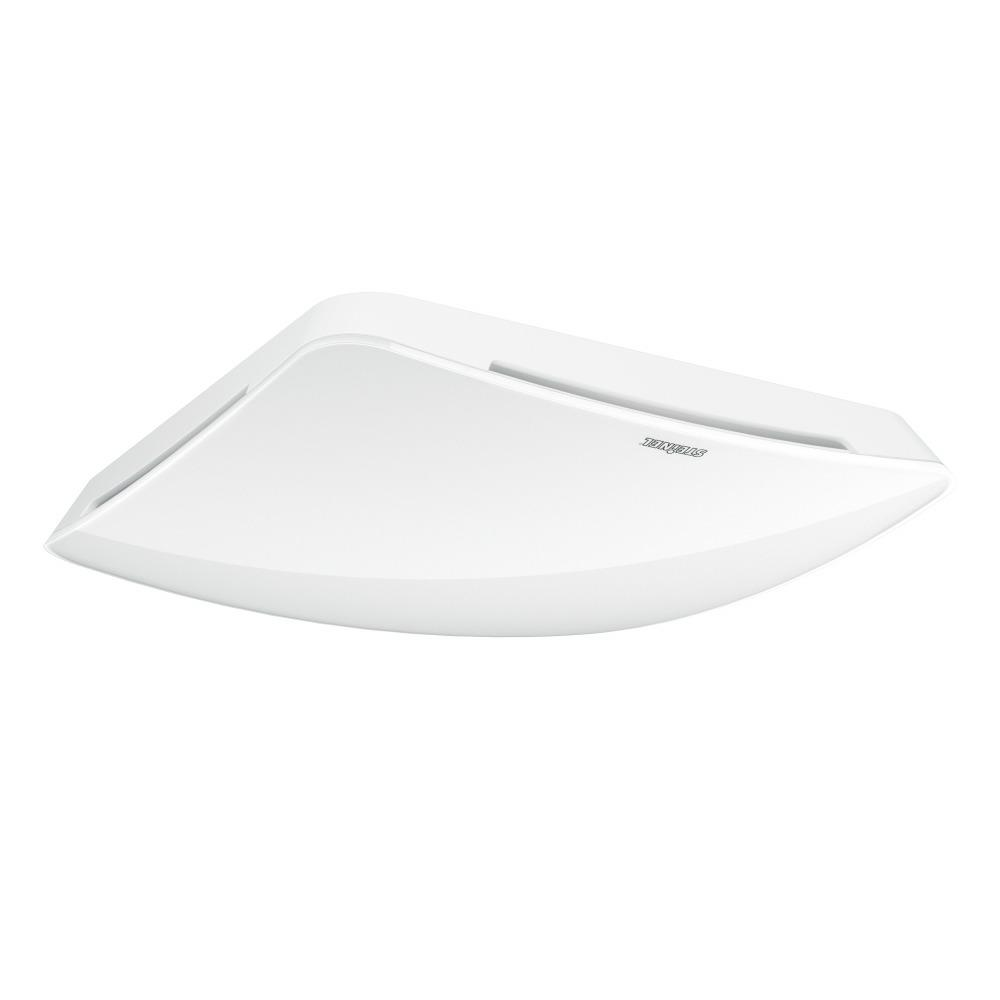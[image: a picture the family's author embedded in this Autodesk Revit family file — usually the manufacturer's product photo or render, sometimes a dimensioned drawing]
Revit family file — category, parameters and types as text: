
# Revit family: truepresencemultisensorknx_056353
name_source: partatom
category: Electrical Fixtures
revit_build: Autodesk Revit 2016 (Build: 20151007_0715(x64)
units: mm (PartAtom-declared; Revit-internal decimal feet)

## family parameters
Cut with Voids When Loaded = No
Host = Face
Maintain Annotation Orientation = No
Part Type = Normal
Room Calculation Point = No
Round Connector Dimension = Use Diameter
Shared = No

## types (1)
- True Presence Multisensor KNX
    Apparent Load = 0 VA
    Default Elevation = 1800 mm
    Description = Type: Presence detector; Dimensions (L x W x H): 33 x 123 x 123 mm; Mains power supply: 30 V; Power consumption: 1 W; Sensor Technology: Multisensor; Application, place: Indoors; Application, room: classroom, lecture hall, one-person office, open-plan office, conference room / meeting room, hotel room, care room, duty room, recreation room, sports hall, reception / lobby, Indoors; Installation site: ceiling; Installation: Concealed wiring; HF-system: 7,2 GHz; Electronic scalability: Yes; Mechanical scalability: No; Mounting height: 2 – 12 m; Optimum mounting height: 2,8 m; Detection angle: 360 °; Angle of aperture: 360 °; Reach, radial: Ø 15 m (177 m²); Reach, tangential: Ø 15 m (177 m²); Reach, presence: Ø 15 m (177 m²); True Presence reach: Ø 9 m (64 m²); Twilight setting TEACH: Yes; Twilight setting: 1 – 1000 lx; Time setting: 0 sec – 1092 min; Basic light level function: Yes; KNX functions: Comfort, CO2, Photo-cell controller, Basic light level function, Light level, HVAC output, Constant-lighting control, Light output 4x, Air pressure, Humidity output, Presence output, Day / night function, Dewpoint, VOC, Temperature output; With bus coupling: Yes; Settings via: ETS software, Bluetooth, Bus; With remote control: No; Interconnection: Yes; IP-rating: IP20; Material: Plastic; Ambient temperature: 0 – 40 °C; Colour: white; Colour, RAL: 9010; Manufacturer's Warranty: 5 years; PU1, EAN: 4007841056353
    Height = 0 mm  [stored 0 ft]
    Length = 200 mm  [stored 0.656168 ft]
    Manufacturer = Steinel
    ModVariant = No
    Model = 056353
    Number of Poles = 1
    OnlyDefault = No
    Power Factor = 1
    Product Name = True Presence Multisensor KNX
    Product group = Presence detector
    ProductGroupID = 4
    RLX_Detail_Level = 1
    RLX_LegendID = 6.1
    RlxData = Q
eAHsfQeYJUd57VWWVjkAQhLSSigiqdVd1d3VtbMzuyOtAihngkAorBWQhNigQDAiySIHy4AJ
JhjZGNmAbUzc1ZLs50w0JsOzMQ8DlrEf8AAD+86prhaD2JWmh7uzde+c/faf+uu/9VdXd5/u
0391Vdc2g40bB/i38echoRr+7dwpSDfiX5c99KxOa33o18lgcNsyyAaUCH+C48aN/77dfoOT
nnr95dfccNmaa556wxlrr4d2zaqVO++4I12PumCwarB2sHKweHAOtJWD1ZAbBlcEy5n45brB
msE10bp68FSUWTw4fXDW4LFIjx7kg2pQDyz+WuSPGXwYW0crwr+ZO7EdLBs3fne73QZnXHPV
1WtOvv6aNWtWoqpt2IZFqwaXDa4cXPpLtS2HB4X/frmmbVHTv2+3/eDMlauv3maPUEMoOd0W
/qXS2wy2j9bvdc2K+c0lvcodvONzfocH/AH+tfXtHUo86ZjB4CRoz4X88GuXrYdMnvSPd058
4NOXrn/dQVdM/mT3V068+g+vX3/1nadN7rrz3RM/OG/1+lurjy/d7sj3Tlx6gFn/tM+vX/qz
Y3YP+jee+Zp11F/63nvXLfrn3z/8e6//3mHUz3nMD9Y9dZ/tDo/6Uuhvi/WvZ/1HHbh2/Qmn
X/DOA/78AxOxDevZhrjd9TO2u47b/eBHTlv/6K9cv/5LB941cfmlH193+otXr793/3dPvPCO
O9Ytv7JazzbAvrSz/8Pf//3Szv6+M66Y/Kdtn7z+x6tfPLHPV/9naWzb28655bwl1N/6/n89
DPVPdvWv/dM8m7pg7fqXvv7PQ/3/tDSbPPGH/7UktmFyRhsm2YZYfpLlYxuCPdYZyj93r8sn
Kecf9fIJtq2rM7ZhKdsQ28Zjdfh7by8meZy53TP3uWHylntPm/yfE980ce9HV0/+wx0fX7rr
Ie+YeOtL1k7u/7rT33nca/5kguV5Llie9TzWv+cInovou77z/cc7Pr6Ovnd97QnrIZOL/vmR
S8868Or1f/pvJwX9VYueuv7F73/uUtqjjvN6X5n11KNv0OG3/mz40w6/dfSJevCnzrq7Mtwm
/Wk/6ui71lFm6GG7rBNtmoz2UI466pjkb9SxnUlub4YefFEfywc9lg/1sA1dnbENwc59ZV2s
J7Y/6DwvB57wxCO6S2obKNtGoc47CYU6r23qTHeIQn3HqDPdCcKyvIfwNwr17rddoHe+1BfF
PFPWvStkNwh/o1Dnb0x3j/oeSPnbnlGo7xV1prz6KdT3iTrTfaNQ3y8K9YdEoU4f5plyXyjU
uQ36PxTS1f8w6GwD94/7vH8U6g+POtMDohwYbSxH/aCYZ/qIKAcjPSTqTLs6qS+OeabcJsse
CuFvFOqLY8rfDotC/ZFRZ3p4FJ70rgz1I2Oe6VFRqHfHinp3DKkfHYX6MVGosy76sz2sn/+I
qUdFoX5stPGcU6dQPy4KdZ535pkeH4U6ccA80ywKdWKE+Dkh6sxTZxnaeQ6Zp1AnjqgzzWO6
Z9SZp15Eoc7zzTxTE4U68cA8UxuFOrHC41VGnXnqLMPtchtd+6lXMc+U+0eh3h0T6nXMM+2O
G3UX80x5nFkf20ofCnW2kTrTJgp1tod5pj4KdbaV+SWQrjz1iZhnujQK9cmoM52KQn1Z1Jcj
7cpTn455ptwHCnXuA3W2ldulD/PUiWVeK6yTQp3bop154ptCndsmRonNbr+ocx8o1IlV6ky5
DxTqvEaoM2U9FOqsm8dlXwjrps6U9e8HeQiku3aonxjzTHk9UKgvjkJ9x6gz3RlCP953+BuF
On/jvvJe0R1b6sujUD8w6kx5HCnUD4g6Ux5bCvWHQ/iPeNkmCnXaKdRZ9kzIzH9HvvTKew75
+Vs/9H9feOuGT3z2mnsevt9V779l6a0bXvz8i+/5wvRHP/izk57e6Uuov3rp/vd87C0vXvKO
o561wRx/yD3v/fzLlx7xhWdu+ND3D7/nK9ucv+7Otz5zw9OecfE977v49gmWP/AFF9/zpX+5
M/h+7tYr73nTPT+amLGthtt69B8+7Z59y22W/L+P37Lh4fv9H8d20H70iScueSX8Wc+F2/3w
g+97Xqvfdupvf+iCW1v9rSees/Qjbz/kHrbhp2/f+UMf8fvfw7b95J8vXnfrvYffw/a8/GPH
fOgHn2zrfO3rV3/w37900z2PWH1LV2aKZd71N38z8d27L5n6xk9u3fDMN5498e3l501d+OKn
b/ig3WvJoae2emzDFNvzzX3/9UP/6662/Fv+8H0+2+nMqe988ukbfv6WXZdcNLn/FNtwycPf
vnSnfzx4im179MMOmbr1r38nHKvP7zM5tc/bBksPfM0zNvzfE8+bWvvKYz/EbZ2H7fDcUH81
6qDOer7+5kOmTnIXrWM95/7ZJVMXvuzuCbbzuGMv2nDYjV+a+tifvnPqrr9bs2Fw6OrJx/35
q6YOevaqDQftd/bkybu8derbu9+84aqnvGHpik+8YOotZtWG8mVnL3nO5++a2nfvmzds+5Pb
19G+/R2rNvzBk1asZ/lFn1uz4X9fd/V61pPfetGG50998R7WP7H2S/d89ZiLNlBf87Tr1y/5
1JoNLHPSxWev3+0vVm1408fePPWuT7x+3X9//aYNTzrgt6ZOeNJTP/gmbI/bOvu6Vyz9k39p
7St+cOrk1Ifa8r9z5aWTq7/a1nP45/5z6tg9LtxwxmdfM+WWf3HqI7e02+IxaP/dtuyfnval
qfWPumgZ23D+LRct+870F8O+f/7Ta5ad8pdPCW3+/jtXLXvmEy5az/Zc+NWbltmX372O7dnu
2lW8jQze99tvm/rM/75p2TYHv3op7ce9f9Wyx/zB6ZMs/50vr1n2+b0uC8fwTGznjtVfCvse
G4Dktg0Pefi1k6s+u2YZ9/117zhv8oQ/W7WMvnd+5a6lZ33tpmWhzpu+tuSlZtUy7vtpT7p9
3f7faO3/8JYV63+wvi2///rL11/6pbae3zvpi/d84+Z2v3jtbgshZ24P2SEK7xnUef/gfYWc
twhCLiQ3kjPJfeQ2yl4Q8tY+M4T3ue6+9lDoD4PsH4X3CN5HeI/h/Yf3JwrvxUwPgSyGHBrl
MKTd/Zn3Ut5naevsR0Kn8P7Jeyrvz7wHkefIgeTDji/Jn510XNdxGe/J5A5yBu9f5A0/T7IE
26FMRFmKdBLCC5NgWg6ZhpwIOSnKCqQPJCfj91Mgp0JOgzwa8hjI6ZAzZsgd0D8GOfs935l8
2Ou+M/mod3578jL33ckTX/dfkz//r69O/tX13598yQfunjzoM5+ZfP3id0weOfHDkP/WtbtO
Mc90t98+ZnL3Aw6YcmevDel7HveDpR/9ycZQD+27/Px9k59e895J2ln/WZ965QTrox/LMX/T
BT+YpP8bv//zyX+96/UT79jjx5P37GuXcnufrvadvO7Ir03u/dJ7lyz/6t2T//Cub/r//vYb
Jh/6kWcv/fil+4b8uqP2DPn8iFdNfOzKd0x8vvzPpdzeKaeuCtt996RdSv/DXraWh3bws68e
OfXpv/rU5PKP7DA1jX29aOUhU9zXe7/nptiWFzzznJB//eJrw+9vX3Pj1Fk4Rr/1onOD39s+
2oT9+tL1F4d0+XlXhuOxbs3qqeMP/drke/a+YymPz4e//J9LmB+8+5v+Bf94d9g295O/c//Z
TubP+NiNU2w366Gd9Uy/rlhKf6b0/9+77hvK83iecvONU6d9/M6JJY+8duqFu9098d0f3DDF
OO3yH10d0m1+65ypP8rfO/HFC08L+V1+7qau/rsPTHzu7UeF/LtvPiT8fvaOO4X8zV/aIdTz
2T02TrLeI3bcJtiJC+Z53l54zCsnvvDeb4UYkOfj1UfeNfGxD3055HlePvPDd02856bXhzyP
86te+ecTX87KkOd54u8/etUpIf7k+aA/z9ctr3nxxJvX/MME28/6p5/1d6Heq995/sQtn7sX
5+jkpe/d622T//Ghwyaff8Z/T97wExvSZRe/fpL2Z//w9ydZ7qw3fHmS7dn2ffdOsp4rXvOt
SbbnM1/4myVsB9PP/+SwUA/bwfqf/IOLJlg/t8/tfviqTy5h/UxZP8uzfpZj/fRj/SzP+lnv
Hsf/d9gOU+KkMS+fIG64f5/6VnteTvlOe15u2/Z1E/w9/9Tfhf09Def295e/KbSB+58BK8zf
Dqx8fa93hG3SzrYw/YvHrZ18091/MsE2Mv8vwATLvfUN7XnheeLxJO6JK6bd9cc8r0PmiW+e
jw2ntfgg7nm+DvrdFh+8Hvj7nT/cMeCA1wn3h9cn8bDox4Ng5/VLXPCa6jhl26iTWyi0dxxD
fiG3UKiTY6gznck1/I1C3uFvM7mH5TvuoU4OImd1PMTfKOQk/saUnESdvEQO4/MyhTo5inrH
VeQr6uSsjru651vayF8U6uQxCnX6UGfK9lKocxv0J9+xPgq5jtvk/pFfyX8U6uRA6h0XLoZO
PuzKUCf/Mc/0kVE6fmSePNmVp35kzDPlNln2KAh/o1Dnb0z529FRqN+fU4+DjbxKnqVQJ8dS
Z9pxLPXuWFHnMbg/79JO7qVQZ130ryCsr4Y4SBOFOnmZKTmTOoU6QUihTg6l3nEpb7zUpyDU
mZJbKdSXQ6YhJ0adeer8/STICsjJUaifEnWmp8b8aVFnnjo5l0L9MVFnSg6mUD8j6kzPjEL9
LMjZkHOizjx1ljkXch7k/CjUL4g60wujUL8oCvWLo870sVGoPy7qTB8PYX1PgNCHQv2SqDN9
YhTqT4o600ujUH9y1C9D2pWnfnnMM70iCvUro850ZRTqvxH1q5B25alfHfNMuQ8U6twH6mw3
t0sf5qlfA7kW8pQo1K+DXA+5AfLUKNRvhDwNsgqyOgr1NVGor40605uiUL856kxZD4U6678F
ciuEdVNnyvoPgBwIIfYp1J8edaZVFOrPiEL9mVFn+iwI/XaD8DcKdf7Gff1NCPeXQv3ZUajf
FnWmz4lC/blRZ/q8KNSfD3kB5HbIb0WhTjuFOsvz3zZtEraHLS1jfttoa3+7jZfZfTYTfmvL
bQf9F+VvW0a/zlbOKLc9dP62Y7SxTGejzu0yvwOk+4026p1tEfSuHOth+Z1oQjmW6WzUaWOe
vzPP89uV62w7RxvbT53lD4g21t3Zum3wd9qYJ45YH/VdILQ/DNJto7MxpY0p28+U57wr19m6
feP+Uqfw3spy5AP6MJ2AdPV1tq4+1s0ylEkIy7Ee/k7ZHUJbpzO/JNpYjnkK7+XdNvaARpmi
Ke7HntBoY0pbpzNdTlMstxc0lumOC/XOxpTlmO4N6VLaWK6zPRx6V26faH9ItLFMZ2PKckz5
LNGltLFcZ9sfelduv2hnShvLdLbjo431cHu0d9vtdKY3QujL9vN3ykMhtBEbtDPfHQPaujK8
J3XbZRm27VSaYps72ykzbKyHx2RFtHXHl7YTo414Zl3EMu83rI/47GyPjDaWox/L3AZhOZbp
bAdFG/Osi3nei7pyne0R0dZtj3ne07pyrJ+2g2nCNphnXcw/HdKV62yHRBvz9GP+lmhj+zrb
odHW1b0Y+SuijXXTbzHkcAi30fktRq7zZX0sx/xhEJbr/Jg/ItpYbjGEtu748ZjSxvxaCH25
XdbFbR4J6errbF19i/ELbcyTXzpf1k+/o2hCfSzT2Ypo4za4TZZZGW1du2g7OtpYhu1g/vpo
Y7nOdky0Mc92MP+UaGO5zvaoaGOebWM+j7aubbQdG21d+5k/bkY5to22bj94/bAsy3TXG20s
R1t3bfG6ZDmWySA8Lsxzv5g/AUIby3W2G6KN5bhfLNO1mWU621XQ6dvtK8tcE2089mwL27sq
2rZFyn01EBttTDrbs6ON5bivLFNGW3eMaDsn2rZDynIsU82wcf+Zr6OtO5a0nRVti5CyHMu4
GTYeJ+abaOuOL21nRNvuSFmOZfwMG48n80uirTvmtJ0ebbshZTmWWRptuyLlMZ6ATEYby3W2
rhz9aGP+0RAe+13wlzb6TUFo2wN/aWN+GaSz8fwwvxxCG8t0tq6+PaNtOdJpCMvRxvPI/IkQ
2ujX2c6NNt5faWOZk2bYeL6ZXxFtLNPZzou2vaONZU6eYeP5Zv6UaOuwQ9sF0cZ7PcuxzGnR
ti9S4uJUyA3RxnKdrStHP9qYvwjCfeNx5v7xmDwG0u0v8cN8t78s19m688tzThvzHV6Oizbm
z4SwPpYh9pi/DEIby3W2s6Lt2Ghj/uxoYxnikfknQ+jLcp3tnGjjNUMb88+JNh57bpv70B17
HlPamD8fwvpoI76Z744zy3S2rs08frSxzIUQ+tJGzDPfHdPuWqHtYgjL8bizHMs8FUJbd/2w
zNXRRl9eL7Q9NtqY5/XC/LXRxnKd7XHRxjyvF+YfH20s19kuj7bu2mOZ66KNZXhd0faEaOuu
M+YviTaW47VG2xOjjeV4rbHMb0Rbdz3SduUM23Lo9Ls12ljfcghtT4LwuCzHX15/zD8DQhvL
dbZLo43YoI35J0NYjjaWpa3bX+KC5Z4MeRakK8djcxmkK/cI6NyPKyBdmw+eYVsJnb4sx/1j
mVsgtD0Sf+nLMt0xoG0y5q9HynLH4C/PO/mkO+dHz7B12GA5nneWuQZC3yPwlzbmOxzQNhHz
T0HKcofjL23Md+eXNraF+a4t3C5xeQOk2+5DoJPLboQ8DcL6aDsRwvxNENpYprOtirZDo435
1dG2ONqYXxNtO0Yb8zfPsC2GTtvaaNsJKbfBbXblDoLOY8/j3mGItuUx/3SkbN+B+LscwnyH
IdqIA+afCWG5A/CXNuafBelsxAzzv0kTyj0cf2lj/jkQ2rbBX953ns0cpCtH222Q+8ptPOTZ
GFn6g0t/vHHDz57905894V83XPKzjRu/87cwnnDaXi9b3Dz36ztv++2fbNz4iR12OXXjxg3l
fvDu/j3xtbcvP+6VO7CRgzs646DX2Mn7vDav9K+PR737xyNB2fw/nvO/P9Gg0A63bbMHxpVi
OO1y2Hh++W/nNgl/0xpJ2gA2ZMhLIDNH2N10iJ9cdvETJoud/5ijBTniL/Tkf+Z/nT1JoX3m
6DyWpc8M+3r2/M8c5RfLrGeZr37jssmf7Xnzuk7/6Z43L6Uey4e3L3G7oZ643eDLdnajEWM7
O/smRzKizHpsO5TBdtZh20GPIwdD/dx+Z8e21lPYHvrRn/o9+7xhHSW2ef2M9q/v2h/LhH2J
vpMsH9sQ9Fh/0FE+1Bvrpx58Y3tCmdjmoOOYcNRnaHMc9TlTn4zHfJMjQKNvKMNRmN1oys2N
oLzf6M77RnFG+1Jua+ZoTcKb18m2UahvF3Wm20ehvgOEVw3vgrw6KNR3iUJ9URTqu0adKX0p
1FnnbhDWtXsU6qxvDwh/2zMKdZbZC7I3ZJ8o1PeNQp33J+aZkh0o1Lt6qLPuh0JYx8OiUN8/
6kx5V6VQ552YQp13aupMeZ+hUH9E1JkeDGF9bAd9KNTZFupMD4lCnW1jnml3PKlzf5nnce3K
U+exZZ7p4ijUeVyZZ8rzR6HOc0b9UMjiKNQPizpT7gOFOveBOtvK7SyGME+dx5/79sgo1Hks
mWd6eBTqPLZHQI6EdMeKenc8qR8V80y7Y069Oy/UWefRENbFY0uhzjqPgfA3tplCnb/z36Mg
20Shzn2mUOd+UqgfG3WmXT3UWTf3i9vnflOoHxd1psQchfrxUWdKnFGoE28U6sQ3dabENOvj
PtKfQp3HhTrTLAp17jPzTNk2CnXuM3W2uStPnfvGPNMTolDnP+b5b/so1LeN+q5Iu/LU2W7m
mbJdtO0U87RR5/5wWyzHMjx/M/9tbsTTix62dtlOl1y0/qZrXzn1gbvWLqPPuYe+YuqPF69d
9hGMZqJ95gimmSOqdl96/vrpA9ZuYJm1WfXBv7hr7Qb6fuKvzprc4+DW/os23LZs5sivmSPC
fuPAtRv+6Zvnhm39Mer4zA/fsoT1XHj42g0ri1ND22aOUJs5yulHz3jc5N/st3YZ27Djy366
5HexD/R9x+2nrV/2yNY+ow0bOjzyWFN4bVK687ADdAqPJ4XHlrJzlF2QUhZF4bmYD9kN26Hs
HmUPpJQ9o3TXR3c98L7Q3QO7+zGvB97vKLw/zIecgu28CPKCE6+cQjLY75WXTT3Wl0v3Wn5t
yK9bclXIv/vxvzvB3/fa4ScT/H1w+3FLmd/5jRdjNke59PCnf2GS+YdWrw3piod9dpL29171
6pA+6ZQipL939/Hh9yVr/y2kd177tWBnuh/qpl/5xjdO7FP82+Qi1H3YC39v8vbtDp289+Zv
TV6KOpiyTtopLEcfCnXWQ2GZrzzpvAlulynroLC9rD+HsH7uD7f7dZRh/Uzpy7Ksn+VYN/1Y
P8uzftbbtYXpK978o7A/9d0/D/vzmTO3DcfvpI3bh+P38zedFPJnfeDEkH/89w4LeTxnhDyP
x7twjL9w53cmd8Cx5fH82XO/smT/T7x58nU3H3Sf8LjTPnjeV5awHM8L/f5t0X9iVMrxk0x5
DuhHYX1HoC7WR53bobAMy/J8MOU2WJ71sxzrpx/r785Vd265HZ5rXqvddUq9u05nXp/Uu+tz
5nVJvbsuqXfXD3VeQ9211F3ftPF65zXFa727rqjzWudvvEd05alz2/z9gbbLetmObpub2y6v
X1673XVLnddtdw13fNY9x/Aaps5ruLueO86mjc8OzDMlr7M+8j59KN0zFHU+W3TPB9QfEfNM
D45Cnc8fzC+GdOWpHxrzTA+LQp3czTzTw6NQPyLqRyLtylM/KuaZdvcm6twH5tlWbpc+zFPv
zk93P+S54rk7GnIM5FFRqB8L4b/jINtEoX58FOpZ1JmSSynU6Uuhzjq3hfAfMUnhP9bJ37jt
rnzXDpgecLvdtro2bG67OeopICYKdRt1psQihXoZdabEH4V6FYV6HXWmDsL6Ggj9KdR91Jku
iUKdN2zmmS6NQp0XL/O8AXXlqfPhgnmmy6NQn4460xOjUD8p6iuQLo9Cne1mninbSNvJMU8b
de4Pt7UcwjL8x/PDf2zbIPbSbBv07rfb2JxBZ7sw/PbLoxSIR/qyDM8762zLtyMNto/5FhNt
uc7W1cffeO9g2tXHMp2N54/b4D1nJwh/ezyENuaJ+a58V66z7cpisRzrYZ2shzaW6WyHRRvr
4zXTbYvlWKazPXJGOdbN8o+LNpbpbKybvtwebd22OhvL0nYEhDa2n+W4rYsgtLENu0FY9tGQ
zkbcdtuijWU6G1PaWDd11nkopCu3BzSW7+qjvme0db4s09n2hU5f/kYb066+7h7N8isgLMf7
Ku/RXR20sVxny6B35Vg36+TvtHX3dtp4L+vK7QeNZU6hCeXo19m4PdqY532/235XrrPxfk0b
62bZbludjeVoOwRCG9vPctzWqRDa+PtDIbSfAOls5JVu+7SxTGfj/aMrx/s2t9PtW8dHtNGH
5Vjm4ZCuDtpYrrPV0LtyB0Dr6qCNZTpbxWKxPnIY6z2OJthYprPRhzbm2a6ujq5cZ7MsFsvx
WLKOY2mCjWU6G+uhjXlyI/MTkK5cZ/PRxuPLtnV1sByPB21dHZ2N54b+3Tlimc7W7RvPL22U
xRD68lqgfTGkwy5tXZnu2ue1Rxvz3XXO64w25g+HsD7aFkOY767fri7ajoewHK/9xRCWORJC
2zb4SzvzR0E622JotB0N6WxsK/OTNMF3Mf52tmNogo15tpf5KUhXrrM9Ktp4HmhjvjtvtC2O
tq7NPOYsxzLLIayP5bh/PMZdOV4LPCa8nrtrgddoZzsROn2JY9pYJod0Nh4n5rvrozu+tHW+
xDbLsYyD0Lc7lga5M6ON2OGxo63DKW0sS1uHNWKW5VimhLC+7jwwf3q0sRzPDW3ddcTrgjbm
u2uQ7aON+a59bC9tzD8G0rWZ57GBnE0Ttkscs320de2jrSvXXTPM89wugXS+PEe009aVo60r
Nw2d2+Bfnu+lkPOZgW0b/O1sHa6IIdqY7zBEDNDGfKgIvswTF8yfC2F9LNfZltMEG9vS4adr
C9tGG/PnQFhuL/zl8eL5PglCG/PEGfOPgXTlOtuKaNsbKW3MnxxtHT6Zf2y0sRwxS9sp0cZ7
NW3MnxptvN/Txvxp0bZjtDH/+Bk2lqXt0dHG881ts72nRxtxRRvzZ8yw8XphvsMuy3S2J8Ry
xAVtLHPWDBuPIfMdDphnOdq6Y8pjTBvz3TnieaON+fMgPKa08ZpkvsMGy3S2ri0wBRvLXMAM
fPl3ewjzFzIDG/P0pe0iCG274i9tzF8M6Ww8zsw/jiaUY57laOvOG48Lbcx3bdkJOsvSrzsf
26x94j/j/+onvmLxQdM3bv+Rvbf/7NpJWtZOvyJkd7ojcDNcwr+1//Li5Xfst0uA5R2dMYF3
hLxmZv+PyGzfEbY+/d9JPvC2+tXH63jjxm9tt/vg/Fuvv/yp161YddnN19xw1U1/W2zTbua2
Zd+dOGHqdz5/Mu4mpEUWXhQLn3LZFSu3Y7GNfJjmh2CuffVX1tFw7VtesnSmvnjqZ7zj/ZL9
LfjoSVeGOj7UEu5qrKfT6bPoNm4Dm8BD98xtnLDdCevfdu/kepZ56uc+te6S21YG/adn7LqO
H32h/Rv77L6006/4wKeXdmX+aM0Jk53vzHbQp90eN7hDqPfDB7yTd+Gg/2TVHqGNG665dN1M
/faPnhnsbEen/3Jd2w4G37+86eqivulyOw3+8ITLlnblqHfbYfs3Z59ZpquXvp3OtnT/FnVK
SDdu/I/tth+cdMZFp/OE84X1zH87z8i84AevW06ZYQIkinBX3/bYnSav/z//E44Bf5+Zv3qb
v4CFtx7Kk8PlG8H1S1VtPtNS3y9+D7ex5XjIgdwGeTPkw5CvQ8hSe0EWQ3LIcsg5EG73Rsht
kDsgr4C8FvJmyNsh74a8H/JhyF9DPgn5POTrkG9Bvgf5EYSMtz1kZ8hukL0g+0H2hxwEWQw5
HHI05DhIDikhDWQpZDlkBeQ0yBmQcyAXQB4LuQTyZMiVkKsh10FuhKyB3AJ5JuQ2yHMhz4fc
DrkD8iLISyAvg7wC8irInZBXQ14LeR3kDZDfg7wZ8lbI2yB/AHk75B2QP4a8E/JuyJ9B3gN5
L+T9kA9C1kHugXwY8lHIxyF/BflryN9C/h7yj5BPQj4N+Szkc5DPQ74I+TLkq5CvQ/4F8g3I
NyHfgnwb8l3IvZDvQf4b8n3IDyE/gvwE8lPIzyF8utgGsi1kO8j2kB0gO0J2guwM2QWyCLIr
ZDfI7pA9IHtC9oLsDdkHsi9kP8hDIA+FPAyyP+ThkAMgB0IOgjwCcjDkEMhiyKGQwyCPhBwO
OQJyJOQoyNGQYyCPghwLOQ5yPCSDnADJIQXEQCykhFSQGuIgDcRDlkAmIEshk5ApyDLIcsg0
5ETISZAVkJMhp0BOhZwGeTTkMZDTIWdAzoScBTkbcg7kXMh5kPMhF0AuhFwEuRjyWMjjII+H
PAFyCeSJkCdBLoU8GXIZ5HLIFZArISshvwG5CnI15BrItZCnQK6DXA+5AfJUyI2Qp0FWQVZD
1kDWQm6C3Ay5BXIr5OmQZ0CeCXkW5Dchz4bcdtLgNsjgOUghg+cihQyehxQyeD5SyOAFSCGD
25FCBr+FFDK4Aylk8EKkkMGLkEIGL0YKGbwEKWTwUqSQwcuQQgYvRwoZvAIpZPBKpJDBq5BC
Br+NFDK4Eylk8DtIIYNXI4UMXoMUMngtUsjgd5FCBq9DChm8Hilk8AakkMEbkUIGv4cUMngT
UsjgzUghg7cghQzeihQy+H2kkMHbkEIGdyGFDP4AKWTwh0ghg7cjhQz+CClk8A6kkMHdSCGD
P0YKGfwJUsjgnUghg3chhQzejRQy+FOkkMGfIYUM/hwpJPzT/Vn3522Bhe0g20N2gOwI2Qmy
M2QXyCLIrpDdILtD9oDsCdkLsjdkH8i+kP0gD4E8FPIwyP6Qh0MOgBwIOQjyCMjBkEMgiyGH
Qg6DPBJyOOQIyJGQoyBHQ46BPApyLOQ4yPGQDHICJIcUEAOxkBKyYvqunVZMv/rgFdNfXrFi
+vanr5h+x4YV05fvd/L0J285efqg/zh5evXTTpnebcdTpw+9+9TpHz75tOnPHfXo6X0Gj5ne
4duPmd77m6dPv+X7Z0wf+9Czpo8//ezpE+48Z/ov/+vc6Zdfef508x8XTN/ykoumH3bSY6e/
vffjp//5x0+Y/tz/PBHPGU/+JVlywSXT/rUXTb+2Pnf6m0edMX3bylOnb/n3E6ef+c6p6Y+9
a8n0T79VTy+/yE7v/P0Tph+x4bjpO99zzPTHP3Xk9NR+h0//9a2HTj92cMj0nn9w0HR5zQHT
xWn7T798+qHTPzx/v+kjf3Of6R/ds9f0Ex6y5/S5t+0+/b2f7zp9ySsWTf+93WX6ed/aafoz
f7Lj9P7P22H6Q1dtP108Ybvp71+y7fRLr9tm+kUvHExvd9XG5Ud89mfL//JxP12+9P/9ZPm9
d/94+Zk3/2h5ew/Q37SPgDAtTKeN0P6tE6aF6f6oSdtDmBam00Zo/9YJ08J0f9Sk7SFMC9Np
I7R/64RpYbo/atL2EKaF6bQR2r91wrQw3R81aXsI08J02gjt3zphWpjuj5q0PYRpYTpthPZv
nTAtTPdHTdoewrQwnTZC+7dOmBam+6MmbQ9hWphOG6H9WydMC9P9UZO2hzAtTKeN0P6tE6aF
6f6oSdtDmBam00Zo/9YJ08J0f9Sk7SFMC9NpI7R/64RpYbo/atL2EKaF6bQR2r91wrQw3R81
aXsI08J02gjt3zphWpjuj5q0PYRpYTpthPZvnTAtTPdHTdoewrQwnTZC+7dOmBam+6MmbQ9h
WphOG6H9WydMC9P9UZO2hzAtTKeN0P6tE6aF6f6oSdtDmBam00Zo/9YJ08J0f9Sk7SFMC9Np
I7R/64RpYbo/atL2EKaF6bQR2r91wrQw3R81aXsI08J02gjt3zphWpjuj5q0PYRpYTpthPZv
nTAtTPdHTdoewrQwnTZC+7dOmBam+6MmbQ9hWphOG6H9WydMC9P9UZO2hzAtTKeN0P6tE6aF
6f6oSdtDmBam00Zo/9YJ08J0f9Sk7SFMC9NpI7R/64RpYbo/atL2EKaF6bQR2r91wrQw3R81
aXsI08J02gjt3zphWpjuj5q0PYRpYTpthPZvnTAtTPdHTdoewrQwnTZC+7dOmBam+6MmbQ9h
WphOG6H9WydMC9P9UZO2hzAtTKeN0P6tE6aF6f6oSdtDmBam00Zo/9YJ08J0f9Sk7SFMC9Np
I7R/64RpYbo/atL2EKaF6bQR2r91wrQw3R81aXsI08J02gjt3zphWpjuj5q0PYRpYTpthPZv
nTAtTPdHTdoewrQwnTZC+7dOmBam+6MmbQ9hWphOG6H9WydMC9P9UZO2hzAtTKeN0P6tE6aF
6f6oSdtDmBam00Zo/9YJ08J0f9Sk7SFMC9NpI7R/64RpYbo/atL2EKaF6bQR2r91wrQw3R81
aXsI08J02gjt3zphWpjuj5q0PYRpYTpthPZvnTAtTPdHTdoewrQwnTZC+7dOmBam+6MmbQ9h
WphOG6H9WydMC9P9UZO2hzAtTKeN0P6tE6aF6f6oSdtDmBam00Zo/9YJ08J0f9Sk7SFMC9Np
I7R/64RpYbo/atL2EKaF6bQR2r91wrQw3R81aXsI08J02gjt3zphWpjuj5q0PYRpYTpthPZv
nTAtTPdHTdoewrQwnTZC+7dOmBam+6MmbQ9hWphOG6H9WydMC9P9UZO2hzAtTKeN0P6tE6aF
6f6oSdtDmBam00Zo/9YJ08J0f9Sk7SFMC9NpI7R/64RpYbo/atL2EKaF6bQR2r91wrQw3R81
aXsI08J02gjt3zphWpjuj5q0PYRpYTpthPZvnTAtTPdHTdoewrQwnTZC+7dOmBam+6MmbQ9h
WphOG6H9WydMC9P9UZO2hzAtTKeN0P6tE6aF6f6oSdtDmBam00Zo/9YJ08J0f9Sk7SFMC9Np
I7R/64RpYbo/atL2EKaF6bQR2r91wrQw3R81aXsI08J02gjt3zphWpjuj5q0PYRpYTpthPZv
nTAtTPdHTdoewrQwnTZC+7dOmBam+6MmbQ9hWphOG6H9WydMC9P9UZO2hzAtTKeN0P6tE6aF
6f6oSdtDmBam00Zo/9YJ08J0f9Sk7SFMC9NpI7R/64RpYbo/atL2EKaF6bQR2r91wrQw3R81
aXsI08J02gjt3zphWpjuj5q0PYRpYTpthPZvnTAtTPdHTdoewrQwnTZC+7dOmBam+6MmbQ9h
WphOG6H9WydMC9P9UZO2hzAtTKeN0P6tE6aF6f6oSdtDmBam00Zo/9YJ08J0f9Sk7SFMC9Np
I7R/64RpYbo/atL2EKaF6bQR2r91wrQw3R81aXsI08J02gjt3zphWpjuj5q0PYRpYTpthPZv
nTAtTPdHTdoewrQwnTZC+7dOmBam+6MmbQ9hWphOG6H9WydMC9P9UZO2hzAtTKeN0P6tE6aF
6f6oSdtDmBam00Zo/9YJ08J0f9Sk7SFMC9NpI7R/64RpYbo/atL2EKaF6bQR2r91wrQw3R81
aXsI08J02gjt3zphWpjuj5q0PYRpYTpthPZvnTAtTPdHTdoewrQwnTZC+7dOmBam+6MmbQ9h
WphOG6H9WydMC9P9UZO2hzAtTKeN0P6tE6aF6f6oSdtDmBam00Zo/9YJ08J0f9Sk7SFMC9Np
I7R/64RpYbo/atL2EKaF6bQR2r91wrQw3R81aXsI08J02gjt3zphWpjuj5q0PYRpYTpthPZv
nTAtTPdHTdoewrQwnTZC+7dOmBam+6MmbQ9hWphOG6H9WydMC9P9UZO2hzAtTKeN0P6tE6aF
6f6oSdtDmBam00Zo/9YJ08J0f9Sk7SFMC9NpI7R/64RpYbo/atL2EKaF6bQR2r91wrQw3R81
aXsI08J02gjt3zphWpjuj5q0PYRpYTpthPZvnTAtTPdHTdoewrQwnTZC+7dOmBam+6MmbQ9h
WphOG6H9WydMC9P9UZO2hzAtTKeN0P6tE6aF6f6oSdtDmBam00Zo/9YJ08J0f9Sk7SFMC9Np
I7R/64RpYbo/atL2EKaF6bQR2r91wrQw3R81aXsI08J02gjt3zphWpjuj5q0PYRpYTpthPZv
nTAtTPdHTdoewrQwnTZC+7dOmBam+6MmbQ9hWphOG6H9WydMC9P9UZO2hzAtTKeN0P6tE6aF
6f6oSdtDmBam00Zo/9YJ08J0f9Sk7SFMC9NpI7R/64RpYbo/atL2EKaF6bQR2r91wrQw3R81
aXsI08J02gjt3zphWpjuj5q0PYRpYTpthPZvnTAtTPdHTdoewrQwnTZC+7dOmBam+6MmbQ9h
WphOG6H9WydMC9P9UZO2hzAtTKeN0P6tE6aF6f6oSdtDmBam00Zo/9YJ08J0f9Sk7SFMC9Np
I7R/64RpYbo/atL2EKaF6bQR2r91wrQw3R81aXsI08J02gjt3zphWpjuj5q0PYRpYTpthPZv
nTAtTPdHTdoewrQwnTZC+7dOmBam+6MmbQ9hWphOG6H9WydMC9P9UZO2hzAtTKeN0P6tE6aF
6f6oSdtDmBam00Zo/9YJ08J0f9Sk7SFMC9NpI7R/64RpYbo/atL2EKaF6bQR2r91wrQw3R81
aXsI08J02gjt3zphWpjuj5q0PYRpYTpthPZvnTAtTPdHTdoewrQwnTZC+7dOmBam+6MmbQ9h
WphOG6H9WydMC9P9UZO2hzAtTKeN0P6tE6aF6f6oSdtDmBam00Zo/9YJ08J0f9Sk7SFMC9Np
I7R/64RpYbo/atL2EKaF6bQR2r91wrQw3R81aXsI08J02gjt3zphWpjuj5q0PYRpYTpthPZv
nTAtTPdHTdoewrQwnTZC+7dOmBam+6MmbQ9hWphOG6H9WydMC9P9UZO2hzAtTKeN0P6tE6aF
6f6oSdtDmBam00Zo/9YJ08J0f9Sk7SFMC9NpI7R/64RpYbo/atL2EKaF6bQR2r91wrQw3R81
aXsI08J02gjt3zphWpjuj5q0PYRpYTpthPZvnTAtTPdHTdoewrQwnTZC+7dOmBam+6MmbQ9h
WphOG6H9WydMC9P9UZO2hzAtTKeN0P6tE6aF6f6oSdtDmBam00Zo/9YJ08J0f9Sk7SFMC9Np
I7R/64RpYbo/atL2EKaF6bQR2r91wrQw3R81aXsI08J02gjt3zphWpjuj5q0PYRpYTpthPZv
nTAtTPdHTdoewrQwnTZC+7dOmBam+6MmbQ9hWphOG6H9WydMC9P9UZO2hzAtTKeN0P6tE6aF
6f6oSdtDmBam00Zo/9YJ08J0f9Sk7SFMC9NpI7R/64RpYbo/atL2EKaF6bQR2r91wrQw3R81
aXsI08J02gjt3zphWpjuj5q0PYRpYTpthPZvnTAtTPdHTdoewrQwnTZC+7dOmBam+6MmbQ9h
WphOG6H9WydMC9P9UZO2hzAtTKeN0P6tE6aF6f6oSdtDmBam00Zo/9YJ08J0f9Sk7SFMC9Np
I7R/64RpYbo/atL2EKaF6bQROpfWbdz4+1/fZXD+mpXX3LDyut0X2cW7L8ohtubfgtJ02okr
b1551dobrlp9/crrrly5avHJq37jstWrYUCpc05afM55Zy9+9HmLz71w+oILoJ62AuY8z23p
oVywau3KxTeuWrl65Q1XrLx0zcrVa2BccdmatdcjLfKwic385W8zJTSKXtHe5aevu+6qlZev
umztFVevvuq6n1593WXX37hy90WuoPMtFP7JM1ch6ZzDhmO+sxkWC0U9m94VoZmHp4Swihri
IA2E5cJ2itAaFi1YtmDhImyQxQuWL+hQ0MOwakMPQw9DD0MPQw9DD0MPQw9DD0sPSw8bmkMP
Sw9LD0sPSw9LD0uPkh4lPUp6lGEP6FHSo6RHSY+SHuFUVfSo6FHRo6JHRY+KHhU9KnpU9Ki4
jYCVmh41PWp61PSo6VHTo6ZHTY+aHo7bcPRw9HD0cPQIJ8fRw9HD0cPRI6CwoUdDj4YeDT0a
bqOhR0OPhh4NPTy34enh6eHp4enh6eHp4enh6RHOdIdD+hQ5nYqcXkVOtyKnX5HTscjpWeR0
LXJurYinP/gWwbdFQAuBFgNF8G1R0MIg4KAIQCgCEooAhSJgoQhgKAIaigCHIuChCIAoAiKK
AIkiYKIIoChsaHOARRFwUQRgFAEZRYBGEbBRBHAUAR1FgEcR8FGUYX8DQooAkSJgpAggKQJK
igCTIuCkCEApAlKKAJUiYKUIYCkCWooAlyLgpWhvLgExRYBMETBTBNAUATVFgE0RcFME4BQB
OUWAThGwUwTwFAE9RYBP0V7cAUBFQFARIFQEDMVbWUBREWBUBBwVAUhFQFIRoFQELBUBTEVA
UxHgVAQ8FQFQRUBUESBVBEwVAVRFQFURYFUEXJlwZzM5sWECrkzAlQm4MgFXJuDKBFyZgCsT
cGUCrky4r5iAKxNwZQKuTMCVCbgyAVcm4Mq095f2BhPvMMSkae8x7U2mvcu0t5n2PtPeaAKu
TMCVCbgyAVcm4MoEXJmAKxNwZQKuTMCVCbgyAVcm4MoEXJmAKxNwZQKuTMCVCbgyAVcm4MoE
XJmAKxNwZQKuTMCVCbgyAVcm4MoEXJmAKxNwZQKuTMCVCbgyAVcm4MoEXJmAKxNwZQKuTMCV
CbgyAVcm4MoEXJmAKxNwZQKuTMCVCbgy4eZkAq5MwJUJuDIBVybgygRcmYArE3BlAq5MwJUJ
uDIBVybgygRcmYArE3BlAq5MwJUJuLIBVzbgygZc2YArG3BlA65swJUNuLIBVzbgygZc2YAr
G3BlA65swJUNuLIBVzbgygZc2YArG3BlA65suF/ZgCsbcGUDrmzAlQ24sgFXtmWwlsJaDosk
xvuVbWms5bGWyFoma6ks4MoGXNmAKxtwZQOubMCVDbiyAVc24MoGXLUPIDbgygZc2YArG3Bl
A65swJUNuLIBVzbgygZckUjCtct2Qnh3DMyGNHAO0sABoWBggEAA4T4cbqWBOcLNP/BGoA16
6AkAR5DHSk8AOAh6AtjiTwAmi09TSEH1dQ7Wt+3DAX9yZV37wsEeLlaY6rop8DTWlK59HILJ
eY8nrQrPQe1zEky+dh53Y+87P9w0S1eXYLmqfTQzGe5b3le2xrNF+8QIk8tt41xtcS9qbxtZ
mYOPnPO5bx89TVbaxrsKrnXePofC5DxaUaEVeft4abIKZOwM+CX37ZMTTMiDPPGU0T45mawG
u+IxqmIzws0JpgbPE7iV53nL6YXJXGmx13mDPWof/kzW5N6B1eFbt89WMDV5iYdV1B0fk0zm
qwpHE3djVB/uczbLsb/OOTyxtpRV2Awor8DRDs898bk0w4NNXuWVd03cRZuBsTyePfHoEZ83
LQ6NByuWBVrRPobZrMKDIw5E7kCj4R5rsY/eOutcjh0Lx9Rih5rS13DM22cqNKJx1jfgvdyX
7aN8+8TLi/AXGjxdXtUgQ2yxPbNoBdqPE9Z43z6AoLLcVQ3Y3+FktM+fOIbYmRIHyBXx4Rsn
rcbpycFDlW+f0E1WNIAEjlqJZ42w2SID+nCuc+x+2UYXRVYDXAg+ALe8PbUFMIGDjr2ucHTC
ThYZHhqrCjsO2m8fZ/PMe5fj4Neuao8EYl+AA+coJ4DaOCYD1KumdnhOjo+yeVbi4QmxB0Df
tFFBjksDm8cTLw53+zifZzgbeDxsfFG3UZLPcOCxbZzqGqAOIRg2iIajrR6MHHbRZ3WV102J
54O8aQK5e5xGV+OxEMcGpXkgfGaxyzj2zoGIw6Ocx4WXlzhpRDlwHUohznC+weVZlVW4qHwG
zAI1OBf4JRybJvM4voh1rMWxCQ+BTYYGNHioI5yr8ATTACU8ZSjJXeTBaXDkczyz5tbh0Ian
sgYXFS78Ci3B2QyPRE2GI4NnS1TWIFzhbsOEyx+nAo8buD54pTW4/NFEAN+XOBtt9WgA7iO4
FoDB8EjS4Cx63A4CUAHg4AhQoQ6PM5a7aMK1mePOVVYNbk08Eg0uNDy3NLhN4XIJD40uQ3vw
RIZLCrAPz5ow8XLCyfa4x4THZIfrGLcDnAgAsb1zwIT9wU3OAQZABaqHKcfJDsfKo3ww4faG
awPPiziR4RGRTz+SdI8Bbu0iP5GfyE/kNwzyC5GvyE/kNxKkL/JT5IfgTuQn8htN8mMchjDv
QSI/BpZzivwYRSryG9MIVuQn8hP5qdtT3Z7q9hyJaG2Y3cgiP5GfyE/kNyTyG51uz/Y1nV75
jWlQNxuOFPeJ+8R94r4Fx30a75LuOJTZENcwyoj8RH4iP5GfyG/TvZ565TfGkaHIT+Qn8lvQ
5NdOMhjOTIf57/Wc3XiXlsM000HR3syIUeQn8hP5LWjya2fFDYf8widlEpzpMOfBnq2jpvmN
5VgYkZ/IT+Qn8htSt6fIT3PcRye6FPmJ/ER+Ij+R36bf+Sny0zs/fd1MXzcLHKmvm4XPdOrr
ZqP1dTN1e8581yW9jU4V+SnyU+SnyG9kI78tPOBFoz0V+SnyU+SnyE/ftdZ3rfVd69F5p/dg
Ea4iP0V+ivwU+Y1s5Neu8/Bgn/bUVIcHI4KF+LvIT+Qn8hP5jTn56Z3fQiS3B9tnkZ/IT+Qn
8hP5abTnWM7leyACFPmJ/ER+Ir8hkd/8f+FF3Z7j8w7ugYhqS/wm8hP5ifwWNPmxS1ALuWsh
94VHoiI/kZ/Ib0GT35w/b1YG1qxcVZSVy8vamGL+v/Cyhac6bGKSO2NNLG+bG2NdXRnjm6pd
HsnVZVXrCy+jQ6IiP5GfyE/kN6RuT5GfyE/k52vnbZ57n/PZCRRrC1fi0ciUdWX5tEZTWXhf
2bpoXM5nJ5pcbhvn8Px0X6kyN+iScD73uW0LlbbxroJrned8+oRf6bxxviqsyYtoqoytnTGs
u45tqJA3FcqUddxebSqRH46gzRpnfWMLk/sy55ub9jCGY/mLPzbTF170hZcyt64ZrS+8DHOq
gyK/LfH+bWvUCeIwREZIiwaTWIumsi5yg6lcWde+cJrkrknugSNFfiK/pMhv/rs9uUV1e24N
shr2NkV+ivwU+anbc0jdnhrtqW5PdXuq25PBtK8qxNG2LNG5G/oSbZajm9c5V5jG+BBf26ww
RWVgNTmKMQq3mUH/Y5VX3jWxZ9dmNne+wKgCa4oyOpa5N74si6L2PnQl26wqasTtVe6Mz0NE
b7PaeOssQrbGFLGUK5vS13DM0c3ZblHdniYc+zyr87pqalfgQ1Y+9PjmWWlqnBF0t+O4KfJL
KvLj6WgyfeFl2FHRQqhPkZ8iP0V+ivyGFPnN/4CX2ZEfn2tcNnMldz7zwcJHSTzoeM10GJ2A
bVi8LO4T94n7xH0Ljvsakd+C+6DL/UlT5CfyE/mJ/ER++rrZgiNDkZ/IT+Qn8hP5ifxEfprp
gGEhFm8C8tzYOAfElbbWTIfAkZrpoPEuDzDeRYM9NdhzdN4dKvJT5KfIT5HfkCK/+Se/+Z/m
x6cfTfO7//uzUcyL/ER+Ij+R35DIb3QGe2rAy+hEaFuKWEV+Ij+Rn8hvzMlvmF830wdethQZ
zXe9Ij+Rn8hP5Cfy04AXDXjRgBcNeAnfovnF16x/oem71vrAiykfYMCLuj014GV0ulMV+Sny
U+SnyG9Ikd/8D3iZ6wde9M5vdEhqS3WHivxEfiI/kd+QyG/+I7/Zjfb81a+bzZ38NNpzS5HR
fNcr8hP5ifxEfiNLfrOL/IY54EXkN98ktaW2J/IT+Yn8RH4iPw140YAXDXjRgBcNeNGKRlgm
yJXelblxhXWVY8dhk2FN65Ec8DLMyE9THbZUJDbf9SryU+SnyE+R35AiPw140WjP0RlII/IT
+Yn8RH5DIr/5H/Ayu3d+wxzwoshvviO0LbU9kZ/IT+Qn8htz8htmt6cGvGwpMprvekV+Ij+R
n8hP5KcBLxrwogEvGvCiAS8a8DJeA16G2e2pyG++I7QttT1Ffor8FPkp8lPkp8hPkZ8iP0V+
ivwU+c0t8tNoT4321GhPXztv89z7nD0OiC9t4UpXl6asK8vxUjSVhfeVrYvG5T6aXG4b52pr
7yuFmUa1d87nPrdtodI23lVwrfM8fHTZZKXzxvmqsCYvoqkytnbGsO46tqFC3lQoU9Zxe7Wp
FPkp8lPkp8hPkZ8iP0V+ivwU+Snym1vkl+pUB4323FLvzUa5Xr3zU+SnyE+R35hHfsMc8KJ5
fqNMeDPbLvIT+Yn8RH5jTn7DjPxEfjMJZJR1kZ/IT+Qn8hsS+WnAiwa8aMCLBrxwSI+vqqay
tiwxrCe8SLNZjgE+zrnCNMaHUTc2K0xRGVhNjmIc02MzUyCTV941cUyPzWzufFHWxpqijI5l
7o0vy6KovQ+DiGxWFbXFyJ/cGZ/zcRd11cZbZ53L8TIzlnJlU/oajrlphxrZrHHWNxab9WWu
d3565ze3d36pkt8wIz/N8xvlaG9m2xX5KfJT5KfIb0iRX6oDXob5zk/kN5NARlkX+Yn8RH4i
v5ElP/ZlNFne+Bzj1MuqKYxlmAcTpku5pikdOkq8yG+USWpLtV3kJ/IT+Yn8hkR+qXZ7DpP8
NOBlS5HRfNcr8hP5ifxEfkMiv4XQ7Snym2+S2lLbE/mJ/ER+Ir8xJ79hDngR+W0pMprvekV+
Ij+Rn8hP5KfPm+nzZvq8mT5vpqkOmuowt6kO6vbUPD/N89M8P83zKxy+Mu7CbEOT4UvkrszL
whVFO5kRXyOv8d3x3HI+o43fLC8afOscsyNL42z4QHmR+YIfMc8xzbHMeW8tiqzGV9OLvCox
JbH9ZnmRlbZoGsxurDALkv1SKGXypqowwdHmVRPqyjPvXY5JlrWr2hmPeebw1XPMxcz5ZfQw
xzLP6hyW2hUObYl+pakx8xIfVMf8SI50L/LMcPOFt5hWWYWHhTzDrEuDZviiLsI32H2GCZbY
NqZ01vhaOydnemwQDUdbvS3bXfRZXeV1U1pT501juYse0zVdbTA7tMpRmo3wmcUu51XtnEXr
2AifGZeXmJzJz7fjg+3BVGCXfWNsU5VVmMLpM3zGHbNDcS7wSzg2TeZxfIsS4yFxbOp2cCQa
0Bgc6drVlWH1TeZKnjKU5C7y4DQ48rkp4ehwaD3PWZNVOJhlhZbgbBapkp+6Pee7S3EUtqdu
T3V7qttT5KduT3V7qttT3Z7q9lS3pyK/uUV+muqgbk91e6rbU92e6vZUtyc6qEPnKPq7S/RA
W3SR1rG/lF/9y/FdP1+iE7rtVUW/q0XPdY0uWVe1fa/43h6W9wzf4cP3+UJd6EtHHR4d1bmL
pv6T3Nksh35pdJOji9tjydA6DuNsKl+h+xnd7+1CoA5RscF+eIfOb/SFB8cmRxd36CH2KB9M
WK20wkKkqC9vCj4FjELP30Juo3o91eupXk/1eo55r6fmuC9kktvcvov8RH4iP5HfgiM/BX4L
PjAV94n7xH3ivjHnPo313Fzws5DtIj+Rn8hP5Cfy0yu/BRcJivxEfiI/kd/Ikh9Hnzz4mg6K
/BZyhLe5fRf5ifxEfiK/IZGfJjposOfoDHIV+Yn8RH4iP5Gfuj3V7akp7pririnumuI+XlPc
h9ntyamGmPmnaX4jT5aK/BT5KfJT5DekyE9f9lS3p7o99X0Xfd9F33dZcN93SfWd3zAjP33g
ZXMDSEbNrshPkZ8iP0V+Yx756QMvo0ZM89FekZ/IT+Qn8hP5acDLyL/D60uYIj+Rn8hP5Dfm
5Kduz77EsBDKi/xEfiI/kZ/IT5GfIj9NddBUB0110FSH8ZrqMOd3fm3IqBWNxpIYFfkp8lPk
p8hvZCO/2X3ebM7k1zqK/ER+HL1v6ropCmOb0pV8LKIJyzwWWIKyKH1ZRpOmOmiqg6Y6LLip
DqnO8xP5LYR3eH33UZGfIj9Ffor8Rjbya5d277+Oe6P1/MYymutDgCI/kZ/IT+Qn8tOAlwVH
hiI/kZ/Ib0GTH7sEmyGR3/x/4WV27/w01aFPRLRQyor8RH4ivwVNfiSG0SW/2XV7zpn8WkcN
eBnLqFDkJ/IT+Yn8Rjby28Lkp9GeeDQa10hQ5CfyE/mJ/BYc+Wm8y9hy2my5Wtwn7hP3ifuG
xH2pznSYc6+nAj8FfnWdEwakSk3z42Focu9MSeKsXTwyTZOXhTFl7YuGNwGU8lXVVNaWZWXr
8NUUm+W2LpxzhWmM58NnYbPCFJWB1eQo1ppMgUxeedfkeZg5aTObO1+UtbEG0ynbUmXuDWZW
FmiF53t/1FUVtXW+yp3xOa94mGqD2WbWuRxfromlXNmUvoZjbvJYV+Osbyw268tcH3jRB15G
5QMvsxvv0nKYbzAbucQlBdjPcqaDXvnhJjLbSGrUyinyU+QXKFLkZ8KDR57hOa8S+Y0K+emV
3/iS05YmU5GfyE/kp25PdXtqmt/YRnibI1GRn8hP5CfyGxL5zf80P0V+ivw2R24PZhf5ifxE
fiK/kSU/vfMT+T0YyW3ud5GfyE/kJ/IbEvlptKe1GJWWNwVj4M3ddGVP49iI/ER+Ij+R35DI
b3S6PTXNb8Fzs7hP3CfuE/ctOO6b5UyHdoqEPm42lkQp8hP5ifxEfiI/DfYcS4J7oB5mkZ/I
T+Qn8hsS+c3/Kz+Nd0nj9dkDkUyqv4n8RH4iP5HfyJLf7GY6zPkDL+r2HONxOyI/kZ/IT+Q3
5uSnT3umGn1tzXaJ/ER+Ir8FTX4Mboa1mt/8d3sq8lO351wJVOQn8hP5LWjyY1Qk8qs14EUD
XvICyxC48KV/rOBQubLGIgVOizrUDb4Db/OSz8l4YtCiDr5d5sNmWMkCK0nYxnvAhUcHK1e4
qjGY55sXpQtLS5jMYYWKEqteuKJoV64wGVaoME1uuXiFte1hLZrCeyyFURpnw2IWRQb0Vd7n
WNOizMNaGUVW11jfIq9KrD9Rh/NRZKXFShpYyqLCkhdh5Yoiw4f7qwqrWdi8akJdeea9y7Gi
Ru2qdnmLPHO+xlesRX4j2+05uwEvc+72bB011WEsiVGRnyI/RX4iv5Elv9l1e86Z/DTgBU+l
c+1WTN1P5CfyE/mJ/ER+6vYcW5LbHAmL/ER+Ij+R35iTXxvAzWEtW0V+ivz0zk/v/AJHYj34
qrZFhaXj9c6vLLytrWvfdOZZ7o3Bq0df1EXOd5g+8/gR74saUzcuvEf3eMmIl5V4P+lt2b7W
9Fld5XVTWoPPITeWrzV9VuE1uykrvA9Fab6w9JnFa04ce+csVtplZ5/PjMtL31iHV6fGsGfP
ZwVec/rG2KYqq5xv7n2G99S1sXj/il/C+9Am83inWpS5tXgfWtNx3Ae8qNtzc9HPQrYr8lPk
p8hPkd/IRn5beMCLIj88Go0rQYr8RH4iP5HfkMgv1UUd1O05rgT26+yXyE/kJ/IT+Q2J/OZ/
kvv8R37scnaY64Q+bldXxvimapdHcnWJVwJazm9kIkWRn8hP5CfyE/nNerSnyO/XibZS8hX5
ifxEfiK/kSW/+Z/nJ/JLicB+nbaI/ER+C5L8wlDIQp94GfnhnvPf78ktqt/z12GdVHzFfmK/
Bcl+vIWJ/IY91yHVES+a65AK4aTUDpGfyE/kp35P9XvO+qWfIr+UCOzXaYvIT+Qn8hP5jTn5
aa7Dr0MS4+or8hP5ifxEfiNLfnrnN76z0Lc06Yr8RH4iP5HfyJLf7IZ7KvLb0kQyivWL/ER+
Ij+R35DIb/4HvMwu8hP5jSI5bek2i/xEfiI/kd+QyG/+P/GiyE/dnnMlSZGfyE/kt6DJj1HR
sJZ1mP/Ib67k136SzFtTlLUrfD3rwZ6a5D5XrknNT9wn7hP3LWjuWwhLGs2517OdH4hlqWrn
vTO1cY1mOqRGYnNtj8hP5CfyE/mNea+n5rjPlSDG2U/kJ/IT+Yn8hkR+qfZ6/ir5zbnXU4Hf
uPChuE/cJ+4T9y047mtEfiOz8tCWIluRn8hP5CfyG3Pym/Mrv9ZRr/zGkihFfiI/kZ/Ib0jk
txAmOmiw55aKxOa7XpGfyE/kJ/Ibc/L71Vd+c+/2FPnNN0ltqe2J/ER+Ij+R35DIb3TGu4j8
NDVe5CfyE/mJ/IZEfql2ew4z8tNozy0Vic13vSI/kZ/IT+Qn8pv1B15EfvNNUltqeyI/kZ/I
T+Q3suRHKmqyvPF5XjRl1RTGMsyDydrKNU3pitJ7jfbcUgQyyvWK/ER+Ij+R38iS3+y+7DnM
bk8NeBllwpvZdpGfyE/kJ/IT+anbcyzn8s0ku/vrIj+Rn8hP5Dfm5DfMbk9FfvcnkVHNi/xE
fiI/kd+Yk98wuz014GVUye7+7Rb5ifxEfgua/BgVLbzV/OY+z0/kd38SGdW8yE/kJ/Jb0OTX
Do5sStsYV/na1ZVpR5G40rsyN66wrnItRdZ1bsoyt66pKm8Da1auKsrK5WVtTDH/k9w12lOT
1edKviI/kZ/Ib0GT3zAjv9GZ5D7nRR30ym+uXJOan7hP3CfuW9DcN8zAL1XuG+Z4F/V6pkZi
c22PyE/kJ/IT+S248S4K/BbcxIb7c6S4T9wn7hP3LTju03AXvSkU+Yn8RH4ivyGR3/wPd2lH
5jzYx8000eH+UY/yuO2ZzBAZIS0ajOUqmso69gkEkyvr2hcOdvaa01TXTYHP5+GTeWXn6Lwv
rMGQL1+WsRTGjHmb5953frZwpatLU9aVZac5qrJl4X1l66JxedygdbltnKvxVb6uFEab1d45
n/ucg8vgh1FpHqPSfFXnedxe6bxxvkIr8iKaKmNrZwzrrmPbK+RNhTJlHbdXm0rkh4Nqs8ZZ
39jC5L7MeQtrD2M4lr/4YzPn8qq2RVV3Z9ZmZWEKnLDGe1MFT5vlrmpMUzicDBdBghOGgYNl
4YrCxtPB0YFNbqscwwbjqS0aQMJXVWmcDZstMqAP5zq3Odz5RqkoshrgKvIKcMvbU1sAE0XT
5M5UpigDvIrM5BiQ6KyzedWEuvLMe5c7wAvDE0OhPHMAR9WI/IZEfqm+8hP5iex+NdINDNdy
CthL5GeyujGFtabI8/YDuThCrrSgfDxdWtBme7Ca3DtTkjgxMjyaGtzbDdjd4z7cmnAbx6OE
LUtQfMcLIHvcfwvTGB8Y2GYgj8rAanIUo6PNDFiIpOCayO82w93fF+ALNK2MjmXuDZ43CrTC
h5u5zSrwEJ4CQAM+D7Rjs9p4MABYCzsWS7myKX0Nxxxk125R5GfCsc8zPOdVTe0KByKOpFma
GmcED104bgw1ihyPjODewlsc7pby8wxnw4CDfVEX4TnNZzjwIF6c6hpPdDzQHmwL1gZAvC1b
fvdZXeU15hmYOm8aS+R4nEZXG6CmylGajfCZBd/jwcM5i9axET4zmF6AJxY+4uGhLpgK8L1v
8GxalVU4tT4DZoEaPIjgl/Bg0GQeDxcF5itYPBjUdBzWLL9UyY+n1mW+wdNxiUsKsFe356+S
wUIjSJGfIr9AtyI/kd+vP8svVfJT5LfQiG02+yvyE/mJ/NTtOebdnor8ZkMGC62MyE/kJ/IT
+Y05+SnyW2jENpv9FfmJ/ER+Ij+RnxY0WnDz/kR+Ij+Rn8hvZMmPQ7i24DrubciIQUsYYIwh
brXBMKgweKbJMbopfAXVNxXHMrkMg9kxEtpiVFqOkc4wzSb6UJmtd5xEfiI/kZ/Ib0jkx1t+
k2EcrKnxuWuMrgRntCbMdMKYY4v5UHX8HjYHQecY5uxLTDzhS7kGw1cxEYkjnzHdpmpn8GE4
MmY+hWHJGK4cSmH+DOrwmN2Ut1T04OQ3zG5PNsJlIr+tR1rDemAQ+Yn8RH4ivyGRn0Z7KvIb
HVIU+Yn8RH4ivzEnP432HFa0NE71iPxEfiI/kd+Yk98wuz31zm9cCFDkJ/IT+Yn8RH4a7bng
BuiI/ER+Ij+R35iT3692e7YDND0/FohP2Xl8PriOIR0Gb1b4zBy+Mdt+FBiDWzTYc1yCvZn7
Ie4T94n7xH1jzn3q9Zx505fejskR+Yn8RH4ivyGR3/zPdGgnP2hFIxFa/0GmIj+Rn8hP5Cfy
U7enXvlpOT+taBQWXwqL+dzvj5bz04pGpsRSSA4rJcap6pjLXpQV1lbC4oyFpvlpml//CGxr
Ra2K/BT5KfJT5Dfmkd8Qx7vo+y5bi6uGvV1xn7hP3CfuGxL3zX/gN7svew5zvIvIb9gktLXq
E/mJ/BYk+bXr1+dYV73Gsu1iv5FlPw14GZ1uxq3FcpvbrthP7Lcg2Y8hQyHyy6uaYVEzsuQ3
/6FfnA2oRR1GfoCMyE/kJ/JT5Dey5De7yO9X3/k1muQ+8uS1uYhutnaRn8hP5CfyG3PyG+ZL
P0V+syWX1MuJ/ER+Ij+Rn8hP8/wWXCQo8hP5ifxEfiI/kZ/IT5PcNcldk9wbfOsYi4T7MMk/
z/BdY1OY0jalJrkvrEnubX+pPmw9lsSoyE+RnyI/RX4jG/nNbrSnBryk/v5ta7RP5CfyE/mJ
/EaW/GY32lMDXrYGuaS+TZGfyE/kJ/IbEvmluqqDIr/UiWhrtE/kJ/IT+Yn8hkR+8/99s9lF
fiK/rUEuqW9T5CfyE/mJ/IZEfvMf+c3unZ+6PVMnoq3RPpGfyE/kJ/IbWfKbXeQn8tsa5JL6
NkV+Ij+Rn8hP5Kd5fmM5neGBCFjkJ/IT+Yn8hkR+qb7zG2bkx1jTZY0+bD3yZCnyE/mJ/ER+
Ij9FfiNPZg8U5W3qN5GfyE/kJ/IbEvmlOuBlzqM925BRX3gZS2IU+Yn8RH4iv5ElPw140WK2
m4rqZmMT+Yn8RH4ivyGR30J456cljWZDLKNQRuQn8hP5ifyGRH7z3+2pyE+R31yJVuQn8hP5
ifxGlvxmN8l9zu/8Wke989M7v0WkyrpuisJgdRdX8m0wTc77wpqqKH0Z1oCBydfO2zz3Pid8
UMgWrnR1acq6sgQsTWXhfWXronG5jyaX28a52tr7SpW5qb1zPve5bQthaRnvKrjWeR63VzqP
VlRoRV5EU2Vs7Yxh3XVsQ4W8qVCmrOP2alOJ/ER+Ir+RJT9Ffor8FPmJ/BYVNquK2uIpIHfG
5+HZxGa18dZZ53IsVBgeO2zmsC6dr8uiyE372GGzxlnf2AL5MmfnVfsMER4kfvEHni6valtU
dfdYY7OyMNgoHki8qYKnzXJXNaYpHJ5EXHxCwtOKK/OycEVh47NIWePZJLdVXnkbn2sKrKGH
p5qqNM6GzRaZL/igk9sc7nylVBRZjSerIq/wrJW3zzVFVtqiabDXlSnKsJNFZvKmqrDjNq+a
UFeeee9yh2crV7VHIs8cnoyqRuS34MiPT78u8xZ4wdqNHs/XNXGDCXxN5auGcPbtUzNMWM8R
D/gOqzpikce2lKb5jXwwyLiti9+qoqlrrWWrtWzFfVrLdlGDJyQ+rhhXWFc5Pq80eOrIF9Za
ttxtkR8OwlyDq5T9RH7q9VSvpwK/BRf4NbOL/BgYiPxEfjgCpEq98uNhaHJ0gpQkzjo8FNPU
oFPP4J2mRwdce7DQf9dU1pYlXmx2HYJ4xYmOt8I0xof3jjZDr2FlYDU5itHRZgbdj+wNdE18
q2kzdPt59NAY9tNExzL3Bm9ZC7TCx/5M9Xqq19M3eCNflVXo0PYZXnADNeiBrpwPPcJN5tGr
XJS5tegRrnl/b4ZEfvM/04G4b7K88Tn6rMqqwWiEdoewd5VrMDIBl4tvAzjfYExAiUsKnf0i
v/GM5vpEmor8FPkp8lPkN7LkN9fxLrML/DbR68kNIhbUK7+R7wkV94n7xH3ivgXHfbMM/DZB
fhrv0ie4SrmsyE/kJ/IT+Y05+c2511Pkhzg3ZQL7ddom8hP5ifxEfiI/zXQYW5LbHEGK/ER+
Ij+R35DIj4O6mgzTL01dYXJmU2B2XGvCFy4w4dLiOxi155TOBl+4wJAcDPTyJeZcMsJq8LEM
fICCY78w07RqX+Zh2im+eBGmo2KaaiiFqaOow+OrFrmLJo132dwNXvbNR64iP5GfyE/kNyTy
m//BnnMd76J3fpsnhYVCmCI/kZ/IT+Q3JPJLNfJrZ+vNYabDJt75abTnuJCjyE/kJ/IT+Q2J
/FKN/DTgZVwIa5j7IfIT+Yn8RH5jTn7DjPw01WGYBLQ16xL5ifxEfiK/IZHfQuj2FPltTcIa
5rZFfiI/kZ/Ib8zJT92ewySNcalL5CfyE/mJ/Mac/IbZ7akBLyI/LWWr71oH2tRqfuGT5XmG
r4wbLCroi7oIqy57LBaHZQ1LfMK8xvrMnPDmsXwgliHEh8+9LdsFC31WV3ndlNbUeYNV5EKp
qnC1wdfQqxyluRShzywWMMRXqJ2zVVPzBuwxLS4vsQQjF2zGEs3BVGABQ33XOnzqeuZ3rUV+
40JYw9wPRX6K/BT5KfIb2chvCy/qsImpDnrnN0wC2pp1ifxEfiI/kd+QyG/+pzrMjvyGGfmJ
/LYmYQ1z2yI/kZ/IT+Q3suSnL7zoSy1zJUSRn8hP5CfyE/npw9b6sDWWQ65seDkfeNFhFWiP
t+91zt5vmrSQuxZyLyosHd8iwmYa8KIBLxWG3tTGFPPf7Tm7yE9THeYaHY2znyI/RX6K/BT5
KfJT5KfIT5FfYwprDcaVG8v35Hg8wGosiHexbIrF821rarDSiqY6BNpU5KfIT5HfIpe5uqxq
a7FoU94UxMQ4R03jsG+K/BT5KfJT5DekyI+3/LFaz09THcaYxEV+Ij+Rn8hvSOSX6js/TXUY
h0ht2Psg8hP5ifxEfiI/vfNbcN20Ij+Rn8hP5Dfm5KfRnsOOmsahPpGfyE/kJ/Ibc/JTt+c4
kNWw90HkJ/IT+Yn8RH7q9lS3p6Y6aKpDGLrPtQSK+/2xmXNYWcBqkntmqtKXhbc1Fm7QVIet
N9VB3/bUlIq5RoSK/BT5KfJT5DekyE9THTTPb3TIWOQn8hP5ifyGRH7zP9VhdpGfBrzMNToa
Zz+Rn8hP5CfyG1nym/9ve3KLLmtyrFzs6soY31Rcp1hfeBm5d4YiP5GfyE/kN+bkN8zRniK/
cYkGRX4iP5GfyE/kp9GeIxe5/bokLPIT+Yn8RH5DIj8NeNGAFw148bXDGgh5t+qbyWzhSnz2
3JR1ZfmSGqxrMVTcV7YuGpez15wml9vGOXwb/b5SZW5q75zPfW7bQqVtvKvgWud5GItvstJ5
43xVWJO3w/NNVhlbO2NYdx2XYqiQNxXKlHXcXm0qkZ/Ib0GTHy+OZkjkN/8DXmb3zm+Y3Z68
e+md368bdaXgr8hP5CfyW9DkR2IQ+eEBu460hgEsVYMHbPwLj81gutLgYR6LmNXGNXrnlwJx
DaMNIj+Rn8hP5KfIb9bkp8hvGMSTQh0iP5GfyE/kN+bkN8x5for8UiCuYbRB5CfyE/mJ/EaW
/BiHNVne+BwfZiyrpjC27cfNMW7ANU3pihLdl+E9nW8wKKBs8jw3cGhN1mDldVf4zXR7ti8L
1e05liNBRX4iP5GfyG9kyW92A17mTH6to8hP5MfxmKaumwKPV3ikKvlYRBPeBeORqsIjVhlH
XxqN9uSR8VXVVNaWJca0hq8f2yzH6FbnXGEa48OQU5sVpqgMrCZHMR5Sm5kCmbzyDo+p4ZDa
zObO4yHV8FE1Opa5NzjkRVHjBLSOVYEvLfsqd8bn4fTYrDbeOosvUuOL3bGUK5vS13DEI3Cs
q3HWNxab9WUemnq/b1rHVujD1rzbFrk+bF15Dr5ussrhwu8+bD3/Ux22cOS3CfLjFjXacxjd
jlu7DkV+ivwU+SnyG/PIr+29nEO35ybIT+/8tjZpDWv7Ij+Rn8hP5Dfm5Ndy2HDIT5HfsMhn
a9cj8hP5ifxEfmNOfr8a+c1uvIsCP/Txbm2O2lLbF/eJ+8R94r4hcd/8v/Kb3XiXX+W+WQ72
3AT5KfDbUmQ03/WK/ER+Ij+R35DIT18306c9RydSFPmJ/ER+Ij+R36w/8KLxLvMdoW2p7Yn8
RH4iP5HfmJOfxrtsKQIZ5XpFfiI/kZ/IT+Q368hP7/xGmfBmtl3kJ/IT+Yn8xpz85jzgpXX8
pQ+8iPxmEsgo6yI/kZ/IT+S34MhvzjMdxH2jzHcz2y7uE/eJ+8R9C477NNNhdAZlziSsYeoi
P5GfyE/kJ/LTK7+xncu+OcIU+Yn8RH4iP5GfyE/khzWxKqwKwA/XY7WGypV17QtX1zkHC9Ok
NR14GJrcO1OSOGsXj0zT5GVhTInj1XCuL0ppTYfSccQADoXDAhUlDpArinbhCpNhgQrT5JZr
V1iuD4BSRVN4j6NWGmfDKhJFBvRV3udY0qLMw2EtsrrG8hZ5hSVE8joc/CIrLQ46VrKosOIF
X8oURYYV26oKi1nYvGpCXXnmvcuxoEaNZQhCoTxzvq6x7kZeOm9CVXkGqFcNFnhzaEv0K02N
VTZKLGSCkQ+sXWs6VJtc02EhzHHXNL/NRVKjZscNx8TbE1YkakByIj9TWKwahPUuw6KYvHGX
FpSP1S9tXnZMJ/JrH4dsBsbHKkq28R7PSmQGrNrkqsY0hcsLkR/osjF148IDpQfbgrVB1N6W
Lb/7rK7yuimtqfOmsaQPn1V43jRYBqvKUZoM7DMLvs+r2jkLauYN2GMlsbzEKlQOzxAmXMU+
K8D3vsF6Y1VZhbWqfAbMYhksnAv8Eh4Mmszj4aIosdgrHgxqXv7NmEd+vGpdps9a6z3fTIIW
+anbM/CVVvNT5GcQY6MjozLk1gbPfAzWQZPWVaF7o0HMnZsSrOkQVG9qNb+FEPlptOdMAhll
XeQn8hP5qdtzzCO/drbezMhPMx0W3Cu++/O0uE/cJ+4T9405982517MlzV+a4q5XfvcnkVHN
i/xEfiI/kd/Ikh/7IJsMr+NzDFYoq6ZoX9TDZG3lmqbEu02MoNIrPxyBUSWpLdVukZ/IT+Qn
8hsS+Wk1Py1oNDokK/IT+Yn8RH5DIr/5H++iyG90yGZLRXBzrVfkJ/IT+Yn8xpz85vzOr3X8
pXd+Guw5V7JJzU/kJ/IT+Yn8xpz8hvnOTwNeUiOxubZH5CfyE/mJ/ER+s/66mchvrmSTmp/I
T+S3IMkvfP0EXynT5830hZcS37Lz9azZT/2eqbHYXNsj9hP7LUj24y1M5LdQPm82zH5Pkd9c
ySY1P5GfyE/kp37Pke33bL/E9mAT/eY84mUTs9xFfqmR2FzbI/IT+Yn8RH5jTn6K/OZKEOPs
J/IT+Yn8RH4iP73zW3CfgBH5ifxEfiI/kZ/IT+Sn9fwarefHwSBhHdf7/bGZc1gBzhZVjfVl
+SIFi/dpPb+wimGe5d4YrKnri7rIuTivzzwWA9J6fvz6JlYxLrGusK0KLPbMg9NktsSSg5Wp
fYmlhYmlBgsUVhbrEddYa9BV7ds8g4UzAbgcad60JiwSiTo8lh/OXTRtsXd+muWOEzOuXZ+K
/BT5KfJT5KfIT5Hf2JLc5shb5CfyE/mJ/Mac/OY82lORnyI/rOBMGJAq67opsHAIFgspOYaK
Jud9ge4KLB5Shn4ymLAitLd53nWOmcyi38PVpSnryoY5VjCVBVYbsXXRuHbOMUwut41DP4e9
rxTWksYEVOfR7cHuEmyvtI3HmtO+qvM8bq9EH4jzFVqRt/11JquMrZ0xrLuOba+QN+hYydH1
0lZVm0rkJ/IT+Q2J/FJd1kHkt7noZyHbFfmJ/ER+Ir8hkd/8L+swu3l+vzrVQSu5L7hezvvz
vLhP3CfuE/eNLPexE2kLLmarOe44vvcnjXHJi/xEfiI/kd/Ikt/sAr8593qK/ER+euVXNxhN
bfGysH1X2GAAtilJnLXrTE2OQf94p+mLhr0/eK7wVdVUlkO68fqRJpvleMXpnCtMY3x472iz
whQc3e1MjmJtKVMgk1feNfGtps1s7jyGiRtr8Gq1LVVibD3esmKcON65tqaqqC3efebO+Dy8
kbVZbTDg3mKKAqZwxFKubEpfw5EDyFvHxlnfWGzWY5Q5Tfeb5BCymumAeQs8OHlmKrzgLrzF
4a4006FyuDKMKVJ95fervZ6Nuj3HNqKbbWSqyE+RXyBlkZ8JDx55hqFdVYPv/Lum8IHy86w0
NR5HMM4KDw0ivzK3rqmqOFuvchjo1pHf6Lzymzv5EQAua3LM6XR1ZYxvqpZIMZwPU2AtnlDz
JjwGzPYmrHJbp2tV5CfyE/mp23Nkuz238Ds/PhCB6fD0gxHtDs9AeCQS+eEIjANhi/xEfiI/
kd+QyG/+uz1nR34th/kGU6FKvElAb//cIz+R3zgQH/dB5CfyE/mJ/EaW/GY34EXv/MaFsIa5
HyI/kZ/IT+Q3JPJbCO/8FPkNk4C2Zl0iP5GfyE/kNyTym/9uT0V+4/H+bWuQoMhP5CfyE/mN
LPlt4Xd+muc3JoNbNkWuIj+Rn8hP5Dck8lO3p6Y6jE4kKvIT+Yn8RH4jS36zi/zmPOBFkZ8i
P33hRV94CRyptWw1yX2BT3LXgJdNdSGOok2RnyI/RX6K/BT5bXotW0V+ivwU+SnyU+Snz5vh
PmDKB4j8FsJoT33ebBSjvE21WZGfIj9Ffor8Rjbym91UB33hZVM3/4VuE/mJ/ER+Ir8xJ785
D3jRtz3V7aluT3V7qttT3Z4P1u2Z6lQHRX4LPcrb1P4r8lPkp8hPkd+YR34iv03d/Be6TeQn
8hP5ifyGRH6pDniZM/lptKe6PdXtqW5PdXuq23NUuz31zm+hR3mb2n9Ffor8FPkp8htS5Kd3
fvq8mT5v5rHysc1z73P2OIBibeFKV5emrCvLbyTQVBbeV7YuGpf7aHK5bZyrrb2vVJmb2jvn
c5/btlBpG+8quNZ5XkaT88b5CmtV5kU0VcbWzhjWXcc2VMibCmXKOm6vNpXIT+Qn8htz8lPk
t6nIZ6HbFPmJ/ER+Ir8xJz+981voRLep/Rf5ifxEfiK/IZFfqgNeFPlt6ua/0G0iP5GfyE/k
NyTy0zs/vfPTOz+98+NbTV9VTWVtWeLNJh+KC5vleMfpnCtMY3x48WizwhTV/2fvS8A1Kcpz
f3YY9kVFQBiQRQSarqrurq6ZOWfmsKsIyOqCIgoBERCBYTEmTowSjHENUaMmLpHESKImMRp1
honRm5vcrC4xJq43MV6v5hqTq15jVO77VlfDcWTg9PGfQ/3/eeeZ79RX319fdXX32/3WV13V
bWG1JYp1paxBpqyDb9NjTVe40gdTNdZZUyXHqgw2VJUxTQjxOaoratM4PPwsvQ0lu7vYYmOD
8w6fY2itSaV81VahgWNpu6etrmi9C63DZkNVxqbGR6db/HGFvuqgrzo8wLs9cyW/cUZ+erfn
tESMivwU+SnyU+Q3sZEfu3NtUbahLE1b1a2xjkwHEybN+batPPqKYdHP/DrHtrKYwBe8baxv
RX4iv8pXMbSwBeZZBsyzrIGyKk21tIr8FPkZj6m3PoEE03N9VVbGG9OFt7ZAGGvb0jHCdWki
r2kxARjxcmW9i1AyRTCc2Vsi8K1KBhbGFA3uRKasAbeym8hrisqZtkW8WyMujuGtKWzZ1jVC
XlfWbayrLHD/KhF2N77uYuCy8JgKjOi8rDBdOEbdZdGUsDTeeLQl+eHeh1gcs4wRMSvye4DI
L9dnfuMkP8LLF21prfNNbW1oa47E+AKT2WvMU8fwTNkaHolpIYlp3Q9Ffor8FPmJ/KY88hvn
sKfIb1rIUOQn8hP5ifxEfvf/Mdv7GfYU+Yn8NOxpKxJn4+NwmS0w7FYZi1X8ASNwHJ/ThBcN
e3oMuWJuU4M3N3BsLGCcFeO1AEhwVTeyG4qmLpu2chajZa0jcgLmLfnGYppUXaI0x15D4TDS
W9aN9w6Dshx7DXjeUFaYpcRXOeDlDdFkMNIbWuvauqrjXKZQ4JUOmCaFIWj8EoeE2yJgWNlg
9NJhSLihYzux5Mcj8eDP/BT5TQthjXM/FPkp8lPkp8hvyslvnM/8NOFlnAT0UNYl8hP5ifxE
fiI/DXsuuwk6Ij+Rn8hP5Dcm8puc2Z7dBM3AVbOY2Rvw+uAmPczD5M0aw8+Yddy9FBgzO+ev
dNAjv4cyWBvntsV94j5xn7hvTNyX6xr3cY56ivzGSUAPZV0iP5GfyE/kN7HkRyrSfBctKVwM
iYr8RH4iP5HfxJKfJnuK+BZDfPQR+Yn8RH4ivyknPw17LpYgptlP5CfyE/mJ/CaW/DTsqchv
sQQt8hP5ifxEfhNLftt42LNbHK/ZnlO5CkLkJ/IT+Yn8Jpb8Fhb5adhzsdHRNPuJ/ER+Ij+R
35jIb3KW+bVa5zeV0dwQshb5ifxEfiK/MZFfruv89GrPIaSwXMqK/ER+Ij+Rn8hvwW940as9
p4UcRX4iP5GfyG9iyW9hz/wU+U0LYY1zP0R+Ij+Rn8hP5LfgyI90qw+5j5OEHqq6RH4iv2VJ
fvFbd6bE5/Wapm7FfmI/sd+ymwEj9hP7LUv2Ywde5LdcPmartQ4PVXiV83ZFfiI/kZ8iv4mN
/Ba7yl1LHZZdoLclD4v7xH3ivmXNfQyK2mXHfYtf56fZnluSyKTmRX4iP5HfsiY/zoScdvIb
56inyG9SyW7Ldov8RH4iP5HflEd+4yQ/zfbckkQmNS/yE/mJ/ER+U05+Wuc3qQS1Ldst8hP5
ifxEfiI/rXRYdhNgRH4iP5HfsiY/TXhpvAnNgslPz/y2ZTS2lHWL/ER+Ir9lTX7Lc8KLVjos
u0BvS14V94n7xH3ivmU36inuE/fZwrLjFznQtE1TmrZ2nsiIJl81TTAedo6N0NQ0rTHWtZWv
ekcfgnG2NlWoqlQqND64sgyh93PGV76pbNXULr5awxauMiHUrjGt7141BZMvXet949y9parS
YkDChzKUrqu8cm3wNVybskzbq3ywPtRoRWmSqbau8day7ia1vUbe1ihTNWkHG1uL+8R94r4x
cV+uX/PTdJctgx7lE8P1TCfyA7s3rTXOWVOW1iV295UD5Zct6LxKPNqWwduKxNn43tSWlbFg
92BaftUMdYUaL410rqpA8bwvGFeUIHvvvbGtDZGBXWGsqS2stkSxrpQ1yJR18G3id1e40gdT
NRZNq5JjVQaL/oZBK0LsULiiNg26LnXpbShj613R2OC8877EjqVSvmqr0MCxtF23wxWtd6F1
2GyoytjU2IfY4o8rUE3dOFNji123xhXYaWwUHZJg634nfd3a1nj0RHx/DLEzFQ6QN6bbSVtg
Z2xbOu6nS/0a06I/hKNWWe/itk2Brhc6OiV2vyrjYTVFg56VKWv0tcquX2OKyuGgY69rHJ24
k6awZVvX2HG8v6uNdZVFCL7EwW983R0JvdgTZ5MnaNpX+XEffRFa9I4rXFKAvZa476nIT5Ef
qKNmAJruvyI/kV/dYgaEBxEn0qxsg+4IRhzQaeBsB7wR1JJ7TQBsfEf5ZYGuiAUHB9OYOEgR
CvQ6QLzo5zQYzmCPJeA12mBtEHVwVcfvoWjqsmkrZ5uybR35PaAP4xuLLlNdojQbEQoHvgdV
ee/QOjYiFNaXFXosHN/AiEY0GfB9aDEwU1d17NeEAh02dJnQEcEvsWPQFgGdC1OVzi2XF3uK
/BTp/TjZx7FNXDYxVeSnyE+RH0b4RX4MBn3FYB00SX7nkESLmLu0FVjTI6gO7C22RY0wuqpB
w4jjzdJ/x51hflsgkCvxwKaqWzyR6UJZUHvtWzydwUBJYOsXFfl1rIkODAYbMNbTWHSJYl1t
iZ6Ob2prQ1uzX+MLPNXBqIjD8EyJUQ+YRDh5HwORn575xeFYDXvaOORcFiI/y8BS5IcB+Diq
jk/3ifymkchFfiI/kZ8mvIxpwsvSR34dTz9Y5LfoYU9FflMcwYr8RH4iP5HfsiO/bqQycPrY
sBXuGvWcliBQ3CfuE/eJ+5Yd9y1+sqfIT+SnZX5a6RBpUysd4voOTfZ8SOa7bONRz26ijB75
TeXcHUV+ivwU+SnyU+S34Bd7KvJT5KfIT5GfIj8t83uIVzoo8st7NUHORKnIT5GfIj9FfmOK
/DgA3BZY/W8bkCJeqILVcZ0JLzfEu3YclgQ2aX0g33tU4s1GocLrdrpVhNbj3YN82RFeMlR3
tIY3DuFlh/FNRHhDUawLbw1CHQEvNCx9Mm2zyZ4a9tRkT73aU283ixypt5vxBqwXvGSzxn1h
kV/HYeN5u5mGPXOO5oa0TZGfIj9Ffor8xhT5Td0yP0V+ivwU+SnyU+SnV3vm93YzRX565jck
2ptfVpGfIj9Ffor8pjzyW/Sw5/284IV0ixee6dWeE7/8QeQn8hP5ifymnPwW/XYzDXtq2FPD
nhr21LCnhj3zG/bk9JNt+FEHkZ/IT+Qn8hP5ifzyI7+FPfNT5Df/WZf07jmphj017KlhTw17
Tuyw58Iiv3GSn575TQt5ivxEfiI/kd9iyI8fmJ+Qb9mK/KaFsMa5HyI/kd+yJL+Sbx7BYnWP
75XWrdhvMeyXxZfcFzbuuejpnnrop4d+euinh36RJPWKF95t9YqXCXvFyzhDP73iZZzh10NZ
l0I/hX7LMvTjLUyRnyvrhsTQTnnkt2jy6xz1TaOJX9R3fyQr8hP5ifw07Cny0zeNppLg7o/0
epvIT+Qn8hP5TTn56Zlff8NXet/74ER+Ij+Rn8hvyslv0cOemvCiCS+a8KIJL5EjNeFFE16q
0vkJm/CiyE8R330RX38sFPkp8lPkp8hPkZ+e+emZX2na2sXvL0de9FXTBOMV+SnyU+Sn95tN
6vvNFPn10Y7S+yJARX6K/BT5KfIbU+Tn47KJKlS2qX2NT6c3sR/dFpXxlfPO1aZqQrc63lVV
Xda2CVVtDNmpLayvnYXJVKWvu+XrtkRI5kyJtGw7k6k86gg+2NInU9mGEt32qm6Ndd3ajRIb
821beVOFoGd+Ir37SK8/FiI/kZ/IT+Q3JvKbnE+58w0/vgjOgo29CY1GPTXqqVHP1hqHS6Is
uy4kegfoszYa9dSop0Y98xv13MYvttYad0321CM/kZ/IT+T3YOSX66jnoh/5ifxEfiI/kZ/I
T+Q3qeSnR379Yy6l9z360yM/PfLTIz898pvyR36Ljvw6xx95tScn3fiiLa11vqmtDW3dPT/0
TVU3zuEZYtkaxsAimryPgchP5CfyE/lNLPlt42d+90N++qjDtJC6yE/kJ/IT+Y2J/Jb+md/C
yG+ckZ/IT+RX+Yoj6WRPH4LB8hysp6n4dWeaAtb3uLIMoSTuYHFY54NxAVs1tSN8aKoMFuC4
xrS++7QoTL50rce6HndvqarESiDvA5b5cHkQ/CrXBqwhCnVTlml7Fdb8+FCjFaVJptq6xlvL
upvUhhp5i4VEJZYadVU1thb54aC6ovUutM5gNRWWWPHgxMO4xR9X6O1mervZA7zdbOnJr1v5
p2V+00JIS7kfJKp65Qj/Nmzenslow1r+vWfLfz+8h79tpuwx73eW5b/tIPNduno2bL4n+sUi
P/Zn1+TT/3DosdS4/U5YJ6XPR3VBf84eYbu7nDe6cXT56Dmja/H3alooe18/unR02egSWC8d
XYNfLhmVo3rUjBz+OpZY0ZfYwt7XwHSHOZQtqe13A+p4Fmq5P68C270MrUC5vU4ezY1O2WJr
xeiq0XWjK/j7/ueghueh9PrRc+Fhtl6SpbeUh81hS1ejJraFLVk/evboytENsFw9+sE9V+Iv
9/Y6/A7vnfrcDX09O9wyumW0krntU7rLTfC4Hkfveagrltu7GlmU8aMKfw32vpyX1n1NuaQ7
3ICjeO9ZH1urtos17T3a8X5wuN392Oab+t8fMd8I/au84t763mfsv+5Hf4j20ai8Ldm/yXIP
6b/jsfX9BrTgDSg7B3k1ZKfot27dS2La3UlwZW++Efn7QfQD2mIV6Q99H+zfPg9WYCu/77Qz
f+jP24XzSj0+6vfdq+bfo4p55aL6qC0NyG+Hf90hQWaHDaOV23OPV9yIq+7aLa79dShxMoT/
eM/s/+0w2n6004bt9uowuQ7mU9JP80ttd+8ZWyh+BpU7dOef+5XNfYvuP+3q2zf++Azc47kv
L4Z854uXboLMnPzXd6z+4Ccu2fTGQ5498709X7P6db91zaYr7zhjZvdd71r97XNv2HRr/bE1
Oxz9/tWXHGQ3Pf8zm9b84Ng9o/7lF75+I/VXvP8bG1f8/W8c+c03ffMI6uc8/tsbn7ffDkcm
fQ30d6T6N7H+Yw5ev+nEJ5z/7oP+4IOrUxs2sQ1pu5vmbXcjt/uhj5yx6XGfv2bTZw++c/Wz
LvnYxie8/IZN3zjwvatfdvvtG9ddVm9iG2Bf09v/6i//ck1v/8CZz575u+2fuek/b3j56v2+
8F9rUtvecc4t566i/vY/+ucjUP9MX//63yuL2fPXb3rFm/4g1v93a4qZk77z76tSG2bmtWGG
bUjlZ1g+tSHaU52x/Iv3edYM5bxjXrWabevrTG1YwzaktvFYHfn+28wMjzO3+8T9rp255Rtn
zPzXSW9Z/Y0/uWHmr27/2JrdD3vX6rf/0vqZA9/4hHcf//rfXc3yPBcsz3qeHN53FM9F8t3U
+/717R/bSN87v/i0TZCZFX//6DVnHXzlpt/7l5Oj/toVz9v08j968Rrak47zem+ZTdSTb9Th
t+ls+NMOv430SXr0p866+zLcJv1pP+Yxd26kzNPjdlkn2jST7LEcddQxw9+oYzsz3N48Pfqi
PpaPeiof62Eb+jpTG6Kd+8q6WE9qf9R5Xg4+8elH9VcT7z/sm1Go75CEOnmIeaa8nVCo88ZF
nekuEJblXYG/Uaj3v+0GvfelviLlmbLu3SHs8/E3CnX+xnTPpO+FlL/tnYQ677rMM+XVT6FO
BqHOdP8k1A9IQv1hSajTh3mm3BcKdW6D/g+H9PWTW7lN7h/3+cAk1B+ZdKYHJTk42ViO+iEp
z5S3bcqhkMOSzrSvk/rKlGfKbbLs4RD+RqG+MqX87Ygk1B+ddKZHJjkq2ViO+tEpz/SYJNT7
Y0W9P4bUH5OE+rFJqLMu+rM9rJv/iKfHJqF+XLLxnFOnUCfrU6jzvFNnekIS6sQB80zJfxTq
xAjxc2LSmafO32nnOWSeQp04os60TOneSWeeuklCneebeaY2CXXigXmmLgl1YoXHq0o689RZ
htvlNtg2CvU66Uy5fxTqPAYU6k3SmfbHjbpPeaY8zqyPbaUPhTrbSJ1pm4Q628M805CEOtvK
/CpIX5766pRnuiYJ9ZmkM51NQn1t0tch7ctTn0t5ptwHCnXuA3W2ldulD/PUiWVeJ6yTQp3b
op154ptCndsmRonNfr+ocx8o1IlV6ky5DxTqvEaoM2U9FOqsm8dlfwjrps6U9R8AeRikv3ao
n5TyTHk9UKivTEJ956Qz3RVCP953+BuFOn/jvvJe0R9b6uuSUD846Ux5HCnUD0o6Ux5bCvVH
QviPeNkuCXXaKdRZ9omQ+f+OfsVldx/2w7d/+P++7NbNf/Op59z9yAOu+KNb1ty6+eUvueju
f5j7kw/94OQX9Poq6q9bc+DdH33by1e965if2WxPOOzu93/mVWuO+ocXbv7wt468+/Pbnbfx
jre/cPPzf/qiuz9w0W2rWf7gl15092f/6Y7o++lbL7v7LXd/d/W8bbXc1uN+6/l3719tt+r/
feyWzY884H95toP2x5x00qrXwJ/1XLDDdz70gZ/v9A2n//KHz7+1099+0jlrPvLOw+5mG77/
zl0//JFw4N1s2/f+/qKNt37jyLvZnld99NgPf/tvuzrf8KYbPvS/P3vT3Y+64Za+zCzLvOfP
/3z1v9518eyXv3fr5hf+2tmrv7bu3NkLXv6CzR9y+6w6/PROT22YZXu+sv8/f/i/39mVf9tv
fSAUuzxx9ut/+4LNP3zb7qsunDlwlm24+JHvXLPLXx86y7Y97hGHzd76Z78Sj9Vn9puZ3e8d
ozUHv/6nN//fk86dXf+a4z7MbZ2L7fDcUH8d6qDOer701sNmT/YXbmQ9T/r9i2cveOVdq9nO
44+7cPMR13129qO/9+7ZO//ixs2jw2+YecofvHb2kBddv/mQA86eOXW3t89+bc+bN1/x3Dev
OeVvXjr7Nnv95uqVZ6/6uc/cObv/vjdv3v57t22kfcfbr9/8m884ZRPLr/j0jZv/59VXbmI9
5a0Xbn7J7D/ezfpXr//s3V849sLN1G98/jWbVn38xs0sc/JFZ2/a4w+v3/yWj7519j1/86aN
//GlmzY/46BfmD3xGc/70FuwPW7r7KtfveZ3/6mzn/Lt02dmP9yV/5XLLpm54QtdPUd++t9m
j9vrgs1nfur1s37dP85+5JZuWzwG3b8Na//u+Z+d3fTYC9eyDefdcuHar8/9Y9z3z3zixrWn
/bfnxjZ/693Xr33h0y7cxPZc8IWb1rpX3bWR7dnhqut5Gxl94JffMfvJ/3nT2u0Ofd0a2o//
o+vXPv43nzDD8l//3I1rP7PPpfEYPhHbuf2Gz8Z9Tw1AsmHzwx551cz1n7pxLff9je86d+bE
379+LX3v+Pyda8764k1rY503fXHVK+z1a7nvZzzjto0Hfrmz/9XbTtn07U1d+QM3PWvTJZ/t
6vn1k//x7i/f3O0Xr93tIeTMHSE7JeE9gzrvH7yvkPNWQMiF5EZyJrmP3EbZB0Le2m+e8D7X
39ceDv0RkAOT8B7B+wjvMbz/8P5E4b2Y6WGQlZDDkxyBtL8/817K+yxtvf1o6BTeP3lP5f2Z
9yDyHPmPfNjzJfmzl57rei7jPZncQc7g/Yu8EZZIVmE7lNVJ1iCdgfDCJJjWQeYgJ0FOTnIK
0geSU/H7aZDTIWdAHgd5POQJkDPnye3QPwo5+31fn3nEG78+89h3f23mUv+vMye98d9nfvjv
X5j502u+NfNLH7xr5pBPfnLmTSvfNXP06u/E/Fev2n2WeaZ7/PKxM3sedNCsP3t9TN/3lG+v
+ZPv3RProX23H35g5hM3vn+GdtZ/1sdfs5r10Y/lmL/p/G/P0P/XvvXDmX++802r37XXf87c
vb9bw+19ot5/5uqjvziz7yu+sWrdF+6a+av3fCX8x9fePPPwj7xozccu2T/mNx6zd8yXR712
9Ucve9fqz1T/tobbO+306+N23zvj1tD/iFeu56Ed/eALR89+4k8/PrPuIzvNzmFfL7z8sFnu
6ze+6WfZlpe+8JyYf9PKq+Lv77zxutmzcIx+4RefFP3e8Sdt3K/PXnNRTNede1k8HhtvvGH2
hMO/OPO+fW9fw+Pzx5/7t1XMj977lfDSv74rbpv7yd+5/2wn82d+9LpZtpv10M565t5o1tCf
Kf3/5+77x/I8nqfdfN3sGR+7Y/WqR181+7I97lr9r9++dpZx2rO+e2VMt/uFc2Z/u3z/6n+8
4IyY3+2HfvbKv/jg6k+/85iYf+/Nh8Xfz955l5i/+bM7xXo+tdc9M6z3qJ23i3bignmet5cd
+5rV//D+r8YYkOfjdUffufqjH/5czPO8fPI771n9vpveFPM8zq99zR+s/lxRxTzPE3//7mtP
i/Enzwf9eb5uef3LV7/1xr9azfaz/rmf+YtY75XvPm/1LZ/+Bs7RqWvev887Zv7Ph4+YecmZ
/zFz7fdcTNde9KYZ2l/0nd+YYbmz3vy5GbZn+w98Y4b1PPv1X51hez75D3++iu1g+pnvHRHr
YTtY/zO/feFq1s/tc7t/fMXfrmL9TFk/y7N+lmP99GP9LM/6We9eJ/xH3A5T4qS1r1pN3HD/
Pv7V7ryc9vXuvGzY/o2r+Xv58b+I+3sGzu1vrHtLbAP3vwBWmL8NWPnSPu+K26SdbWH6h09Z
P/OWu353NdvI/D8BEyz39jd354XniceTuCeumPbXH/O8Dpknvnk+Np/R4YO45/k65Fc7fPB6
4O93fGfniANeJ9wfXp/Ew4r/HEU7r1/igtdUzynbJ53cQqG95xjyC7mFQp0cQ53pfK7hbxTy
Dn+bzz0s33MPdXIQOavnIf5GISfxN6bkJOrkJXIY+8sU6uQo6j1Xka+ok7N67ur7t7SRvyjU
yWMU6vShzpTtpVDnNuhPvmN9FHIdt8n9I7+S/yjUyYHUey5cCZ182JehTv5jnumjk/T8yDx5
si9P/eiUZ8ptsuwxEP5Goc7fmPK3xyShviWnHg8beZU8S6FOjqXOtOdY6v2xos5jsCXv0k7u
pVBnXfSvIayvgXhIm4Q6eZkpOZM6hTpBSKFODqXecylvvNRnIdSZklsp1NdB5iAnJZ156vz9
ZMgpkFOTUD8t6UxPT/kzks48dXIuhfrjk86UHEyhfmbSmT4xCfWzIGdDzkk689RZ5kmQcyHn
JaF+ftKZXpCE+oVJqF+UdKZPTkL9KUln+lQI63sahD4U6hcnnenTk1B/RtKZXpKE+jOTfinS
vjz1Z6U802cnoX5Z0plenoT6TyX9CqR9eepXpjxT7gOFOveBOtvN7dKHeerPgVwFeW4S6ldD
roFcC3leEurXQZ4PuR5yQxLqNyahvj7pTG9KQv3mpDNlPRTqrP8WyK0Q1k2dKes/CHIwhNin
UH9B0pnWSaj/dBLqL0w605+B0G8PCH+jUOdv3NefhXB/KdRflIT6hqQz/bkk1F+cdKY/n4T6
SyAvhdwG+YUk1GmnUGd5/tuuS+L2sKW1zG+fbN1vG3iZ3Wuz8beu3A7Q7yu/YS39els1r9yO
0PnbzsnGMr2NOrfL/E6Q/jfaqPe2FdD7cqyH5XehCeVYprdRp415/s48z29frrftmmxsP3WW
PyjZWHdv67fB32ljnjhifdR3g9D+CEi/jd7GlDambD9TnvO+XG/r9437S53CeyvLkQ/ow3Q1
pK+vt/X1sW6WocxAWI718HfKnhDaep35VcnGcsxTeC/vt7EXNMosTWk/9oZGG1Paep3pOppS
uX2gsUx/XKj3NqYsx3RfSJ/SxnK97ZHQ+3L7JfvDko1lehtTlmPKvkSf0sZyve1A6H25A5Kd
KW0s09tOSDbWw+3R3m+315leB6Ev28/fKQ+H0EZs0M58fwxo68vwntRvl2XYttNpSm3ubafN
s7EeHpNTkq0/vrSdlGzEM+silnm/YX3EZ297dLKxHP1YZgOE5Vimtx2SbMyzLuZ5L+rL9bZH
JVu/PeZ5T+vLsX7aDqUJ22CedTH/AkhfrrcdlmzM04/5W5KN7etthydbX/dK5J+dbKybfish
R0K4jd5vJXK9L+tjOeaPgLBc78f8UcnGcishtPXHj8eUNubXQ+jL7bIubvNoSF9fb+vrW4lf
aGOe/NL7sn76HUMT6mOZ3maSjdvgNlnm8mTr20XbY5KNZdgO5q9JNpbrbccmG/NsB/PPTTaW
622PTTbm2Tbmy2Tr20bbccnWt5/54+eVY9to6/eD1w/Lskx/vdHGcrT11xavS5ZjmQLC48I8
94v5EyG0sVxvuzbZWI77xTJ9m1mmt10Bnb79vrLMc5KNx55tYXuvT7btkXJfLcQlG5Pe9qJk
YznuK8tUydYfI9rOSbYdkLIcy9TzbNx/5ptk648lbWcl2wqkLMcyfp6Nx4n5Ntn640vbmcm2
J1KWY5kwz8bjyfyqZOuPOW1PSLY9kLIcy6xJtt2R8hivhswkG8v1tr4c/Whj/nEQHvvd8Jc2
+s1CaNsLf2ljfi2kt/H8ML8OQhvL9La+vr2TbR3SOQjL0cbzyPxJENro19uelGy8v9LGMifP
s/F8M39KsrFMbzs32fZNNpY5dZ6N55v505Ktxw5t5ycb7/UsxzJnJNv+SImL0yHXJhvL9ba+
HP1oY/5CCPeNx5n7x2PyeEi/v8QP8/3+slxv688vzzltzPd4OT7ZmH8ihPWxDLHH/KUQ2liu
t52VbMclG/NnJxvLEI/MPxNCX5brbeckG68Z2pj/uWTjsee2uQ/9secxpY358yCsjzbim/n+
OLNMb+vbzONHG8tcAKEvbcQ88/0x7a8V2i6CsByPO8uxzPMgtPXXD8tcmWz05fVC25OTjXle
L8xflWws19uekmzM83ph/qnJxnK97VnJ1l97LHN1srEMryvanpZs/XXG/MXJxnK81mh7erKx
HK81lvmpZOuvR9oum2dbB51+tyYb61sHoe0ZEB6XdfjL64/5n4bQxnK97ZJkIzZoY/6ZEJaj
jWVp6/eXuGC5Z0J+BtKX47G5FNKXexR07sezIX2bD51nuxw6fVmO+8cyt0BoezT+0pdl+mNA
20zKX4OU5Y7FX5538kl/zh8zz9Zjg+V43lnmORD6HoW/tDHf44C21Sn/XKQsdyT+0sZ8f35p
Y1uY79vC7RKX10L67T4MOrnsOsjzIayPtpMgzN8EoY1letv1yXZ4sjF/Q7KtTDbmb0y2nZON
+Zvn2VZCp219su2ClNvgNvtyh0Dnsedx7zFE27qUfwFStu9g/F0HYb7HEG3EAfMvhLDcQfhL
G/M/A+ltxAzzP0sTyj0Sf2lj/ucgtG2Hv7zvvIg5SF+Otg2Qe8vdc9iLMGf925f85z2bf/Ci
7//gaf+8+eIf3HPP1/8HjCeesc8rV7Yv/tKu23/te/fc8zc77Xb6Pfdsrg6Ad//v6W+4bd3x
r9mJjRzd3htHg+ZO3uu1dWV4fTzq/T8eCcrW//Gc/+VJFoU4kzTOQY3n59Tksus817xmkraA
DRnyYsj8GXY3HRZm1l70tBmz6+9wtiBn/MWR/E/+97NnKLTPn53HsvSZZ9/Ekf/5s/xSmU0s
84UvXzrzg71v3tjr39/75jXUU/n49CVtN9aTtht92c5+NmJqZ2+/35mMKLMJ245lsJ2N2HbU
08zBWD+339uxrU0Utod+9Kd+935v3khJbd40r/2b+vanMnFfku8My6c2RD3VH3WUj/Wm+qlH
39SeWCa1Oeo4Jpz1GducZn3O12fSMb/fGaDJN5bhLMx+NuXWZlBuMbvz3lmcyb6G25o/W5Mg
53WyfRLqOySd6Y5JqO8E4VXDuyCvDgr13ZJQX5GE+u5JZ0pfCnXWuQeEde2ZhDrr2wvC3/ZO
Qp1l9oHsC9kvCfX9k1Dn/Yl5pmQHCvW+Huqs++EQ1vGIJNQPTDpT3lUp1HknplDnnZo6U95n
KNQflXSmh0JYH9tBHwp1toU608OSUGfbmGfaH0/q3F/meVz78tR5bJlnujIJdR5X5pny/FGo
85xRPxyyMgn1I5LOlPtAoc59oM62cjsrIcxT5/Hnvj06CXUeS+aZHpmEOo/tUZCjIf2xot4f
T+rHpDzT/phT788Lddb5GAjr4rGlUGedx0L4G9tMoc7f+e+xkO2SUOc+U6hzPynUj0s6074e
6qyb+8Xtc78p1I9POlNijkL9hKQzJc4o1Ik3CnXimzpTYpr1cR/pT6HO40KdaZGEOveZeaZs
G4U695k629yXp859Y57piUmo8x/z/LdjEurbJ313pH156mw380zZLtp2SXnaqHN/uC2WYxme
v/n/tjbj6RcfsX7tLhdfuOmmq14z+8E716+lz5MOf/Xs76xcv/YjmM1E+/wZTPNnVO255rxN
cwet38wy64v6Q3945/rN9P2bPz1rZq9DO/t9bdiwdv7Mr/kzwn7q4PWb/+4rT4rb+h3U8cnv
vG0V67ngyPWbLzenx7bNn6E2f5bTd3/6KTN/fsD6tWzDzq/8/qpfxT7Q9123nbFp7aM7+7w2
bO7xyGNN4bVJ6c/DTtApPJ4UHlvKrkl2Q0pZkYTnYilkD2yHsmeSvZBS9k7SXx/99cD7Qn8P
7O/HvB54v6Pw/rAUchq284uQl5502SyS0QGvuXT2yaFas8+6q2J+46orYv69T/3V1fx9n52+
t5q/j247fg3zu/7aRVjNUa058gX/MMP8w+s3xPSUR3xqhvb3X/G6mD7jNBPTX7/rhPj7qvX/
EtM7rvpitDM9AHXTr/q1X1u9n/mXmRWo+4iX/frMbTscPvONm786cwnqYMo6aaewHH0o1FkP
hWU+/4xzV3O7TFkHhe1l/SWE9XN/uN0voQzrZ0pflmX9LMe66cf6WZ71s96+LUxf/dbvxv1p
7vph3J9PPnH7ePxOvmfHePx++JaTY/6sD54U80/95hExj35GzPN4vAfH+B/u+PrMTji2PJ4/
ePHnVx34N2+deePNh9wrPO60j37+86tYjueFfv+y4t8wK+WEGaY8B/SjsL6jUBfro87tUFiG
ZXk+mHIbLM/6WY7104/19+eqP7fcDs81r9X+OqXeX6fzr0/q/fU5/7qk3l+X1Pvrhzqvof5a
6q9v2ni985ritd5fV9R5rfM33iP68tS5bf7+QNtlvWxHv82tbZfXL6/d/rqlzuu2v4Z7Puv7
MbyGqfMa7q/nnrNpY9+BeabkddZH3qcPpe9DUWffou8fUH9UyjM9NAl19j+YXwnpy1M/POWZ
HpGEOrmbeaZHJqF+VNKPRtqXp35MyjPt703UuQ/Ms63cLn2Yp96fn/5+yHPFc/cYyLGQxyah
fhyE/46HbJeE+glJqBdJZ0oupVCnL4U669wewn/EJIX/WCd/47b78n07YHrA7fbb6tuwte2W
qMdAbBLqLulMiUUK9SrpTIk/CvU6CfUm6Uw9hPW1EPpTqIekM12VhDpv2MwzXZOEOi9e5nkD
6stTZ+eCeabrklCfSzrTk5JQPznppyBdl4Q62808U7aRtlNTnjbq3B9uax2EZfiP54f/2LZR
GqXZPur9bxvYnFFvuyD+9qOzFIhH+rIMzzvr7Mp3Mw12TPkOE1253tbXx99472Da18cyvY3n
j9vgPWcXCH97KoQ25on5vnxfrrftzmKpHOthnayHNpbpbUckG+vjNdNvi+VYprc9el451s3y
T0k2lultrJu+3B5t/bZ6G8vSdhSENraf5bitCyG0sQ17QFj2cZDeRtz226KNZXobU9pYN3XW
eTikL7cXNJbv66O+d7L1vizT2/aHTl/+RhvTvr7+Hs3yp0BYjvdV3qP7Omhjud5WQO/LsW7W
yd9p6+/ttPFe1pc7ABrLnEYTytGvt3F7tDHP+36//b5cb+P9mjbWzbL9tnoby9F2GIQ2tp/l
uK3TIbTx94dDaD8R0tvIK/32aWOZ3sb7R1+O921up9+3no9oow/LscwjIX0dtLFcb2ug9+UO
gtbXQRvL9LaaxVJ95DDWezxNsLFMb6MPbcyzXX0dfbne5lgsleOxZB3H0QQby/Q21kMb8+RG
5ldD+nK9LSQbjy/b1tfBcjwetPV19DaeG/r354hlelu/bzy/tFFWQujLa4H2lZAeu7T1Zfpr
n9cebcz31zmvM9qYPxLC+mhbCWG+v377umg7AcJyvPZXQljmaAht2+Ev7cwfA+ltK6HR9hhI
b2NbmZ+hCb4r8be3HUsTbMyzvczPQvpyve2xycbzQBvz/XmjbWWy9W3mMWc5llkHYX0sx/3j
Me7L8VrgMeH13F8LvEZ720nQ6Usc08YyJaS38Tgx318f/fGlrfcltlmOZTyEvv2xtMg9MdmI
HR472nqc0saytPVYI2ZZjmUqCOvrzwPzT0g2luO5oa2/jnhd0MZ8fw2yfbQx37eP7aWN+cdD
+jbzPLaQs2nCdoljto+2vn209eX6a4Z5nttVkN6X54h22vpytPXl5qBzG/zL870Gch4zsG2H
v72txxUxRBvzPYaIAdqYjxXBl3nigvknQVgfy/W2dTTBxrb0+OnbwrbRxvw5EJbbB395vHi+
T4bQxjxxxvzjIX253nZKsu2LlDbmT022Hp/MPznZWI6Ype20ZOO9mjbmT0823u9pY/6MZNs5
2Zh/6jwby9L2uGTj+ea22d4nJBtxRRvzZ86z8Xphvscuy/S2p6VyxAVtLHPWPBuPIfM9Dphn
Odr6Y8pjTBvz/TnieaON+XMhPKa08ZpkvscGy/S2vi0wRRvLnM8MfPl3RwjzFzADG/P0pe1C
CG274y9tzF8E6W08zsw/hSaUY57laOvPG48Lbcz3bdkFOsvSrz8f261/+t/j/w1Pf/XKQ+au
2/Ej++74qfUztKyfe3XM7nJ75Ga4xH/r/+nl624/YLcIy9t7YwbPCHnNLPwfkdk9I+x8hj+T
fOBtDauP1/GuG276H2a7rtYNa/919Ymzv/KZU3HzIAuu2LADf7iHvWW+6eWq131+Iw1Xve2X
1szXV87+gLe0H7G/DW816ctQx5tY4m2L9fQ6fbptYBPoVc/fxok7nLjpHd+Y2cQyz/v0xzde
vOHyqH//zN038q0utH95vz3X9PqzP/iJNX2Z377xxJned3476HPfPu0U6/3jg97N22zUv3f9
XrGNm59zycb5+m1/8sRoZzt6/Ufr2n40+taz2r4u6vdfbpfRb5146Zq+HPV+O2z/1uzzy/T1
0rfX2Zb+34peiek+G3hqt3yv067zyrz0229cR5lnwsk38Xa9/XG7zFzzv/4r7jt/n5+/crs/
hIX3FMoz43WZYPQjVW0903Hafb/H+9M69F4gGyBvhfwx5EsQ0s8+kJWQErIOcg6E270OsgFy
O+TVkDdA3gp5J+S9kD+C/DHkzyB/C/kM5EuQr0K+CfkuhFS2I2RXyB6QfSAHQA6EHAJZCTkS
8hjI8ZASUkFayBrIOsgpkDMgZ0LOgZwPeTLkYsgzIZdBroRcDbkOciPkFsgLIRsgL4a8BHIb
5HbIL0J+CfJKyKshr4XcAXkd5A2QN0LeDPl1yFshb4e8A/KbkHdC3gX5Hci7Ie+F/D7kfZD3
Q/4I8iHIRsjdkD+G/AnkY5A/hfwZ5H9A/hLy15C/hXwC8inIpyGfgfwj5HOQL0C+BPknyJch
X4F8FfI1yL9CvgH5JuQ/IN+CfAfyXcj3IN+H/BDCbsN2kO0hO0B2hOwE2RmyC2RXyG6QFZDd
IXtA9oTgVYCjvSH7QPaF7AfZH3IA5GGQh0MeATkQ8kjIQZCDIYdAHgU5FHIYZCXkcMgRkEdD
joQcBTkacgzkMZBjIY+FHAc5HnICpICcCCkhBmIhDlJBakgD8ZAWEiCrIKshayAzkFnIWsg6
yBzkJMjJkFMgp0JOg5wOOQPyOMjjIU+AnAl5IuQsyNmQcyBPgpwLOQ9yPuQCyIWQiyBPhjwF
8lTI0yAXQ54OeQbkEsgzIZdCngV5NuQyyOWQn4JcAbkS8hzIVZDnQq6GXAO5FvI8yHWQ50Ou
h9wAuRGyHnIT5GbILZBbIS+A/DTkhZCfgfws5EWQDSePNkBGP4cUMnoxUsjo55FCRi9BChm9
FClkdBtSyOgXkEJGtyOFjF6GFDL6RaSQ0cuRQka/hBQyegVSyOiVSCGjVyGFjF6NFDJ6DVLI
6LVIIaNfRgoZ3YEUMvoVpJDR65BCRq9HChm9ASlk9KtIIaM3IoWM3oQUMnozUsjo15BCRr+O
FDJ6C1LI6K1IIaO3IYWM3o4UMvoNpJDRO5BCRncihYx+Eylk9FtIIaN3IoWMfhspZPQupJDR
XUgho99BChn9LlLI6N1IIaP3IIWM3osUMvo9pJDR7yOFjP4AKST+0/1Z9+ftgYUdIDtCdoLs
DNkFsitkN8gKyO6QPSB7QvaC7A3ZB7IvZD/I/pADIA+DPBzyCMiBkEdCDoIcDDkE8ijIoZDD
ICshh0OOgDwaciTkKMjRkGMgj4EcC3ks5DjI8ZATIAXkREgJMRALcZAKcsrcnbucMve6Q0+Z
+9wpp8zd9oJT5t61+ZS5Zx1w6tzf3nLq3CH/59S5G55/2tweO58+d/hdp89955lnzH36mMfN
7Td6/NxOX3v83L5fecLc27515txxDz9r7oQnnD134h3nzP23f3/S3KsuO2+u/T/nz93ySxfO
PeLkJ899bd+nzv39fz5t7tP/9XT0M575I7Lq/IvnwhsunHtD86S5rxxz5tyGy0+fu+V/nzT3
wnfPzn30Pavmvv/VZm7dhW5u12+dOPeozcfP3fG+Y+c+9vGj52YPOHLuz249fO7Jo8Pm9v7N
Q+aq5xw0Z844cO5Vcw+f+855B8wd/bP7zX337n3mnvawveeetGHPuW/+cPe5i1+9Yu4v3W5z
P//VXeY++bs7zx348zvNffiKHefM03aY+9bF28+94urt5n7xZaO5Ha64Z91Rn/rBuv/2lO+v
W/P/vrfuG3f957on3vzddd09QH/zPgLCtDCdN0KHt06YFqaHoyZvD2FamM4bocNbJ0wL08NR
k7eHMC1M543Q4a0TpoXp4ajJ20OYFqbzRujw1gnTwvRw1OTtIUwL03kjdHjrhGlhejhq8vYQ
poXpvBE6vHXCtDA9HDV5ewjTwnTeCB3eOmFamB6Omrw9hGlhOm+EDm+dMC1MD0dN3h7CtDCd
N0KHt06YFqaHoyZvD2FamM4bocNbJ0wL08NRk7eHMC1M543Q4a0TpoXp4ajJ20OYFqbzRujw
1gnTwvRw1OTtIUwL03kjdHjrhGlhejhq8vYQpoXpvBE6vHXCtDA9HDV5ewjTwnTeCB3eOmFa
mB6Omrw9hGlhOm+EDm+dMC1MD0dN3h7CtDCdN0KHt06YFqaHoyZvD2FamM4bocNbJ0wL08NR
k7eHMC1M543Q4a0TpoXp4ajJ20OYFqbzRujw1gnTwvRw1OTtIUwL03kjdHjrhGlhejhq8vYQ
poXpvBE6vHXCtDA9HDV5ewjTwnTeCB3eOmFamB6Omrw9hGlhOm+EDm+dMC1MD0dN3h7CtDCd
N0KHt06YFqaHoyZvD2FamM4bocNbJ0wL08NRk7eHMC1M543Q4a0TpoXp4ajJ20OYFqbzRujw
1gnTwvRw1OTtIUwL03kjdHjrhGlhejhq8vYQpoXpvBE6vHXCtDA9HDV5ewjTwnTeCB3eOmFa
mB6Omrw9hGlhOm+EDm+dMC1MD0dN3h7CtDCdN0KHt06YFqaHoyZvD2FamM4bocNbJ0wL08NR
k7eHMC1M543Q4a0TpoXp4ajJ20OYFqbzRujw1gnTwvRw1OTtIUwL03kjdHjrhGlhejhq8vYQ
poXpvBE6vHXCtDA9HDV5ewjTwnTeCB3eOmFamB6Omrw9hGlhOm+EDm+dMC1MD0dN3h7CtDCd
N0KHt06YFqaHoyZvD2FamM4bocNbJ0wL08NRk7eHMC1M543Q4a0TpoXp4ajJ20OYFqbzRujw
1gnTwvRw1OTtIUwL03kjdHjrhGlhejhq8vYQpoXpvBE6vHXCtDA9HDV5ewjTwnTeCB3eOmFa
mB6Omrw9hGlhOm+EDm+dMC1MD0dN3h7CtDCdN0KHt06YFqaHoyZvD2FamM4bocNbJ0wL08NR
k7eHMC1M543Q4a0TpoXp4ajJ20OYFqbzRujw1gnTwvRw1OTtIUwL03kjdHjrhGlhejhq8vYQ
poXpvBE6vHXCtDA9HDV5ewjTwnTeCB3eOmFamB6Omrw9hGlhOm+EDm+dMC1MD0dN3h7CtDCd
N0KHt06YFqaHoyZvD2FamM4bocNbJ0wL08NRk7eHMC1M543Q4a0TpoXp4ajJ20OYFqbzRujw
1gnTwvRw1OTtIUwL03kjdHjrhGlhejhq8vYQpoXpvBE6vHXCtDA9HDV5ewjTwnTeCB3eOmFa
mB6Omrw9hGlhOm+EDm+dMC1MD0dN3h7CtDCdN0KHt06YFqaHoyZvD2FamM4bocNbJ0wL08NR
k7eHMC1M543Q4a0TpoXp4ajJ20OYFqbzRujw1gnTwvRw1OTtIUwL03kjdHjrhGlhejhq8vYQ
poXpvBE6vHXCtDA9HDV5ewjTwnTeCB3eOmFamB6Omrw9hGlhOm+EDm+dMC1MD0dN3h7CtDCd
N0KHt06YFqaHoyZvD2FamM4bocNbJ0wL08NRk7eHMC1M543Q4a0TpoXp4ajJ20OYFqbzRujw
1gnTwvRw1OTtIUwL03kjdHjrhGlhejhq8vYQpoXpvBE6vHXCtDA9HDV5ewjTwnTeCB3eOmFa
mB6Omrw9hGlhOm+EDm+dMC1MD0dN3h7CtDCdN0KHt06YFqaHoyZvD2FamM4bocNbJ0wL08NR
k7eHMC1M543Q4a0TpoXp4ajJ20OYFqbzRujw1gnTwvRw1OTtIUwL03kjdHjrhGlhejhq8vYQ
poXpvBE6vHXCtDA9HDV5ewjTwnTeCB3eOmFamB6Omrw9hGlhOm+EDm+dMC1MD0dN3h7CtDCd
N0KHt06YFqaHoyZvD2FamM4bocNbJ0wL08NRk7eHMC1M543Q4a0TpoXp4ajJ20OYFqbzRujw
1gnTwvRw1OTtIUwL03kjdHjrhGlhejhq8vYQpoXpvBE6vHXCtDA9HDV5ewjTwnTeCB3eOmFa
mB6Omrw9hGlhOm+EDm+dMC1MD0dN3h7CtDCdN0KHt06YFqaHoyZvD2FamM4bocNbJ0wL08NR
k7eHMC1M543Q4a0TpoXp4ajJ20OYFqbzRujw1gnTwvRw1OTtIUwL03kjdHjrhGlhejhq8vYQ
poXpvBE6vHXCtDA9HDV5ewjTwnTeCB3eOmFamB6Omrw9hGlhOm+EDm+dMC1MD0dN3h7CtDCd
N0KHt06YFqaHoyZvD2FamM4bocNbJ0wL08NRk7eHMC1M543Q4a0TpoXp4ajJ20OYFqbzRujw
1gnTwvRw1OTtIUwL03kjdHjrhGlhejhq8vYQpoXpvBE6vHXCtDA9HDV5ewjTwnTeCB3eOmFa
mB6Omrw9hGlhOm+EDm+dMC1MD0dN3h7CtDCdN0KHt06YFqaHoyZvD2FamM4bocNbJ0wL08NR
k7eHMC1M543Q4a0TpoXp4ajJ20OYFqbzRujw1gnTwvRw1OTtIUwL03kjdHjrhGlhejhq8vYQ
poXpvBE6vHXCtDA9HDV5ewjTwnTeCB3eOmFamB6Omrw9hGlhOm+EDm+dMC1MD0dN3h7CtDCd
N0KHt06YFqaHoyZvD2FamM4bocNbJ0wL08NRk7eHMC1M543Q4a0TpoXp4ajJ20OYFqbzRujw
1gnTwvRw1OTtIUwL03kjdHjrhGlhejhq8vYQpoXpvBE6vHXCtDA9HDV5ewjTwnTeCB3eOmFa
mB6Omrw9hGlhOm+EDm+dMC1MD0dN3h7CtDCdN0KHt06YFqaHoyZvD2FamM4bocNbJ0wL08NR
k7eHMC1M543Q4a0TpoXp4ajJ20OYFqbzRujw1gnTwvRw1OTtIUwL03kjdHjrhGlhejhq8vYQ
poXpvBE6vHXCtDA9HDV5ewjTwnTeCB3eOmFamB6Omrw9hGlhOm+EDm+dMC1MD0dN3h7CtDCd
N0KHt06YFqaHoyZvD2FamM4bocNbJ0wL08NRk7eHMC1M543Q4a0TpoXp4ajJ20OYFqbzRujw
1gnTwvRw1OTtIUwL03kjdHjrhGlhejhq8vYQpoXpvBE6vHXCtDA9HDV5ewjTwnTeCB3eOmFa
mB6Omrw9hGlhOm+EDm+dMC1MD0dN3h7CtDCdN0KHt06YFqaHoyZvD2FamM4bocNbJ0wL08NR
k7eHMC1M543Q4a0TpoXp4ajJ20OYFqbzRujw1gnTwvRw1OTtIUwL03kjdHjrhGlhejhq8vYQ
poXpvBE6vHXCtDA9HDV5ewjTwnTeCB3eOmFamB6Omrw9hGlhOm+EDm+dMC1MD0dN3h7CtDCd
N0KHt06YFqaHoyZvD2FamM4bocNbJ0wL08NRk7eHMC1M543Q4a0TpoXp4ajJ20OYFqbzRujw
1gnTwvRw1OTtIUwL03kjdHjrhGlhejhq8vYQpoXpvBE6vHXCtDA9HDV5ewjTwnTeCB3eOmFa
mB6Omrw9hGlhOm+EDm+dMC1MD0dN3h7CtDCdN0KHt06YFqaHoyZvD2FamM4bocNbJ0wL08NR
k7eHMC1M543Q4a0TpoXp4ajJ20OYFqbzRujw1gnTwvRw1OTtIUwL03kjdHjrhGlhejhq8vYQ
poXpvBE6vHXCtDA9HDV5ewjTwnTeCB3eOmFamB6Omrw9hGlhOm+EDm+dMC1MD0dN3h7CtDCd
N0KHt06YFqaHoyZvD2FamM4bocNbJ0wL08NRk7eHMC1M543Q4a0TpoXp4ajJ20OYFqbzRujw
1gnTwvRw1OTtIUwL03kjdHjrhGlhejhq8vYQpoXpvBE6vHXCtDA9HDV5ewjTwnTeCB3eOmFa
mB6Omrw9hGlhOm+EDm+dMC1MD0dN3h7CtDCdN0KHt06YFqaHoyZvD2FamM4bocNbJ0wL08NR
k7eHMC1M543Q4a0TpoXp4ajJ20OYFqbzRuhiWnfPPW//0m6j8268/DnXXn71nivcyj1XlBDX
8K+htL120uU3X37F+muvuOGay6++7PLrV556/U9desMNMKDUOSevPOfcs1c+7tyVT7pg7vzz
oZ5xCsxlWboqQDn/+vWXr7zu+stvuPzaZ19+yY2X33AjjKdceuP6a5CaMm5iK3/523yJjaJX
svf5uauvvuLyZ11/6fpnX3nDFVd//8qrL73musv3XOENnW+h8E9Z+JrJj/v39Vn+HEsGtpwq
f6KZR6eCsIYG4iEthOXiZkxsDIsaljUsbFjasLhheUMHQw/Lqm2smx6WHpYelh6WHpYelh6W
Ho4ejh4uNocejh6OHo4ejh6OHo4eFT0qelT0qOIe0KOiR0WPih4VPeKZqulR06OmR02Pmh41
PWp61PSo6VFzGxEqDT0aejT0aOjR0KOhR0OPhh4NPTy34enh6eHp4ekRz42nh6eHp4enRwRh
S4+WHi09Wnq03EZLj5YeLT1aegRuI9Aj0CPQI9Aj0CPQI9Aj0COe6R6G9DElnUxJL1PSzZT0
MyUdTUlPU9LVlNyaSac/+pro2yGgg0CHgQ4EHQo6GEQcmAgEE5FgbPSNWDARDCaiwUQ4mIgH
EwFhIiJMhISJmDARFMbFNkdYmIgLE4FhIjJMhIaJ2DARHCaiw0R4mIgPU8X9jQgxESImYsRE
kJiIEhNhYiJOTASKiUgxESomYsVEsJiIFhPhYiJeTHdviYgxETImYsZE0JiIGhNhYyJuTASO
icgxETomYsdE8JiIHhPhYyJ+TASQiQgyEUImYijdySKKTISRiTgyEUgmIslEKJmIJRPBZCKa
TISTiXgyEVAmIspESJmIKRNBZSKqTISVibiy8cZmS2LDRlzZiCsbcWUjrmzElY24shFXNuLK
RlzZeF+xEVc24spGXNmIKxtxZSOubMSV7e4v3Q0m3WGIK9vdY7qbTHeX6W4z3X2mu9FEXNmI
KxtxZSOubMSVjbiyEVc24spGXNmIKxtxZSOubMSVjbiyEVc24spGXNmIKxtxZSOubMSVjbiy
EVc24spGXNmIKxtxZSOubMSVjbiyEVc24spGXNmIKxtxZSOubMSVjbiyEVc24spGXNmIKxtx
ZSOubMSVjbiyEVc24spGXNmIKxtxZePNyUZc2YgrG3FlI65sxJWNuLIRVzbiykZc2YgrG3Fl
I65sxJWNuLIRVzbiykZc2YgrG3HlIq5cxJWLuHIRVy7iykVcuYgrF3HlIq5cxJWLuHIRVy7i
ykVcuYgrF3HlIq5cxJWLuHIRVy7iykVcuXi/chFXLuLKRVy5iCsXceUirlzHYB2FdRyWSIz3
K9fRWMdjHZF1TNZRWcSVi7hyEVcu4spFXLmIKxdx5SKuXMSVi7jq+h8u4spFXLmIKxdx5SKu
XMSVi7hyEVcu4spFXJFI4rXLdkJ4d4zMhjRyDtLIAbFgZIB4E4/34XgrjcwRiSPyRqQNeqgH
gCPIY6UeAA6CegDbvAdgi9SbQgqqb0qwvus6B/zJV00T0H1oul4eTE3TGgNyq3zXHYLJh4Ce
Vo1+UNdPgik0PuBuHELvh5tm5ZsKLFd3XTNb4L4VQu0a9C26HiNMvnSt943Dvai7bRRVCT7y
PpSh63raonJt8DVcm7Lrh8LkA1pRoxVl1720RQ0y9hb8Uoau5wQT8iBP9DK6npMtGrArulE1
mxFvTjC16E/gVl6WHacbW/jKYa/LFnvUdf5s0ZbBg9Xh23R9K5jaskJnFXWnbpItQl3jaOJu
jOrjfc4VJfbXe48ea0dZxhVAeQ2O9uj3pH5pgY5NWZd18G3aRVeAsQL6nuh6pP6mw6EJYMXK
oBVdN8wVNTqOOBClB43Ge6zDPgbnnfcldiweU4cdaqvQwLHs+lRoROtdaMF7Zai6rnzX4+VF
eJ8GT1/WDcgQW+zOLFqB9uOEtSF0HRBUVvq6Bft7nIyu/4ljiJ2pcIC8SZ1vnLQGp6cED9Wh
66HbwrSABI5ahb5G3KwpgD6c6xK7X3XRhSkagAvBB+BWdqfWABM46NjrGkcn7qQp0Gmsa+w4
aL/rzpZFCL7EwW983R0JhL4AB85RSQB1cUwBqNdt49FPTl3ZsqjQeULsAdC3XVRQ4tLA5tHj
xeHuuvNlgbOB7mEbTNNFSaHAgce2caobgDqGYNggGo62BjBy3MVQNHXZtBX6B2XbRnIPOI2+
QbcQxwaleSBC4bDLOPbeg4hjVy7gwisrnDSiHLiOpRBn+NDi8qyrOl5UoQBmgRqcC/wSj01b
BBxfxDrO4djETmBboAEtOnWEcx17MC1QwlOGktxFHpwWR75En7V0Hoc29spaXFS48Gu0BGcz
donaAkcGfUtU1iJc4W7DhMsfpwLdDVwfvNJaXP5oIoAfKpyNrno0APcRXAvAYOyStDiLAbeD
CFQAODoCVKgj4IyVPplwbZa4c1V1i1sTj0SLCw39lha3KVwusdPoC7QHPTJcUoB97GvCxMsJ
JzvgHhO7yR7XMW4HOBEAYnfngAn7g5ucBwyAClQPU4mTHY9VQPlowu0N1wb6iziRsYvI3o8k
32OAW7vIT+Qn8hP5jYP8YuQr8hP5TQTpi/wU+SG4E/mJ/CaT/BiHIcx7kMiPgeWiIj9GkYr8
pjSCFfmJ/ER+GvbUsKeGPSciWhvnMLLIT+Qn8hP5jYn8JmfYs3tMp0d+UxrULYQjxX3iPnGf
uG/ZcZ/mu+Q7D2UhxDWOMiI/kZ/IT+Qn8rv/UU898pviyFDkJ/IT+S1r8usWGYxnpcPSj3ou
bL5Lx2Fa6aBob37EKPIT+Yn8ljX5davixkN+8ZUyGa50WPRkz85Ry/ymci6MyE/kJ/IT+Y1p
2FPkpzXukxNdivxEfiI/kZ/I7/6f+Sny0zM/vd1MbzeLHKm3m8XXdOrtZpP1djMNe85/1iW9
i04V+SnyU+SnyG9iI79tPOFFsz0V+SnyU+SnyE/vtdZ7rfVe68l5pvdgEa4iP0V+ivwU+U1s
5Nd95+HBXu2ppQ4PRgTL8XeRn8hP5Cfym3Ly0zO/5UhuD7bPIj+Rn8hP5Cfy02zPqVzL90AE
KPIT+Yn8RH5jIr+lf8OLhj2n5xncAxHVtvhN5CfyE/kta/LjkKA+5K4PuS8/EhX5ifxEfsua
/Bb9erMqsmbta1PVvqwaa83Sv+FlGy91uJ9F7ow18Xnb0lrnm9ra0Nbd55F8U9WN3vAyOSQq
8hP5ifxEfmMa9hT5ifxEfqHxwZVlCCX7TqBYZ3yFrpGtmtqxt0ZTZUKoXWNaX7LvRJMvXes9
+k/3lqpKiyEJH8pQuq5Q5drga7g2ZcneJ/wqH6wPtXG2NMlUW9d4a1l3k9pQI29rlKmatL3G
1iI/HEFXtN6F1hlbhqrkk5vuMMZjed8fV+gNL3rDS1U6307WG17GudRBkd+2eP72UNQJ4rBE
RkxNi0Wspq2dT9xga181TTBei9y1yD1ypMhP5JcV+S39sCe3qGHPh4Ksxr1NkZ8iP0V+GvYc
07CnZntq2FPDnhr2ZDAd6hpxtKsqDO7GsURXlBjm9d4b29oQ42tXGGtqC6stUYxRuCssxh/r
sg6+TSO7rnClDwazCpw1VXKsymBDVRnThBCHkl1RmwZxe116G8oY0buiscF5h5CttSaV8lVb
hQaOJYY5uy1q2NPGY18WTdnUbeMNXmQV4ohvWVS2wRnBcDuOmyK/rCI/no620Btexh0VLYf6
FPkp8lPkp8hvTJHf0k94WRj5sV/ji/lfcmefDxZ2JdHRCVrpMDkB27h4Wdwn7hP3ifuWHfe1
Ir9l90KXLUlT5CfyE/mJ/ER+ervZsiNDkZ/IT+Qn8hP5ifxEflrpgGkhDk8CytK6tAbEV67R
SofIkVrpoPkuDzDfRZM9Ndlzcp4dKvJT5KfIT5HfmCK/pSe/pV/mx96Plvlt+fxsEvMiP5Gf
yE/kNybym5zJnprwMjkR2rYiVpGfyE/kJ/KbcvIb59vN9IKXbUVGS12vyE/kJ/IT+Yn8NOFF
E1404UUTXuK7aO57m/V9mt5rrRe82OoBJrxo2FMTXiZnOFWRnyI/RX6K/MYU+S39hJfFvuBF
z/wmh6S21XCoyE/kJ/IT+Y2J/JY+8lvYbM8ff7vZ4slPsz23FRktdb0iP5GfyE/kN7Hkt7DI
b5wTXkR+S01S22p7Ij+Rn8hP5Cfy04QXTXjRhBdNeNGEF33RCJ8J8lXwVWm9cb72HDhsC3zT
eiInvIwz8tNSh20ViS11vYr8FPkp8lPkN6bITxNeNNtzcibSiPxEfiI/kd+YyG/pJ7ws7Jnf
OCe8KPJb6ghtW21P5CfyE/mJ/Kac/MY57KkJL9uKjJa6XpGfyE/kJ/IT+WnCiya8aMKLJrxo
wosmvEzXhJdxDnsq8lvqCG1bbU+RnyI/RX6K/BT5KfJT5KfIT5GfIj9FfouL/DTbU7M9Ndsz
ND64sgyh5IgD4ktnfOWbylZN7ThfiqbKhFC7xrS+DMnkS9d63zh3bymsNGqC96EMpesKVa4N
voZrU5bxpcu2qHywPtTG2dIkU21d461l3U1qQ428rVGmatL2Glsr8lPkp8hPkZ8iP0V+ivwU
+SnyU+S3uMgv16UOmu25rZ6bTXK9euanyE+RnyK/KY/8xjnhRev8Jpnw5rdd5CfyE/mJ/Kac
/MYZ+Yn85hPIJOsiP5GfyE/kNyby04QXTXjRhBdNeOGUnlDXbe1cVWFaT3yQ5ooSE3y898a2
NsRZN64w1tQWVluiGOf0uMIaZMo6+DbN6XGFK30wVWOdNVVyrMpgQ1UZ04QQJxG5ojaNw8yf
0ttQsruLuhobnHfel3iYmUr5qq1CA8fSdlONXNF6F1qHzYaq1DM/PfNb3DO/XMlvnJGf1vlN
crQ3v+2K/BT5KfJT5DemyC/XCS/jfOYn8ptPIJOsi/xEfiI/kd/Ekh/HMtqibEOJeepV3Rrr
GObBhOVSvm0rj4GSIPKbZJLaVm0X+Yn8RH4ivzGRX67DnuMkP0142VZktNT1ivxEfiI/kd+Y
yG85DHuK/JaapLbV9kR+Ij+Rn8hvyslvnBNeRH7bioyWul6Rn8hP5CfyE/np9WZ6vZleb6bX
m2mpg5Y6LG6pg4Y9tc5P6/y0zk/r/IzHW8Z9XG1oC7yJ3FdlZbwx3WJGvI28wXvHS8f1jC69
s9y0eNc5VkdW1rv4gnJTBMOXmJdY5liVvLcaUzR4a7op6wpLErt3lpuicqZtsbqxxipIjkuh
lC3busYCR1fWbayrLELwJRZZNr7uVjyWhcdbz7EWs+Sb0eMay7JoSlgabzzakvwq22DlJV6o
jvWRnOluysJy8yY4LKusY2ehLLDq0qIZwTQmvoM9FFhgiW1jSWeDt7VzcWbABtFwtDW4qtvF
UDR12bSVs03Zto67GLBc0zcWq0PrEqXZiFA47HJZN947tI6NCIX1ZYXFmXx9O17YHk0Guxxa
69q6quMSzlDgNe5YHYpzgV/isWmLgONrKsyHxLFpusmRaEBrcaQb39SW1beFr3jKUJK7yIPT
4siXtoKjx6ENPGdtUeNgVjVagrNpciU/DXsu9ZDiJGxPw54a9tSwp8hPw54a9tSwp4Y9Neyp
YU9FfouL/LTUQcOeGvbUsKeGPTXsqWFPDFDHwVGMd1cYgXYYIm3SeCnf+lfivX6hwiB0N6qK
cVeHkesGQ7K+7sZe8b49fN4zvocP7+eLdWEsHXUEDFSXPpmGL3JnszzGpTFMjiHugE+GNmka
Z1uHGsPPGH7vPgTqERVb7EfwGPzGWHh0bEsMcccR4oDy0YSvldb4ECnqK1vDXsAkjPwt5zZq
1FOjnhr11KjnlI96ao37cia5re27yE/kJ/IT+S078lPgt+wDU3GfuE/cJ+6bcu7TXM+tBT/L
2S7yE/mJ/ER+Ij898lt2kaDIT+Qn8hP5TSz5cfbJg3/TQZHfco7wtrbvIj+Rn8hP5Dcm8tNC
B032nJxJriI/kZ/IT+Qn8tOwp4Y9tcRdS9y1xF1L3Kdrifs4hz251BAr/7TMb+LJUpGfIj9F
for8xhT56c2eGvbUsKfe76L3u+j9Lsvu/S65PvMbZ+SnF7xsbQLJpNkV+SnyU+SnyG/KIz+9
4GXSiGkp2ivyE/mJ/ER+Ij9NeJn4Z3hDCVPkJ/IT+Yn8ppz8NOw5lBiWQ3mRn8hP5CfyE/kp
8lPkp6UOWuqgpQ5a6jBdSx0W/cyvCxn1RaOpJEZFfor8FPkp8pvYyG9hrzdbNPl1jiI/kR9n
79umaY2xrq18xW4RTfjMo8EnKE0VqiqZtNRBSx201GHZLXXIdZ2fyG85PMMbuo+K/BT5KfJT
5DexkV/3affh33Fv9T2/qYzmhhCgyE/kJ/IT+Yn8NOFl2ZGhyE/kJ/Jb1uTHIcF2TOS39G94
WdgzPy11GBIRLZeyIj+Rn8hvWZMfiWFyyW9hw56LJr/OURNepjIqFPmJ/ER+Ir+Jjfy2Mflp
tie6RtMaCYr8RH4iP5HfsiM/zXeZWk5bKFeL+8R94j5x35i4L9eVDose9VTgp8CvaUrCgFSp
ZX48DG0ZvK1InI1PR6Zty8pYWzXBtLwJoFSo67Z2rqpq18S3priidI3x3hvb2sDOp3GFsaa2
sNoSxTqTNciUdfBtWcaVk65wpQ+maqyzWE7ZlarKYLGy0qAVgc/9UVdtGudDXXobSl7xMDUW
q82c9yXeXJNK+aqtQgPH0paprta70DpsNlSlXvCiF7xMygteFjbfpeOw0GI1coVLCrBf4EoH
PfLDTWShkdSklVPkp8gvUqTIz8aOR1mgn1eL/CaF/PTIb3rJaVuTqchP5Cfy07Cnhj21zG9q
I7ytkajIT+Qn8hP5jYn8ln6ZnyI/RX5bI7cHs4v8RH4iP5HfxJKfnvmJ/B6M5Lb2u8hP5Cfy
E/mNifw029M5zEorW8MYeGs3XdnzODYiP5GfyE/kNybym5xhTy3zW/bcLO4T94n7xH3LjvsW
uNKhWyKhl5tNJVGK/ER+Ij+Rn8hPkz2nkuAeaIRZ5CfyE/mJ/MZEfkv/yE/zXfJ4fPZAJJPr
byI/kZ/IT+Q3seS3sJUOi37Bi4Y9p3jejshP5CfyE/lNOfnp1Z65Rl8PZbtEfiI/kd+yJj8G
N+P6mt/SD3sq8tOw52IJVOQn8hP5LWvyY1Qk8ms04UUTXkqDzxD4+KZ/fMGh9lWDjxR4fdSh
afEeeFdW7Cejx6CPOoTuMx+uwJcs8CUJ14YAuPDo4MsVvm4t1vmWpvLx0xK28PhCRYWvXnhj
ui9X2AJfqLBt6fjxCue6w2paEwI+hVFZ7+LHLEwB9NUhlPimRVXGb2WYomnwfYuyrvD9iSae
D1NUDl/SwKcsanzyIn65whR4cX9d42sWrqzbWFdZhOBLfFGj8XX3eYuy8KHBW6xFfhM77Lmw
CS+LHvbsHLXUYSqJUZGfIj9FfiK/iSW/hQ17Lpr8NOEFvdLFDivm7ifyE/mJ/ER+Ij8Ne04t
yW2NhEV+Ij+Rn8hvysmvC+AW8S1bRX6K/PTMT8/8Ikfie/B140yNT8frmV9lgmuc7550lkUZ
rMWjx2AaU/IZZigCfsTzotY2rY/P0QMeMuJhJZ5PBld1jzVD0dRl01bO4nXIreNjzVDUeMxu
qxrPQ1GaDyxD4fCYE8fee4cv7XKwLxTWl1VoncejU2s5shcKg8ecobWurau65JP7UOA5dWMd
nr/il/g8tC0CnqmaqnQOz0MbOk77hBcNe24t+lnOdkV+ivwU+Snym9jIbxtPeFHkh67RtBKk
yE/kJ/IT+Y2J/HL9qIOGPaeVwH6S/RL5ifxEfiK/MZHf0i9yX/rIj0POHmudMMbtm9ra0Nbd
55F8U+GRgD7nNzGRoshP5CfyE/mJ/BY821Pk95NEWzn5ivxEfiI/kd/Ekt/Sr/MT+eVEYD9J
W0R+Ir9lSX5xKqTRK14mfrrn0o97cosa9/xJWCcXX7Gf2G9Zsh9vYSK/ca91yHXGi9Y65EI4
ObVD5CfyE/lp3FPjngt+6KfILycC+0naIvIT+Yn8RH5TTn5a6/CTkMS0+or8RH4iP5HfxJKf
nvlN7yr0bU26Ij+Rn8hP5Dex5Lew6Z6K/LY1kUxi/SI/kZ/IT+Q3JvJb+gkvC4v8RH6TSE7b
us0iP5GfyE/kNybyW/pXvCjy07DnYklS5CfyE/kta/JjVDSuzzosfeS3WPLrXkkWnDVV401o
FjzZU4vcF8s1ufmJ+8R94r5lzX3L4ZNGix717NYH4rNUjQ/B28b6VisdciOxxbZH5CfyE/mJ
/KZ81FNr3BdLENPsJ/IT+Yn8RH5jIr9cRz1/nPwWPeqpwG9a+FDcJ+4T94n7lh33tSK/ifny
0LYiW5GfyE/kJ/KbcvJb9CO/zlGP/KaSKEV+Ij+Rn8hvTOS3HBY6aLLntorElrpekZ/IT+Qn
8pty8vvxR36LH/YU+S01SW2r7Yn8RH4iP5HfmMhvcua7iPy0NF7kJ/IT+Yn8xkR+uQ57jjPy
02zPbRWJLXW9Ij+Rn8hP5CfyW/ALXkR+S01S22p7Ij+Rn8hP5Dex5EcqaouyDWVp2qpujXUM
82ByrvZtW3lThaDZntuKQCa5XpGfyE/kJ/KbWPJb2Js9xznsqQkvk0x489su8hP5ifxEfiI/
DXtO5Vq++WS3pS7yE/mJ/ER+U05+4xz2VOS3JYlMal7kJ/IT+Yn8ppz8xjnsqQkvk0p2W7Zb
5CfyE/kta/JjVLT8vua3+HV+Ir8tSWRS8yI/kZ/Ib1mTXzc5sq1ca30dGt/UtptF4qvgq9J6
43ztO4psmtJWVel8W9fBRdasfW2q2pdVY61Z+kXumu2pxeqLJV+Rn8hP5LesyW+ckd/kLHJf
9Ecd9MhvsVyTm5+4T9wn7lvW3DfOwC9X7hvnfBeNeuZGYottj8hP5CfyE/ktu/kuCvyW3cKG
LTlS3CfuE/eJ+5Yd92m6i54UivxEfiI/kd+YyG/pp7t0M3Me7OVmWuiwZdSjPG57trBERkxN
i7lcpq2d55hANPmqaYLxsHPUnKamaQ1en4dX5lW9ow/BOIspX6GqUinMGQuuLEPo/ZzxlW8q
WzW146A5qnKVCaF2jWl9mTbofOla7xu8la8vhdlmTfA+lKHk5DL4YVZawKy0UDdlmbZX+WB9
qNGK0iRTbV3jrWXdTWp7jbytUaZq0vYaW4v8cFBd0XoXWmdsGaqSt7DuMMZjed8fV3hf1o0z
ddOfWVdUxhqcsDYEW0dPV5S+bm1rPE6GTyDBCcPEwcp4Y1w6HZwd2JauLjFtMJ1a0wISoa4r
613crCmAPpzr0pVw5xMlY4oG4DJlDbiV3ak1wIRp29Lb2poqwssUtsSERO+8K+s21lUWIfjS
A16YnhgLlYUHOOpW5Dcm8sv1kZ/IT2T345FuZLiOU8BeIj9bNK01zllTlt0LcnGEfOVA+ehd
OtBmd7DaMnhbkTgxMzyZWtzbLdg94D7cmXAbR1fCVRUovucFkD3uv8a2NkQGdgXIo7aw2hLF
6OgKCxYiKfg28bsrcPcPBnyBplXJsSqDRX/DoBUh3sxdUYOH0AsADYQy0o4rGhvAAGAt7Fgq
5au2Cg0cS5Bdt0WRn43HvizQz6vbxhsPIk6kWdkGZwSdLhw3hhqmRJcR3GuCw+HuKL8scDYs
ODiYxsR+Wihw4EG8ONUNenQ80AFsC9YGQIKrOn4PRVOXDdYZ2KZsW0fkBJxG31igpi5Rmo0I
hQPfo+PhvUPr2IhQWCwvQI+FXTx06qLJgO9Di75pXdXx1IYCmAVq0BHBL7Fj0BYBnQuD9QoO
HYOGjuNa5Zcr+fHU+iK06B1XuKQAew17/jgZLDeCFPkp8ot0K/IT+f3kq/xyJT9FfsuN2Bay
vyI/kZ/IT8OeUz7sqchvIWSw3MqI/ER+Ij+R35STnyK/5UZsC9lfkZ/IT+Qn8hP56YNGy27d
n8hP5CfyE/lNLPlxCtc2/I57FzJi0hImGGOKW2MxDSpOnmlLzG6Kb0ENbc25TL7AZHbMhHaY
lVZipjNMC4k+VOahO04iP5GfyE/kNyby4y2/LTAP1jZ43TVmV4IzOhNWOmHOscN6qCa9D5uT
oEtMcw4VFp7woVyL6atYiMSZz1huU3cr+DAdGSuf4rRkTFeOpbB+BnUErG4qOyp6cPIb57An
G+ELkd9DR1rj6jCI/ER+Ij+R35jIT7M9FflNDimK/ER+Ij+R35STn2Z7jitamqZ6RH4iP5Gf
yG/KyW+cw5565jctBCjyE/mJ/ER+Ij/N9lx2E3REfiI/kZ/Ib8rJ78eHPbsJmoEvC8Sr7AJe
H9ykkA6TN2u8Zg7vmO1eCozJLZrsOS3B3vz9EPeJ+8R94r4p5z6Nes6/6Uvv5uSI/ER+Ij+R
35jIb+lXOnSLH/RFIxHa8EmmIj+Rn8hP5Cfy07CnHvnpc376olH8+FL8mM8Wf/Q5P33RyFb4
FJLHlxLTUnWsZTdVjW8r4eOMRsv8tMxveAT2UEWtivwU+SnyU+Q35ZHfGOe76P0uDxVXjXu7
4j5xn7hP3Dcm7lv6wG9hb/Yc53wXkd+4Seihqk/kJ/JbluTXfb++xHfVG3y2Xew3seynCS+T
M8z4ULHc1rYr9hP7LUv2Y8hgRH5l3TAsaieW/JY+9EurAfVRh4mfICPyE/mJ/BT5TSz5LSzy
+/Fnfq0WuU88eW0toluoXeQn8hP5ifymnPzG+dBPkd9CySX3ciI/kZ/IT+Qn8tM6v2UXCYr8
RH4iP5GfyE/kJ/LTInctctci9xbvOsZHwkNc5F8WeK+xNbZybaVF7strkXs3XqoXW08lMSry
U+SnyE+R38RGfgub7akJL7k/f3so2ifyE/mJ/ER+E0t+C5vtqQkvDwW55L5NkZ/IT+Qn8hsT
+eX6VQdFfrkT0UPRPpGfyE/kJ/IbE/kt/fvNFhb5ifweCnLJfZsiP5GfyE/kNybyW/rIb2HP
/DTsmTsRPRTtE/mJ/ER+Ir+JJb+FRX4iv4eCXHLfpshP5CfyE/mJ/LTObyqXMzwQAYv8RH4i
P5HfmMgv12d+44z8GGv6otWLrSeeLEV+Ij+Rn8hP5KfIb+LJ7IGivPv7TeQn8hP5ifzGRH65
TnhZ9GzPLmTUG16mkhhFfiI/kZ/Ib2LJTxNe9DHb+4vqFmIT+Yn8RH4ivzGR33J45qdPGi2E
WCahjMhP5CfyE/mNifyWfthTkZ8iv8USrchP5CfyE/lNLPktbJH7op/5dY565qdnfitIlU3T
GmPxdRdf8WkwTT4E42xtqlDFb8DAFBofXFmGUBI+KOSMr3xT2aqpHQFLU2VCqF1jWl+GZPKl
a71vnLu3VFXaJngfylC6rhA+LRN8DdemLNP2Kh/QihqtKE0y1dY13lrW3aQ21MjbGmWqJm2v
sbXIT+Qn8ptY8lPkp8hPkZ/Ib4VxRW0ah15A6W0oY9/EFY0NzjvvS3yoMHY7XOHxXbrQVMaU
tut2uKL1LrTOIF+VHLzq+hCxI3HfH3j6sm6cqZu+W+OKylhsFB2SYOvo6YrS161tjUdPxKce
Enorvior441xqS9SNeiblK4u6+BSv8bgG3ro1dSV9S5u1hTBsKNTuhLufKRkTNGgZ2XKGn2t
suvXmKJypm2x17U1VdxJU9iyrWvsuCvrNtZVFiH40qNv5evuSJSFR8+obkV+y4782Pv1RXDA
C77dGNC/bogbLOBr61C3hHPoes0w4XuO6OB7fNURH3nsSmmZ38QHg4zb+vitNm3T6Fu2+pat
uE/fsl3RoofE7or1xvnas7/SotdRLq9v2XK3RX44CIsNrnL2E/lp1FOjngr8ll3g1y4s8mNg
IPIT+eEIkCr1yI+HoS0xCFKROJvYKaapxaCexTPNgAG47mBh/K6tnasqPNjsBwTxiBMDb8a2
NsTnjq7AqGFtYbUlitHRFRbDjxwN9G16qukKDPsFjNBYjtMkx6oMFk9ZDVoR0nimRj016hla
PJGvqzoOaIcCD7iBGoxA1z7EEeG2CBhVNlXpHEaEG97f2zGR39KvdCDu26JsQ4kxq6puMRuh
2yHsXe1bzEzA5RK6AC60mBNQ4ZLCYL/IbzqjuSGRpiI/RX6K/BT5TSz5LXa+y8ICv/sZ9eQG
EQvqkd/Ej4SK+8R94j5x37LjvgUGfvdDfprvMiS4yrmsyE/kJ/IT+U05+S161FPkhzg3ZwL7
Sdom8hP5ifxEfiI/rXSYWpLbGkGK/ER+Ij+R35jIj5O62gLLL21TY3Fma7A6rjPhDRdYcOnw
HowmcElnizdcYEoOJnqFCmsuGWG1eFkGXkDBuV9YaVp3D/Ow7BRvvIjLUbFMNZbC0lHUEfBW
i9Ink+a7bO0GL/vWI1eRn8hP5CfyGxP5Lf1kz8XOd9Ezv62TwnIhTJGfyE/kJ/IbE/nlGvl1
q/UWsdLhfp75abbntJCjyE/kJ/IT+Y2J/HKN/DThZVoIa5z7IfIT+Yn8RH5TTn7jjPy01GGc
BPRQ1iXyE/mJ/ER+YyK/5TDsKfJ7KAlrnNsW+Yn8RH4ivyknPw17jpM0pqUukZ/IT+Qn8pty
8hvnsKcmvIj89Clbvdc60qa+5hdfWV4WeMu4xUcFg2lM/OpywMfi8FnDCq8wb/B95v/P3rnA
U5Xu/39L6aYmo0JyGWa6qT3rutda5TpDmjNkHGQqqsMMpSkhFHKZ5oJcaqYmVHQ0Q7ZiTCmX
ETO59CuR0EUuRSVEVC4J/Z+1aS6dzjkdfzMTfXevtr2f/axnrfXstdf7+Xy/3+f58hPeOJQ+
EKUhRAufcyTVn7CQE4poTMRSJCHCWJRFTlKLxhkRgVZDpzFUm09FyAlJlMAQrULNMCTNivgb
MIemxWEUSsHIJ2xGKZolRThKYAjrWkuWuv7tutYAv5ECrKE8D1B+oPxA+YHyG7bK7w9O6vCc
qQ7g8xtKAP2VbQH8AH4AP4DfEMHvz5/q8GLwG0rlB/D7K4E1lPsG+AH8AH4Av2ELP1jhBVZq
GSwQAX4AP4AfwA/gBwtbw8LWKB0yTUqc8xIuMigLNIe87yKMt37zRZDIHRK54zRKHd9/RZBC
CHiBgBcahd6ICAL/882eL6b8YKrDYNXRSN4OlB8oP1B+oPxA+YHyA+UHyo8lcJIkUFw5QfJ+
cjQ8QNlYkN5FaVNINL7tL2JRphWY6iDBJig/UH6g/CYwQkZE0SKSREmbMBbnr4mRrJpGwrmB
8gPlB8oPlN8QKT/+lj+i8vnBVIcRDHGAH8AP4AfwGyL4vaw+P5jqMBKU2lCfA8AP4AfwA/gB
/MDn98qZaQF+AD+AH8BvhMMPoj2HWjWNhPYAfgA/gB/Ab4TDD8yeIwFWQ30OAD+AH8AP4Afw
A7MnmD1hqgNMdZCE7vO5BPBnnkghw6DMAiRMchcSNMVROEeKUOIGmOrw1011gLU9YUrFYBUh
KD9QfqD8QPkNkfKDqQ4wz2/4wBjgB/AD+AH8hgh+f/5UhxdTfhDwMlh1NJK3A/gB/AB+AL9h
C78/f21Pfo+MkMVQ5mJGRBMEx9J8nmJY4WXY+QwBfgA/gB/Ab4TDbyijPQF+I0UNAvwAfgA/
gB/AD6I9h51y+/+FMMAP4AfwA/gNEfwg4AUCXiDghRMxKAcC9jTrGyEkcYZCy54TlIgmeSc1
oi6JQsU5mhThLIPxVnO+iMFIlmHQ2ui/1KIwQsQxDIdxGNlfiSJZjqHRpiIMk8TiE0KK4QiG
o3GSwPrD8wkhTZAihiD4tkUDqRho9J6gUR1KNLA/EUED/AB+rzT8+B8HO0Tw+/MDXl7M5zeU
Zk/+7gU+v/9f1fUybA/KD+AH8Hul4ceDAeCHBtiiAayhABaaRQNs9JAMmxHpKAIN5lESMxHB
sODzexnANRTHAPAD+AH8AH6g/F4YfqD8hgI8L0MbAD+AH8AP4DfC4TeU8/xA+b0M4BqKYwD4
AfwAfgC/YQs/XoexQozlMLQwI0WzOEH223ExFDfAsCzF4BQyX0r8dByLggIoFsMwAm3QX0QS
KPM6g3P/xuzZ7ywEs+eIjAQF+AH8AH4Av2ELvxcLeBk0/Po3BPgB/Ph4TEIkYnE0vEJDKoof
FvFFyBeMhlQ0GmJRA9GXBER78j3D0TRLkyRFoZhWyerHpBBD0a0Mw+AES3CSkFNSiBM4TaBS
AkPV+C4lhQSO3mA0x6BhqqRLSSGJMRwapBL8UHVgQwrjCNTlOC5CX0D/hjSOVlrmaIwhOEzy
9ZBCEcGRDIlWpEYrdg/UYiiW4kRoQzQEHmiLZUiOJdFuOQqTHOoza1oPHAUsbM3fbXEMFram
OT74mhXSDPrhP13Y+s+f6vAHK7/nwI/fI0R7DoXZ8a9uA5QfKD9QfqD8Rrjy67deDsLs+Rz4
gc/vr4bWUO0f4AfwA/gB/EY4/PoZNjTwA+U3VPD5q9sB+AH8AH4AvxEOv39Vfi8W7wLCD9l4
/2pG/VH7B/YB+4B9wL4hYt+f7/J7sXiXf2XfCwZ7Pgd+IPz+KBj92e0C/AB+AD+A3xDBD1Y3
g6U9h49SBPgB/AB+AD+A3wsv8ALxLn+2Qvuj9gfwA/gB/AB+Ixx+EO/yRwFkOLcL8AP4AfwA
fgC/F1Z+4PMbzsD77bED/AB+AD+A3wiH36ADXvo3/N0CLwC/3wJkOL8G+AH8AH4Av1cOfoOe
6QDsG868++2xA/uAfcA+YN8rxz6Y6TB8gjJ/C6yhfA3wA/gB/AB+AD9w+Y3Yuez/DpgAP4Af
wA/gB/AD+AH8UE4sGmUF4BeuR9kaaIYSiTicEYkwPliYL4KcDnw3sBjHEBQPThEz0DMsi1E4
QVCov1h+ri+qBTkdKIaPGEBdwaAEFRTqIAbH+xNXEEKUoIJgMZLPXUHy+QFQLZzFOQ71GkUw
pCSLBC5EVx/NcRhKaUFhkm7FhSIRSm+B0SiFCCaSdD4upEjU6SiTBY0yXvBOGRwXooxtNI2S
WZAYzUrawoQcx2AooYYIpSGQVMKEDCcSobwbGMVwhKQpTIgudZpFCd4YdCwD21GECGXZoFAi
ExT5wLcOOR3o5+Z0eBXmuMM0v3+npIZbObrhEAO3J5SRiEWQA/gROImyBqF8l5KkmPyNmyIR
8lH2SxKjnpIO4Nc/HCKFiPgoixLJchwaK/FkQFmbGJolWJzBcIAfwiVLiFhGMqDkEG0RtRGo
OZLq5zsnFNGYiKVIQoSxLMnjgxPSaLxJoDRYNIZq8wTmhCTiPUaLGIZEaOZvwBzKJIZRKAsV
g8YQhORXzAlxxHuORfnGaIqW5KrihOiaRWmw0HeBPpEMDFghhwYXOIWSvaKBgYj/+bMjXPnx
v1pGCMtag5/vt4AG+IHZU8IryOYHyo9AGhsZMmiCZyuLxny8WEeYJBlaYt5gkebGCApRk0Gi
+nnZ/F4F5QfRnr8FyHB+DfAD+AH8wOw5wpVf/2y93yo/mOnwyrn4nuU0sA/YB+wD9o1w9g3a
6tkPzd9NcQeX37MQGa7vAX4AP4AfwG/Ywo+3QbJC5I7HULACRbN4v6MeFZEkzbAshXybKIIK
XH6oB4YrpP6o4wb4AfwAfgC/IYIfZPODhEbDB7IAP4AfwA/gN0Tw+/PjXUD5DR/Y/FEKbrDt
AvwAfgA/gN8Ih9+gfX79G/7O5wfBnoOFzcu2HcAP4AfwA/iNcPgNpc8PAl5eNogN9ngAfgA/
gB/AD+D3wqubAfwGC5uXbTuAH8DvlYSfZPUTtEoZLG8GK7xQaC07TvTC9AO758tGscEeD9AP
6PdK0o+/hQH8XpXlzYbS7gnwGyxsXrbtAH4AP4Af2D2Hrd2zfyW2/zbRb9ARL8+Z5Q7we9kg
NtjjAfgB/AB+AL8RDj9QfoMFxEjeDuAH8AP4AfwAfuDze+WWgAH4AfwAfgA/gB/AD+AH+fxY
yOfHB4NI8rg+80QKGQZlgCNxWoTyy/KOFJS8D/L5SbIYYkKMIwiUU5fDRTjGJ+flhBxKBgT5
/PjVN1EWYwrlFSZpHCV75juHFZIUSjlIEyKOQqmF+WuJRQkKaRLlIxahXIMM3e/NI1DiTHTB
YegvxvYXoSSRqA0OpR/GmIGiP8znB7Pc0RczUk2foPxA+YHyA+UHyg+U34iF3L+DN8AP4Afw
A/iNcPgNOtoTlB8oP5TBmb8MeFSKRCyOEoegZCEUH0PFFzEchyNzBUoeQknsZKgIZYTmSAx7
ahwjhCSyezAiiqBENCmZY4WKKBxlGyFFOMv0zzlGRQxGsgyyc5C/1EK5pNEEVIZDZg/eXIL2
R5Esh3JOc7QIwwb2RyEbCMPR6CiwfnsdIaQJUsQQBN+2aODYafSeQIYVDJle+psSETTAD+AH
8Bsi+L2saR0Afv9O/bzK5aD8AH4AP4DfEMHvz0/r8GLz/P51qgNkcn/lrJzPch7YB+wD9gH7
hi37eCPSH5jMFua4o/59Fhoj5T3AD+AH8AP4DVv4vZjwG7TVE+AH8AOXn4hF0dQkchb2+wpZ
FIBNUDw4RczTIhZDQf/Ip8nhLG/9QeMKjqZZmuRDupH7kS8ihRhycTIMgxMswUn8jqQQJ3A+
upshMFStvxaBozcYzTHsgFeTFJIYw6EwcYIkkGu1vxaFYuuRlxXFiSOfa38RjYtI5PvEGILD
JB5ZUigiUMA9iaYooCkcA7UYiqU4EdqQDyDv35BlSI4l0W45FGXOFz0zyUHyFmY6oHkLfOdg
QoJGDm6cI1F30zDTgWbQL4Mg8JfV5fevVk8WzJ4jVtG9qDIF5QfKTwJlgB8hGXhgQhTaRbNo
nX+GxTkJ8jEhRYjQcATFWaFBA8CPwkiGpemB2Xo0gwLdnsJv+Lj8Bg8//gJghCyG5nQyIpog
OJbuBykK50NTYEk0QsVYyTDgRW/CUO+vMa0C/AB+AD8wew5bs+cf7PPjB0SIdGj0gyLaGTQG
QkMigB/qgZEAbIAfwA/gB/AbIvj9+WbPF4NfP8M4Fk2FopAnAVn7B6/8AH4jAXz8OQD8AH4A
P4DfsIXfiwW8gM9vpABrKM8D4AfwA/gB/IYIfq+Czw+U31AC6K9sC+AH8AP4AfyGCH5/vtkT
lN/I8L/9FRAE+AH8AH4Av2ELvz/Y5wfz/EZIcMvz4ArwA/gB/AB+QwQ/MHvCVIfho0QBfgA/
gB/Ab9jC78WU36ADXkD5gfKDFV5ghRcJIyGXLUxyf8UnuUPAy/NMiMOxDJQfKD9QfqD8QPk9
P5ctKD9QfqD8QPmB8oPlzdB9gKD+g/J7FaI9YXmz4ajynnfMoPxA+YHyA+U3bJXfi011gBVe
nnfzf9XLAH4AP4AfwG+Ew2/QAS+wtieYPcHsCWZPMHuC2fO/mT1f1qkOoPxedZX3vPMH5QfK
D5QfKL8RrvwAfs+7+b/qZQA/gB/AD+A3RPB7WQNeBg0/iPYEsyeYPcHsCWZPMHsOV7Mn+Pxe
dZX3vPMH5QfKD5QfKL8hUn7g84PlzWB5Mw5lPiYxjOMw3uKAEEviDMWIKIIS0SS/RgJfROEc
R5MinGUwbqCIwUiWYUQk+UstCiNEHMNwGIeR/ZUokuUYGm0qwjBqoIjhCIajUa5KDB8ooglS
xBAE37Zo4Bho9J6gUR1KNLA/EUED/AB+AL8RDj9Qfs9TPq96GSg/gB/AD+A3wuEHPr9XHXTP
O3+AH8AP4AfwGyL4vawBL6D8nnfzf9XLAH4AP4AfwG+I4Ac+P/D5gc8PfH68V5OjaZYmSYpC
nk1+UIyTQgz5OBmGwQmW4CSOR1KIEzhNoFICQ9X6axE4eoPRHMMOuDVJIYkxHE6JCJLAqYEN
KYwjOIrCcRHHSfyopJDGRSRyfmIMwWH8cBftUURwJEOidAwsgQ/UYiiW4kRoQ4zo97aSQpYh
OZZEu+UoTHKoEtfpM0+kELI6QFaH/7C258sKv6FUfrC250hRjKD8QPmB8gPlN2yVHz+cY4UY
y2EYzlI0ixMkTzpUhILmGJalGDRW5Abt8+vfkKUIFMDHMYSIYFiAH8CPYiiJtCCEKM6SQ3GW
NLrKqIFQSwKUHyg/nEGht8zARYLCcxkKo3AGx/vlLSFEMpZgMZJXuORAIC/OogBgpJcpgiEl
lxIu5HA+shdDwpfCeGGB40IRuhPhGI0uN6w/kBcXUiTOskjv0kgXS+QtLiQwlqaR5CUxmpW0
hQnR/QtDslvE0P0aGBMyKBQYqXOMQuHCEtWNCUUYKhExOIOOZWA7dO9DWhxFGSPFDMrvPyi/
l9XnN5Tw4y8vRshiBEEyIpogOJbmLTGMEAWz0yhOHZlnMBbne2KkQGKkngcoP1B+oPwAfiNc
+Q2l2RPgN1JgCPAD+AH8AH4Av+cns32O2RPgB/ADsydB8eAUMRJzGSFEZjcKJ9Asfg5Z4Hj7
HAS8gNmTQSZXFNskQis38LYxDtlZkb0WXSAcSfVbdjmhiMZELEUSyFrGkvyVw6G4JUZEoDAp
GkO1edsrJySRpRejRQxDIqMsb3vlkL8Bo1CUEr+UA1q8QVKEI0svxxIkS1O0JJaJE6IlHVCY
FDJBo08kJmFWyCGzMo6slyQyCYv4DdlhCz++J/67zw+U30gB1lCeByg/UH6g/ED5jXD4DaXP
DwJehhJAf2VbAD+AH8AP4AfwA7PnKxegA/AD+AH8AH5DBL/hE+3ZH6DJ8bNmUWQvh5YPFg04
81DwJo3MzyjquH9RYBTZ+duZDuDy+yvF2lDuG9gH7AP2AfuGiH0v6xz3obR6AvyGEkB/ZVsA
P4AfwA/gN2zhx6MI4l1gSuFgIArwA/gB/AB+wxZ+EOwJ4BsM+PhtAH4AP4AfwG+Eww/MnoMF
xEjeDuAH8AP4AfyGLfzA7AnKb7CABvgB/AB+AL9hC78/2OzZPzkeoj1H5CwIgB/AD+AH8Bu2
8Hsx5Qdmz8Gqo5G8HcAP4AfwA/gNEfyGzzQ/Fub5jUg197/AGuAH8AP4AfyGCH4v6zw/WNrz
f4HCq1IX4AfwA/gB/AB+L7zCCyztOVLgCPAD+AH8AH7DFn4v5vMD5TdSgDWU5wHwA/gB/AB+
AL8XVn48biGR+1BC6K9qC+AH8Hsl4SfJdYdjKL2eSESzQD+gH9DvlYuAAfoB/V5J+vEDeIDf
q5LMFuY6/FXy6mXeL8AP4AfwA+U3bJXfYGe5w1SHV07oPcthYB+wD9j3SrOPF0XsK8e+wc/z
g2jPZyEyXN8D/AB+AL9XGn58JORIh99QWj0BfsMVds8eN8AP4AfwA/iNcOU3lPCDaM9nITJc
3wP8AH4AP4DfCIcfzPMbroD6I48b4AfwA/gB/AB+MNPhlQuAAfgB/AB+rzT8IOBFxOCc6IXh
Bz6/P1KN/ZltA/wAfgC/Vxp+r2bAC8x0eOWE3rNcBfYB+4B9wL5XzuoJ7AP2EUKCH/hJGIiz
IhGGszTJ8FeGpIihRCIOZ1A5bxvhi0QiFscJkqUY6umGDMfhJEHjFEdRA7U4EcORGMZxT7cj
cYZiRBRBiWhSsrQGISQpnONoUoSzTP9SU6iIwUiWYUQk+UstCiOQQYLhMA4j+xunSJZjaLSp
CMMG9kcxHMFwNDoKDB8ooglSxBAE37Zo4Nhp9J6gUR1KNHCCIoIG9gH7gH1DxL6XNZsfhLs8
K3rg/QDhnpIO4IfoLmIJnCQJHMMIcoDuDEUi5GMswjk1wFEW4xiC4sEpYp4WsRiFE4juHM7y
Wc1QWxyNFo0kSYpCiOfvCzgpxBDsGYbBCZbgJAQmhTiB0wQqJTBUrb8WgaM3GM0x7ADfSSGJ
MRxOiQh0aNTAhhTGEWi8gaOj4CQDClJI4yI0dKExhuAwydGTQhHBkQzJMBg6sYFaDMVSnAht
iBH9ww5SyDIkx5JotxyFSQ5VMoZ45okUomZoEYnTaI/9wxpSiE4a7RQNSDiCfnqSDM0SLM6g
kQjztA/RyVCogxgc7z9JQohOhmAxkj9PcmBcg7NoPIR6jSIYUrJvXIiGXmigg6HTpzBJt+JC
ERpZ4RiNxlpY/7gGF1Ik6nR01jTqHclJ4kICY2kanThav4uVtIUJOY7BUOeLGLq/J2BhT/Rt
8l/QSJ/lx58jI+RYNDqm0E8KXfYwxX0SKD9QfggdNC9AB+6/AD+AH82iCAgGgXgAmhQhQsMR
ZHFAgwY+2gGtCErw7MU5dNkw/cjHhGgoQiAGc7gIlxgpOCEadSDwonGOCJkz+BELh5bRRtRG
oOZIqp/vnFBEYyKWIgkRxrIkz3cOjWEYEYGGTDSGavMHwQlJxHuEKoYh0dHxB8EJCQaj0IiF
t28gi4akCEe851hkmKEpWjKu4YRowIaGTGgggj6RDAxYIYcGFziFkeSrsrAnwA+U3r/CXmLb
RD8byV9QfqD8QPkhCz/AjxeDDMWLdYRJnu+8SYJFmhsjKERNBolqjh8tskIayWiKRhhGOh7/
8/O48zKfFSIhhyGHDUWzyCPTL2UR2mmGRd4ZZCjh+KMflPLrpyYawCBjA7L1iAg0JJK0xWJo
pMOIaILgWJof1zBC5NVBVhESmWcwZPVARQCcl7sPAH7g85OYY8HsSUhMzpgQ4EfwwhLghwzw
Eqs6St0H8BuJIAf4AfwAfhDwMkQBL3++8uvn9H9TfoM2e4LyG8EKFuAH8AP4AfxeOfj1Wyo5
Pnzsf5vhDlbPkSICgX3APmAfsO+VY9/ggz0BfgA/mOYHMx0k2ISZDpL5HRDs+ZfEu/zBVs/+
QBlw+Y3I2B1QfqD8QPmB8gPl98ILe4LyA+UHyg+UHyg/mOb3F890AOX3cs8meJlBCcoPlB8o
P1B+Q6T8eAMwK0Sz/wkRgiJaUAXNjusvQosborV2SDQlUDQwP5Bf9whDKxtxFFpup38WIcGg
tQf5xY7QIkN0P9bQikNosUPJSkRohSJJW2jVINQGhxY0xJiBoj8s2BPMnhDsCUt7wupmEkbC
6mb8DRgWeHlp5ri/mPLrZ9jQrG4GZs+XWc39L8cGyg+UHyg/UH5DpPxG3DQ/UH6g/ED5gfID
5QdLe758q5uB8gOf3/+i9n5bF5QfKD9QfqD8RrjyG7TZ8zkLvPC4RQuewdKew376A8AP4Afw
A/iNcPgNenUzMHuC2RPMnmD2BLMnmD1fPrMnH37yByZ1APgB/AB+AD+AH8Dv5YPfi/n8QPn9
1tcFr/v9pGD2BLMnmD3B7DlszZ4vpvyGEn7g8xsp8AT4AfwAfgC/wcCPTzA/THLZAvxGCrCG
8jwAfgC/VxJ+GL/yCJqszqB8pTQL9BsM/V6KTO4vZvccdLgnOP3A6QdOP3D6SSAJS7zwd1tY
4mWYLfEylNIPlngZSvn1V7YF0g+k3ysp/fhbGCg/EqNFPBjYEa78Bg2//g0hp9Gwn9T3PMgC
/AB+AD8wewL8IKfRiATc86D3tAzgB/AD+AH8Rjj8wOf39IYPf39dDw7gB/AD+AH8Rjj8Bm32
hIAXCHiBgBcIeJEwEgJeIOCFwkhmmAW8gPIDxfer4nvaF6D8QPmB8gPlB8oPfH7g88NwliYl
+ZclXGQokYjDGVB+oPxA+cH6ZsN1fTNQfk/VDvz9VQGC8gPlB8oPlN8QKT9GMm2C4ihCRDM0
Sp0ukoyjWSGFMxTJkCSNUyKuf3Y8SVE0RhMijqJxnKcTKyQYmiRQEU5hDN0/fZ3AkCQjcQz9
xdj+IpxiUBscwxEYM1CEsRyGhu0UzeIE2T93A0M7Y1iWYnCK48DnB9D7FXpP+wLgB/AD+AH8
hgh+wyeVO7/CDyPkSALRmME5EVg9weoJVk+WwEn0k8Cw/iEkGh2gMasIrJ5g9QSr58tn9fyD
F7aGOe4Q7AkuP4AfwA/g99/g97JaPQft8gP4AfwAfgA/gB/Ab7jCD1x+T91c8PdX1x+4/MDl
By4/cPmNcJffoJVf/4a/W9qTD7phhCxGECQjogmCY+l+/yEjomgRSSIfIsbivAYG0LzcfQDw
A/gB/AB+wxZ+f7DP7znwg6QOIwXqAD+AH8AP4DdE8PvzfX4vBr+hVH4AP4AfxVC8JZ2nJ8Nx
OJqeg+bTUHx2Z76IQ/N7SAzjOIy/7lAJieb5ILsAQYlokr98+CIKRxNwSBHOMv2pRVERg5Es
g+b1kL/UojA0E4hhODTNh58ehLajSJZDc4g4WoRhA/uj0JwfhqPRUWD4QBFNkCKGIPi2RQPH
QKP3BJpIhKGpRv1NiQga4Ic6lRSyDMmxJI5mU6EpVnznSLrxmSdSCKubwepm/2F1sz8ffv0z
/2Ca30gB0p95HjyoaHUBevhnj+L/CPz1+Ocnzz76nvCfZfP/ZX/zOV+Xf0ih/7/dpL8d/+wn
ku0kVf7ladzANk8/UJ3Lv+L33/+fb5P/3//+t38lhf/hyUyA9jvWQrBZ8LFgnWAjev6EL+H/
v7ZZ8A9Ushr9/4dgA/pktQAT0AKRgETPJF9jwtMaz5Q/bYH/K22A6mL8q9fdUBt2qJXnbSVE
+/0IfYLqTX5XYCAwfGZvQoGTYJPAkf9c/gOBq8AZ1XYXrEdb4P++Jl/72f/TDNCePkEt8cfi
is7MXWAvWCtwQyWfCHqfrEXP/NluQp+jrcc8fef2tB3pLYItAnX+3aiBv2M90BauqPecUVuS
eq9RAgLVYQQUesbR2WO/+Us/bell+Svthnrxl299yI5KStLSa4LRz7n6pJ5T9tuip58r/LYQ
vb7D/+IOfr9KXv/3H0jKBQLsi4HyVr7eX/qYj/b++v9wBBGorgH6vxP9HyPZTl//M8nf/jsJ
+mVnb0bvn3NF/8cySRMDT/y2/+0x5b9V+Defj5HhP3j6vS37Ta2/SV7/eq96es/ii4W/qSd5
qfJsAXovhR79XfLLhy/6/f4x9ab+chxPnjRITxYYuzq7b/rgH67/2PDx5o9dFdFX+GxP8/fv
p49fT2Uswsj0geLf1nha8/d/+5nz+7Jf382UvHx+L/MfTfHnv5v/dFySBp4+PfOjPV9oonu+
sFDn6cfPvkc/Sn2BQB39H8yDP+r+h8jzyZUn1wVT/rb4vcWS711LSgsd9TXBuwLpUfyDf5ZG
j9Eyo/nHOBmZMTLjx02YMH7c+PETZF+TnTBx8sTx4yfJTZr82pQpclMmyL4u//oUefR6Ct+I
FL+l9OhxaMMpE8dPRKX/4+NJjkBunPQd9E9KTjBKTkpaTupJrmAmOlSBNH+ZPj0PgdQo6dFj
ZMaOR5+aTZESSEmPkh4zeiz6N270WHRFj5KWG/3GGNxA5nXzf7jIB+z659ipGsQ7KSXk311/
mqb5rt2N1rY3Lb76mbJ3+3R77A8Xpxt+9vU4hbdoI8vdqMHpv9uTZJdSo1C5khz/wW8OQiCQ
k8LfGPWkQiArLYUOV1pOoCfoS/D/5SjhBfQA9AD0APQA9AD0APQA9AD0APQA9AD0wIv3wCSG
9lrpFnyvRP6GfGSXtKmN9ftqHlrJF/f7bpFJry3rU9FZ9ShwdN83yYvWJTwRtPj5q108qdeX
qtdb3DombK7O5ieCCU8EOUoFU1P1vMrPdPkevGo25WJ577elTSY5jLlHec3Vyrjk986QL35E
L15TRiF5RYphZZbrnLiFZ7Qze1ydHi9c6deZ2PfB5EVRoUZPBNdWiQ+3FmneOKNYKnddNlZq
r/rHUyYg/YrLF6krzylzWtB7rr1gd5Ef5nwoyGnu44fmNn6n9QqV79R6OHbstjaOJtUW/HSq
Ot7Mw8WocZYPmZ2jrP/iR/diNTe1qWrZf1laFXPSw95Jw9ft+msx6Qll64XetkbbGhpU5j4M
UCpRlDuhvm7/J+gE7AhZ//52I4LqlWQsbTKdOzzXx5+d7fyluvOhQKeEx6VGLvWKMXvvTHro
8rfZ6084xXc5zNLbyZQcvVhZ8baF/A3rqz0/Zcaof/BiR/dCtaRq23R1TI80PCSnWZ/d6Ba8
Tfsj44CoJGva2rLcyiIystrB0n1l/JTt27BJu3OOxErtJML0D/5iDnp9jLxVel+S+HCfUg5T
klxe0vuttVp1/EP0Js+v+krMitl6EUxJLrXnQWZV35yC4p0L54qj6rJMzfG619F3OSQP6Ykn
j354knG2nmpuxu30uTy1bq97ZErc+Uzt+O+suruMv/puq/81pwP3t4uDDU6M+SRQxlzwvWyA
y80J4wTqAwcgdWf8A8HruoWdCZFxPnYu6jWLj1k572mIaBWTfeo1xtPSlW2PmTwqZR+ZNaKv
ZsGClVa0uR46zSsqU21TPciNt+iCTkf1wiE4HalzybULN6o5Z3sdKdfzCKz/QHfl6lz3me/U
e7V/GDv7bsnMQ+0xtDElPSdke1z5nIVz/TcE5nrGrw07dmZZRrvX+ysry64FthffnOR3sWLS
45NxP/re4ibElK6Y4BFR5tdxZs8BbUcDvXt1l2q6dq3/yGWjsna7ZWlT32jlhLKGpMVry1ZG
RC/f77umWB6PqNZeI9D/5YT0pQQ7pXCloPy2MuUNjamivlvdbfU69wpVprq8/7DvYtW0boeY
MvTTi/I61UuXNCmF71y4oXH+qoryxnkx4w70Ca780tIgX2gnaRVsWHvMLl+4+pbuVK9Hj6Rv
b6zOPJxu1dQ5K6OxnjicL7VTtDKk0G70J5ni0gbf82czL+tVlWateiJ4zUvLsonu7Ehx2kc9
EeRZ5xn2hZSvjkjqvbanOOSs1rwtG3a4BaUbkTrkRPP9mx6vmmb23TSzW+OOZB9q9stMj3k8
L1v/H9avnZSLvpu7tRTvCUhsFD3o2GgRMy84ZN6NPeakpXl2GNN19PV9Xony1Se9bpF18pGP
bqqItuyVizscl7E2K7I193F2+Vhb7ZVm8lXl5quik1ZfWqxZd+661g9RCUmkkbnl1iVz1Ac6
ZpRgfDiGXkvN0tiab/DDjsvNfUXtmx854q0HAk6FzRbH3zOaVrDfzlfv+uRg9mhCxS1xw4PQ
uvZH0tuyNn7TUlYTryvPxny2fcsg+5nfbLyVZYnJZVtzU1wpMrJCXY3L837XqrCha5uFqbY4
89I2bR0rrdzAYuzjKZrzJ6TMvO2goUGS5HF92sK3Q5yQ+s/I2PA8z93lDTdUfXqlLsff6N6m
I2f7YWQ9bVKrq7PtjMKW6KiCqycty3vkwvc/EfizLW07UnvPWeb6eS0qfXD2p9gkzSQx3h5V
qz13v/GZ7ZZVWaurM226z4bYJX59VnxK/ey+yw2P964P/9u3yusuN9Xi7Yl7DDeLjxScl2ny
WWlhXBNb7tKjUtPLqjem5lPltW83JMb6rBPPC//s3oM3bL1WZiifXJfu1DzNxKyq2CP5syeC
+bFZevZ2966cJ8kup9C+1ydr7Z+QR9aUWrmZWr+XyoZ3bfX5LNTNWOFie2pinLZv3paeON9R
u/I+MceXJlWdX7C6/XhvTFe6z0+XjTbbhLVn1B6OTlE/2N/9o5bI3x5f1v9aPoKIzWj2PXvL
0k+2VldQYyxXXnL8sqlfnlmD/2bzvIRbHnnmPWRMMfpkykXr3uMWetWP9SIWatgdPk/Kq2KD
vVtSTu1R26YlZB1On1pamu/4s7ra3Nyu/ENBVpUh11LkU+W0e+rzzE+PIgKn7R5VWGo0zSbd
0sIIjxJHf7D9myjntvd3bQx2OmS2v9Prcr1ebGvThXRv09NH88Rz4zJquc1BRls92z3baVNr
rcizh5ZOXdVCnjBwKc1VUL4tpYEfH1XL1UVf3yV3TmBir24oFfb99rii7OXxYbcS2031Mpc9
7HlT9Zt9x91Lgp0rIsJnzMZbY25hBg0NXSe+tAoMvlP4MLKl+Ge/3bEZTrHnz7R0HvLds1gP
c7G97rU2MimPvpIcvcHM008pzOKev9O+mSvNUjNPtFMF7++qSqxTNvt5tH3vW9PjZ5ynq7S7
ypXi65R98jZXZDs8NKzINF1ejfM361EOmlv3S8nLn7XTF8gLnjINOUMsomaLbq+LmeFg56tf
szh7ufOe6s49LjFtMt1slvnjlUoP4vx29x28czL34Z5m+rx87x0ebGvTN971PHrZ1KXO5KZS
/1f+Pz1LF9fudzQ7va7FrH1vnO75tOhVbjcEjxasOmaRlMWkMovKN4ftLvhsHp1DBCjlTrBJ
33g+PdMjqVnu5P7iz7b8X2moaHNF2FxXrXQz1/PyUWsbVN3q9OpzrzeWOR1dN6f71N6YuYmH
tcW3xY33TFpkiIlBreYuJy4EhO7GIw3smDbpXv2CkHmKIbfH2Bj+Y5SG1xLFYiP5jIDABkGN
/UpxaYHH+cZYPQ/P8M/uvmZsWqF8qc20aXlgk+ETwdxrNz6zjo+vm6FjaGh61s7x297IR80P
xq6aby3XEUuenXdN7zD39ibbt/4vKiH1buOBx2VmHg4+bcXVk7eWtKkwd93NPSJ6GHt53a7e
0fbtTSdOlK9tMe9t1MxSe/v2pEvuXhsMHc53z3u4a6XBI+cNvjvjjSq09hNFTinf5dGdTvnr
6/XG5LuX/Ky7i91wJy7myHnxj1r7/T79+VTyexUrmYSguHYFDa/6R9+ueNjsYqpzptolxksr
bseJpsd7ch//9I1g9P2BLwj5HUcf8B+d65ilbBbiJtNIR2X6eZpbFny+ev2DSpXpXal3eo9G
zXsQhxiH3iV9k5w97Vp7vN43BqUbe3fU/JBptOrrnZ/8T182ur9fd/G9aLE+K/5GuZHVffE9
Nr4031f/Ubo4cY+pezltZXnbwZGct2OKbK3Umtfbm7y8NMS1TuLkdEM3sd/urZ82sNuaPy4+
2uQUGBdt3rUufNycq0cuWxiR8aWL54bG+XywtbJzj+yWOYYfjwkck5+zeKH+7O5POx13r1FQ
9bf/JMAf34l+nQ9rOGmBvbJUVZEgXySdWSR1oijRKq43tLEhzE2pYltlwJ11Xb2PXeQ8Kk22
lOjU7H17p46ytvN7XrituUmXlUpNdNsjjYyEfQqaWdM21JXWKUvbtih8W7Yt8Zt1kQ02G/QU
K40X+GhZOc2ivLrvFM9JV+kKr38w7VHx2r7PP3HR6kyt8NU8UtrobM1oJa8vM7XgIlt6ow5d
JFI1b7B7Sxw3dNlatC+c7zJvbs10oedG+6LgNj3ZPZqn+76u8xn1RPDDpauX1goLbmSaWvr6
lHn3kA1qQR/m2qSbVvh0xIS8pbb8tO9XD/faaZqbLquvm1jSbrPoxAodS+OU8pJlXp5fLfD2
YG/t2NWRovtV8N2TR0or84XGPyrH2m016f8W+XvBGvmdAn/BeKQ2NAxOVMebr+/wbAqfu7/g
Z4MS42llpZ13YtOeCL7wK05Dl0RWUO/RjDsPCrx0V/YElDov/y6TPekbFCNb6/v6pJwXvzCk
bR93bL4kzvK9aW6ER0aOPevie2HVZc8j67wvHe+J22q1OvmzrdL/F2j5MX9V7GEPXFeszpqO
G1Gd96w617Y+iHm7UGWGqkKxbVKSg+NWsdcj466p/0iuJT10QpOPbRTlSm9XejCmpeBHBbWD
ijmKrWeEuJw/rm5fqKC63EBj/2LL5SFLt+VkuvUE4PLq9ntDPs01M80JX3BQdulWR/XFPeln
5ht/5u0fGL3GcHPgKPu80blLz5InXduDMy8lWRt2lZKC5mP57h6n+rQe5M++1VOy6puYsKvp
bHqUXzCpptgrVYN+K2W3I4P6lIq7egLWp9ibm5TaTrWN/9nuzZkLq6X+ealin0KzkUdj/cZb
uGtQp9WBLOy14LrV7/TuqVVpvNt6T2xz4HG31tfON4yWx9+Xa61ceWdl6J1Z4i4zxVSPiFvO
1oZXY5YkkSbFPxkXNqXNXv9Yr6Nr75jyko1Mx4mGjm/a6qrjMcsNN7KOX25om7p+XkRoiuWt
td1hKg93eOEKd4IexBk8rNQ72a0ccb77aPHn5v7J/7zoEZvXaLcuy8hFx3XX+tJjecc7ueYG
zsjd/PAxtxabIBnJN4uc1bMj1NGVIlGmx3OIk67NyVdtk8LnJCJZt9k8t333tsbDSXpZS2ff
RCO2PPnHK6dZ9JDyamfQdfNFWL3Ww1Ldab0xhSpyOB6xP2cOaucFHpN1NfOoH4nLvr3Lk3xv
pT0u94uZ4uMpV+uVNNsz2/eIuZprpWt8j0+Zm6GcUq70wnWR+w1+qm1bdcFI4fANm3lpyea+
aScZTR+TIlGvlWoW7a0Y/953jz3nBMY5HagN2dJ1Vqvk4qamGVpu4ktFTok+VkUJD4xc16d2
0u52uufl2MDPjd801Bcy0vL3x+QojinQx+9Jq6phGkzFLP38ahUD72P/N7XA9LPlYR9Wvat0
+1MTkzlpufdvBps4eAbIuncePvZ6sKGJsf8XCyfYOWqoVH3+YegDRXRdnj5jWBCu/+G3yzZX
JkWGLNW+rvJNWlJciGdTcNvjkpgYzPNqHWVid9PKrG9tr++altQjpdXhx6xIXYvsnzdNSju5
yDMlmh8guNneWPH+1+Rd76/JyH1ulEl3XcyPakz+qTBvnXzv8vWsxzft7s705fXprn73ruX2
uGrWbom/EPZVZFSXw8nl38aMz4+t9GtIvjVPd/Xyh57XVNUs87+iet6ZW5PpcM/jpvGBabX/
GLvLbXlems6Vk7mU11GVotWXzK3UZA+3H1c5fmlFPq3TFbZnavihCx0dR2N7Vbsd9eZqq737
z+a4r27jCS2PrNg3VrXEHBclGZpcNjXX/UilIy06ut5GI2NOllN2po3Zj0r+KEZFME6gel1/
4DqIdTqZldEY65dJqu1cuKBt0sfZzXZprUn7+z4ca3QK16to6H1o1RPfPtZ0ppnx6kVZ/9fX
Y19/RmWqtdGZe+Y2Vqo4J/O0pYEGn/fnNeUQj+Ci7VnxFzs3NnJmLSVN9Tdf+yrLq0PcbH2v
UnzL3U1sucTfccrhc3dLTSp/HSPezHz/2oQFJcv2vmtZathM+857IvjJTd49+QfbyNqoAx+f
evuo+FbUId2zZRssHfCoH9u0Q0vxbvqAaN9nV4NbSuXd9lvcaDz7Y9WyH1rEp9rddM2vH1r6
pqzh4wDvzBtj8n3nzSJvTgw7rJg7Yc07mocT5Y6P+1qup3NMrvH8nHgPXNdOTllK7ubcs9tG
22z1+RxXLAxcMy4wv8rIZsP3qpnoLlYkyFGbYrP0gXqKqr7xAv/QHz+SNbP9yW4WiQuOX7Zx
H2ua9Mbh1I516WyDyuzKyee0HQ5XZGj23a27de7m5Gs2f887H5cW1CrGH4RfUJGzStxXkM+E
73zr/KwYC2PXW5meCWF7DC0nm5pJldSctBInJKYvKzWszXDQXpTqoKEjdf9H6zsxx2zecRKz
tjusiutKrUSz9Fry18X46xoHbZvk9PAB3RqNewSGWTodddCrO7S2a7zaIvHdLzewNqZup2db
b4zsjfsmLVNtXM3Nycrablb/zBQle69X0DxA55biLV+FOxtdW2DK9mXMa1+hUzV7w1bvvzlW
cdqq1V+fWOjVtqOrfb/vR6r5kgvNQexY/U4mGgHRRW6fWRspNFt3bjTcjgnuCBRHC9DQZ+Dx
umamTqPv+VX48R6DU6Ebf7hcVWaF37CueCJQi0CXnXdJ+Hq7qB8b9vugS83o1IJvk+91Nhd3
JvQSkxM971aHVGQa+Z1eZsCHkv2HB56UsaCUvmxpYYr4tt9QX3d1iEd0ZlXz25PE6w7tsd5q
uvr0jcbXYkJvLXYRnFU3zPbN/yq30d1TY8fmHgcf9YaC0x47UleEaXpQC2fMixB7n7hb8mO5
ru8GBzKjw1vzyspTFdFv5GlecxJXR20tXV+a79M3PiM9PDuxsXLW5WOpU8u9Z9btmX+8Ldkm
2dzmsu3yGFzRzr78nbnhU63yH+Ub4jqCHHnVLWPyPW7K6I76WmVhoB2eJievfNNCKUw/5ZyL
rHGOxU0Z7swXOmPwC0YRTTeuz5HRXZMW/aEcXqhwxqqlR39/e0h3gJwgbSf+veJ+KbmdNlsD
pshoLpIK7d4+v9A9h4zt3Wwlb2ohf3NyBhsXG55lg4xlIcW5Kie25Mmnbi43K9KVzy5U8Wiv
8N6VutksW/5Br0Gm6LZuh2axcwRddaHhnplXJmWlMy//iWDK1oq+wtbqNwyvlX8Y266W6RWY
jm6MxYVqs3NPBXrriKOQFcTR1PJedaltlN59qyiD+z3v3vl6xzrSenLt1cBbS+PKSsNXNBSO
a6N19jXvlQ0S3xuf7lvpty5eLMztYR5NqD2Zf69ho/eiEte8M/XTDEvfUj3xdapXsOMGY++z
3x3u2JyVkn7Sl6x//e86B2Z/Mr9Iw9lU92D7w6q4VFeyea54nPW2JDwuPaRI561ppYuPmbm1
VPpvCIqzX4co+evlMVogn2lyL/Da3p2iEnH5it7ouLRw7p7vmjsn89opZFXK6CVNngiwzdfq
Znhlrzc657ul0CegdL11XBab6hscf3pRj1Tar609+2qs7knbuBsdDn3imxZmS5osuwyl69iT
M8vaVjzed600t3efC9K++Qb1uXOK1JUMpWOCXHRmjzvWTNOGl/GoDbn3dE9NcVcbk8tmT2/W
m9IdHRycZHMgRdl8Y4xS6xffOlyu8lj0vUeaj1FTSbM7XdC+NzHM/Iaq3KM+C/cjZ7qbF4vz
P60pf7irI93KYl7bxsp9ezzjHNUvB0VWGgV2TbA/827xqLiuMRE1OxXbdn4YFO238wtt9b9v
E+Sa1ApuCdLaAmRN7gWYuBeOxsZ6/swFLPpIQe7iaDwsNqJyXHzl6AIuR6g+PjR208SwNYu3
3hwXcn9M7v1OqUYZvTLZpRqzNk2UC+1bY2i3RkG5/hv9Ak66cmK47hr74p2K0Vt3flwd5XVf
pslr36VT5Qrz4i9umrzPZlkz2REbdeyyYszORQtcvN3thJ4J7YExFw1Kna3jM8+KHXzi1aKl
MrszDt2z18X912UeLK2K7l22LirbSxQTsvG1RauvnpfJCDqZkLKxXS3dq9Imvj67UO3tXN3g
RXriSPGlLza3+3ZE3S1pjXNbouu8+uH7yaUmxZNr2/M5NJTS/rEpHr8/9suEuzGfpPk6hanN
yJhbvyrqprXaZD/1raltC1YF17ut/C47PvnnW9PM9TCPhsfveYSYzhDXnXXUiyoLtzatqDKd
2Rj349br33plrLqau62vV6/+TKv3jFWXrybLNTdEtkZ/pFWWUqGiU5wVvnln0jkfs/fcHpto
nCz1LffzuEXek1nzy6UzSjD2A/3lOXhEUIiJY5lSiR8a9jNNh2Ye4pD0nbzPx7U9IT+uzCa+
83CF78z4m5plF5uo7rM6cdE3rVTsj3jlHM35panfv9A+hRccr5wXefKxrSEyfsmfK/JRV1M+
cqlxy+cN2eL0avFW47/Z/6wZG2qO7ntKpSaFuYYOH6laz2yetXf7NXGV+HD64bZ6U7UjRxxO
ab3vGNJxztZqhlfiDtt7Te7TnOVuqZK3Hr0tn1y+SOvKeYWxF/NEh4PnhjalL2u30nFwPNLz
zwMVlz7y6q5+wyjTz/qisUdgk4r5KqOK2wn1aVhgZP0UmdnKOTtujjb+4ue42Yfnu9UsehQQ
5p+5RSoo+tM3uwonnMssk1fe7I/XtYzhr7HxYb7oSg0Izf7A5hMZbf/A/D79tPCy8SHGmKDp
VM4ahZglrYLxQa1XZDdODJ8zJmSLY47shshK+cxTdlKO3zg6638YrtI6elSt/V5/uaWV/rlS
oW2CtJpNGgvrIhQjx+RzHykZWS1uU69ytvIq6w2+HfMe4rSWa6g4MEZ39c6FzW0r3Tcss7+k
4ae/eWX5h+lyOFX8bV+aTE3jbbK6ICnnsqeRXce8dLsqXze5R9vDLXIeegXPqjrrFOW4LjjF
xqxn+dgiF7VDqkVNbpatWTRttlKniWzq8EBYdlz9cNHG/eWnu8J+KNhzVqNdt6XlTVWZ5DsP
UjO4iIvVF5vws1EbPbWQ6Dviu+Y+vWLVxU1HCqZcrzjnMrOxw81Kr23xmhmfeISJZ8t5iV1K
tcwb1j22Phy/p6d7d7iF2bVFJakr6468t8krY2OluZpXBvLH6Rpvv3Sxo9jMU675TqIO8U7W
Ip1vL1aGtrV8pfVDzbSSyltuqgmvZ8wtW57cUhW3rfaEYe79nQNX1WjpMwJ9qdDNeSuXcAlJ
fcE9TlS7p1N8/Hvh4+/LPeye5H50W2CW87rQxPijhNa3v78Un77zqZnRbCrKrFilZGm1el7S
g2C/L/N9Hs3/26N14sw9pp7zosRiN5KMjBwTaPTxlENsHE6b5FGlP5YjS6/u6uPbUlK+O7lq
35eVua7ie3NjzMbZ5HuueltwN0a+2bbR3aulN3Syd8lMcabqKrn61jbbK19lr75eFXNhk63K
1Lyo+VdPKsYFhnwcWlG9JaPlLauaFEPPtaGx6qob3E1tDb5gxgQWRMzPvyalODpwTEtXwUHF
/QGlPp/Weknpqo5SrNGIkFZ9XUZ7k4woV39+vld+jqd+sIdAQTm/+mBE/vW0+9K+B9Pujw6s
P2XgwhWafXPdXm7/p7nO9QKTre4583Pk5LQPTtY3dD0jvNqQppjrWilrrK5BqgpSzhVcUFDd
FyB3wnETLp8mfHNcyOaaCwobcgLDPpBZ+MnEcPVFaRUGLn3+dvabPhQfjt4SffDa4qT27HTX
dQ9lHtssbV5ULqd711e/MTUvISY74tH2uFD34CeCaeS9HFHnUStlB12/nXiimVOPiYm5q/bs
1ydNaz1K2xw9r2pphatN1r+f9qVdF/N6UPftHaa+jkebppbrNoQsCY+83DvZw+uJwOuo7lct
0T6bu4OeCEpXrbEuavL9ItXDbeFk2mu/a1xvWGefk6PaG6rT4+88OJFh0ruqeu9Kub7aHscb
y6TqGh9mHbqRHvbGT+4nEsLcTROifPHvqavNb51zC3a2Nikwub9CR1nl+3LzECey0TL8fbNr
B0zZ4NhZ2nZHFqjG7W0Yq2zNzH3UZxzc/rBmyQynNvmEOL0dzoVBq07EnFi4MkW51PpbZGGb
37HDwPPAh527bJd1fRN802Hfw8cXnOPaxX3NZx2rZTt2CqR5C+ubOQLpGXeCD87seLvmRkVg
tuPeeQkNllvGdR8Qiot+yGPulkc5deV2LXnufXTSilCj0LeikhuFpRurFp3/+2uhdbbfZuc6
HBXtzVpvetbPK3v1uPuWW9qUt8/5bJmLoMDcz+xQysIDtldiK32c7gda+sxet8jee/nqsuOb
rarQ4LHZ/Mdya5O6/akRRU3ld8NLyns/vuZjdpwycr89K1T7nqleXp2uzaHzjDXe/d0B4d7P
VwQnxs26ua3CR2f5uvom+rL7NAfxiQZBrTghUg5PSwxpmRh2MCIotM5X/6CdDyazcM24IOnM
OxNDihwrx8uVTdcsnLzGxL31gbTATj+wVz8kX1Ng58KG/rR1cY7JGtkNJ9MUlOrZM3LK18fV
+Orb63Cjche7RK+x43KXKEZUTmcO5HTWFU6qXxvqH1jcODHwjOp1qa2bxwSeUawW5MzP/Uh2
y6d1MWemC0LjS3NkzcyQUUc/rWYNrrNG1k7UJi34WnVN26KV1yZLXYlWdg7q+HLl3QWrshZH
nZczKXftbayfei02ojrhQP1ZDQcXOWKyqdpFtY9SvXbMUK78+1GZRCty+nwXZQXK820Tw3Ld
on1lpXSthuPd+rWRNw2T/5nqVdWo0Zx4/LKReZRTnJ2dfQGm9ZEVV3970vHV6YsflmPI7PF5
V4GXXfKHZxZuaLPZYEWqft29PS7sLaeE3ELvukfbt83YQd/P7V5C9iX5TdfxkFGgvnk71/t9
5E6JDNzpVnljodOhu6W2aqct624skj5bq7Pjes/7+JELDbRaR7eXU0zIGjTW8P1iESk+v6zL
3csrPmmfuaXfrcQ1PsVTuidnOpOn0y7FXf6cedhXWm8YpKYn7p7fnPRVQndW1fTkn+dkVYm3
lRv6/iNZ0/rqqWubKnvXH8uoNF652XvJE8G5XfSt8jz3hQsfR+1jPrGOtiqlis8bW4WVN26o
S09Mrlm2LPxvBRvpS2297rTXbq+Fft/qmKp5hTzKM/4y2fr9h3uDwnqq4nT1dl1vP579npdT
yjQn+76H9g/eWJW/72TUopqwqlVf7VpfVtqxz8hvL9f61bSGde0e7mqunq27l11HQfMGAhmF
BXkuZ0zXl6wXtmYZ+2o4pS4rL6mrV3XSjTvf5LXDsvqYjZWRS0SEkcPTu/qvfyerzs17uH9W
sZ/5svWJLSvDs6y7tm6/0bV3ennb+upS82Vz4nzz0h4ffyIIjzr0jbpS7pIjB2f6WIfc6aIT
9rUbeaZEbTDs8x3792zdyy5heEWSZrtQzcj6ntVFUWyVLnljSmVI1eU7B4K7uZSfMzOOWi4+
tNJmW2Lq4rKCz3Xl6ot8TVrKC8PTxS37vrjWsjzPmnNUNj60QPvA0thbFcgJETlWT3fL6Hyu
WCfA5aLmGlz+oiCi5syktjMKStH6EaOkXKL9U6aMx2+or1HIDJFSXbNY2ytgZkb3qNwlyBUm
I4XfnHjCQ1pFkM9Jhfnk5Pd8PzH0kYN+vteoTs+H0qoqBi47l7b0VgZgEx9IK7VWKgjsEUIq
Ze23oqF1oR022vjg22FrFOSOr5H9aLpmwRpR9JrsKRraImlVQabrmIZIafkQqaoHMllGTO/n
xeLHehuqom/aFFpUN+x39vd1vGb79kUFpSy3T12WnrPO3aKQErfR/LT7sqOlyenWi1YEJ1kr
LPgwvs0oQ0ucdm236bQy37crJurENatmv78+bO2Chg1Oa+ONF+9Y7VUz9tB7TsL8ubFVDcF9
yVNLTc5nmleny/V+bKFyzVKuyeRqUm7rqnyX9116Vej1afFOzYWbElcVZNGGhVdactfVasrZ
FvV62s1Oj4hKXvnaD2Ud507sV175E22jcPxy2snRl1rFXTFTayud319vFnvR3HVdqHbJVHOj
q+L0qMa4Yq+M23PjIqO8q7q0Mj/bxrp4dS1N3NG2Kr8y69vSRkdTp75v7h1LP5K8R9T8YfqP
NZH3HJBDoiowz8oCXW1zrMs2qcXp5nd8abbwwMy2uakm5xmhxemW6pMbD1ccFt8Sr4/FubBO
70y20CR/1gfJ4hsqB6/7eBoZy13fv9ooqdTadllCVnyW6WbTzYV5lrdnq9yJiIiol389+GHC
/iJ79avTCu2Vt2/IMqpg4hLCtzAlSZnySrmPTyLfW/g9w4Jv6x/IdLt3iCscdFon7a5Jtf4y
wyB6Q7GN1/YZR1Zkyk+zMHXRrrVXr0/+fN28W+vTe+SpPv1bZR3exofj1maqdDu2VsZG1dUr
jS1uey226Nz6WodOqRvl5dq3d6zKTw7V0F0fuE26w6nD96j96u9iukNNrNQe3f/W53bmHQUL
dBt5/K5XRFhU6JuF3o1xLvff0V5gXDJ2w8Nys3J3n0XWcmfnZFPlrRF9a+6n6nzZbXDhtrOH
m7ktfqncshIxm1ux69bqvgM32v1Obgr13aey8cOkmKLpu04aXJvkEXbTar21jX1rOefve+BK
9bWrdRZLv7l15lhimGW9U692z9fWaofuuMcsj1tQVXHTB8UwTCtDoSujBJM8NxiZnzE9/UXb
jK6PG2JvO5rZ9B7uvdrmv02HtrDFbacZWZYrBYVZjPrh17vCwKst2m7HO7b4eb9/qKWq7H70
8WvtbTFvBa1W9upFw7fUGfv22KTb3HZKjAqasttR7qYWsiB3OpPaB9V0Ch6v/u7GcSvHd12j
klz3ZWl2+VkVOrq39Wh94VJd2eQU+ma58/vTalvEhyPD2fhOcU/G2baFvV//sC3oxo/SxqYH
6Ii4iOpbFZ3i9LbIJr05j8jMFYXh661yF1yJ/aTBPlPF8Ujsj/v2zrpZr345pOjRKO0AO2RK
KfZXPKPsWkOMNjRbcHPyPX/lM/O3ukon6dfsllpU5FEcKGdm0+MfcW1rccTMzp14mhDvyZGW
u1w9dkGOv80WfTkVTKbk3GHhbBX9fEfFynFhB+0XfXr/Wq7s5ogcZV9/O69P67S7pcK+Fnj6
/ORyWWC4Zamg5dGoOoH9GVnHvR8sDxql4eJvYzKqbktNhNy56OqDhluuKwjcQh6MCWwolLXz
MXDQ3B8gh+4YtydWdd5UXJXi1J5xpDrV6KxWiJWpeYRYe9bsCF2L42qGfsbbDpc2ba50/CFj
4Z1aF0un2kLTcGcry07v8sdcfJbNYtyyV+wiL68YoPZWXl9o2vlth8VJs+1D2/rGxJWuCFPa
eCnbTN6uRSuu/njcPVfNqedxI4/a9bmXp5k0T1zySMXvieDLU5dQjEZ8Sq/ywkVUTUvDJ43z
gu9aMOv2ieYcyjSKOlpqRE7L9Z6TSZpYVwdrfPx3LPp8x7EfLh+P0lL5onazlZ+pVfTs/KwD
otSFiS7W3o2X6g1QGJ54RaRY966nONiRNre0sP1H/I71i0jvoHXeaknH4i+Znp+alxm1Spm5
2xBH4qcfLlyxLimTwVWa9iaeZBZlr1csODb53Ez7VK+lBZvWZ2x7bfqFylTXy5PTTydb+73v
uqPcmz25/l2nqs1FcYHBiVFJNpm2LpVih8jH5kt8z1/xla/oUzpYZn5NdZGxXLZrT7ldsHfq
tlVlhobmjF1V9rr9nscoC3z/tiOecVoNmadIjSMWeuqr7tovcjC0sdt2PSWix2LX8lKvZm3x
zUm7EjNPOMy+JHXiwOb8UsXO7e4LrzTpKcpUuFNWl6T228T6FRm4GYd4/xTqMb8qPtM2Y334
+MAImai0VV8kLZt7qEsXxVQpsMLow3noZqeqFJzN7tyaUZ236aiHb+rBC42afZnvm1q0jQ13
u5N8bNWlfR1bJn91/uysecFHbMSVuQWt1xNUFNi3FUutSfv3XW9R99Av87Z9sa/TwiPVZaaK
5Wvbp1rPvL3BKuiRxtdHSi1Y8V2Lpu+XmSeWmmk99MuVrRXPe5xaqvvVhPHq7oIZzsuDDy5u
kcttvFDZnRSXjCKsjpFdsx+aP9zf+ZnV73/oUqHuJU7IbpUUtS6OpK3YQH8fP5XmDZ63j86e
IBYvuC/unCfuUxv3oP5Oila9xjSlXI1jgaN6H894nzxcbrvDo+7Ig5g5bWN/9og/aW41reFh
u+k+uSINz8RLK9BP3nvuQ/fcx6YeYW9VzNi47rhbR0KpSedGm/AZTwSu2und7htPE+2P9SZe
z5gs921slWhOikMVbjr9TnxmYCtSVKfXHa2lrVWLwlMMN8gpS58XZ4ijvTeOD98kFOy3xx9I
y10f6+Hzo36Bvrag5dN26UtSGtho/fmLZ2sH4C3SiOLdAUqh/vnXkT9b39BsrrSys96URafU
00Zpnpnc8jgg6FbZuNBO/9Xqs7fclNG8MK5eaUxEgVDfcKmBHSaTY88VGbigcUOB2eQ17lcU
VNekPZDOTFOsVOBvED1SLnq39Qv2Ygudd9q4S3/TdkHWeefHYV8/CpDTPrTJRipoFIGG+Z4e
hTkqlffD1qSF2AuMFn0080eLT1vDuLgDCso3Vui+ERcZnBUmPs+sLXSNbjbHJs0kfzgQdf1k
37Gft4ydXFIdtS3meEpcbPDjUyp3Quo2vqNjs+VBwDINH801NiZ1o+bnt9XODfNPUdqpua4m
eed84/n6XyzsdDBaHoes0YoVBvutLBeXS3+8cMcuZZPtbFm5ciHyl/xwwPJ+bo/BgYWHo3+Q
rTM3aQ8/o2RU4dhrsNc38olAnzQOkaJKLO3sZkkVu32xqSm9I0prmmN+pXT0qaLWqCeCRxvv
tV629P37JNrD0bg3+pCFc9dG34OXdfYlxVx1MTX0mz5PZtqmyW+ZVdbutrpltd/n/iS6tYhz
Xpv5bWJXZskjfdrKPsz8ieD/PkzvYfBH26PaT2mGNyEX2RPBsXRTt1Ykg409RzePSbQ+fGPF
o6Tz7hsc3ragzFrvHX/8g8HDwwd/d9Xerp1p/N5p6sHh8qrgdQ0qTjHojt2lS1ZMWq2YXll9
KXr23Yqg+nrrkNSI81vLcsjAaT9EuR1/R2v7jrZmBZnYbd/mXWs7W7m0pKlbKSijp35Hx75g
l763jCdfWJl+5NKq3j37bDULfo6yP1L0RoJSamfvF91a8e961EyvK12aHOiYZUTlb7ga01KP
AtO8tpWoODTeNm44XvLdjUt1WXJWLkrB9ruJ0uLyJqHTvMLyiDuTucKiB+r2vvqGGzocNo3O
R/cc1evaGgu7RplsyUc2W/K4faGs4YPiQHmlGnW7rYVSchdktwpkNLURXyJmLez6tA4Zd088
uiJr3Dgx/AP8ugxTsVWqCnkOQg/KbpHy/zhc3WSrVNDtiWFfK0uFrZQKbFBPC+Qd8Ga2ORH7
H3RKhf7kEr1p4tS6g28aBwq110zXsHNRi5BT1T/FVcqrrvy07qBwYa1+4E7tn+w0Fy1GcT63
ZaTsdAzxmXkas+VenygXskZBRZB7P9/HPzBmk3ChfYRQ87R6ipKcvfIEtwMBdtpegWusAgsO
K0bKbUW/PUTHaJfGebnGb38z2maxKPqdiAKdnPwSTDYzLXz8KM1tNxWUR3X6SLnIl270T1H2
wzRIxXwDO/LM9Fk+joIUekvAviytAz0/eV8+1OZ4iZCNbb9Sjy7SxXGnjvf8tNspvtPxgYx5
QnzyTVnkNsUmNm8oVyw0+1HxPLW0Tb3gqj5dU7KufdntotjyzONLH5huzs0hSk3Pyd8VltPm
vQcsii86Ptp++LfXkarxzObpe7eX3K1TcKcXr+NNrgkNo7Vu0Bm9q1/PXnjg46tJCbdU5oaP
C9t5WanJ0ninyGIJERkbPC/dNWNt7IFGcULuO1q3vN+9tmPG3+alnE6y/87acV2M2Wvnj+RW
+fjJ3LA91K1ffn6mlmiz+TJhU5IFaWj2Yayeyuo5TTrT8716j6XoGe9X+6Fi+cl/ptC2yfJ+
Ft7NNun4JXHGIwvFwNYvmPVbdz28nOqx+bjpUab6Fm1mab3Hq92q2CshcqdT/aIAuQsKmZfe
fE0dj/b33ForaLmuoLxZWrm5TNaw/aG0slTIBgG69wn2SSGrA7pKjOfemXgPFeOnMGSgVUjG
NBY+zgmMXiWw43oCHLQNmFZpVf2D9udujw2RMlkiFAQG1jgHKhbNXmPjwEmFIHdSo4yu+rET
V6SV0bdMCtZM19xwc3yYee1o50U9AXZkq7Ty5jG5W0bVyZ/ETNsaZbMjvhD15OH3xoTZzV98
5Yyc0jSXC0b5PgZ4aFuhVcgnbwRYq3Cjau0E7f42xkvOCMmZAS7XJ4YrSe++OzFoTD6z0zbd
R5BrrG+zZcl81yIp5K84cd3+yBkhIaN9SnDu9YnfK4aMqnUrVFBZ+Ol12a2j6sgQV2k57Z+8
U24IPNfdHOuWO7n+i5ysnEVf146ny51Iuu6Swdpsp761iX4ovrzQ2MOpOCaQ+M21sLXHeceK
690zUunaxK87Npg/Lvc98JHaPttMTwuvLKPu25l7eWOn1zmTo9ihj7HgW7X77Q1+OmrqlbmL
wSNSTZAnaPTfeopTY5Ywb5dPj7vZm9BSkYJ2a7XI0MLEmVywpKjZq3dH96za3u/SjRWaj1h/
d9Gks7n1TuK0yyqz2s3PdWnWaN840L1ed3XGpqLXYm+sWOlxdMUhM56HKGTdU05FQ3O334HI
de5ej8Q6B46YG27231p+mXaTWbTl0+vj/LX970srIqAFjbnVJ7DfhI0PDIsYk39FIOs+OrCo
5HuhaEyBPzKU3pmIH785LrRVpm3n7Auv2dwXKCTp58jLnZHd0o6CNBr8kezNkd2MzFFLHwcE
FodIBbWOKfgsQO7+KE3dgylKjTL4yQdj8hduDQgJCA3wyWkqvTAppThC8T6KHktrCFD4x3v+
H9dPGX9HRltq76ObMnjoZ3o7EwOmq/9dfbrG1puyDvY+n9bFVf8/9t4zrMns7RdNiIAKggwi
IBAYcEAFkRjpJMAMEB2ByEAIHYcoVXonQCg60oOVThhQSkIRESmhqUCQFpHeeyeE3st53Huf
fzn7w3ud95zr3e8H+PSw8kSWv3utuxcWWVZYemCoOxDBiod1rrMSoSHO7e7vbtbT9ELq62RQ
XxIvNEoBwar1Rk33skQZlEXYZh8n+uoMx3KfIKBu20rk8pCUWNfjH8ZWgIli1vHCFYBXS2gn
bKNJuCzecjJBTHEbYgm4PYJl6PHKCz0YVUORPkDaTPfXt2FsA6eE/B60DZbqqfuAF4Nl/Dz/
Je8BqBFw7i/DLJY2XDDgxWDQVyLYZw48oy0mVeZrlaNv2abcQv8eGGR3sOYES3PrBLXbRnvp
DZZ2al9gYjD64uC1wwxGO0lT26fc230kon44PXhufuFdUfuSIxU12P6LNddSY3IBJmjJutsi
KVrBs4e8R39p+zCwMah3iYAi/ZYqXcJ/dSJgnhLpHpXFcCzsFLWRSjXPeXVhd50EjXEpSzyU
uhTEqpZJeSak5fEYy5aD9dg0TdpglznMG02ELoFj6BpyHLOrp7ZZJps4nWvlYOmpdXUC6Rm4
/M0+biYAkauYJOAgmW9JBBzlsIhGjURIoixYGeD/gLlDPA9Lq/QH196T44hdXWkSoAMPIQBX
wWUI4UNtVHBF98ThgJBi2XnETgfh4FWhwytAJEjDJEa/Dudmgb4NSJ90scSk+SZ+hNjpOI3y
VoANqOLrtjUEIg8+uQNmUqFaKCFRYIbjwoSU8mBiNBGsa6M2pV2vv3OhUZllN2zsV08iD7aw
7/x0BN9rlbHTEVOnPEY73SzwY+e2iKCHF+gmEMG0KrB7p1j5KmtE+vNTGldA1Cn+12D3FdbE
QbW65dmEe9ZypkSBeIsHp2lWITUZkOt100dijZTXc/vdqIxbvfnET1oBTbewPpXrI4XuYxJG
vYCWlD09YB+30X1e+vlwyxDacNP5FzhMNKDmZR2SeDcnC+V4awtXbRE0v7Ie79WJ9oHRAe6l
8Q+Wwd7oQ4ttW3zx+VbpYbRnyrqI4+Gor7W6dqteYMMt8qWWrR2f9Bsj2Y7k3LaLk6m0mB0N
dTiD6CKdbTu838kLj/axj50J/NtT3KXzPUmrOpPxdkCJ6DizzTVegljw8mq/YUVk0seIssGp
bZ2w/VE7VenPVPUvDHs/q7h24l1bmN4twwii0ipJeffd4PfagjLbpLLsGJRZZWt4W4WPU9KQ
AJgIQoDd11kUAGcwEEIeDM64z6khqzAfr1ojGAlpcZNjQ+xChMIY4++A3GuPOfZEgU2IiHsM
mGeBQ2C26UzI1Rj6GgTqxyLGafcIDPBZsKTiECC9J1u5mKbxAKNQ05CVAOHywTxzHLHFaXXz
8WrFrb+Ka5sSQbDapjODubKSChCBQVD5YB2n3QhH5PQ3Th2fZ5x+TCU+fPF3fzAP8lcZnd2p
qzxlGbIwpfO7YROBrBbOc4Bk+lUi0JPPRk3L6hkI13U6IpLPt1EccHTrRmjZKoSaAsqS60FI
RN3NRvcPU/wJVadD5Dgi6mQv8wvZTZxC1fNny3HMsSM+2ajZauKggKE+xv8TRwQL/MPYRcV4
kxHwtcJkCXlMiEORqS6qL2Y3XM93uVeAaQNrVon4otbwp1G9a8if8geaX/N6BjobHYsI93Bv
xgNGpKP3yOROB1zQFlDFpLEnIvm853WXScfAlsJkIbLberZV5FaHHs9wNgzU9I/zAfIbzp50
/+wV1CKP6nHVaig/7FvEUtct9IKDqg2BWgh4ux3lNuPbvENFynbWHgVw2VQjflZEvWq4Vdl+
3afyVleD77XF5qsr9MfCKoOAkpyZLvR5c72x/LXf0wsViDmqR1oB6kklgdO//cj964/4gzz1
UhCfckUkWdkAqADS9lgoLR1eXA7xwMCVk1LDdG/zTH4EVM/7rnEaNsrgCEglm8qD00Q3GQ2A
7sJrp5jlsoqADIkLuS3DFP4EEyufFktsfcDp+o2/N5FXaJkj5DZNhmWy7nSMzpgWuEW4DuDU
9dwyobD0exwhepOJNxJBuHp+XuEMTucuQBzX4yc0lhsVWCTGxbzqbuQvidejYIYiSFDNi5/Y
VMCidvctcEIsa6cahx9chEPjOUQCpvgFp051Qm2uZB+BqiojcLxpT8QV4wigh0CWQxQVB9Jy
OeU5xcGTHmKj6a4UE7bBouwMKgEVJ04DjlwRDdZpMW+aCStr41jVFuS+CTFRdl2sPB2w6y4D
tp8H62DdT47ZiW0YHFSs27hwGLZl48iWvKl4bUDyauQKW0VSOj609p7uZK4ceTZRHhsAnJBW
DSUpTF6v5V4ZVwmmea81aCDoAbSMe+zirVLtYey+cU661PI3bpvrM0C9yQiwCYlvQv8kPOiS
fGXLpXPX26wy8w1c4IAjnGdW7KAzYpG5ingY0KZ1SJ51DADSTf5KcipzVUoagMdMHkxB0y5Z
6ryPum7AN59vEBkxWA3rRUggDKxmuca6TDKvLTdUSuTT1G8fea5r+wx1G9j8uO52aYbtml88
NjHt6/CZc4b0mxwxnixqmjZqIBaJXAHWY5BaXeLMKXBMe52NGwdMCQI1PRWxxhovAS+XQRUe
hCxPdvEGrg/xU2sTBVYhwRrFu+AQhem4+2hElUYdFHm/WaIlUVJxk5UmdnsnDLBLBGlysAmO
uJBngM7V6vojf4k1EXKeQ2BaGPCixzRqWXjNXPMaBZXv+IFjWOqdEwHr1z+s3isesFng3wR9
3c7wqK2IT9qnRtnA4y1Qmpwsk1NXAV8aLkMW7A6oAoAfD7jnk4HgWd53vFCA009xCLmw57M0
Kk/xiwSNoWQ1au0vgmJYGoEMvXsm7fB2DZpJWqg7nB5/457lLpjucr9a7VMs9nqHADmXKBOO
MWvGBdjYQcccKYY+NeVEMcd236TtCJx4oY1G8kdaiBy5hnnPiTw7xaWHPV9qA4OPkH0iVnle
vwh38ouTF/618sNAcNBoA3Yua86r8q6Zk4HdXUeZASJ3NXZ3Z0+80iE7WYKqawP+p0AAgQK5
Hf16N7IpC5VANLbfa327pNTbm9L5Bn9gVt/7AqcXcEB7n7W0WZg7OCxCoMvhD1TD9TDOur0W
znAEIgCV8/XK1lzp2w7UYEPLsyotVP9jrEKWqccSEznmqWeIvaewWJshC8QzWCaBJDQe3mZP
EM4f4LaAJI4D2yiuQ4SAOB782+nIHZbdUIE6HoEjDZyqJ+AISd1+x6amLgbQiyZnElcD0vIP
7Y0XLnknC6rH1832glgm74vDQZ4hMHhL/NNcClE0/mliNqArKK2xiAM31R8cB9QDLHEMr5IS
oRaAyQeqt0u8ofuAVzjURuplaFxivNSoetNvgrTdJkrsR9bp2FDcfXE1ZfB5Dh6BQ1Ds5H3L
GYWZn4eTYjYgLPk6mu5q79jGypt4Beo1hHYgMloRKQfaFjr+LGP8UHUxiS7u9yBZSbtEWdAi
6bxljVjxd1BE6hLHdIg42F2VLmcSETF3ztu6FKUyieQpl8fkE79oAflZ2ZRtp9jFxLUQXKr3
dij9/k2QcKhkflB++FnKIThzKzPaHW5pwBPiYUaxbqCkWCBH+yP3sdcGErfDB8ZTOe7+TRmg
A3e6oPmIgQzZzCurDa5gYia/I8R+JNr+4wcyizdtWO4rVoNr3jq02bCZNiQtzJFmkVDo9Kd1
Feg5kT0nqvxIhWo9Gv27P6qoPg/aavjmGw1vaOVEXJpLO1zfCzSw2FbaKgxuJFEde38XlysW
6GjILhroZEZqu5aRi62li3ln3ylO2BVqAO4Yk8V40GZ9WL1OXcom66hYSQgM9OiUBs/0OqDK
C++CI6bLZVeAzBoWsTMhSA+ORRCYGC+ww8JsPX1+WiDyAi1CxhasoqPAGrH6jBNlOmTYCIq3
FpMA9LsxTueqKW4xa4uIF803r9EiAIsKMPdbxAsVZthGVCNuy/if9YxXmwGkp1rdIHT8ooTa
evkbXMLMzzxxgU8sgMxbv1Cesh3gfreejmz0B5Jp0y0++WvpgwZpoPLFEID3/qVYR4nzhxyC
fVZYFOMtwDwfwT6Ndd4/VAG1Mf6ui8BJVGadbY+XoNVx+/2Cde7YpkRsA9e1BbZtYzd1DuMk
ix6OyJk5h8Fa4jFG9FypeCF8XftQqOekKouOymmtvagShNafoxEL0hZDg/4LXObJ1ATprUt3
vS2panmhIgH67RiP8upGWb3mHL9iF5/tZspIWU52lPiQgd7F+QGAPRBXNT+Ki8N4IkLu/YO4
wIPHqoj3pXO3hhOZWHXbYZ52cuga1j7KiWJYf8PXqRDf7ZE8u6sRh6+ycsh0tp+LNkIrLyLf
Z/3lgrXYphTaBnYBzOilvnL4lUTN98OLr2dUEyRJfirXF5mG28VY036+mrifXV02+QznyxU7
8jq7t110jlTRrUK4oAkf1s1TpKsQgdmuiwhNGyn1CRCoqi62DjCoA8I2R8Q4/UM/inGnNoFq
7gP2j4ZookxoxBR7KjhyPh4WAlM/b+FcpiHHJsbPO83Cw/sNs17H+xP7Pdh3sNuZDwDv1gWc
QiwbiRCWK5KrSPH3PBK0ekOXKiBkUhV6UPUpYHZIHDfaZWypDI5cFK4buXxRDIh2qobGVaSG
TXhWndaRUrpQv8bKojgH+JeQGvi6OCpLe0eISTsgWfq4kupkdBBjxSAbKXuAzl0XgXSbvlPk
6Urkphct/wdFDZol89bYyKUJksENMH1NMqXXiRZQscGmvB26BukEufIkLnCkPZZ0F6i73L5/
1k5Eg+mnESm/JH2mApnIjhjGXNDazmkBDWePm7X5yC44pslHru5vBqA08MmIc2m/1Nq9LV3K
WzRiWmrMZ0fZxxgKHN3/F/0LICl4xt3J92qhvGpbeaY9GbdCwHfSvoNXhO0WL103ajvYlp7G
Kr0uvnR9NLvKxuNc11Dkwrln2MSbUVWfbN49HAG8qC0tUxwkNxn9fjYjywrUUCE56OBTTaz3
nnI3X8Bn6SBhnTTq1uywcpNiR35nr/qH+t2lc13dvFW6uugQWTUx/h/BII3YN5wsByEsCosk
OYsHXNTQsirueJng+7g3IacCIrRcI/ns6k8ThVloMg+47nvMiosoXJiNmbxvfSVEXOW2rBqI
pqGy0ySwwLYDGNmLByG0e4CWfErrPqcWXQ7GI1xzX9cVBioR0h3jMp/ih4oLH2pbaECFImxU
6igRkAwo4TysNuJmowr4neAqpIufrgzhSezjz28cDGvimToVViewDhj+aZ/ceYE0JxtfyMip
CeTGhJoH57Uuk5x93T0X4DrmHijMBGk+CWgpaaGiM+QxAdMGkRVARiS8Vgy+F1oLOJVYrs2H
KC+J+1Y9sWCSzivQ5XSZLSDfko9gydwRzSfYQLFLLgtXygQL8+8LOnxIPpKIKjBcyj8GVVV8
wGflItK42b/PSw0Yoj5QexhNo0iDb9DHBjyI+ZHAB/9bjSS3VKSP753CUswFIDscqyIJ19qv
5aaOcdN3eh/slLEXUvauOZJ7kdOeiduYvXFyq5+XO/Ghz6MFe3LDyAeLmEA1owBjvyd8RzeS
uai+82QFMuuj6DTNVGPOzJqQ6nk209VV1sh53seCtlK5sgG3ZTBJ9BnOPLINYI/cc87BBKdj
JW0CfQ0q0yUCkJu3WsXLDOqvHPhkIxSBGFFyQPGhLXwSNKjXfI3uUU66w2aOumeB1oDVjCXG
aVRlneeYbuUyaDo9Wy4LqC4b6ffLV1kk7JtExDVGE6+I2EoqgwHjKvcvuGoUrhGUtkur5/aK
qDrQVstRhnwDXLCNQx9D+f0GxbT8zvofaBDFrCqAC4gHOpTuDp2eTg2jXanjAcylizhY0kFd
CGKfhYZ0nztlA6r3YF2LrUtMz6gKoaWDbQJCiV6hkStDF9XAOD8WCdVtTclKB1pAOdGUjTev
WHRAaw9isVjQ2NUBX3wnl+ZM/6Ind84zt9pId//ONsTK1jcpCUJPFNyAtIhpMSbY1tg0fULg
kekboSODjRpM/SAQE5cr5cfJqJoE6Zk0jvVi2pPaweSZzGTFwtwIiB7Osj7n8HXP9U2qVRdt
cZm9KHNMxYmX39XOwEedj+CDEIPmG/BUMWFr/+KV+QeHfsEDiwzxq7IuHmKPGUyWV1GxTzow
npAA6jCMiJETBG019B24b4j7lcLEaceZUdLisuObwOUi9IA+O9Y3yi1lo5N3m1HfrZvbokfb
2LajMjKvxbkbd0LHivR7z5dZoAYeA2WfG5jmXL6PKek/cWaWzwpBrlDcHo585kjbNniJWdO0
KQxpqf7GX90pZuuf+Z6eEf3MXPxwADZcYRRwO/bDYukF2khkxHQi24BfzCzDPHIj9Ww/mqd0
J68Qeb//UhvCmgh9d+7lcAlWGiieSLfxba8r77so9/PM1do7kBwxy6zA01o22oijMIFIwIFC
1BDDEOWk6Lky/rdBngvs96zMwcuAtQ548evHtC8kAqEfqJiurQYtInpaDDd2SofVZOP89lnX
dk2fqDIWZZbGwTFO19i6OlnF0fgLddCMd2xDn2KGS/W7sah6Af3C+mC1PQ05iqXryiDZrlUA
U1ixYx+xycbnyKRP7kIshqlAlHmB5CfpccpGAimGnxVzhoXcPNVud/8mR7phPBjexRk2o/zg
TOJOmO390xS5U/5NvEYQQbIEqNFlJ1yvTfuCVhvGBuy150w4P4q2tS/rYdBLdFHr7AWZS0fJ
PbKO6gOFnm3uURLfVcJ7s4e0dHxpVxrF/x/q1j8ID/QauNWr22EJw8A/1DfaaI6tunzewsVo
tef8ZZ5ZMW2Zu9xKuPG8i/h8QlSrshrp4gaVN9LyKA2Gi4pumD1bHxjhHVhmhRvXPsZ6DKst
m6bS5gx7YtXtH20DWTUp3kDuoW3Sbp7V2/RfHKeAU2C2kGWobZIY75I9pQsEG4yAQ+D8ljXq
4+i1m0z/jGKrwfArlNwbeFD1MhVyJZe/Wsh/XVu8oP6hPO6ztkm8aTopMZoPJ9JfV/By4YZh
taLjdrvme/mBiANTolIkW7Pfk3agAHeOczKiEYbJIyo9E+ysv45WcQo11aGiYe24z7aXBRuL
0EZ2A7QqwYZ9eDNDHWpzM2o+HWOIXDUFsVvWm6yHoq8c1MXO8oJqqkFD52bENYMGwUQ/IXr5
6Q3WBY4uXhGFuiuyirSQSJ7YWdWo8jrZ3REQhJd3jv2e6gZqkugHS+nB7ZsFbrPB8zrrj75L
BpaxwQuAFg1238FSllo6XbflKBHou+61ibA05/5UINgV+EagvfDgSC1AA0Y+bM6CexRFyDH1
DJNzkP4QV677dmOn9HfqZN3YCK2hqaG83zhb6fE8qgHgeEkfyGgTf/XEmcQmwR0wfBbkWxlK
ktNtVHt/quvMSIznzBn5OjnylgRMrNMXo13ehqnXgrikaNZ795Gjgz93HYMcfB/toZTZi4FT
8wIN86i0PaSPUoW0dg33wrujvRolg7toMhsb/5Ka/88z87+e1NKl+vXpqwG2ab4cJUb0iez0
pT0GfeQPJCrikMfBxnYWMuHr1e2VWdGmPjtUKjFbmvacUXY6iexltHidNlGieiCxW3AH6uVO
rTSrTqei8WgMPHLrpa5OkP9Vq7iUGBMg4Kd4lSz12YOrJYDqPWHzxniHytus+dIicoFzIr9J
BjteBtDRPKzB4D0H3xR/da9YSzWgTwCSZYyDd7GSs0TQAN+BtKeM7NLvifvMcMA/gtrVNBNI
EbK+dUL0e/CPYy21RjheOc68ah8JmE9RxM1YzNxRT1EEPNYqS/0DKV7GyVvEJTDjovwAcSRy
m+UQMDy33ec4hH/dvhqFBLXs/cpc7gT6OP1s4XzLUKz2Ox99y2CVRSmWUIGuP9Pb21JxW/Q7
P9ADZZ1F6cnIS0PoPIv8dq0HMUSql4n6HQmqtartpa6c2mMcbkdss+gXGcD20S9Z9LMPjkFO
2HLewRESw2knlCG9aGnIZFOmW0xxpX7yhCqfilwEVcy/4xWrWGMBEvtD05+zeYIeXJS6eSbV
Y4ojtR0G0q2TxKmF4juEQlMJuTxYDclcum6YnZhvVR0QtR85xbTLvRGgScSvQ6p5SHL6K5eH
aMpsfFYRcYGhmQXGjlteWr2WFnnZcPgyuy0pbPW60cxGY3LkKK/Iwoz6X+qJiAJucMfcjKx2
4WHT0XfmAGVYOAP60kAXjU/docs9+N9Oyb8tcAVZc39zml928vJxRd0o07qNxEUc8m9Zm8M9
0bYzcVNH0vKtOoF7Bz2AeCmZqyXOrWPPTGwBXSWu3dC5RppeN3s2sfChOndsHQiYWUA3b6G2
Xh91q5+f5ADagmDwqq/0+IIZ7sOkRKD6ScKxtl46O02PzyNX6Cp1FtQu6x9+pahV0HcS1CxN
f84xss4adfCAvxrobFX4Qqx6OaQYWy/o+0110HudlenchWmKTvuEHxEv1GCyzM5wpIdoMarC
6ptu4IHMR40mwcUmTlqubGANqHppE1IdD1dijaSFyNqC2pVDR/ouSt5kCwAnQpSn2PyXOUaG
uFZkgewW1T6IWMU0nYd+H068Bx8H2dHjZXFitkFjWrMO8ZKFIXb34d9VwPLOrbzKMfc560SY
N8RU+1JD4WUZl1sJ6Rl6ftssvluQgUCw6hFBTrWjHLaVpim55NF0qzs3G27UqgMqvlTtbTl8
MZ1a0pMLmN/tLTwL83i4z7J074IkocLOfrtb/SsfY17JJUEb7Yu2Bcqv9qtmewo9uMgO2YkN
sB+9vf6jHzG1Gol+F/qqmW2a69liq4AGRP+u51VR+YI9qXH5mULBem8zlSr4aM5YqURDdxDU
p+y35A9mabIfE6cFlzHr/Y6oZ3k5H9SkjkFD5QqF3bCdiUgyKQYiJExAW2xLTsOwjxnq8tKV
oz+VWE9oexmQM92jMoRsloDeXVMQdYfWi9KA0DC5ESiobS+D7RWrXrGYdTMpOp2fmUdDOkbz
abmua7S2erL+sDA8hdByFsxQ42vrTdEjkReiZsWKxXzfcG3LPRyJS61ruhHgxubZxLUig5lh
DwgC27ixaTBv38APsbmLFRtpiMzPlwuuQKqTZqc40tbjVQc1RMZUO9SmOGl3aPEic6uNILqG
aj9g+vlWfcLX+U7SxNKWGsH4YVtNyVo51ZH7aTuQKo6ReRCtdoadIMQA4fUqwqEHOJCeXzyO
YaPQJN8dLK4cbuR4rdqz3ySTWroWZZ8DV2cN/9bpxiVNHlnqzM75HNxtfXoAsSbR993H+mkf
0CxJ3rpQZTiVdgArm3llVXrRuUMX6A8UMS0wgBgKffcf0e1/fc6b/p1b0bq/EFw/gbP8fKvX
1p9eEgEUkBmsV45mFoJ95d0OdSjaWP3poAXcsPQfanrWHTkOXkmUp+53L5FxrxQlqEbHoF/y
oMZZT3y+/EXfx0JqLWHtVHUXsazn6apLOdS8Mo+uxk7GlWSCvPR7mkCnVUynR1IzX7fOx2EL
Sqh5loEuM/4hP7xLULvOjl/8nrXDWRmsyGVBvN5uBh4t93B092wxNiSGOqZtpRaaADAv68cZ
1YxJNxPKow1W5tnqg7XzTL92VpPc32oXrm1P8VexExJvBHicGSH+oOuvIjvzSXwAQUKYWmsz
7MH+YdtVdUw/8CikeupU70eAUG6qdb57U1wHXgBN7RJFGHXMCRAzDH977hTmG28NO4EeL/Vh
ULlO5BjEFQJ0pIgBM1Qi8Jom+1YlQLSreELibClMsDX/0nwXxqfWziZ5Gbv/wRCuLs7FUGeZ
VKkgLjgUo2K/th5IEOLAi/OqP7/N4nNy6c2lfLajoj8rkiIxjPkNM2d5Hpc2sn3O58QI4mPC
LaFMcQkegX93lvxH1Lwkf+k6tFC1suCXlI5jkKkWZje8vudQdAttCccEXvtR7FwK1y24vSpv
rbWHmP1rNc2K9DklsUL05rNpRyQRb/kmiXKH8t1xQlnHNnK34Pa6/CXZHreh9pJQR3xxO9V9
NGcSNJ1D7HBxz82kGh4CncWAlPt0oJpUMBso1tPs1qnsNogoZHXOMdBdIyuyufuo3L4ZXXOT
g1/t00tL4nmTilZB7bZP+CO3sAb6KmQAcqUoWxN/CI+3dgA6E4wVm0IGvFiZu/t1zN2M6mNQ
2GNMjUfY9sGRzQsLz3Yt00IVXfBouikrk/Eu5wOkdkZ8e6sxMFS1o0U83/jMSGwZi6wWy/aE
RB23w4w4Hq0WypDIyAn8ycUvAq/vdGorpX1HI6X65jW94Ypl9o8rRjiGp9onRL4dKH2QlxQP
S+naCb9UysPbGm4Z0Oww4kir1jG+2utki8x5U+2b7ZDlSrwMVNy8T8UZRHb16qQnzYu6FHXO
YPCXgOzJQROK4WgXRrTWePR0faCHwZJJx7xXF171on0m6awDQMxH4b7XM/45HuI/ouI/PmdL
2UNIkmF53/upUL4Ovh+1bUFPl7I/4nvLJdOvHS6I2yfu8El87Tq86CaUlCZZZJlNkq7+cUFv
r7se8q/eNZ9T1dYLxi5Nzt75Q23/MIZRk7DssFFJxhVQ+0hP7t4p5OjB3/2b3qvE9jEZt6pd
sxF4H+FJ0DdA9de6TOetFEbmrP9RNjhpdpfkswmfv4LVVgF04ykO86vdBkDDIiCZDSrWfAMQ
ntVxHhz8gQ/4B3bDr1ChYjU9yrpT3E50r4uyu7k1XfwDdv7xJtSZUEbA7EP+gXHIwOZXyEC8
tZOQnRjeZDoeUUTKgPbSfzo1lDirft7a6fkZBi4R2hOokTLy4AxV5PJ456BdrlRp5Ksw7eUK
ja2OiTOMTJxgaq7e3Kqm5DEovRm2tUq/j8638f+reK/VL1ywx7Bm5YcHhdh4rsd5VcSo3sFL
JTqd94I+El48tuF1+IrBRsG/LpifPHqfT/+s/sfYplf147JSs+WfPSoW9cqjcLvNBkvzqoqf
vAz5zL51YAx2CoPygM4b37OTHWIMdbX8WUL+QaL/tw+csn0lAapl+R0eateyL0N9ct4fpnbP
LgrzahvRrXG66EYWtZZjEErkeXW1MJLKO2m76XUMks+DBjEza/jVN/RvFJWMj5CTV1fDnjXg
575Emx+D/t6KGiZs9UiqX70q7IvnGFTlPbQMENFCLQ8nE5TMXlh0b/l+rCQMuClXELd9cym7
r4I8hzp9ntcfgyz7R37WV+m0dSS+1rKvqC8C4p1v5rx9auMajI7c+B67D0ODu+eyA2fB5g4T
A2ZHjAW779oFHxYZ+qseyJ/NJUy11ip+4szCah0pxVvnNyqHHdrt19WaEM9bu4o8ON2FUoo3
qRWtYu9Rq9s6uh9ko6axdfTTKUcb3yapHlgPaI+WPqafrY6fOaOSuHoqzchvL0yfTDp/p7tz
4oxKs/8PMk6CPhd48+z8rcO3qmrUvi0xwfcqZS/NeEDv+v7uMcjXkXwMuqLlazqW9rbrqCVs
QVzNxYZ4aPgTZnPUrhiRXV098OG1BGmgQh7dfFZ1KUhkNDXIM4bRIzNAa7clXH4TEODyaUVa
KaULuLuTHlOT4wJhzxYd/G6c6SB0+Pmkj6YaCO5kUsXFE+u1/j+R/J9H5JZlhz3zaPSO7Qwh
eAg9wyU0/GqpJ2uriv03pLtN4kGGsPcWpHjzGHTwC5kQVjl/8NZRJ+ooliqFHfpuXXagQiG1
/w4sxKiqG82MFEUMHgmtqqfd/ONW74bll9r3k4G/kyZSvAktrBJ6BO1N1BIeFaAeV4/Z1b0Q
Kx8k6K5CsBu46024+Bx35PGMeAx6PeSi7N4ms9dHVk+63RgcR9UU9Y2ay+lJ/ttBPuZQ1Ccd
uUx9ii7wph28lTizxO4k8TrrCf1IvukYFP8Gh3jM8FbLeYqZD649fILAAa1qq4vSvYBs0mNQ
B/bo+zPcu7TClXFABnVhjkHv3nQfg8aQveiJ8WJgBftj5bsqZGD+qPMv1BGCfvhE4sqeOsOI
YZwD/C7/9cdf6HHf8B8wHSjw5Sb+TiHt/q5nh+6gC5NqGza89gyMjiJv94vqBOoEH4PsH3XO
vwESaVPfuGTNNTO3qv8mE57q8RyDbr2M7QoSmCN8nDRbqA27krOe/bvOPkEn9WxSW0D7z547
QK7PK7k/VJwPoT5mxNrMas+dUkX1VwasEoW9OPwNu+UVS3nrrWfygD3x9fZy8Wc/44Sj6C+3
PhLC2m4d3YtaAAKC/3ku8M8jcfJ0gsAJAicInCBwgsAJAicInCBwgsAJAicInCBwgsAJAicI
/OcRgBz3Hx8beJ4C/dvs3B9dHoE+j//NZudylHNnQP51di4U2OSPmb7/0pLyzFm206zswADd
H7N1/f7n9NxToFNnzvOc4zjLyvp/z9Y9fYbnJ96fYReUNA3cfUOflfKJ34Qr//Gnh/fzv4vf
l3z6fFFQQl5B8VdPL58nrz986ejsErhsiLUJe/EqM+vN23r+X67c+u22sUn29ylJLZQRztY+
/PFLKW0dzF8N4w8eTgJ/+cK/TdL9H+T5scrzLzv9nzT79/m6r+T+85Q8+eYJAicInCBwgsAJ
AicInCBwgsAJAicInCBwgsAJAicInCBwgsAJAicInCBwgsAJAicInCBwgsAJAicInCBwgsAJ
AicInCBwgsAJAicInCDw3w4B0bR9/08LFUmRdi34a2212YViomw6iwN9pNXqlremh543h9Vd
NGmjE67nigmTapqDxtTAowIiejBf2AUlXC4VOdoR+Gf/Rbz/ge1YfQ5jiJ3vRev2dRPr1fY/
y+1wZVuWg6HowUru1/7vp23UZ69/rh2NSztYQXh7ejYXQIMfKlkvuwyd2cdqzlW0K17dqrmb
BBVCf1+2+L2m+/6u7HpJszzpxQz8Pv27k7HjvqHYzo312a896i3Kf/WvD87enKmtiGQXetZ1
93mV1RGcuHfOsra4r7liW+GNsDHaME6nGGlOe+RYa/at9C7JM1ZsN4eMEn82MxlDPwY1ehPn
Qja7uxWfBQQOOVCxxR9LXb/EcKfPYqxQ9rtQmRmLPcuyvGCh89zPmcaydwoOnp4vxdfeKfPE
MQZDAhX3KtYeOtVGD6Ukb3+3588COiLFNi3yNJ9LP5JVbEQtBvzCs43NADZhBjXKD6Q4uCtK
bQJDZZCLN8HraLMa42q90IY7hy2dtTmQXqzZiEnWlJJvw5ktr0Ok+iB4nlJAuD6aN57zU05/
fR1xK8MPbQ61VDf8wiVBLyGGizLENunmsla1hp/bxdElTmzqA+BxrLk+ODjnibAGyTb1ypEa
tLJyYEV6U01i9MVSuzDhEjfG0nnnF9GfPzGYyLah20dyUHLl0IoH8rdwofag1HyTg/sB5EXf
z/a7XGdc+rc8izOAz0fdGpG/haZkBqWhoeoghPxm3fhU4FOw74V9lYaIIxlo8t74UsSu9Y2B
qX2VzcQjSc25okLZbuKrNQa5e2lZ1f2ILraB7ZX4DVgZTsN2upAlDl//eMeKM7DotflmkMJK
xDHIJj5AqtDLd2cEa4ubY7oegEQT0o5Bn5mHH4FyVvCu/+iB7DFo8L9gXS13McUlGP1qL6tv
BNhBH5iZVWicoi4znSVJejvcRd8XhoyiLIJqgZUv93L6hi+g92V+rOhlASuTWCLO3Yw0IQZd
UBl/ZLqLBDl1LDm9ttvJwM8vEr4k7SIhy7e35PG8OyFbnT3bT0rWArmGDZYcldZ3wMs5BaOn
Z6d2rlIn+9oaSJ+5nREufnB1qU8F89BGnctHSoiXm2Vjjw9IpxVb8fxyszt1eIdFpzpCt1tC
MK14TvlICdoc0L92DNorvLDKhoiSy9lZ8acB54OA+bwsTiu2YyMMgJfiPgpXBFP+srhNBLpP
EwZCZ1FmR2Yzwep/DekScRzAyidgH3bS62uBiImX+EsuaeqMjC0UcFLt6O/88kQrzHw3xoL6
hm0rdGsHG+eEdRoPfVEN6aPmr8Sm3fc+efjjy2JaRozVLb7tH7Z9ZZewo/j+0huM9nURUkeX
rUkt22huDSxUfxWhv5gwznOa31omjJWK7eUuvG0aJvzScEBGpjgvkMKhmss5ZGvxbv+dfktk
ez9QsMx2BfGsW/TZnTUCNcHV7tGiaAd4e9JbZir8RlnUZDsr4hj0fv5SbG0lLcQj8fBXZbmv
jInd0MFno/uXrcu2jceEY9MDdpFNjDFPnveTtfQFHtSwFoRR2k66qljzW+IylNbp1LdxWJkh
ihEe98jynPJ/Pv4mSGHu8w8+VpnuXGFMaWst4ggaHs2hATzsgSeuuc3q9gz2SbD14VpnbTr7
aGwrUXa3upqdViM8ypxZNc9hKyr1Es5WFyxHJAx+q8L291J3q6yo0diBfOHYOHG3Y5DU0fUa
n8ORY5ByXh+FYcSl0zj2zSNTit+8rnq0bWLNnsK4jRy4YVohwhjOLHpLvgy9/99OYgAb4rY8
iBb4KPvwoVWZbVuyLTVBFnOhUxsmMmNr95WHZyH8jn/EAr2llt3V4tuOJ5/7XatSC0OPWImb
KZce5u70kziQ9oUpL8a6R9T0+B2Yup0Yo9uq1BfLDl6yLuUoNf2OrXb9kab6LubcXlwKXvKm
eKNe5fWhnZYOPejNyLKAbiv+UPRrx5yyxu145n8ndNhjfa8Pxm3LGuoGrCNCaQ+Xg0pz6tuD
xzthmWrreNlhkepdNkWye0tYwGXdRYs/+wV40OkeZWy/FI5aeoCJQzOdr/AGcOubVdfXAga/
oJP2+TUbZzzzmnU4dUdmVJ92+xx9KeyjbvPdhhUY5pb9YqamO726/1vF2O4hR2zCi20Kxpcd
7EnGinehAvwGLQm/ppVQjoRN2AWTusOfW9gnFdc7Y2+U5dm5zKIIRaW3YWmG+a5XkgN1J3Cu
1eiyZJiXudH2MYgjOMQNq9LjUcuzm8Dt9xboKOSdPQ80pPvYpNQ68jGVNVNqgnCmbHN3U83r
T7N9LJlNmdTL/WCQuXojYdhTomdDp9qWTigoMVH6fW+G5h9tUbRN/MNxpDb8G2i3yLuly5HY
qmzXmEmgDm9itt6NCQMthBGLFuiMisCO6wEjitZUT4bpG2Gor3mwggVzFR4+KCHas7r9nhnU
1gz+ZLGIbfsFg47qE5bJJP0hpdtlixveeBSUEdgb0OFp7jmlQOQsCJJ8kbLjeRn4h01GXNbE
A41lvzQeOmlTETU1hxrj8MqPnm8TeOeCxstWqMeg+4M7nYMHl4242LaN0gNceuUNGweAsa7Z
saVvfIiEi3ZL4TPUrsV0p46BGlVr4ttvt8jBPbcg03F/D607YdpSXZScthdJXRPz5c/UZ5Y0
ECWts/cOG0R7qn6b6NHCzmxcROqJHBL5XMALsZNdJExRY9+QxVer5Np3D5yeoau1ttjLPi04
J4lKtG7ukP4uv8ZOWePuSjAparAatKBZAe0Ueh45eXUyewfAjKO3cX/jo9QLy90bdCMo9Lkh
SpfvVqBzE/CVSv+p7kK/xSHOnuVedfLXrpU8ymjhwW0k1VJud5YqMj+Gmdtz/vTWcGstdKNv
3oGuvXBwaeeqduLuwrbsi8GD1DzSOy6s0JtRVf59v+HQLNxRRbnbbFnPULyHj8qv688Axt6x
9ZbYKz8gtewQH7QVoLzu7zvFXLprjS6wIFWUiO1f33g401z7fEhYuWxjoBE71hAfdMHLfOZ9
EXJ1/Am0vSBtR+4TIy5qqAtNClopRKRhDY7CuL3joizau7GbdB4laxeSVSzqXmHQ/OcQj/Lh
n8oZWFftVc8/BzYPLGyxW4w/uH6nacle6R7ssPAY6DkGmXd6SO97gqZkNtRGvAmNyo877Pf0
WBjWLhuQxbJvoxakBE+JcPR3htnCMcgxBNgLvJX02lPRFhGbBj8aBG3RfgNm8GHaOFHF72tX
x7b75uyi9SzX/FOpHiSzkbYoqaXZ28q6Lk/xCukj0TO8ptTFnepaR2JZcAYAyM8r2ekjUZM+
SxV7I2zyoq7lyH3ET3786JYdas3i3u9u8/s+b0Qf1kQOVaJaykn1ATUJEmykLQf2DpS2rKnE
dKr2ROC+4F4gobgJ8WHDaNqpjOZ6dE338JyhPnHrfPDRHznSohv7UbWTlqp7p0Vf5jXTDpET
RTu9+kdhp7ww0zZSVcyRa+hvaVhggTtIhN//j6ypMgIvZc/ZnH3lzzrEhtfDaQUSQAqdovnS
GOtPUcBLQv6onKlSqBh2aVFBnU0JeMd7+iwJ0bZuXVLQsSMTPoxCjaAd1iddVarTPHevA7/f
RupfXZ83/1hkZ0lZ+QPQR8Qr4Dn0sjKEVXu174oGsPP4qRoSsnMIg1c5Qo3F4x3mr3+1RAa9
KAT0Ps6iT/eAN1KmMtX2IaaU/iFl0vanpZy37JefzY43UpDtE+1HXlCvjTdTf6kdyHXZ9Q8F
PF2v20L9HoeapH9Ond/yhb492FGbfGstAXwBarGv+sLwKJ77yrx1U5f/juozdaDFWbf6G0i7
iskaTHRPsPp/LBDehK8FmHjA1fcu1Yr+eANYaAwwXlNEunBP0YqB7jPzoJX0VxZx9JTHFc+W
XPTQuyt+6N+DUbNtn6t2thShWT9sEq+sqajAoZtdWX1D/seg9vBe7J3lO3ZtXwrMSDh3O4IS
t6WlpP9VksKXnrwtRS67w5WAhfmrXx9aOScVdS65cJK+3ENgvOKmPhcp9A693L90CCiygOIt
rixPafvbJTkoNmB2PCTAcR7ytc3KWdG3c8mpNPgSeL4oq1eq27/A1Swo1kX9XEaA09xsswjw
v6+Z25KnEP5qQvBtOE1LFj3rLn+CKs6fPBJ2C5CeozV7W0tUKL1AfV/YIT09D43au+6RZ93E
1L9isFH5kX38c3xA7VXDV8S9oAbr1cK0w1PczUbTuCOSO/bAKYegCVl7pWxyDMoZAjrDXJof
/aY5idVGYqWmlEIblLa8ESqEvtD5okzidd61msvuCqTs9s7Zw+fgteG5lJaug5yoQK2c+cKx
7q3iMVGR5UhhXsrRjcbrTFRnfz2FYR7ivity3s8OS/h1tddzcLPKNoFoPUAGN0xtKA/Kb2+I
wpLTiswbGRRfZI+e2KTT3EPdbrhr8pmooNtpr0aCgL5LAO6/SdfmzQQnbflYu26NAYg45KKa
d5NolPmPTwyO+sV2CzeUhgzW0nEfBmpSHlnkMB40IaWHuX2H1VeD1efkD5FPA0ilPpq0KS+t
iWHEIUdjW5Znz2qi6a2g3Hh3fwSvclhWbcZO3pfBmrLYihRXBq6LS6UmKvW7tuGY6xFfNzoP
TnaEqddpLlIya+VhM6Nq1yl93d7ccxobvR345AEkymelufZtdwmBSxgyQ+3ISTEn/Jy/sjb7
fVFQ/ekl8KrV3GrbYVF87Av8vHxl1nKBhtJB3LPAmX7mxNZMf+3eSLWt6qHvfWAnV3aHi0cb
3Oh6Xw+d3MdQhEIqaFJ63pOOEQEaEJ1j8iw0TnfMHuaKyi8nqa2ZxG2uSFwLfmHxfXE/NYk9
s1csdYsxv/LO73qlu61a9Uoppz9p3fcNtLkicEG6DLc3auOeXm94DMqzbKtg+pGnoFS8Z57t
qTaFW/q2Mn5IdOvq5hwxWAza/H4veZxGm1pH2Ej0Frn9wW1Z84v3z99snaiVu09KB1uQMdR8
i4ht2e0Q/LWZY1Cu5DBxsf2Ku8SlK+t7ilxkKh6p0BX+ufcPfT85xxTCMpOsbbQrmTJgzOoJ
pT8BNH/zhVC6djkDLSKL7nQeliwqi+Iu4SAT1cpLd7A7X2ITRFXxzg7uolO4TrEmt0rq+qto
nsnN4YKkwX2FcBfVwwffuXCi+TkKPap+w1JPK0QL7ft5Rhc97osG1Xyo6jZYM7/xZBuZcod+
IPiOu4i3wBd+Czuq+lQNVo0qcILcK0MezGC2QuPHvakT3eXEKDXeAcVDAk/aCydGm8aMe+Wk
S5QNgr+lMMEnyJq/QtZga3WBfdS10NYikPpaFRMku5pM6HsjanXDotWsUMvWg+bTLYpw8mvw
ZOrzqT8S5CL17P+VoBpoNGY8Q9s85CZPjuyT7dk0o3toCY4TCKHPRxJmJGyDyaeKrTUH9p9x
BWhpRaDZNpU3yjjTrsVoPiCwE7rlSnjHmaC3sP+13Utr2tGcqs+cjUk7S6YSwgrfPVCqxuyK
NkWkVBm3NzIXLAeTX27ttfBB4mkLT5pqtJudDWnX7MlFl/3aKigG0KX2G/bbn144VB2D1hzI
9fo35FLM4gDLsK0l8RgUlBn/QGBoci0tgUeh4tl49Q/jadniLsHbAhLfOJPzmrPlZX/9jOqT
7ULM2i0D6sYuOaiJOiSITGuIu+jEw/tm9YbjTIOVQ2OPe6Hv3sCU8JFC8RtbLX0o5WmwVJsC
sxM7EB/kDoONSEqC9/6PauWQ7hcvYp8QfW/AxYejL15JSXAZLryaGWWj2obR3RUXR5iyET1F
u3NCLMQ39EfHLQiVLpNlq+kX055d3Ejh81crnfEhy+5eY/LYJM+T2ByS5+J1En7afT7Lnt7W
6/oA8yJ/8eO6dNTq1l+99RWu6DJdDIo2VKLV2qvH1yDvNxS1uBo0E3jtvmAtz56Nu1O48AcX
K+Qq2s1h51J2tA5fizmOhaQ9nB3db/yo11hHGz4xT46gGrUpHDxEZNU+FckGv0dwlzUsJvte
2HF+8QoVRavNXkz0IWDkLbIZqcDY3J5i3PCptyH/JwFGKAsm+n3YMTX1eVQfUCarDdvSjFuo
MhyPC9ftLnQXcprvAMyazUA8TNTSAvJT08yXV1W/k7MkkqD8HZa8A2TCLwOB3bxLfiNj4/JQ
P+Xfvs8nv/eP7iutJywMlFZFbhfoWX566ojQqxD+ztSLiVPFWRSqbzpzG9aie80byaT3XPyK
5N7LSi9b+yb+ykqCLZgMJj/WPQxK1oxwQjzwR33f32PXH92rTSjbTI+1ST8Gja9dDw/9umjd
grlAz9hxrm8pWdAekuFw37oJTHWkbNaOlyY77oTWpbUlYRdwcAytMXIr8KyLD9t1fOHD3ciY
YJOCDuSb3qrsomIBOS52w8XQeqEP9HoXFucl000padPaZzybHxnh51sXTVsZLaX63Nx+f9p0
HcQq3jr8ddpgqVvwZf1+3cRaZeu63TPeix+gwpO+m872u4aDi2tkNkSet8esqookzBc52End
zRHSKMa6rtQIwKjDBhXzVIyhsNuKuN2U/aCZlhZetKf6qAnJMXynYqKLHK2+zMjTw+yKp1zS
IbnY9a3AJjSn1eibnMMbxyCTVf5oQXfrZK/WwOigQyKPVlCIn1mvSoJj2kJjd0XS16iq2iTr
3gWihzge7PnIW7rnWrSpiujNCqToi3X8paXO5TaDAcQ3f/rVIM2yJ+rMp5w7aUl8u5N/NFeg
CLY3hojv2dT1oH4lwchRFnim49o2NX/+4+xBVQT7z8TvvenR21cza84Cc7rWez095hFZ/RHN
Sfugrx+W4w+m7bT09Z+Weh0dZetXuxSOjmW+89wZFtgtruVR9JU6V3z0ZNhaFh/kcjn8WcNc
Tuumr0NM+89uNW0V692uBl3SZMTXLxGkQIAndXBEKdogpd1pjpNoylyQovgxyLUwGUzHeSl0
kyM2rG+Wv87pXsXrk49GLMWm3FUEJzp8rtFnXBiDwQUKPl7mlMUchaIPnFn6c5GfnQxE+coH
qR523RtILnngxFiOh6fR5v5ucYZBoyewPy2jKRPrclf2/V5Bnn2eq2jOlu+rIPi5q8pKHOkv
F4RfoPf82an+QFCB/3acHsxG/Ci80lM1oKx0sXh0UTzeU+DwqvLPJTyTSta5o4ee7gs824oZ
os4i15UvZiJVwxKk95zbKEecuezD4Z3Sz9qQRVw0FpgT6bCmIm+EGDCjW3dTWFZTWaEuIlq4
2vl3KsG2xJJJJWu24tasm41lfMpannJLlW3pQaCzw4Zi+wVrxOYCQNReD5QlZQ8o8QVRNfbl
du9P5+gXNTocVLnRL9aml3z4sCc1Gq3R5FZ+53OagvitZUFnNasRV97MSYPBkQzhdmTvoFJQ
Fq/L/GtV/yqrXyqDuyDLZdGxdl+doN2id7U0EBn//3Af7q8RpMv1txH8XgccqwNHXIj2Y5C6
Y9K+G5ei9MNHQ32JbQNmCiiCemxdqTUhON4taej8WE0O76WE0z7GFmgSbU4gQfXQu4Idgn+F
xHpIpyTsuow7Ny+sdxvTO2fshlcBNXHtSXPaHMP6eiqM+HYg8dYhxY1LVeq5voHHhA1TFn8W
oHXfByeFoxkxYUlftP7dTa5VQgKDiiIs8U2Z7g83sYMJb7fFd/klGYEcmck5+9CJ7lxiQGpu
SGBZgMka3HNKCR4w+n3ZErsy1aR0kP5i6IV15KqFanfxPuDZHjItGVwsvK2EQGUxpSo+tCn1
DdJZ7LppvWpXiSuvF9mUfTOLpDGt3U7Bq7+P+q+hGvSQNurfqIfx7rtBvP4BhVLf1P6Y+CVp
U815SYjkBI3HJZN+OxK1jNyJpVV/iUbmZHo58e8HObfcp7l43aRUtaXbTQTZUx4eiaIgcS1z
7hVXIjfYYZXO85tqPv0VrowHXZyuRnPERoqBOo8f7b1HTtcGJqYqGLCntetwvSrS6wYo/6wg
t4+15h8puVqHqWLuFUGXdj82RqaolHF77Ae89k6NYG7ubIQLdavc9cwDHFuSTd9KZUfsG4YE
PvxwHGFAtGWv6tnsIV9KqDf9+7KeeFHpS+6owjThtbmEIF670Mpuygd/Sn23HIWMiCwLfgDF
KgcuXP1w9ehDX6BdY5RaR7ZFG3WwL5oPswUqy9m82Zl3QGNPajXDzTq7nBVH1qkRpBB3PnCk
q0t5eAoRbx2DFn1LK/OITBdf4jvuwdS59d2S+WNQYHlx7UomUW3BxADraus6QHrP7aJuaOUP
yxQfFVnLAe4K992KbZPvXCh2MkGtPCHw4RFscsbwMO5o8PsEaQ02T3rPmYNeBLdLXtB6MPvo
4GikUOcpz+iBiFd4Km1Rs807keHp6AYc1Y6KN7a0oRkN5VipAiLsootvr5/1l/yWoCPUT40+
t7a2HL9WbIUmjnk3DCvME6NSqQ6mfAElxApZ08i9pYBPreObLY1kxq0F4fdDZU6bmP4RHkuD
JUMlo+3tT4kOaS5KMJ/EnRIgCBCNzLeZsnmgFeTt86m9f9G0+dAAGjG+fcG5dfdARBENRFUU
wK8cRKwrlLvysj29RUbf6u5Own9NzkaQeC3rHvQNG/lfqtXVG5GbmtTdS/DpyYOLmhPFZjdc
sg5eOFVXs9LaJHv9GYf40JSn24u3ILKfZ1VfVv+aSKbBDlSypfaR440lyE3vOuUCxaQRc/no
jtg362e+WAx2Aq5sIlVOFss09C2Hi6jil6ptEim3h/dkveX9c4TulfpILTrGe15cHqSinzhO
y9OKdLdD/P9L9RZuKx0dJBTRWkXdWjIp0Rqq8Jg20LtgyDPimES6rIWiiHWMPFD54Mbx2Cpy
8EDmGLSq6GG+Q+fQb4oO0I6qUWyxsnPMZD4vXL14tUK3Da7bqxV2y+9Fq6+S2tbyIF4yP9bO
Kku2vEjUnhFz9/XGvlGDUbCDZbKkbaV90SdK4xTWOnolO1DlvpBli52OJU79W0pW0nD36s3W
HX6C+B7fgssDdBM99EXCgH3WplG3dmJRla6eokP8nYSzfrDPNeyMSoWEM1sKrz5+aA4UrNAR
Se+9eS07MVu62qdw+wZ2QFxN9RUG+6KdSz2xmoiPDIRMSH5qKNVuLfB95Ghi8szCN+JrEbS8
BDlNZwmq+y3htiXTydEzMvxvq6hsxb9Guz44qvrnFUbZt0aSPLlyiVnYjlNz/6W0ASQI99fE
bNVuGA80Pzyyazv4e4d9SnL73He5qzl0Y31nioGopRHkdJd/5nQWqtZYltKqfg52o2PNuMil
9aw0kWnLdMMFlKkFZsx1YazsYOaXpgxnNyQpOkb7z+w+J7HxpnSzP0sVKu0virswXBjJgOFc
HcuukmxyG1fshuJxZjQsl+6tZkcKh7cLwgzXpg8NDU4i4Wja5Wz8r3oor/YNMUpUSOT2TFJi
ZJoiOjO5hnjgYbcE4e+pHHErbJDXHxoLXmwnI3Xg3pyPTEi29qvVoU8fbLa0kJNikKYyg5Su
FGqjEzFALosRfrFHZXjV5QCzCgnDo87aTQUJprx4Mdi/IjnqZlNW2blu6CN5fSmO33QzO00a
aYs46Gdnzdt8PMuOTIoxH7yhl7SuL/tUXpfwhGoid9CeF7j+0JI8XXPLvCGzSJ6q6vr7isOW
ZL4DZSk8pig3R20/jpmx5P7FotanVr5K5MbZYc8lbQqP2EFRdBDK963R6JcR4cAWJmJywtKs
gGw3RIuy0dz3vbtgnd95YcrhoM3W0PrF+t2AQy86FakhPc2fe/Eo63Bz3Pen0rMu/pMmzYWj
BNubLqh+9lqhbEW1CqMG43LeZ7roLT3872XITVM5znCdecX2mjyeOUZolgPgxNgc/vIU0Gj5
ZQHGMtfWlo6BKW4eCY+37iWUxuQl7rWahbY5pF1Qjq/GfyyurxGyGdhdepS/vxnkbPIB1c+G
y/FSHeF3IEYNfZ7r61xoRI5SgyUWi75xOQn9ncbjEVWinJqcG7mzd/3RSCds41rqPIMJufG9
UnzlrzbYqmus+RfZImN3t1X3ieBKWR82TVxmgoxR56Fnvf4VC8Dn/Bs6E9kuHC7ZUYlYC8o2
1LXtG0muoqV7yjdl2/WvKjDCr9bPY5tmEDD+clTCK9jC8FByqu6hrbbYrFdcivAz+1d+foGs
nS5oQIb2JmcHW+B7i7pBLSv+MtNS+tlXadO0p4BNY/fNnUmv9Uhiv+r0ctk4Xxfj9Lr9YicG
PnLt4On84UQQ6QInUXeMxv7BJKJjx6DknTjpFs7e5CM1yPk8ZzS/q70AjCf87/n/i7svj2v6
yhZHUXApWmRTkGDFgoBAIWyy6hTEtgRKIaCsGjRAgLCHJSxaatlERKoQtrSgARJIiiwhhAAq
qxAihrBlYd8JYUvY8Zd5M7839n1m+mrfzPtNf/nrwL33fM85dzv3nHPP3VgG+FSnWSlSZsTZ
IGl7xRKMWrqL8s+m/8tzNnrxWkW0iUelVTsfizl32gPePWT8gw3MxNn6dfJqy4ICeH19VkwH
u7LZZIZQ0W845C/xJ/XVLY2Am+48ft/EaU2O/SaYooibJNzrWSNb70dX+5xWKW5vU92qBto6
azFV/uzaCDDI813nRprdTfQOezXhLRxVcrWnoOzwqJ0rjdghjFmKT0eKF0dcAv028ZHpa6jO
hh/2RtdWjaFsTFf8d+SvP9v1LLJTc3kcJytb3QxSN1lfCta/DyvaEeh3bJ8Zeb6lusJ2B84A
Pl1W79rKjNDePxF73+Vyqp/Z8ZqDW7Cd9OXVoJt2c95Aq4rHkgsbcpoRYsD4nwrAQmXDNfQi
bGKLsTBYaN7qn6DEiD4TrE4FLks9YHprxV59/fa5zlhcDS5f+EDlGngqhR0erRAf1MCvRaeh
equPqGdv6cyoJa2/eDlndppEfonxVtC4OScFwJhXI1DopSfnxRRL18qmU/evp7aOqqgU2Qls
AjowVub8zjW7AfHjGXSvApBKSXvBQZi9O4kn4+UnHztUGJeY2o4ST+veFy498MOGkYlU2rWw
nomkt+o0CnNgTR8sKoCH6749vzGf133T3o5g8i3Lekh80rSDf2zAMb7h9OdjezIGO6tlLp0U
5mBejvr2mdWWuZs0AHozv8EE2kWfyKYUzhKhZujj8rdOczIZ3vm7BtOJqBZNC8fixnhRbbhv
b1vFZlqO6kKCTtP8p9RWRZ1T8oHHVzFmbmnyOzbvRBLan57uVnLp9tZkY0I3kK8UBEUTpcTi
Odl5NK9YtyQ98tSTx/3icYNJG6QmRVGt2OvNfTyv9a15530ZI+GdbVi+NCym0k2oHEVcgG/g
SwRquCNn42pPNWT1Me9mlSb3bVg1LKvzvWTLTJPSEbia7QRlujFt5Vl+3IWpAI9PfXtpBYtX
MhPBknvHtbCNHWKBGL7nRKZxEk4jWR6fD5wuVoVPg3X2jjCCPsq0nrveIUZCNt9cHt/P8Hwn
gno6Z/TDbvhCtO/2GWrVXmiUTW9pyvJm+ihD0mKrday1wpz/evbhrTqlz/JEWYxIhcAHCqJg
XGOguHjIqGfBHhGmdRVoo+l1tbckZY3rfFwdtQrKXeuX4l01bxLufP/KH4C8vgAZIGVmRqca
BDjoC5WeEkyOWhIPCDS/mpTuKH+5K94pznPj8kya6L3VvVnmo+HWdbruWU4mhJBWwJ8SYLV2
AtzHLjiEoHKgObjCy6d2bKbs8o4hDW9TMp2uVOBdu/AabUMKnicmKeZsHbCSklDlKcXn+KXA
lkky/WPbXRuOTQaVT7rvD3X/NAPq6Vqc3ciCxCg0ZqQd4Rvqqm+eWtIN2amyn8LmlFTKrCcn
Y7i6h4GjzmJG15t2q6+8Hb3S+ramD2WXYHj+VeXQlJUjXbqlsx/GC+HHFiq/IoHBdoFGwEv7
No7w/QniTxZ/HDh5Mkud/rNBvBT27RS5QmdktiA9V4aW1YuTryPblTtevXDhXyntv+H+S0QE
tjEzmo0Ls47G4Usw2QLo5b7tLFS3mwEC1KXY04ZX8kUhvCiRJIXME7lrbfMewFd8sxvhiLE5
9w7AEMXDwPP0z895DlI6tvnPvKccnN+kPikDB+78eDOnzdncpqoz1EN2gjVU1RyxFLR2tLfr
ncj3y8GCy9/f4uMmvx2+d7LefCx2Njk7GWdLn8HE/UVhke3b4iy9AuQUBywZhk2DlZRPDT0x
P2dXqWfFaWrWjZ6c6rdsVbpQowmeA7FHDZU599UvJ82z4Ua0DJB9jZH+87Wt4glvC2VtXeXB
FI3q4QVRma55C2ocCAjKx72y+QLNuP4WqOI1vzJ352Ydz8kjnC/cDKXWBWmFEcKzdZ8C8ljD
8OdbY6k/tj6ve7zaievyYrSB/gQjmUvojfvUhWMx3r3pcuknjrvH+MwBm4+UttPXixVDC0t5
NjPD0mV08yk9hxPHhwTEb8p7wEaD0Ya6F3siOoa1OCSD6UHsdGsb+Uz819pm20Pci3WJYoa2
AXP1/fru1gB2nGdRRrTKvk5fyoWL47RGEG4H0NZEdN6psR2nm54UQO6nYLdFuvW601is6R6Z
2zAFUVvUKj2zjIP12pE1C/oo/eoMuuv2Nruao7I0foxGg0xM3+rnV3u5pj//iGk3E1yL75HC
rioWe4GFSskAKVqZjVO5c6tO9fP8Ssh0bFuXR3G+dXzGS6bTsjex0sNquOqjfvHCeC2nmaTe
2tzmVH50pZfq/l4kA9L3EfpPQn8fIIM59v2V7b5tu/j5XRhbqDhtIw3uZo+FlU8Eymdj1g/p
hkxZgJEhsAwgHyXdpJsvVxz/ad1BaeaLSeF72WTpKIoCUlU3drARQUKHnXJSVXUrHnWQHpwk
f19tGX+baRThPYxnJeS/vRgyyQvsH9cDHAhaBREa449K+Y0MFuxRDX489b1YH1MerGOLIurV
G6XrXXtFhCvPQ/Z10EF6bTDhAzouZ5R+/Ntw/38NifYjWnLXNgyFb7iYwUqT058fk3IYFbzs
K80JT8v40bvFI7KD7s9O3pq7dRIRqOH2HOYsDI24GD76ADS39+Uk+9ldcOju2tDiMQWLRw3f
6MtD8x64RcZa2gkkjgKatwWzT08iKujOjxRDJty7RgzQsBJhfN31ubrvzyH7QtTSf/4o1H7W
qgMQLmVrKKFvZu7Nv8ZMNS9NXyL63bkpT7ii5Rh+dBV5PHRZ2aa4tzoNBwFbb7Jc5rbPtPJt
k90OkS1bU1so26nOpRftEzMkFx2gA5+lff4T/tMIHOHLKQgfZ1FKzKiCCI3H/ba3dSxcPgp0
mkE2XuhxnHGLexOqvmtzeyarojAWheF2N70MNdYItYJOxiUM533WTpRazjR+EivDULpiJq4D
2EmQ74u+FJqKcQBfu6Zg4Zy96pCItwKatz0oZIke7ZiNp5lr39MPMiD/QAdOVteG5WzvnkwS
Pt+xb5n+Wu7rYwr2+j47F8Zsc0GN2gHHVciVgGYIC9dYe8C+t/Hz6uWqUMNiJsbsaj/XQclH
KZMa+LWtvIvQzbSR36JokOoRXc2UwwsE3lpsz1tKHoYOnKhl35SA5bdce6VBxN7jEG82TvbW
qSepDF5emnqObzdDUFChM40z/FMhCje4LOMqVA/MtV0e+PozbG4twE/espdaZq/Vb8GyBV7A
KmQTNSyu9vSfKqx0CEty8CnwVumrPu1xy21Jd3L+3Ucj/M5K8JBaL+k2PjV0JeJC4CGsUH3I
O8/jv/mI+eV8QNN8b/N83ifD1x5HVyR7ACytyWBm7ItHvhSfKAdqIyiPWtxMMUetshufjoIt
4xM6sYSVyzmz7GskFSomuWNMlnBX38ay9QpH+FLYFnCM2y8wSTAZEsYf6rDXWlycPzMJVKoX
CCVxdi/XYtaJm1CNSJc3Mmuc8oIEu3ovXhSeRp/OZ5NCpeZtXPHIq8Az/4rJFOlOhrVgecMk
EBkxmzOPJ3GF8/gJFBrzRuLclB1OXMQI6GTLHq32XESRFnZu0Z9NtMg7mXkqrHRxGA6hHY5d
Vilw62hoDlaoArjZTXnl7kUTwZQMoQpQfp2K12gd3BaqAPVHzqoXjc9XWjLAr33xarjWW0Kr
BwqVUnonwE4z/1Q12+5NLhpFpS8rA/5DBTjGlwuBrdrdzciaJAZS9RigEkK9XSTJ5luQkf0L
uEyQYUBP1YZdRVh5NaYtwVDtVfUm3sqxzQe/O0dmUTx9kpYWwWBPy1N/flDvjCd2sY1SufmG
tfXYscfWfJ5exQ6Vz/HlDqHaiuUb9uqpLNfqiK0zufiPeTCjxy/TUM1fhYEkSYI9dFmk1HRh
iM4MWY8W6KTSQF8Q1fpX9MAvce5rgyt2EBFPMjJrDT0oxT51HopSocomX78uUgBQJaex5CwV
NYz5/XZ9hxShxc5iNK1zwzhutZuz9cAs2Ooa0+tYiOZ69morqIOY7m5e3xNC8Gp8KH+3GV/D
utorjLp+aXuMu3ui2Q2b3dH/nAeTg7uubOhbkYHQ3PCo4ipGiHInwNNInxa0Ok3zPh36TkTZ
2Fl6HRyxqrURuQV/86L4qHKH2Y68+iuirZXj7mE8fo8QFLORlx263PZRMku+8fC6gPB4sqjH
hAB8EzFl/t2cYUC/zlpM00J+ZQ8zl4uUvZ/mREkjaoEVp1qLy/tD6uK+69bM7d1mXDWxCwwz
G0YZ+OLCl7cv0/FdMeHGcclIg2z0T+DOGmjsjJhvYZjxUC1/nZXXPDfYu756g9sZKbSPEM7y
hsR87/VYPNkOs4SZ2oyBtijXKx/fhZnNtpScunKvh/mD4tmz+kfWW4lM2sUttnTEOxHuwpDY
zeS35Iyy6LO5LED76+xdMLsTa0nru+Ug0hmmhT6dzR1SKxLNYhMRaqvRxoFTNLLhojNwMUGj
dVLusduXkFzTmqCXyCjMFP0FPnar3CZBtyfS4SWXaGUg4EnU1DwGKSnbyqanQ5QHls7fuVUT
vOBFH/EaIMKy+eeFR/Kfj9/4Za//W/61GapXDvy60IdGrwjxRZt6VIKCzXdEJfojDzaV93Ai
DA8iAAQO8p2IZ0CXabr2umDiZGuECgszpwc6dZq4NJaEXlAIPCHcJWeSxWTKwwYn0j1J46G1
RzFDWNVG/pNidCKAn7pmPSBmWLJWNJFqgCpW+N7lCRq4VRbbViI8cJ3gB32k7CSMYIorim+7
CbdVng0TektaGMvqRTuLmuGxf3Z0WOJF3Qu9rghjxVpwvXmEy7cskT8M1nyk9M2MX6L73HzP
ZhYF2j+nOcE9T3Imu1/8oW3zTNO6hWWc3pjd3pXl9NuwiuF3Il0Lt0fsAvfc5V4wXMlPi41N
YHW+bxFxd+t8UVz9Wfk9M0lhnO6pUEjp+tlbJ61iPpk73PmdW9tbROPJmgcqFsh1OHebVJlg
l1VPjQiaw9IqObEPb5OlsG3GCvI79qW8NG2E1xBGs1VlpKeMId0VXRkKuMDBxsYfmdi8W2X6
2XxEEQvTpypvpIZKBxsIn8KiDW1WcVIfvxMJTc3Ui5RcGMZeJp3+dLr/hz1gv99R3+DEq8KI
Z7CV9Gwdi4G5xQgh6Neptaf4UpzfVINv8LZgGCwEC1VRMWluy7nxz1bFRF9ymYiA/mj+6wAm
0YbhHm7ng1HuFJ4ZfcQer37C8M7CH41WvTS6K3xi+SuWgNwzFnY/xZfu7zyxCQ+EleI6gBOV
IJomEORguXn5lKnTFC6XE0k0U5Bl73rat9AIDQbdQ9lEn1c5EN+N+SczOTiKdJeVg/sWLkW1
vpkuMshx2dJbBHmUgWhdnKmN5ORlYryyy6dzWlPOgC+WQnTra7hRZJBB4USX3aO6cydCX8IP
LxXdzQ3JL30ZkPqMSzE2VVI4+aRRvx2rXOUcx3df9CAQM1+SwA5rl3Pv/HkKnnXGi7VXptVt
uDennnwMYn9u16tng1u2a20xWtfkVFjSCObJ7dmCcwqxb7eRYErUhYGKzNxTF3MOTM2gpOaY
qRedTUFSC179XqwFibJ/+ZyWX2/jxERBJ9+GVLFnGxdgrolyL1Nq9hIlc0usgiXND772zS5s
cccmJ1HcG5bNbUcexBmGZ40jeDjVL0fwjLc1gHxhPMnqim/xN72YbFyHW+RrSEujMOTTXGui
mfaIxGUpihIj5YQeLGPj8vJ+Y7F1zpPFrn5vV9apxy5NRKvXeybNnq+xuR4HbCJyEUhBUlKK
UGmoHtW2zEeqNk8vt903ytaLdDAMo1akGS6C7Up3wzOEwf8e9ZE5430P4ceP1vmEhL+cR2i5
jrqnMdCw4VSCYZhH/pXA+HBwCtnLclfev8nAOjAgrbqqiumi1cscgqYWD2DUqpOLx1xbK+HZ
q1Z6rkkY5YE7ITf+5bL+53/gs931Fxyp4CsM2ciMV5rldWeHo4jGDRleWrhQHSZFxg0DRXGB
k8nJYrhgi6fOaq681tsBIIsgf9OhOfz0vSKYvkcbto5Ma7v+OrVCWthfuaFwZarij/K3W7rv
s14EHNH2DsIhAoQzMRmenRM8h06+zmcMd0ozyWAnE8voyjiV2BthHvdaOBEXlfr9A7D82Nnn
5wuxY32p5V4MpE0HJmcMDso1HMPJ0IE6UiG0rPH6x9ZxI2zAQT6OvoJt69lMGS0b7QfbW7lw
+nnu2TxnH+yU8HHxOl8MWhNsjyAV0EeYq5fOaXwXEzMyDNBL7qv9otldIeR6YQrcszI1vsZW
Dzz8YnmALyBDvasEwscMG294j/wTxSzaOtmJCGAIlyofohUQDAabFWanm3ZtPZRQm9LG8rRY
CvcpRxM39YM1Qq9hcR7KX5DH1pj6bYFPoF0gmTbfAo6K1iYEAkUbKQNTT/evRtHEpoogg404
7zGYjNDK688tTUXcdylNLu4MYUuBIwpRSVg/Ctjecj176YaCTmfglbSe8i250FCdOvMzELuE
0BXDQvdCQUDw9FLgxE44zqOKDteyad7UKLyselp5xPuwkSTRy28pC+KLDBWDoBWN+sjDHcJ1
ChzHdzDUBu8ywsHmPwL/+kS0T+M1SgYyNATlHeplJen0hjUgn7aFKVg10KJHnPBN5puwOiot
OAn46E8CYaGR3s0Np6lSMj5DiypEGTs4oxVqOpid7vVGZ3j2xxNu/0SR/z1Uoq4Xs+b2dbZd
yMgsWtTs2PyEXQPxTSMWgkE75HBBclI7rjG19QHDwQwPlqECOTkaq/s1Ild7c3Pgt/UvDm6b
aGt4+9Tlz7S2vEFUsfJYJCzSAT4F0hnngc12TmFYroUlBXTLhPOT408DlTZwgQpBwc5naR+t
He0BvQ7wvr52pTw6OQX2YOAHhqR3Pcje3LhOA+PVCb9xAtRUkF9fFiTLvk9VThREmJOhvoSx
vqkU4IoaPgeDhRGtHFty9R2AE1h2HYwrySnNXpR4kpQCUcOcPWuaITknuvb3uP0j/C84VxjT
Wj5ZdItLHSYKD0NfdhU3tb/oDdacGOcU9+HZ7TmwdOi+p/VRsxKdjVJmkrglsrbJ93XswZyd
j9S9gTb4Ulz9xjWiekrJSkRSqvN5jNCC94kZeb9xJK192vD0j8LrFJksU4kv9/KfgiKW1+O6
X1Mcb9JHGKNuJHCj2J42zGQD3A/Si4nwwf8YEaGl6GX07LlGK5P10se+IQyGtDduOCi7XI3U
24ypdliu0TWx9klCyzgXwPClB0qC7LJtj68er/EKD0pH3pjP7kXcL4uGBkyOMoA6I8MVnn5P
/rxs6lvDCk3o+ta+4pA7/6weOa6QpTlIBM/3qxWypalgsKMgBWK6Cpy7pEdEHcOy6pcceoyP
vRI+hxpWTvOjABJ7VtSKbSs8MydJFGxhzOpEpZxqvQ14JOqFXIznVH/OXigxQMFcQCi7PT7v
rKwkfpubGhEwyuIOlWD87YEelm0J+lRnDKm4U0ePLvmxwuXO+Cv5k3hOMyuvE+6HRIKyUyuJ
Va5rnr1aUXu6AmvfSu9e3tiOf5dNW7Rq5z7VvE9GnA9tSBCL/IOybs4iQ48IVxQn/cYjezZt
Obj1eRQpmlDk7qAzlX4G2PRXCYl/sUp47r989AeORkBu7eNb/SZewK/bKkHmMuAJiMMMTkdy
jpZWYR1YeOjFzAuK35vNrH5B+M4AMZUkqLG+C42fDFkmCOOHiD2pDpm8dpWSf5bg/z6eGzue
495HayWq4Ly4C4GnFUW/KoSysQQGMEKd54uWgTDM5imhVTYbepY0H1RBj9Rnkoep6U5a6svf
l5UXNc3QRhd7COPqXZgJh3Jvh0neKLuw9D7Mu2P5CQa2YofMlAF9djr+grta7XjrXAUxQlZr
eJTT147VtpkeyOHHzKmUoJYjGTaRJVhTbaq2jY0N3dGVdOKwx+T8D3DRlban9HsvuSho3zP3
kuos/DSivXfVNEMmMmJK+QWGIKYSwEzRXF9p+fjY5N/n7Y/x330l9dS1rsnpbJcQ/q7CV8U3
AhX2ZGip8ipmegMdZKAj9fq1jCE2h++sD3Y31+I6MCkdSQuHsGM0zfqBFakG/8CvDPXd1Vs/
fScibssxCdl9/TOBzkGlRmgkJRNH7XxyDWeTCNX2ku46nM/DSV8IF5WixaPZJlI5bjaxSuaN
+1vS2Al+L141euY23E7xWj2M4nImGwTbDLOZapuIA1m+LjVZBN/sur7EUsiccVx4jq5OyLK2
A4K6DbaO9iusg/piUcnCX3a2eN8/Sd6idlu5S1+lx4SPIFDVG3KGlXCveemJeWPN+3M6Gr3B
Me72NpHgfisZulWoDKiuuIoGK1TBqt35PF5p02/suOYpZOilsWdUw+MhcAnjcheKgsJZXe0b
EGoHERbIKqIQjtVxORtD6vizmpvenUP7naOtQrjFQcw76EVqme+T8dDlE5MRZcMkGGTRPANG
KmzBIjcLJ8P646AFHEX9Qd5wE+Zyw43/ZHVtCuI1Peb5orNa7sItJpY6pEoFy1j7Jgsglz3h
divPN47Sptp7wtFU3SrQdLzvbbANIl0hDlcXDkag9aycMbFJBxOa/hPbvwDYh2HN8pVHiRcQ
qzVa1GKFiGD1XPciWwwpT1OrrmgcRiXZNG/Yr3icTV6aMol0gKtjSg+VMbftchaLTG++pmH2
4FMMrxd5FGuDiYG3YabRxeM+PEm9a8QJVOqf7ZxLflg1POHI5Qt5T9fYI4QLFYl1fD+9QPdd
mKlFavS9pFQjMC1QBWDaRYd5ER9NesjQHnHBOo5vJGr/Bbz+b6KMqcNkYfxy4Lbp5b4Ddd+L
BWDLbo1NXsdwcwVzDxj27jKWwqATwBfJD94e6p0WfWqeXDtukXS6jJqm5JhNysio0oVvGEWF
09oQryhuglas98skotsGnu8gCRbaVD/BuNWHxnd5njWZNoHMbUF/yigamQCVe9/yq2ZVWuXm
76jhm7tsxt2w6rzRHpseN7AMGBSv8JnUV52JevVnpjJ9umdG4xrlQnR8C/VBShrV9bsGk/YT
GD5+dblSuDNOAsEykfqWYCDIfh/zx3+S1M4cL+EsMIzINNmVt2F+Wfqn6JVBAvzjdOFOCr9O
tKpboM9FhWAbzT2dSg8sLkjkP1viQQKodwsd9GaZfl80v9U5W4pCS6VDcx0jUCtdgkKTrgT0
30iTEUzTrnaODJsrrH/DDOtPzUir1YmwlRgqLaBnZMC7/fsB9Vbbjzcp17L5+yxyVMrvEWYG
5BdzEVpjsGs1z5fnk3kyriRLsE1bpZTI9qW/4f1nQ+L3mDVlLnj+/A9MIhyFrZsr6KXbREGh
3lSRlAfIaBw4fgx96OK1PmwhCxSZg+G34aoYc86BtrjedNNoVcYKldDr/nAW8KVxwLI4Ko8V
pxoMn3pWsxGV4VxY2oFHwozXGGbvRMrHatFirE1oYL+UFMf0EIEC/lrK4pWt3MKxYwsLEgmv
QIR7P/q4hAMk8txcvDvNiiidj7uozlpgJgXcDwQ7TKJQYt/8szn/X8dnrJTzAGRkRn0wlCfB
w8TYsq7V1Etoh4y4YoA/T6lAz2OhwsgpjjcFu4NWdKTrgYdqD90cszsSlTPLaM1z9zpuT+1Z
Weh3nCHn2mJgdL5/VAHfFX1EJaW+Z1xn0bLLxrILBLQKP0BYudgrfivUvXBoaDvlM8H0iaWy
yOt1ls56A71CB4KJ8hEYKqd0xYYBg/oRJ1eEykyIAvx/LIt/fOjWnPocS9Q2lV6zTfh5JZ6t
ETrEs/5pLUZoHSz7i3WwBG26eaGlgyclEwkIsvYg0BLNT7cHO39JfBXbQ7gxF3arhaoRsMCC
zbQWV7XFKwaOF59NWgE5ZOgz0y8IMOgzqn5/wjkTLOnzLNkFV4Z6S/XF3msFgtL2JeVWKynz
6Bit3YY75iMiB5FGqvrBjSVwdv9nMQpPiMel1VnhESstkWvTjNzQYaLVpZ+z/yaG/aei+/xx
W3ZKAsRWIUMaAlcsPxknbf2kPs8mt0HX+51IVgbErOmq8ACU29e9N7F6T56bfrTGgF1Z1D8a
tWN6GHesdB3Whlq/PHzjb0h/M7RfaXO1NzppaMorlDkQsdHi5eMwphzY2pn/Zb5xmYWcnS/q
1cYQITJOKXF0Ha/asQIQ0Z8fIzgEvhMJmULuGIzsfW2uzhealNe1vBtfwY9Piv7uQjGJ0GxO
cDlcvuYxx2T5SVrI/Q46lq7Oln96m54ls0GqMIgJTJSLsUhbMon0kMskBnlbyETnxm9nAYdH
ieIrd5edS4nvREihZnsKQfHnlX5nmQkuM9ahVNOtbSEX+f26vC6CT/2SIb9r8jrceO11GAlr
JgP2uL/TnZsBU18OVcQt7Zx8sDt1TsX/HwtcnFoKc0GkFd+GbbXGmR87JpGzohvyHE6HM1Id
HfSd3cMZOtJ0SSkg0KzwzMcdvRqlWj+1koUhJEanSm/d8D8Cwyk5MkqWyj37t6NUUmIY9qm7
XQLsREwWzPvFw4WGS9FuA12t9Fo6VWw4p4Q0ctuHaaI77INFm8lVH1GlSU1kt6EdJismc288
RiK4g0QQztHBStrSQeiBFZrVqZKAp6Lt/5j2P0qJmEbznpy/ue5CvnVi3hfM7DrOPazrkva4
Z7qmfhxmUqjMlbMwMVX9Ni2OtCfnPg7oPq684zxRHHVtGGntzAAKPItmyT/B89TnKrMwnJR6
DafnMOKQ/zDGaxxOH8rZtnLckIkgXroqZwcvcvH87Nq1GOVxQJxWfnO9q4e2lC4k12g7JcVr
YiaJC6rPTuK5l3BlovyIkgAZabGNO/8zGf6zVrsrdrJRz6dW87mdts0V8U7dzb0aezWDTAdZ
rlG1gxTAVegJwXsmZadgcAwwCMjxenHHn6DJljf0IM24d3Y1zOyk36T5oTOosly5Slx6fmPm
cl957EminAok7svkA3lLiXdNlUcMOGkVL0GJz7hd6oX/YQw4qqziRQVv87vYFOcs2n9aA8Sl
yOEwPQlc2TxRY8mHHrZzvw7LL2TXYYV38+5ynkSDuHYFWkoeRJhGdTGT8ZwXsQvSwdzqEd6s
DEOOoN+T6AE4v3bQSf/Y8aXVpDiJ0IyfFk22LBG8IU3oOGgIE9/wgqg43b91pnNLj/fVduLj
NDu/yeFCrAA/29XSRgRE6xBcKjNsaJWIKet6idXf3VEHYw2VqGoMs3rCjsWZn6/9N3j4w41e
si1dZbi+hcH/exNE7z9vgmTVfuJcqvS1KyuydyVS7cWu02SD4ixxTP+jbX0QsFZXk8FRFejL
WIIkt+oKNdD6igmNW8FrA62DNWEPbmx+16MyNYE/T2WSvXRpsDCCE8fDXSZqBYnApoKtp8y/
xKYrDF34Lus9Af43tP4bFxtReqoFi3zm0Pd0dp2WCqEIVsuHTI3eHkp9QhjCmoD0HczjX5hh
TH9M4MSQjrJNny6mxtiN3tu11k6Muv6D+8tuYgjBKmCHcJRCNsQ7LHOO32O2eK7YdFnpI/Bq
Oa8it0L4R5qnxEGtI8Ny4RpGrC/pCzY3oc5DKYYSqWHrOcKDo0oKBFqnPFGaTLJBpIzdGf4f
vei6b9w9zLUQl6WBSTmfjMViC3okAVEoMdSqMsMiK058S+PyYBR6MaPOf73oTY6Blc5dSC1f
GyrApnt2wLRsbBBYtdVvdYyIVLShG28xcqC2v9q/S/NPjfPuudU6eHoaWFJnkmyluPj+FG9K
Pyf2OoTdUxQ+X3CPVd+5mN4uOC0gbZ7ugfcgjWs3mZsWirD+ntTgEKjqRMnDL2iHIqVemosG
zDBPnxuI9mC9xKotM7xcl57rQk0Zno1uVCYjKobPAAJ8VkRNhSNH/Nrq5yUeb6N8xvpK05wT
kFJefv1cWrm7kRwGXfnxobSZ4WJ6LrXbFuS4nidRVDJh/QZFSQvc6Dgw8t6w0/crbeiiUC6q
j0mUmX4ZODnTt8TPNZebU2vrrHafG59pST8tAZyJp1yABMadX1rhbk0JcM98t/rMSlFLkDzX
fk13rDJVCoiCqvZzAT9/2vwe6g8DZdZY8XrFjoKVxqWdb1/c+PXG+5W3noUuZ9SG8rWu1eqX
b1CUTtRVRHxfnuqZZbBmB6vaBrflMIAcbZsoP6yp56MUv9S7j9ZezvK8ZFszu/pP610lZXre
za3SM8XFK0DRj4glw4UxfNojnB7tkfDK3wQm+emn/0uxxL/O5/+89DR0imkSH8XlWvsuUpTk
wD18/+hlYNDz8hYEYRBvArayN4/MPvBxaEuHYGmCkHpSoRFyGxb8nH96K7SmhgStKxQIcyoQ
TtlqdlZMFu6Sil8RPR/5YdBHTBhW7U/PCdPKrJsMWehvHwkz64xXOp5s4gdIT71mL2npfZ0n
3RqbEsM56KAjQ1fSwJc86AEhpj73b/r9PAH0+63q1P8jyh0CxWKQlpbRzyX0p6yxgVo7x9ac
Eior49lK4dd51j+uuaXEikImorMqkWDL6AodmBZYShGbEjNy31Z79S6VZrydkp+YHA9uTCh1
1hv35z5LRVxwx1g877G+F3FWucqGOoTFoJKzU24oKHRGXCmfrI09Sop6zBrOyDtCdt4E9OCZ
jSXOwlwmyuNlg3zTH6wGs1EP1q6e4yWwDoyKiwjjASf8vss9asOsrW7RiZtMDXWydWyL+8sc
rlScrup3FPCGTKwfntr4szBEi0ktZIMou3GJYDPyQhoUjX9FUvpO0q/HJRuXk0YDKin/HIqx
aJWPifsY9N7mJyo5JugsSj59nhNjhicVGhoM9+qlHzNd675ihigs2dLRX1/fd4itul6++6z7
wSD9fA6kdY4eril3FovlDqE/Z2RaB3pAFzVLuGuXTUd+d6cQMOObz4yLicJYl8QJ2aO/jkcs
Jdx0OqTBs8YtKD5RPs0xWDTiZr9hyIL7kl+P3ha5x7AQEqMeyNqYC0Cs0Ef6PSNzfJYSbLdu
hmj7PSDnGDFbYo/g6i2YJB15hCy4sat6YUu104ZuoZoGg5ha9PZ7+sUrSiKyD+OThL8HPYCr
SeIzv07QH6a0uZbwkvq4Fa80bwock824UvTTfOQqZJfElWHiaFbMcAR6/6SMJRjk8cyx+duD
RqkVRqP0TFSZf5q2vTAtTFpcaJWiiyZjBuRni4UWMHqGO0Fh60REf9waY9QSvCLTbqt0of7V
wqJ3rdXTYDuffquc575r5qXFkQOkUBtaYXZuLUPog+GOWjkydAAyMvbOPktk0epLv1d8kf3u
BkIDLlYNky28rDJ01izIl6hr9s0mYsS7sEqxKH9vhomlRZsdLJxwmNGQU+5tzB3CKndyVDSt
Xhd6Vdvb5UkmtwKCo2qnnYNaX71qxLKbeudzdGoQb1vIsoEO01xEiqkGSbHwLBQOBusMQc9m
i7UI92FcNNzic7jtbUPDCc/9eMaedRWyhjcnp9w5Qc5Y7vPfyhxKIgOldDjJBwqCIu64AUaO
3d1UGAW8pBsI9IMlMxAtJIKqulejb2McKZcINaEFHivlDlch0s+Y/FUOijrd8c80Ut+JVFGd
N/RvpHanFOTE0rnx+UsP8g5j3xPWPg8c3Vo7/3N1bAnuKr0mSyZG+5vsIpu0rxorpBlpzn29
R4/cea/6B4H7G3LTp36YK+A47yk9vPbru5i4Y6hZlwpjMj0helgmwsyJ4N5c9GbIFg3myTk9
K+kHeajKo1ZoT3xzsNnJOQE9IQ30kfZPjt/ZUR7L+rrAe1WXaFCEQujHvK7OH8b32LXObsRu
R8ruaC0LtTwDf2FUqo70punRcJsDu/5sdM1GbLVefkblWq4xNPmnMZcXTc3Vwy+qoWwd6bao
la5NE6oD8C+/M1OXPojjf+PKfjwT05KZ04NBEUDffj85BYSvNKt7aCufs7alAHyxCQ5vtmlJ
rZC0aueaNRg0isGIV88qPVq8bZiuXP8SGsB9J5KaVcztYvGScplfUOBYPAQMqyu5n+NbXE/t
lKE6LFc4J1qyMGehWNgdtI1pF+jzE61xYqCyPP/cME5lNCPYXU6ToTiLzSnq0PnzbzpZvPb3
SUvpMRgkTQ1nSNNtIlAorqQIPe5W3dMVblOjlY+JncVuTwQYfST90gxKeutISztfW3i5jBUF
gUBYblgVEzDIPOiK0snNjqnhfLNXCseP7ZV6oEv7wSfJJr4QTqrz7KqADALIsAp6FKdbwWDJ
IViKr9irkOEeAnLRUzhjb61rTzjb4arjM3YB3Pq0KxNRMVmBO+G5SqUFvS3CrTd56dwJ5Itu
EeGslRefCP0OKdx5B/jNV6zm9UBR1x0Up1T2rEIN4V0RQjeaA7PRhwu4hPj4r3IQxZCoGOzm
V+MHHBSnV+RwdqSTjPaz84UEDDps7w2wQZJ+V//SezI7E4gDdFKqhLHoOc88PrrOjoaiyq9h
1Lgj9JnoYJgAyWohmc+o9Ccw3xplvAQ9bj5f6LOTGcA1cc5RpVlOeNkjfNFFUm5ttR/Vv4f0
g8D/chrW2Z2/11i5hnOKDCUJAwdLr1jpu7f3rZkMlaeURepHOjrAuj00Hfv1QVIy1I6kFFi6
WMz5nM9f3RpZlhK1awxM2i6G+5EYHktlHj16CltgrGakznK1KwX1WJ8xGoE+ooExsbFOmOB9
knHnH1O5g+JOPrzEs4/zDTeHbfADby2tqyqDB8muKmGx5NS7UtH6/nPzKVqTTEwSimyosRQw
xB2NKMyBZieTHK9+2XaWhZ1llQZ9ddT/9mAruV6fJvoNa7OmqPH+6+yNrmhhziEiFLWkxlch
nHKzBHXc8X9PCfrHNP0xSlIfEPJ+7C8Zo1OhTXR1gvIJdp7meBqEFSEMnr+d9nlVFNR3o9PQ
9J3IqTEsV9IqXPTMrDj1GXu6OuTirWGX4vsMQYPeJBfZL7ws0VVuoL5Dl6N4RFXoO+hZx+2p
N4qppfi3n8v7PaL4v+dl9RRfjAoUirS0Jpyh42/VFYXMN6GFc971a2GYjHu/18uisbjkDLsf
F9zSv9kLhJXThyAQX6KcRrIwHgwQdEXuVBR1qj9f4oXC8SN7pcaIUnenZQT8bQtlbEVtheZX
1TPq3rFiHbWcqWfti1V7qiAuDJKh8Em7EqSLj1iNGWbGeMbOpbdazPZevHVWB+KdSNv1ii3U
xrCCcKM2P/CtXa1+J0/8Ytwb78Cg9BuzuXEtryG62oOFfq87s1HZuZsyXWzyEBQZCbaxjusZ
Mr2z8DcbQriqIWInUD0PgokFJeIZvBscdNMh3AwxtGmKEETfzYR40/fy71rckfJ4T3z7letG
/FkxoOWXnDNDFc7pjLDyz680ClNrWZ0klrOrbWi5jTGdFEoy/y6JoktM253ssDuuDb3tEK9x
tRpVxOZupQSvLPZAUVs6Xs0Jvu8h/jDQmR688zbfgfn6ncirlaMH7/xaaz00Nl5vfUPihXxk
fFX4ccn6yFQQ15zaGaGSW2scoCd43YGBqFaHjvZA0zWBnMlwuhnXRtQx+tLKT04rHNTpLh7I
QL3HoHxoScDG9RXXOJXqAAA2EQV0UIp6dvq5ZhZJSkrmevaBV79Gwx+szFwi/nIP0eleCTe/
DTPQG1buKrt4DKFiBZApu4+sAslp9gPK9R0cm9vKzxCIpyORjdHxq+HSAae3a3gBZdsue33d
jRwvQ1sS2EMrt+Ejuj5dRy54sTlSx7EHITxb7o8y0mmJrWwDyHLxFwKONshmkT4730WE+2Gw
y4sxaUwZqtl4qwsJhJjjTiyVPIT+au/+fcma+uFTw8B/ToGj19zVRfNJ4k/IB3SlOza4156a
KRf3mY6vM5ir5KRf9iFJb4n9db9O4kMgvf+xXUtvvjiZB5lWyI0LN/zI39Rk61mXhC2pSME7
4IJrD5RvHtfvU/SSnDl0ViXmNthBEQPJuaFwuDP9Svkmaa6V5dYO9xmKDnDHbSQUsYkZpW7p
2o+EN1cfVHjxgcsNxlAVSMzhFeHMBXYOi5Fi3xQHLqX+eeZShTM3RNPeUHdl26YLtJMyBWdz
hS4bLEaNN5SdtCJa8R6rip5UrU9Ze9eNyAkQE3b7QM4uVrkfW26+Zj340DL+ykJt69S0Vhct
S8MHZuA1I6CkeY7tD3qvvYiP4XVKfrz7ZLwV+2R2FYvgv9jlOiinSguU3U0VwLgLbBxg34Ow
LznXthIPGu69XGY4Z/606Bf9zNGma0M2VMeHaGldDpBVHBQgt0Yymt7H/CHwbzd5idKzslLv
piJNDM+y78cgw90pCGHnys4Ik+qAHYSX/ZNQqIMxFxPHDHjTr4SZcPxxhrpFQXNPDPretpFA
waA089RMq9zHguKXRMsNZ114V/MGQHe69KpqYoKpGvP0sVH40Kg5rVpvFhm4/75JOAOk158R
2glm8jd0JMe1WFjyY0RS+hGSmM+HcPdvXlf0al35CvW078inbl8yaz0As6PP5KqNTU9uLORr
QVR1aQVnoSk+mF2g2ZQpKIyuuHhVv7LIWtdZL41aHtJJqlaaN4Pn5nCGUqt3vr9dp9xzbS1i
U5gXagBjYgnKrZwuOzHy4fzvP0LamKpM37k1JRoVpGrHin6iwnhrCLgySBdwHrsxi8zJzlPN
oHciotXXZdzw6CPn8dAcaIkw2WnEQ26c65Z+YGznTEBHV8HUTqovH0FYsfjz/CthCeef8CTx
oNKr92/qctSLBs8NkyYJ8RWTl2YJmIAF5A/NtzwqLfsfP9bhQAInnIGIhbYo7ijDjCx40DMh
fvN9bkRPjSFQ8sMSEdA0HQ5wzXTHg9OYmO5u8d3HyLfIa2nA/Pxn94Cb3GLYQJxAhjnc/G30
+639aF+7Z22aTtBT6vSc9cCJP3VXy1hGeb2R8+nKXvcCQOK+a1ceLvRYJRcHE+MWTiWlyi8O
Eks3HMyRtVF69iAdACE6VMtu/cfs3yHhv9DxAfPu6lbl8h7v0CaccMMnqsfbY+z23BoMCR6q
03utllKJS8rOzsbmlA9kr0TpQiHItxJhM6868ylfubBMqXCbI7Dqp1RkfEDk67PIW/2Wth4g
s1meFAg7UwlypPmmDkrTsk90vy+aPzp8/GhNuWe1e6pglgSfBFqFOQvPnqgHdCmp6TvOjSi4
ArzgSlRze1pmSJlGNADnFcZV4IMcrCJlWLlPAhjLezJh9nqsVsLL7KUdcJwtY39U7VfN5eL3
3XSZp+2ZMnbNbBrmWq9/D9iR4Y7CZ+cs9Ot1tSXCG4+kFKp2gKVEOi99sPxkeGOq1LP9ZiR8
jO7RQ79sbnYRofa6mZLqFoHh15XTKnQGZHZns7JsxU3zPiOHjiMnYIiYBko01F1SADv47ftt
g5id/iOBoJ/w/lwnhuFn1VxDVZuOwhKejEsjDBfevHs45enHF+kWIVB/rUiEFiB2bsm3NxAm
LxuOHX+RgyUlR+dogqWm0JYO3h3zdBF00/u4PwT+7eN8/0HjR8ERjlMKeYrOfgHxSiWjAW6p
SKBlc6WMzfBrIsK3PccHfa7fAxxxPqXQ3DgVUb/88eHCyVcJOREiRoqVtdbFoLrpwNkqly4K
XEWtnYqHToFmeEAdGQ5+0l5xJ0MH8KPJuQ8h/d++rnXbtcX9e7aRnz4LrrR6haE4Jw4G+5n7
bmrkOIEdexwFSShswPCyvqVNs4NVBFZMs8fvQX84NZN8Edm3WordGyTLCxLhZLSS0XWZjYsG
s8XER6kRUynb6wX827Tcqv02Hy6AXxvLIoR0EWH4dah5IdLzqwpLum1+y+E3hdl8NRLaSXWo
TPbY+587GL3R+E5kRPzr8lCXXq5VXkB585ahjJ5r8gbrIq1Yl2UZV+kOuHTNVrXxye/P/v3b
/QbizqtmLfNuYiPHNsYozpr0zB9nDf2aUquojs75odVlLupJK12g7SeFwn3jk85n6WLPjYS5
59BkPhMMnc09xqbS8iPOokhylRCC+AkVEvpTmpKbZ3LB7u5x5+eH2e/z/ceHg05fGnTRPoHQ
Gh1dnKgGUzVCZqOMbW/r0WD1oG2wK9YX/U1JCgYSs6xz4pDkpEK0X/2zUEqhL7P47H3PZGSq
MhTu4kMZGVg21LbVHJrDQkyYRMR5CgC+p/Lwmt4Hi2efx97ZmLeaocyc6Vdnfr7zy/ZHNgON
cYPsL/imrLoYR98dX5y5+T1CqodB8lZH8sGES+/V3nfQzL3mtoJnXr7D9cJSdAc8AeMHBDwD
gup+3kHvouOht6SATZqT8Ul5EqOLO6+XYqVqDRqySm9Z6UekBLq3EN1fI7coQhsoS+wXesh7
X/hvwd8+Wg/48QljLWy573OVEqJjt0oIoXMR1fmfN5GYW8xj2Rh23SzfF8/dwJs/MNJtSIs5
V+S9Mo0LtlNvqe0eO1YR4s/GlKJwomKwCjgq/RuI8MaEasd0cjFLYve/pfEPVWGfuKJHrZVH
01RO+XpiWkg+MCkanGarhRDesQ9Iuh+TGiZYWV8KGCA70goChRm+7jwpsK8lOp8m+Y8Kc06F
6KrsIUqLmJWlbjmmSkctAN5K6sjoDMNyt+wtqRPHOB8siV9fOgn2MX7krwoaznHofsuGC7Do
uGew2l0QM9uof0cbT6i9cDQtI1Bbvg+M4lnNCfPHbi3rcPZx3yNin5RZUE0aTiH9nslK97kN
FkvT4WpHo7Qwn7vcBfdKS1plRhzE/N4l5oMs15ry/o4rzcXKuiEhVS58CZW1rk2f1OtZUAZg
MmehOfZY09DIe4g/BPwvZuNfaXrGD0uUxC8r55UjrV6mBI4vLJzWrE4eg+VMTYbRDRfbfFbB
citwJldx709mSYexI3bHApYSExSUv9eLxOKYxsdk8+PIYRt67HZhqgxKKLF0lLU0J4CJIX7l
k3/Aov0WW11LxBXnTkxyc5epsdbtBRBiOJ0Cdsf0iflb5WYA6rutjDwm7Co+SV/7eiyWKnRL
TH+3mRXoHAHzMwi3uY4vyfFt7SbqUeuUaZIgYQIbWg9l7fKHK0n7KTuWm09dpon6tO8v/+KY
JhTqx+6MVbjLm8227l4uMwXGMomw6cXbWHeAQfrjEesVhWZNNlnazJRF3oihxPrtjWxyeYCi
0tckKbMpdXIijJS8DnvoPfJe5+hpl7W+ae8nXXtLVPk0BYYT2k1My1Izp4sA/FyBKrESMXkH
Eiu5/r1BhFjtvZ8LSXn5CqHXGThM7FdR2VWuRQujbgcevofug0CN2do9X9tS7mT86ObBb5v+
cdvoUN3lJR3t6dvsVIQOl4HghkeVFgodzebNwjS3r6eOWeue3uGaOVyvtiLn5iIn4F3zwCEs
VNONXMKuNttZdnTBoiGXb/7NUvyPv/RHKgl31ne7WHBhZbT5gZLLCyIqCxfQ1d5U6dnOyIez
2C3on4Z2yQ7DvQuHHsysN58fchu68ra9EXEhMKAxH+NaLWV+YOJ6SsgMvoQ/xjHbgsSTs/mX
jX6lE/6+aH59sDL76AGc5vGGV2w6cCwc9GzZOFtoAl2u1O533B503G7KML8cYVbO7mg8XO2q
v+E4wOyr6kAv/jxPkC1ZV2luMtl576Ni9eHig+hMvM0Grqgl1OpajmpLNlboR+mTK5+yQVak
61j86ZYkv0cjyo2+wWgUSLf5GU8NVmMj3d+JTH62UkIEmTWkXSSqbg8eaH0P6weBv3nAhhGM
kX204yS7sZopMspJM4x7n/URspcxwrhi6w64V6Fj/nSD2YvYMrsrRzmJcHeZBroIeI33xnVq
uhntOdpdMTiNs7u5YdaVYILl9tvDZR9E5b9/ZfGJZhtENu/EEf5Sq0XpcMmVjKez62aHk6s2
0E6J4Ajk5mdmSk6aHTxzD3q6u3vxTPPm5Ztffyhbv6qsHiLOpxFXAn12PmE7lbf9tKwbnm++
G0dIRNz/kttGgc4YiD6tGW/r29RgRt/OzQAj450YVfMVUiv6jMcedr576yrC2yOk9yky0lyv
Doroa2O5KjsQQV1mr57dnr0uDVYcwzkvMGAl6BDSgRNrFPYppEU+NT0ZsTY22KfWW+U/pPGA
7uicGI09n43W29hGxI7Y/U5/vshvDhMRexKOYNcgplVy8Gkh3i/ZLoKsp0wuILqEfBHtd+zy
29jjBvgrBoyxhg2SpIG+4udfvS3bNK3wMCOvw6Pi7t92Wb+rOvI+6/8fwPsbd23WbNKKaUof
EyAupGRbd66JYwvZZgPoyHrRhsX90BXPhUxn9WMumzEDXVtY5IgvWZH6LZFDeJn7TH3L9eRC
bi0elR5SIv7B2/2R9WWpqQy/Ala/+amD3/0XWfoYukiI7RW/7kvAjV9b2lPm2Zj0z292Guro
cru2iRrVgBkjQLIL//4D0UBqBSjYsGqXPbM1y4fk3deQdjBfGAfz9ls1vYdznwdlUC8IWPIA
joixzU+o3qiQT39EEDvflGar7TCZ3ktNKaqPpg/ISr/X5oPA3+7HfAAgyvPL4o4srftR21Pr
vp8loUFmO5W25p++Vont6CgeFnPtyf1T+1uSLUNfYxlwrLq+cvUCLXDTOLjiArJRCfpzYNIH
UfYHqPwdp0o+/GRMn891BFewFtfWRHF3b/gSGwoM2N4tKV7YD754qdeHcdFhRJgVzdScqWRV
CXbf7mIEHmPIRGyZzT5ELH0okxrDzXY5VnhkqNvGLdmPf9l6H5bydZhGHe/cactiBflAj6YN
VL6ldUFOwJzRagghhMVCQ87J33sz7S58odOIXONH2mxAHEvPhz/Yi77g9rqQlCQIOb8+8ktz
+KGTc68qedy4sPUrxaEvUk2KQHT9+9EQE0Txm14v8MI6KTUk9g1o+LBhWsPZIByUt22vc2WS
uRVHkDSPXLtiJoe069lYun3nl4T+1r9+8wJ54Bt+ZwemrPujm8074WTXbxfa3mDDNtJrHwYo
Ce/49R1XZkqpDMcf/fp1ny48As248izTr2PR5U7A7125fysD/+v1kjyI29Hdhidqb9bNLtXD
i36a9uVHoNOWgp+fJ9n58LcnwcMsMW5YJy3/qwzOyVt29zj3Y79SGsfyLFBzUU67vLQV61LF
u1UfTDchXtLcV5bEpYaOPrx26ZfNxcGr14k8OP66EeFHLy/bK7Ye1D611mpANK/109flzbFK
x9QOfBXmzzLasjAgDblvcyRcFt/0fuZPB65EnG9My5ji7xyVoTUcpryP9sAlPmWwLyjyp1dC
Z5wN7X5f1Wnq2RLeBPdeBmgA7b21Jcx0ubY2wt5U6H/UcHLuYqZd+gv6il50oTpvpCfxMRLQ
H19kUO6KDlNQfx/tB8C/WbX8vNE1P/r+A90lnr9V7BxdQF3YLO67fx87k7weK2G+dE68uObe
FfbEq3vGsdKROhFWeXvD1iq7rGQ0Ar4u9urOB5D0R6h66Of5rGIOQS7BpVz2nYhudahnG8mz
HBx8FyzJs/esl3g4e7nUPr9DpbsFg18t9p7bYFiXA9HRvCGyCPODV0vnxiS0XqqbYIq01H7h
zC/FI9qTm+z19cv2pteFGpWZMLKhGtoppxDixXnoPP8whpmnNd2WmO2a/qKt4yXrVG78WRT6
04uGyyufFaKF2cX23Wh6H5u1p6sizsviTq5S1BW9fmGGLtolq/bixtTKx8nR2G1aqZSHfrYA
KfrDDLkOD9uphJtVZmaNa/mYkFUuMPda0uMVAHVeA7kVcbGDB+68j/cD4CNbcIscBywyynMj
7vKNn/9xy49RfQm69wv8qkz0aFHNAxuysC2piyTGLnbkRMVrLX2jPOwSgqon4FXoaWQqXSlT
0LcbRIkH/F6y/jEd/29LDk3P+z3rQd41OeqSE2cih+i+YFcuF8Rj6OxBzUZuuZ/U/2qTVeqX
HYHl2eZTVpe51uVW1yKdzecmbwzf+FDKf20UihxZDe40iFTqPR4Gj8HpMwL9l83LO0B155eg
/q0/nfrBwcZuXcZBuLiufvvqzPsfZsQVk10W5yZyk/QgYxs7+eqf6bvar/4wSK009Fu/QB0U
KwgzZUduMCtTtgGLlhu71rZv+a6yGEKvF7sRxrUHdINLUFtff/V74zh/szV+n6j7df3hlJ35
xXIL4Tu59TnQzLuTe/PHONbbl1RW77loKvjd27aAM4uair98o7ej7ssv7DOTFkYZnjt19X1+
/3+A3zRU1oF3P38soWDQFQNHUX7WhW9a2Dup3CbUka/qFCQbl8vVKjRWXcWNVxjevugAqHJ/
VWljt4lav6t86UP5/7UdWeRjQ0YWzJ2ZNwcP+Ia0QwuZjXbCwUwQXJBRFYS2ea3aru4wcVSW
WxQfhL7Nw8XuSLQRq7guBctDyFteruTJraXbP75Hj/E7kWxQUUbjhkRzQEaidLcTuTrc3UIe
VlxvNV9LVCOaUTwYVODifgXjP/GOmnjnxUjI8+KPIgK4dtbEIdMCGWl71CS/PjtUsM/4xnto
PwD8zYriwdjoHyYYZaGdzYOtGLjzxRyEph59EoXl5KcGEhvtblyTb8kJXnCtsERg2JKWSEnF
uwsfQMYfoqr8PUaobZHhI83pTLDZtF33W11f4QYg0NzFPZIQvvyej8CdhtI1SBxGnWB3Oyya
AT61xjDn6yGbHv+X48Z/z+2vLnyHwuYDqxZvBhMSt8dfouXKApA5bg7MjlHIbTcScKEL6gCY
2H85OmZxgJOHCip25urMBEiNCTN9vhMpI7g17ylzxH4R77qDzcaiMCXJycJYl7lvKTu1kRzR
cPEhYVCjg+dEfBLR4Fk42Ky4hfWaYIcvRf8Eeo25fPODGfoLy/s8QW2rX4bbBWq8EznefkH2
Hwtif4OpF7b8nUhvYNDspl6kfX4LOmnvo01kT6DDfZ93IirC7F93/nHrP2aJPK0315JEED6w
elrBQQdcdvrCsPDBTnRaXFwLSezhmkXf+YpmLTUfKc826MxQ3C2H+Zbc9fMo4VO0gI1PBz6U
5V/1Gu4HGo8EqHWN8o4Se22afY274zJ15v4Pd28e1fTV9Y8iKjhCkUlRwIoFBQGReQpaBawM
KUKIAgELyhAkyAwJk1IHQEgpVWRWqAECJCLEEAIEGUVmQxgSCPNMCHMY442/99670j5rtaFr
3fs+ln/cMfu7z97ne3KGfT57b2DWrD1Reht5CUg6yXBEIt4V1jVuF0qhXY1O0VKvf8pjTtf5
eKqWhwmt+8mMRgVxv55dTgDEPdg8MhNwcvq43/uiZ/cJakEqhpDyhMQEaL0/hX1k9sO5g1HJ
yNwhl+mjSaeIx2xzK2C5S5wAX1FOLSrDwZ1a9z/8vC+1TsqvIAhsnmVyciww7umcJjnVsMI+
QmLLy3ql6MJBAW5b/pkq/2VP6fmlPZXSlLEufY+EGA7HJRY4sbyGHQiyrr8Yk4yf5hW3aI3X
pyaKjd4175lHrMuj/eblFfqQBwd+4Y7h5c2mv/K78An8uhJBtSpd12/qcnWr7OqDuxZKk4gp
CwakyxtMxu7cMllYUzLieAyCM8zOfMJ5adtmcdTxLejHgb1d2v035/drc2ux5/TKC5qGex9l
yo7x9GZWXIT70O1+4uBqbBJjoLHYJmjFVZlWPGfOb0u40kcu17UfMhkkJOmCsYzDinTjqYwl
yOaNTjui+nLoHXHWxklGFbds3mmeHYNGipwgUiiaE54Ssjd0I5yMCPGj1aTNTsZg78wkp7xu
Ay9dU/NVbd5cfvD+Je/Nfx2ch0SRdsKjOffTjGmGqHAlhqHT7pKQz3yaNUTTEf5jG5c9/T0c
Rqd6NMGDrcX4FXNFlwlOdTgSjV7E2Q75V+3Qxr+8H+HTZGVuv/aGL3rWxclMhPdQ98LLAzPo
Dsd/czXtbdgTvGzWH/SmdIwUCPZuDojLt3xtwyki/VtdE85YjXmnGzAof5FbGxFIt+RdR3TD
fu3XT90XbGcoy+WpdBzIRLNJY7NzIPPecdlPQf4jczLX3mFSoZ/5nlbgNZXBZh+Y4JAsQhMh
0UL9M19TI542GSgwxC2Wd5rXHd2uaibkerqw6wy1PyBYY2rD1damrVCCAQJHvNn33ZT964HO
kOGem1p5TJNUZP4YZEOsNTURZvSReFWhnXdlvg7OXUvQ4N+gUjDHvT70NA6spRm+AFKX/fmb
/WRh+TTLkFIXX06oOoTihcBN3fRv6H2x9/5O7frrAagGU/TS12c9Ok5yuW2t7unjrvco0cE0
35KTCyFn7v0+6TPalib9E/YeU++IxoUNOdNloPVkBvVJLSERWLyw1mlatn+SWyGB6IBfqSFS
rLM9enOanIKgo12zVa0km4aQWO1zA/UvkPZLZqsVg7e2RbQDnraKLMj+RDZKdd9EyoIx+uE5
6hLK1qv3oHt+jeQWyTPN8+ij9JEn6J/WXYbHs5F+dfT6nrKVJhCcUr+XKRDGrooGxMG9jvXR
3G5TgCHk1cDsRPMNsu7Rd5WU3j30f6YZzyb8LzBiHytlKD1Kv7QamChdaJXjIzD+0DyEGNwc
+yIBuO7D9yZ4pzr95aLLJz43mC763jLreNAl8qnUwHef+cRyvNbdSqyQtq9sxcNXyqb3/nyR
q8ldmPTLqw8RtF/Zih4S6BTP2o7JrlO5yHMmQsYFZdn9qDqrWfOoixtysPX3I5IiWifIACHc
u1koXTJv6Kcxa5hc74uWZNZp0T/gdLnE/w3Jq39O8MoSJb8jyzesrpw6M+883tNUw1z2rr35
hOU6ccuEeaVfgsH+KahyKJ6tKujaV5PfNY+dcO6WdZF5aV71Nyp8fV8fWL9N8f5+2sl3dOtO
hVF8IriQmqLJ/swH3XVrx9P3Xx5G+ZTG2lSUW0WWZmoPm13KSg2RCpyo63tueHXZeDNQnbiJ
V2nefPnG0nDzpq3yaA9GEQ9/QjC2miar0U/LcHf7Uaz46kPMyXl88KzS9pbjaLvm4VOV5C9u
k24oAsga/FkmcbNYzssvH+dPg2S1jpFxFgqnXBGBWWpKjTm9TD+pPsTLjMh/9qJ43rBpWqO1
IDfSnvrIVRE0QHD/WCs1QHA6WLQaGfjihcDv/tpVWeOEemlLj7XZUAuhWo5jVKkFHb7C9/zk
P1Psv/gp8YUJxbJg77bxjS5lskaoBd1Wsy0OqQof77JpIzndu6GzU93/8kDKt09nRuSdT4mM
N1uxBy/WTdB6l5o38AL5KyaF6VzbxiotaSjdHzaW6nubKeOw5lTm523cV2HtNrmuq9mQ4k15
DIVFJA3tfhvJpdQuR055c+BevWh3qhYSdLSH6B2z4g7AaTiHWucfGY14gM7d+3MVFz/vJO9e
jk+tmA2KFFg+BXUYtJru4vRpPg+ZkQKzYNNXojPvSau2M79PC0uvS2+hItym4baC7Ww8LsFp
8+rpf51vjW8PX8Dl2nzRjPDvgvAaZM5PqwTo/Wv0pyL95oiwIdPS/QvtxZMUDQsj6ywEOSkW
ugXEineIh38TttNX9Ncro8i33cIwF2cmQHRuWpl8TOp5EnoKr8gYS1HD9BDMEYlJTqSTfa3J
x5FyvoumNYj1pOE5k8OFly3RLisaN9o+ZFEAY7nvDmdzj5W9YRuPp7rXQtrcRC6UGB08slJo
L2hfT7QwJDpVRCMTteW6t7rKyivLrypsXuv0wcWpCtvWcCpXtzTgEzlYqtMdEDWQOtN89zS3
TJ5p3ociEoMjaHQ0yXyqnSeCgsKG+xgzdXrh/sD+i4ZhYucns5+3jGSKLHTj642TM1+ZCIg1
DJw+coRnPb4WRv7D8Gr3ZY+0wb4WVAY53ytO+0Leyrg8I4O98oJ1/3wfwRMcpKAaer5Pe7Ou
xdp1kvCMtbQGPu8FNnK91BO5QyuVOmoL+kLDs2ixegxrCZ+1xgRII2M8RjN5vrLzQfXgn6Tx
65VRvfpCMfyzkG6tLF+N/v7JA0qMMRTdRHpjGunsJoWE72peduzTxlmC8QKPExNGFIzpNwNn
O7bj6/oc7BNkGI0VgEnteW6x36R2BcG2ro1nGncxnFskcBXpj+HEivIkVfvGj7gv7pIzqG7C
+f3XR1k+1mUE2yEV3GTyB4Jj26cCRyIIMk7s8snFBbqGRQj1Q9hP9CO5RfNM8wrt51cvG/Qs
cZmfebjp6smwDcdlZoptLCCd+0UBE1kuA4Iey4h290+6hrhca9MoPfpEZ/F0ZkaKc5dRBEJG
rk+AybNCXw3jQwwuWLJgSbdk5Rie2mpZV4e3cKzwd5sItpoz5qTCTWw105TSdLwefCnRGDIc
l/56BPGuaBJn5BoZtNP7wQMzPn7khfJtPE72kefemIt/6iKBVwH2tNWAyh+C4gOaABfmotN/
n5ZAmIag8lqLnfM2mlY2098XbAtp723dcqTi37p6NdRCLss0r2dFYCaJNgijF7Wb3+wHcQvd
YxtQT0tyzRCBzehUMMh6HN8DogsddtC3RX12lQQYjboDt4LpSzFPb17m7+fklwm61Ebxp21P
MzUounhvsvlnvpAEU+9XPcdDuaXyTPN8ihWD+L6dxF4f7NoD5OR2wdJfbIhT7ouwjhwumHKJ
szSSM9AnmgemxZa1UCufboGachjWfLR/eHfCs/L//zOKyHWLXstqXRwC4MW2Ah2T0cPNGwvQ
OUMr2QkOtnHCv4niPXMifr5BQR7R7Sl7vW6JjWp9/QyKXHT//fjFHarLX9bnsLzlbeTFMB1K
ee/8y58e30UOHXOXYKme3XL4hLmRSj6uD/qIh52dR+W/U5up8C6BFw/RcvAde+z9HbunySFZ
fVLfNedltRYV+07FQraSVO2a6jDJq85PiJwKUn8Ac0mJdPl53Z45UeBeNq4c47kWVX5+8YJS
pqGEisvt3gx6S9PzW0e7r8S1xCa9lzl5l6piravnOJ1tTTCNOGf1LBraLzrXKh2+/MD0T/ry
+JHnE8q3NYXvKibjdWeli+kRBVrpN7crgDNPmzojivkvr+/uOEPbSr2XyR9jcJSIZ4yvbuhK
KpHU51rogzu+P+JR8f9FNhHPbgUzUpDZ4Dje2OjFyG3PUk5ERP5vQyBgD+6G1vHfu/JMXjWa
dNVy0FIoKPydstWM+bgDkUYnyqxp7/Q3ujeglDC1Rg+nUZE1mg/qTv7J7N2D3ctPvd6/guoJ
3RFxBLyORhxhqI+nqFhpUGSWP5xUR8VjI6B+TTXEm7i+uoV1vfjkRBg2Lhk9LmBc5kWRxazJ
AB1PSvBzSxV4u3KGuq5f/Gu4/OBQhwV4/s2C5jVXFxJUze+uE8FokNHHev87RJjlCJAVCc4u
msacYhdmDUJLrGc6osPH0Dl9aVTDebNSbpE807x6ZPacDkhtzVZNlZaTSSG2SjSSZ0HL8r5L
KmH5v+y/NaYqcY9wc5CtaTsek9eTcohi3uARk8Pf3AwkXhDq5lmXr4Vxl3T63WWqyuJ2ES4k
Z6QIH6fTASiBVDdy3AMy87rxsSGstwRw340kWLDVw8riQioyPavghNRmWACorezw5g6t3AWB
qcDDtTPfrWbPt9wq+o/lnr+iFyB8EI4Egz5gBSUvjig8XVozLDrbpd/Awtllwl/euMLd4FHB
8/ZgudB52Sc0VVF8lmZ/Tr5Hl7wLyRPvo2J1ZXVDHHRk392p/UQvr1bf8xqIRDXbKRo1I9G7
cQIdc6Z584bv/k/c4nimeT+83Afkl/W3gNNbxqIcgFHZg1NHOZtX53vnBhYR+FHRZzVxMnEV
NS3Yl/bZ73PMO+69mcrpig08k43vEfiDoTxr9t/MuPsKvGkSH2B5fXl2JmzT43gTsBk7Ba1v
Kl5lXj+knQXAGs8d8hG+FFOpL+xHbU4Jc6+INhYxGleg7zy4EYOXNDQ63kZDWK25vrnx+597
ZReftKWG2aZbhsq3fUWu48rHkjT6zaTG1AdbrP12y0A5QSTbBQ7x7IoL+xk0uy6tMVqK7Ug1
5+hLuVfgSkUbkI1pPhB1mbEfhbjHr2Ccv7VvTGG3uYXmldrajTcH1n3jfJl7OFeHvVIyXgHg
INMBycDCj8QQV2K3ytSS+lz/4oP3g39WjafPvOKUxZenL4WPE9q0Rc/W59Q7YH+squVkp4Bm
75bqNP2CjDpFKfOyz6KIUFPOxjgDft7dzFPrXxOTQHbAjffZqgnbSwkcZNRBVY7Z7cmdPowv
yCiXSbdnTp/54o6CHJJzPvMpYMjAiNPAzSFxYN9m+x93/TyY/Lczm3jZJ8ZmWYQ6wtMp+3hV
A2UVdi544PrYpm6ITbdMsxUoM3zXGYPncwePZ/5WKQJ9rhrck+3u8QJEGShvafYU68GWb7Cl
0cSoMm5dOLd3blkTu8seMA+Hh+pNt69FmUyjThlUYEbtOaWsDJ8QRWQGz8mKclJYi9IVmo4I
t3M/zCvN8zm40sCLsK47rUY4j7HWNHESrzzdDMyXWJHyISI6+d9X8dre18PXpfJ6A9TvksA+
43xzXSm4LBzMehdwzh4XFnNaCtzOuo7qWh/GJAyF+Pqnq8vLdceCsdZbnPNv0k43ceJdwxM5
IyGb3lCjQ10HxSL/3EOnSBitfpKt0b6gO2nhq17ggqleyTAo+qnZ8zxWbgVgUMvo97lhTiCl
AhUekJoAaRG04gRSdgyUkyE38b6nFDb7YgzXBAa5xfLv1yv1Uv0woUulY+kIWJykGSVLoUXm
MPL7EMO+HzI5uUHM3h/uddwerHw/IHk2xbNP38WMooQKXaZESPQ3RnPS5F9Vv/VnNXn5zPtg
u5F0hlL2opc4ka0dX0KZrUNEfeab+xciovh2/75OJU91rpsMr2rasGK04rMT5qjFoA+bkSZA
4xObXYSk/o3boPV4y/rGChv4Cq2tOoaTsPW+xkVe+puLR6mwrg1Yv7RK7ww/ViBxluub/yHd
TW/2ExLyfYuzPIPfnSI9QTQIsY3DCznnzDt2meFjgbeOTlxJb4x7VsXxe5ScIYgmoGAfA5R+
41SQO6YT6EUGzA6DmfwmkVxydwmHwd4903FwGKrfiN9eiSMkvAYWbnskaod95psZKDnMmuot
m/NWMQu+iaajPLCSPxB/X01eXK1urIgFkiyecPIJFL3kEsczyesxYW8owX4Bwcq1bOusvGkZ
9I3KjAggnL13M1nNaDToj9l0eG77v5pxFyWty7mvZSwidu25V0uQyqxheMpZpAFlAcByZ23y
f7ehMWEd3YLJdnYrGZ9t+b427NjTNLPMugewqh2aBbaPzciMm2BU5G6p3zj3n5Uru4Reb3oq
+Pv+UFturm8F2Tp3V/oap5h6Xrasvgyj9zPfXuMqD6fL/W2x0SSdvGIlgkgCekoKlseJe7yZ
LbEyE9BG0P2NM9Ge51bLJMmekWPidqj0TmV5pUQCZnxKbWwxsKkBxdwUC/slEGgK6Q665/vY
Ni5QXu7uXLqpOZ4eugw2TsN85oM8s0H8eniUWxrPNK8eEmFbi2mfBcwoyDCLIg4G1JreAy+h
bJV10xbvVVOsBt5/6JzbLPFIDmCfObfT9YNnXf/3GA95RsMhehNC2o6xIIAYVEo+8FwDVvIc
GOj9dp/+1KWC1uTWrvbq6EzWAJAyP4Fvf1+BWPsFyL3/5kX3v3EX80l7N6P6SURC4HB4d12W
4geKVnhRrLO8PtvTUboneyvv928+83WM+PR26JLWkn1LUYXvcThlvT7gNBqVr2uY3VefzNql
+wdFPoVjUy3jGhrrA4vA4Zv2Ph4pOMMcCga9YFA57rAd6c+63E8JUrrjA74NEpVYrrA2p3i1
RRjetMXa5dOfXjNc25MW+Qd5PH7g8YQgoFsbx4HaPUbk2KGxAhrbkvqKbl0x58BfoHbaU5ez
KXlLhGI/F5KXwm5wcwa9ZNCxeOuewr8tEwanT2UK8sVGh+n1aP06WoAVoLbhFpiFMrHQ+fLj
Y1hTFUl5VJbnp8UpZNne+1U8voP/h+3v5jpOwXFqaw3pYfgLNN24rBAsOk22Ccx8d4DtP/6R
UBIyM4SrsI0ugre+zvXAu+e3WdBKdXXYh7ZlD1RWvfnDD0BzKVeInB2y6FEXdooDF904bFfy
BS6q9G5xZLZnD9z/Wj/4XukQ6R3YY8GukpJtnczkpIHxZdijDDN6n3EynMT/Pxrv6F9e5zeh
wvF8lXHBcyccm4v9qohuzp4rNLThtWxgBfULrs4x7obG2JJn7m3zoDTl1Fwn5Cv1hGjvtSqL
wR1p83UwY5POLphUTx8s1mh7Rr5PUnVfkIHRpWmlHbJjqzvfV/zdAOOvPAoQqJ+2gPajc6Tq
kfVt4nSANi5Gs03ApSdFv6Ho5B9hfGpC5xl6QRP7td/VY0lRpe/GX78GejCMUkcccKMb89+7
/RBG8YMt5bxbRp9NzvbzsMM880Wsnzpbl6+o/5kvLNYcoc6XcfKfvAde9/5TgMCAA/6tVqUV
iSBIVsWrPJdN/F0KDDArkthhxr9Cv8MKzxFjFccVvb1LAeCC1OdRmUWwlxb/wlWTD/s8HZou
l/dI88ka9d7alLFMrTW2Niz3/4sxlH5xgXlXCLEWl5xtfrOxtmsel6oZuMgJByxdd5Ts7ps7
uLunwlu+rjwWFGwDyVJCuVCi4+eFb3ENBOHGJy8YAA9OSvU782vfdR53d5cYLqs85SNUUWg4
0TTY34jldw17QlD/j6yWXDL+guT1btRT8vq2LadqJAdcemF261kzxEhyk0Z9royurPM9rDSJ
QJGDQhfAN+ZDS6mWyXGiM8a0bjRb3nDQ7MlfNP61foVFSjJam6Z1S/1UQRoborF+6KDM6ykr
Vz8gixx27rP5uyPkrr0Vjqst6YJpodu2/ZztUyPev8VydGvFpsNRNQIhIde3p3Fxm6DqrbL7
3kDQ7QZPatenT5oHi9QHcEH3GGAbxMpV9XnungaTUq5iH4Rd0n5OkpG2zlrgp0+h5NrWMcbl
a08+8x0c3Rs17OxSDgz+JTyS+zEeaR6Pibtyt0FLZ+tHEWE3kxm6IXaGLzbUpZ4bRjw5/NOk
m3MoQGO0RZQqB6OhMHTgZz61ZGQR37NbPKrwFbHtclLJejfHoIesJUUIhR58F2B+guY3A3aU
0OzJDMcMvrmjaWxTZzX+gsm306Srf7u+ndigMWIWdGg122P00MNgTzCqFp6+4DvXl8x6O0KP
vGoKbOkwmRtteihVKG5eF3dAg6SKfQwfP7edytdzkbuLL7Js4/L9vP1yCJp26OQc3yk92/wr
wJRTaVAfNzyrBwcsvrC/aHBuJidsHnnbO0Z/Tf8xzKOsIAipOr7WNRcSXn4sklscrzSv4YBS
2l2qdnGqvymed60kF8AqtA/Idc97DZBoWw0R96T9Og7+gGo7qJOEWQM4VLyPjtaEL7hJQRns
8LD5H37kVZeviC/SMS84yCdkfFi56bdgjTtW2XS8kSGwtuCaa3hZSsUgUKu7LceGpmeSYwEZ
Ud0t8wWZSUNhq4V22Bd/59nn20eYiXt5m96+drnMiywjJ6x6k8wE0ZqG6NlHiD7MG6VC21Nn
S+/OODz36tei+IDsBLDoqW450geKrcVNw4rZFLd+gdFIrn7nP84B1MX2hAb2IOrdlqTtPVrT
zQO3HVUg09OZCBVk8JHvPshP48pDtIYAhVDsgbQwkve1ZPbMgbIFecPNI0KfuUTxTvKY1Z4f
AO++bQ08R7ssSno+vllHEFk+S17KXngpFKOzTG7SYjYxxgiVbwubtw/4bx3bunf1PO8qfDWc
UZZvUu7onBiCfIxBWL5+p9GXl+noDKOyz4iKNKGwtoNjS4+kVsK2lM04OMyAoCUWIcqVM+z+
ENvOg61/N+3tvqhH9pD0C3Gi2b1OC8H4MxjR2p7IdX3QkKu1utH3ngs+c1U69OiyitS+Cu8w
gZTs+iGmfvIz6+k67Tc+HqiwTXFEVcI33IoYMx0g+MQEvM4PREYtXHa3NpjsDfQ+1x1O12wK
d3KRYlYKLU9Jl53z3HoxmQL6kpLR057iT/ySkhEU0QHJ2exDc8byBLdIXmle11qpfm9N6N35
/Edlkg/HmvqOhfgAsRI+5TKf+SZGBgSd/f07ss3GhMb9rWnD9bOdxRwIqADdMP4z3zigSvs3
XpX5ivi+T7LzVPNMKcT7yo0RhQUIq2GymbIPdp0tz7hjnfzxsSDW2nA4HZlFZbnX4K5sf9gp
FPZv577DV6fzX9t3EmQHbmrS5vPJvv5PieGW26iAEwhrI/vAl1DmZS9bj8YRiceQ9ReYuIMq
FELm6cA0qidabnLNdjjsyZ6CSK7u3v39RgtjK93+maGcbT1O3CS6/I0vljJNdi2/m28UFNiu
Fh59PKYeuEfnfskURn41tSy30zOH9PxsYy0Olsxyk8AGH9lxfMeX5nn0l+0BBTSTAJJ7i7II
DJFSDIhzYcwOugKkCbQu59bkSCZsx4XLlYyNeUrmTDZDb4qFn9Qa5DLu30Je7rYvPJVqcGuo
lTS47qdF2dLN747VBYFpWxysgwB7eaXrbLfu+SFLL81gK2/jfGFSR1E4Ixm5dGunQPS/Aa/x
8emZpvcfaB0eE40tC9s4hfbyUr4MOBWOkOoctQaMUqP3uPpbd1/w0f21nxZRX6dDjW8iJYBk
DQNbYaetmNaBzMr9r7jfiUBBgGE707P8Fx8ZujLyOOJAnLbei3WqF1SH4pDfhxf/oMF61UVw
kfVf8POiOBjPbhuZtmZl2noU+SnG5AxwsmXuKYnklscjzevUJ9J/D6cIY8aLTclINrh42GWY
NxRKet/IWeMkEypLV18mlhnJ9anWVSyC1QIOYZne0Jtgj03xKi1/HvX4mtiMhR0K7Nw71zRT
aU2B9RVQt0kr20NsgyjPjZt0FPPUlm6WQpNrhWv0arjSHcpaFXV+R8aFm68uftDUtplObdRK
zB+fZAXnJSbYHp4usDRReZyKkFnh1JlKDTqDU4MYjjTahN5dn0qOjt6jM9dCe+Vd6RsQt/Lu
7fSHDryw6AVNL8B24DReWw07jYPgHMg2xjasrDK3klpz+Mu3+/5DqUP2MUTnrpWh8PlePKMu
EMfY/SNZCRUBstiCM5oRFP5v4JZzZlRJvU1rC7zoIOywti0Z1hahqTHU14hcLMpD+ov+ofCV
0OvxAdP0iGcYFQ//G6ksldlCV6LtVPwSiHp+DnzFtGM+73cR047EG/gcP6f8QQhxcAvUG7LW
NcUcRZf5FqmsVwSjKBG3Re/+h548/AevM6rKCqZTFTLu5O7hBx7XoR2X2labAfsZaSluSkzt
SVk0yyGjfOOqT0A9GOIMaX25fqJraiLr1lw7Dyp8ZSy7JPt9SuBYRoaI58LA+5rWrnsTXUw4
XTmi9qo++fdHeZYR321InAbR/fs9QXUvVlC+8kzvpZd9O+uJUHiLGKRjqbAvfrk7LjAluzsa
dck+HqwjuX09LZBmILb1G9vU6HR43Ge+0O3dk20ik6H6vUZnF55vqR6sDTZSkC5XYTv2/24Y
os8/cJiQSaxuKkuqs9N6t53OX9AmMmwofpT6+ElqpWp1ftV8uRBb+CEYtk1sgw2+/U887xdv
4Isv+cfXfONs5oMytxOybvflV38KqusvBllPpGAdiFFjq66Tf0zyKBzl+KnAs0wi+9UoWfxm
p4+qs0P0koX2mRRXw6k9Ast1FJh76ML8sEo/puWYtqaBUmdbYvX88myKBypiPWPP6srwrlvf
/INxwTPi81vRgncBuqHUqZ4FDt7MdWpVYdJ8dKyPff5Ix0eUcrMMeO3SY3hfh29rTfsZTk2T
ZyaZbuWI7ffUW/9Aqf/yR/j14b2DZL+kfmRe4GIP3eZG9Ibk+bdQtsquJv+bTcSEj5WjnDyh
D4/SmHqxPkslrQJ7IZVl6Jx+AfaODNs9SonQWzJy6dtM3iPgX7q8eq+N5TkY2u6c9lfhGJwm
wDUxFHA1PRs+js2z0Cqc3LJfww+0iPXk2zxFK2xJ2/wJnclfeVxG4VH/Vf9+I0vC0VV/mNqW
WTJSU+czn4R8nQ9bCBp5w2BHiv/fzLzen+0Tn64osMxppS9UJ2dQLQUSHkuz4/emDjTw+5R6
via/mp+BTpaQB8k5k6U6RTIlVs4xiLDI25H/RKX/7md2XyrrGKR/HLP2HqXmVOggZgQYjSu5
aSemAdNll94vm7WhJvhYXUlDIT6s0FFzeIffQZnM4funXu7IqnVNp9byth4WYPzSrnQVQ8M0
9W3qmqzG0Zy/BBZzSsPsoghfJfy+VFPrkRaC89QedoQkZ2p+wFrUz6ORzOHSVWdO9no/cDGW
wVCFNKAVcXk/3WjC24SgUn8ztgIsRyVwa8nBH40WBz102FjYbfNJmWyxre/vAjuuNh5dAe9/
SmczgvQ5GQwgxN8geAuaHz1lWBEVFvxLCLcEHmler07AA3nvQBxEig+AoU4/S0LZsdw/LZzJ
JOyNXLhLjovzlHnBkMhFPVk9pb+bymPTXxObBi3fMZmzDKfGKnow9QKxr2/XcpK/aFDZGtKC
7QO2BMSlEYHHagABecfoJGAhfeXYb230k0didmSicCJoa6Z5G+k3d/ubY59GyL01Rv3Y+0uX
Yv4y0JGPb9d+Q9flfHiElpSJFzEsx7r3xjFtRcYiiPws2XPOy3p1l1L571By4SKuWvkacQk+
1pKYRQ4cbQtBjx0NzMW4Ta7ZfNC/za3pNxaUNk8yfr2lKwDq7Byk8vj19LOgTAOyW3slkN21
S8PgUN+KN2z/PCeiESwq7kmzv9Y5Hb1US6/F+yK276lHcsvikeZ1Kjyw7gcc9Ka/Ot5gseiQ
ox9B7Rg32N46uLqAMvow+2+EgPLxaZqhLTKlP5COKM4jWtAl0JGSCDZNSIGT3sZa7/gdsgm2
3kCGbd9DFZ9EvjK+WbQ2v/8Wj53+P2yCjWh2wHh4A4F1Yd+hKZ+p2aHMue6q9Zd1On8VPsZ5
NlqmNOVwWthYdVibhYhkwGF1UBUaa+vRQERC1OYsLRzXtLVRjoRE7OKlGoO0piLIrL3Uo0Or
K2eKckdpeJmxMneB9kguTfmPw6lexJ604J7UMo7v29ojFIjSDzEwuNu0QgGsgmTmT1v/4tXm
GeTrXe1l2xIuraW1UnjBbbNAb6YObdhYpDa3m8QtjkvyX5E8b++UxvLtcq5P/5TsHK6XhtFz
yO6Nwa0jq/+lY46W65gshf9uy7YuJVR1t0mOAn5GVwLDPqkhmSX/WqKUwEn0X704ymi+m0En
xTTGRMRvnnxx/q/6+T++C03BTji6zSIy/U5GtibJZLQeYzNChVMOWf81PJRvX9dMyDvlOxw/
MLHVneln1qcLv6MJ7xxzCW5EBnHSL1bNqsTrP58jfNQyecaBc3rD+k0t/w+c01NWgdR9m8Lc
HVLFpcwuiTBfDYPUlCBB1ndEq2E15kywdv6KM/G3oW6Y4Qz4UpGh/ApNj/TdcTAQ5wCyjc6b
7pE8ZWQNupl0QR/BKThddninzv0vjfOKd8HGt6HHCZ3Z1xqLZGSzgmne8uFJw6Ngm82Ok2/u
cVnxbyF3o0Jaa5+2Xl8jccJGo4o1PUk34yARMfsqJvPhZbrZ/VoGujEqd8/1poT98KJTg01m
mm8OpkTuyPp/Ou4OH58Rf+fZHfJ9NijLVQ4GK9S/jsXnW/g71TGMLleaI9qF3k1GESabhpJE
A2+DFjYcKx6iOVvQZ0hQKVvw5K9/OKubdtsVKnUYFDMs7GLVIcH6A1Ix6CfrB4PO++k3b3QM
WV/hAKmWl3+keA2MNYS409Urmg1nEKc8mIsakPe1T1j61PzZB99X7cjs/8PM+2Q30TjmzxR6
qS9nta7TQk+W+g2IHaTAP/NFLCIevI/cecv/9U8IocerOwfGPJ/a5nHSnxZGlRocRRq01W5u
3xcNO/Y2WzbV8Hpzm/eV2YrvO8Nkem8EsE/K7wwULiufv96dvCkz0ccJrn7dkFP8KILotHs8
SuyvA3z4dt8oS3I/ph/7q4r80LCVOKS+7n1b/MJ4tuyPDRW+4W9j3r+GCAftTfNaqoPkg3wk
A6QVzDvPci5GPBoq4DGckGp02LzZL9zdr3kQPYd0sx5Fhrj2Z8kXKuhfbcarT4N0V++yWFhz
xMsuzCNqxXShT+wlQrgrRdz95nMvOAWY7UEAE8WoSN9dihe5pfFI84hzEHw4kwClBLm1GKvb
bP5yYMu/uf4pJrjUCcqZDRLzHDZa1BWxdXsfRPLY6tfEdjToWElPV7BRZUlITvVTBi5vxBzO
llH+GLHvW/vfA18fNZhwLy0Ge8foyefHicysFo1ExOzhron797b+Y3dJAFBLyqIl6Nmc8pSt
z/j2zKaC/YLWsAGu/6kSzkpkOfRM5JUBkzC71vQWVM7jwNwYHCQ519k+egXKCRHpr5jRRFSl
vuRWz18bcNy3dWqUGWt3Z9MHohXYZZktorZRYNmr0UbQcg6rMpW80l8TIfni8AIue0zqeVu+
HlZ1CwWAGYo1VCQ6le9/zi2NR5rHJVcnvTdZKpDSFbA/oyMuZ9QxeaX8eABwcI+Qf3EtMbHN
SAhD43geulZiuwEPjY68nUIWg05m/uH3xaM+/+1sgrKlai76lzrfoPTrTaRnrGVID680DO3Z
t0wggjDwYA9q3hNOXW7xsKPpcuqNzNU9O8Se7B7qdt6aTPnZuUUE0Y4PdegW1ahz3LPKpHXO
Haibpx2PDknttmwYZAPGScT8hQHRQgb6gmJnDg49zox+GtESDpI0UBVckZGMULjni3DumsE1
HJavn822whFy+4OXof7TnX1Py/yyL7wgHhPxWwIe57ALKa4xD5Iizpyj/2fff3Euz86kyGRn
cZzLdp1qqs59/69zeS98fc8w5tNgphZCLsJnt9NaNP5ezo/1nW9ncL5jWlMVUeEU0oFUfwrY
WxqCWaI1TmR0iJ58Q8/MvQXdCNfKf+3a01zdUmxiomUcm+BLmQGRxa0g4qa/ol3l5eUNEo8I
v+RSR0C4wQJnu8QJFA0ME1WzJeACvLSSkQYWs2bvRvDd/JIbxnNQDRk/jThFNNFypB1nceHF
yniq1TMave4XyyouQbySvF3W7Lq/wLSJE74fatI1/iVaJCd/zHyDrirEgLCrvs3/XSb9WPnI
4GiL4fYufIDBkw3pqayBhcj0b3hV4ivi48T61/m3iI6j9a8qTZGhK3beBg7nFzo0wMd6VxU5
TpDunNEO2kCuxOEd2fRPz+DnM5R9ch6WH6B2aydJaGNS8f5lrh54R1Bbiy/sivkaUSKP6bsS
luVWlZWSU2K+yjiy7+V4dv6AiE7UJCO9CZOZ8DZwu+1Ai93cFbJt0bMrtVdaSuOXnU2f5zLN
u/0aLawgBOZVDUk/hmE/DjYILtc4bGZWUfiTVf5P9WExDIePdQSIf0f4C8wp15jxmE3QeD4+
mCl65OBJX8Kk7LTr0OmpwJlsoUCtKFAMDERHe7XuTUbJh91kTAi6RXJ1z3wFNHY1v8g3Y9kB
5Y42DH7BOIklAWdY74QNt/SqKUS7DzXd6v6IjoEW+JyKiao3htAjcZDreV5JHlcAPU4N6wTP
ZzA1CgBT3T3FWt7sWLskln5UbZiludHfiFyrbGgjyMy5ihs93V/Ca9tfE98uJ8sbrumvOrXd
h0J/dvYRmksVGWcMjToU0bYwVW9u7MgUgAV4Cau+athG+OWimxkS6HboM19gpWCLwNm/jDiW
lcAVTtK8rzZ3syQKH76eSglLeXthyc+7w7neEO1SAeojONRpWIuMJSc/iTRV1YTcWn3UkVaR
2qSSiizThMvnawfJv4KW+TfDsxDAJ7gF3GhbYyDGNdYHcNhqxCOjqr3/cbUQDP6zj7CCn3WQ
Tf8xgHr7+maSfYWWf4ue3Eg5+LHYmsSwgQ763I0s11OVC6YeyXtyFrFkwfuhlXBhf+9DCIfv
6e8UUSt68TmxIg8f+irO56XdvZmSh0K7nn1BdOh2sACIq3uTHhxWmLn5evTGuL37jChMTlb9
tssNFDaD4Kl/AYr0VbFnvZfvS5zu9HTIvvf4Qr+VjT1VCqYQke3couVquOkrNMvd1XtDjdR7
t68ZgZzrE+uZrxnQuCCGhRrz6jkZbi4eaR6BJ/6Z+rpF9z9qS2KbV+ffPXrttvVdSu7WLRNT
43NKeN3kfurPpuO2WiogdM4meuXQMWSR8cWU8zyq8FWxiS+2M0LNpyH3keYtInEN+oFbGcDv
9LauNJTv0P/3z/bgnljtrbn54t8gxCtzB3Ls6VLPYjBTx70lZq3hy1eajWdWVl8UuVTH00/U
tliLG4t1a1B6vq2JDq3yu9OGYdf1dqtMl22HEGRkkktKjmvaV9UvbqXRohlqpiHJpHA06kly
MiYl9H15aL5/EG1j7w1EW4q0bRchExgFp1PIqiBL8ZTyYprSKX1QeGgJK2vg/hULdVEQ1e3N
6dSLNKpQZ8e91fHujnv+cQpAnMVT8xMn4OdcRmhITTH7rFMpzobukb580RmlG3ck8JL7NJ/k
jCy+wRV4ZDoqO9SiAduANa3N16uvgqxGPR9RBiq0VW7kgBqSOYEomualWYYfDY4KdHKPFP7K
9Ivn6D0GrAVJ7WsMTzlhSHXX3bbCwDktADgCgy09JwIdkyy0gvexUGXOaLfu6KV/ktqGx5VC
szh3NV/K6HSfdVNKuewx1IgzaxuhVYcZmNiVLf2NxhqhFqMwXSmcJHv5fQPHr9gcM80+c2SZ
25x/C81fqZ81Zmd0vQIozwAIviod4JT8S5pwgaRkhc19Oii4IzP/0U9EWqmlW13f+5nKYajB
tS6fEf3rRAePDYnUgZIJqDjZhpaVt21R5pySj8FeT5GX4wRbX/0+ac+aZn3rq75aaAgVVZSA
kLMiSWVM9xEkXIlSMIMtLxEx1pN51NnYwLvWaqPZJcEa9hj0937BB5saDoR49R7dlHyIgHUJ
aGqQbV29Winj09pZBvi3qoHRBJvmNvdFTqnHKGMNsoi54B0+PjkFjBD9afrj6opuKmKKWvk6
h7VihLnbS2B/FOqb2lXq3kXQqyO7Y6vTBX2h8DCrpWIbWiODebt282X/S+7OuyRru42zfNj6
iIi+Yh5+tQSiZJ3BLiA7q0X0XtLYOtJXVL6m/gb/s3mzJ9HFrLO8aGyLdqS/TbV7tya3FN5o
Xp2Fh62mkwKVF5Vr4W7s6xVSLz7zHR9qGxTIWdZsiMEBLowFLtKKXtozlyluwOEH4EjeGv+6
uMDkVLu83u1LQahXiyKPKwug1gD8Q18Kp7bBWNDeB1U7MWbXIpSUHpJZNBfW/GC3ngMcoeO2
iZsHuKtZ/kX2vH2K05kNFmZxfZ9uzy9dIji6xtZ8zIFN9ax95ktp2b5WlpdGHX6RU72QCD9b
NFjbFnHZWm0MfevI+8YgZaqb0tbe9sA9Lj3p7xNh6Wa+d2gM9YQ8CEp+DCDpPp+L5xT/MMwe
8apdZV4QWuFcNsv2Q+9BSU0CXS1ZnRQd4swRRbTcqHv+bj15t8mgGJf+yNAwUdwBFd+JCo3c
/JEFFm42GmmncmvYWhb+y1V37q74NqowMDYhrvlRWzeqzwQQ/rEojpMsuEm3189pXbvwgbnu
t10MmJCVjnEmtBSdam8GrE5GZjTgJOQNG3Hnhf5B8mSeR7ThdEPq0fLEOaKoYcWxPA8tl8nV
FrzT8G4IXOpWPz5nIel6/lgQ013i7Ab0bBsaW3l9vzm3Yf8WmnMQeN3DfjARGyMxuUZftwsY
UMA6psY6jfC/15qJfT5FkIHmxWT3C+7I/fVPUA4n5Fn9euH1vSnsVcoc2VvQeyrEDgUKALqj
KLEgBw6EwVjj6kmnnMrmjyNI/U1t/cDgbet2aobtHMVXMR8HGmhAlccGeTImYt5umQYvAR+q
AX6YPbgrko9vtyW8eHIZGvoMxsHtMfUs834ftwaUtEIkEJvdnDTBlcvaXRdUJrd+alfKbFbz
9Tdo8hlYCfJoziIVuUZeu8j9nk9FYSwzjSuso1IKNULDtsKCZNBE+PPp92i5rbGL1Lnndj+7
+WrX0BwveGKF5rBIpxCmGnvjDkhkzhoCmLjl9YRbFm80j3t4d+xNZVsNttX8goHKgBjrUXrs
7GrRs6C1l7f6RfzX8O/ZclDOFkXOt4ezRVkrt4OytWcfXK3iTYWvi+uigk2B53PdyWHDgA5q
6vIk60ymI+D0sLU6k3wyIw6bJPWI+slvGFFveTi2A0B6CEveOjm6o474J1eL0yre05h4m9I6
LU4IxS8QX8PGaqLoqv4DpTJlK1glFC8NqjXveLOEziblAZBVSNyF/RhOrwsUr8i3z83JXF3L
jnIhPXYTFNZvlM1raGsggde1fpe63P6Zzx6PrAWcYRCwuBCqSmY6Jy+98/ZH+YhPcgN7iNzv
jV9Hr89da1FHuaa/TYNTgpBl3HcAupItd2TMT4b5Kpsu8FNHNuQDhWDRuTzzmU8ui6l8Wagt
iW1ZcNfsM18A/I13MLc03mgeh67pgB2t6MQbhhKgEME6gkUA25D1gtish09ynqcPPaM1+YWO
0pjLZeFi7POnT/LW8tfFtUd8JZicLZiWbiZ/lrFwmTPtqS8j7NHdCxeTWwWgCYXzZo+pnaAh
k3DKJ9+ssAjhIxQI+8PO8Ff/5FpSry25RYWNb/IWXw61O5W/TpODNOBEp7sd9057bKrzPcmI
t3tdLgRjDoPVxKH2ZlZ12aR8tSAZJhV3Mu3LewoQ1Llh47aYXX9c8pT82Z4NTta4QLo0dWSW
zBczF5v824gfuFRtGovPWlUJKHMhZeS2vscyrE+m/uHluZNuHq7wsxs7ftwary7yco6h/+OX
+3hbX59NIDEBWMFXpXcKdjzEQH7YsjNmGOZBi5W0QmfaXfApdwASJ2+y7p8e/IM8nj7w6C0/
0e9V7DzAvyqUPtAUEdjCHvjhMdzoqYBpRxT/uKyi3rhFm1bgWhvJ9FO9jDgJD7tUWcVT618Z
07dKBXMaN8ZrTIgin/mO9kqF9bIuLHls/XiNeRZ8iqm4dQKtQGJfZGyEMQDN4XyBO+qDf7SL
cB0nu3cF0gt/d8ipztYXYGtazdQFTqPCe046vX4X1icTEhwAi63cW14WEIooWupsTXpmY9pt
bb4ZmfmG0/XOW9bt7v0Oav2bzgwRiFR9VO4tkPlGUZBMmbzRxz0n/dO7ZzoIPdSUMMNNzxRY
YQ6F1pVzYM40qb8hEqjD/eo4gD6TTNsIuVDj1EDUWDDOQ1es1jTkSY5NHee+HgXNvCX1rH3A
Cu9pPyKUoGn6tLGufdED6agMTjXfXt117iK3KN5oHkctJwgFBxR9V2qcFcTJjTvhqQsh2eFj
gQtVTMdfj4o8bgx/mCC2uhyIQ48COxgJWp/5YgXGeVPgK+PiFDF5gXcfR3iMWxgWOvYEP5/K
dEQHHFrPLAKdTKy8Viyn/1v8N/Ro5uDs9oW2NX2xjrWXcy93YqO0bgtJ1h9gt3aYEJyebw1l
Q/JlIj+dz8ecXYZlw+VTtcoX1M1DAz5uhjj3ExOlN/mP8XoSPLC2aA/cTPVbebMcu9Kijprb
ihNyxRo9dHCsY8y1hN2/NcjRM7iPgxoPsMPokx0s1GW/v+TkmBHkfXcOoeMdm3fFjhRX4OaR
5EJKGWs2fxqCxGDfnDvKbZzQrxPepniMb2xdn1KJsZW3+7RuguhMT7F2Vtimz8mnlTF2lSZG
FxCkK7EJR9eJCnKn0GGI58VvhpHwVLzhvMU+blm80TxuF4y1HZqKdA0kiwaajCtqnEh6oeFn
tDJfhz3BfeBU0LoSWrZa5MAZ2L55Wz967ejIwpuW//tc+x7MIHKMMWfutdnOhxL0BFyNIpzq
Ro2d6qMQZf7QhAJfUHV5aX71Ahyy5fiZr2BsAEfb6tHaUejKHuOAkmEMDLbV4yBWVxH4VFrB
jEBQP4vKXQh6e0EF7Nz2UCbiQP9Rlivg0ZUoSBmP/osDa72xdoLXp89Ezyt79PnFhME6O7Cr
mz/+j+fwwBojRcF95WxVbR1h2J1c2mt5uhn+PNthIcC0SIOF9JcQ4u56gcMNYUR90v2ty1Sf
gUocTtNLT5+TiV2rlujduFL1SCZBP4Ye3er4DNXtezY94hJFY1qO1Gihla2Ar4jj1HEOqOIW
xhvNI3id/7Te0IRxy0x1nDbpeX0S2omxMTYjsnVD+zLKNd3PbDTo0dFuxBpoZPqmzFg/UHE0
LGbwOIA3Db4uLv4zemMuxnp4wQubIbCRma7NbeUb6muDNJXn+FOVxqXe5hGNlAKy0Uho49ZJ
avtObPvmLAXxY2dxCI2u09tJkTh/XuNp6NlM2+bBmwR12a2mpLApQZ4jK8A1qXnZjwwvalcW
WQBU0tVDb3bnlMDxKnZNyayZ5L1RVRzF9iLWUxdCFadFyjVTphf8PUKvZN+j2LSlqNzuSFZn
+5X+KYLR1tbwWHB3EawBrmqP7rdalueACFhkN8VCwYzwYxtayTjfpwxToTLoooVmH/ltYWBm
Nv3PmR556w0eZ8zLRvbK1739Dr7VcFyiibraf9yQTZm4Y7119XRsgsM+cghgSN7AmlZDXUv6
zFdd27d1L+jLRuhf97fvzUxSdGC55SE3MnA8EAM7qAlkgeozNbbrLvawE9cTnjWqdBSJDrSn
PMK6hj8OncGxdbR31Al7zge87jmWInk+FfzExsXKJLPsHUWnI1BhBOP6Ex2jUtvQjouQbFp2
6xKIn2+DDGtR6RswfLVDv59owEgwM5pVcpWgW7Jm64lixi74aIZ4gXwV8NOu2B9PZPR2alvm
NCgrgPrBfhe0ZRxnihLywLnBVgl+WgUfoUTtctX4mPFRylDQIovZJwH7o9acYhhW56drJlKj
DRktYk7p8iuiaotWts+i6S6bk2jDKuCjqFyrfHd4YD6Mk2uo2UxXrO1LhUtTmuAXBNWBz3wr
37/PF8xw/M40JuUMSc9iQ96l0Qb02jnoBXuzGul7CWAn8coEm+WxUYguV1T38bptrTZd529s
tfqexa0If6WDQWyqcJ4MMmew2S7HcuS0R8T3ypZFWkrIAk7F06iL3My80bzOyGJ6nxxjyykM
6qlw0Jv5M5kcjz0AW78nb/Ghs9q69SCjNL5/VeWxU/ctav58FJ63tr8yLpM2+wqAynzSow18
1Fh9302d7W3vY3GaEWJCVZMjaJNXH7/buppPqm2h5Q43w/sZLv0MdtBsVEjkTsyEDlhh7C/o
/jLWdL2K1pOACGAoJWIn/WtNHyZAyhRje4oMiWwPKHTepVHUNxUyfuq0iBmv8W+XGm5wKumo
p07+T3FMyP8pjqlEciNVuBoOmgsqp9Rt1zVhDwZsZSZB7VWvNBHHmAus83cp4N5kQReOEfxC
G3WTnOqadPuWrCfRlHcZqck2G0uSqr1MJqdK9y7V0OKZY8ejkmTEZzj5nEi5dwtFFZdZzPXX
wVrQ/NnmqLcXufphl5OMYcPmi4Aj/VLvLBqz0rVjRLAWoBADKRU3cpLMqPGtfxKzweNUfmng
RjnpylIIrC2c/ZAK98p0qWhaYet8N/PcYf+nddiQSTI4fC1V7vsiw63tqapi4OCXe8l/4R/S
Ebd6CmMfCAN7K1csIGEKU2/U3RYuLftbY0lKNMxAK3P2Y8W2PpB98eo3OzFfKHp8Innu+OJE
tUVdAUyagqL1heg5ggoFTZYt1JMykzUsJIZTrQCysaiy3Pm5QMaVkK2KrO+lyyBX2gxDLzxB
uzQVtG1kahzF/kUUMWeZwH7y7hk3dfP0A3oeS5Wv11Sf6eaAhTj5Sam75E/88gUqlHUv9kJM
+Rl8yfKW5Wc+k7rcYjUm7ZegL17Yb7MLnz8Mkn0hjSS4kWLaejt/sh7dBj3tS5nePCb2wHT9
SLfynBAw2CwTRjqg7JXmwEmdZXqcU/DX18t8dyV3Z+xywuQE2wwuNdXSbKwGyb5zSXCDjBCs
WS3abSB5z/ZUSAnUzlU+G+rs/rEItq0uUwAyNw97E3aRWwZPNI+Dm5OcMW2yacLa14XFnFRW
+KFoNqgua2IhMjVc7Kf69GpGek5t4LLK/ZxexkywzrLpoIANT61/ZUz8RhsU8sCzwnwn74SB
NSdBKN8aXMEphhBIL61ggytgfRuzJ65u/Xj1Hs927ZOb7sXADpulVUT8QAl4+rTQ6IdPy012
jpoBwNganKMyMelslkHHEAQ95gcIma/8ebcwGe7hh8+f6il7l/7+IL5I/a5VgvNE3bZiplC/
f50NherLSbpqDvSIH9wwUjqYEcEQD2LV/P6Z75rg5QWjh6m0KAReznlBGFhDXunTcy5IMwiz
FtXzGXcNvzB2o1vFGkZSCMnKi8mSl3c+5XxbV+bwvFJMeVjfZ74EgLjXoRZPFYpakMqKyKDL
T3aLbM8EOKbTLmcEyhgCwlH61uIgtSPSNF7XjSvdDmF6sfaxP0uVWy+s69h1abRhJfI5iKRN
DiKJ9XouoI9tUuoJmSn2JWpMd8m7daLiwCpnkb6ZArtwX/o3RoZww8aek4YotzY0bFNqm1OB
2viGumzoL17eZieovutSQ4xcbHW+xFyRK1Y1JVyRc9XHBP+p0OqlzBvKR+KU0vR7l62oAenF
KDeQkaHGGk16e4ZTvUleKckrcG5ibPOR/fPPfMHE/LsMSa1R83Xn/FLb/MziH/V37knh9QJ8
H/90gm9+2oqPoiLa9UycVEr4z6FXazLoWx8UsF4u9fJ9n4qc9YPTjktsIiSGdzXyPN6+JsaO
+KI1keSPKgDTqIF2faLlh1V96gf81q3zMk8ICU77gpH3B8b0E2VY3jl1T9jnjlzjyTa18DNM
hvbDUM1+BzPKLChC2NN9PaVuRgwsBoKnSkAJw1PJi8agYMChsGORV9j1M271h6Rrwj/ziZSa
4TTjjqyEMUamJN+ev+CTl4xct3/miJqAItblY1zdVqxkLsIi9um99o2u8yh+mOvtEBeHhiTn
tKeiap1piyETHTYgRwPrmeCgs8kr93FlJkW/c3JIyd5oD3AwNNut8oTgonRkW7ugPyuUYgVR
16DImpyWvcV3P74gPD2ud0X7B/Zed9FLsbWQuOoMAXfExBNa9m7vSbvAqChHE5jXAP+TTBFT
qAfSMIACuOaOkkfnlFwxb7tl7K1TcTOIJKrY2nOCQEkv0SqhQJ7GwfMW4JjXprCBZA5ILMY+
81wtGaDlfDbzwAA8V0C7kWkGkPeh32Mxj0E7tbTqSXQGEURbgNfncDLuUXG+ybES04vNEIKo
uswhsrE/RbzKXFi41KjGUXB+cbxuyLW9irYBMIx9ZlEABQC22ySpMDrBcIbo63xKvmwcmtEh
vXmFXxjOo19qX81M9MtWk9YhrYnFVfKKIZg/zHsm9sbKZ77iq/o5v5sQTAobUUn3LcLFJstW
86JsQmcpvqqrLOwX3NZ5zoAwabCvEHgaL3pvwK9FRHNqM1aBX5FztSrl+YIVdlhmXp0dL7UN
bzjTqxcQtumOIFpV5ZAKQWl3kQrEhJP0SO4RdVnQjiG/HX87MBynsVqU/PauCxlQ0XSzNxHc
Q7x4uuFXZbs4z98sRVzt86tjEWbAWubyXU5oqcw2QTCIWwxvNI/3BU4ZOdrOLINyIEahBWGW
PeNfcHWL742QZikOCe0Mz4rxYL2Uaeetxa+LS8qLgj1yQfdcH5gYtKyCfQ1Z1R8lm45Evdw4
Pi2jzskEkjTAVk3Ouh247fv0IydMLyuSF/sOC8+I1G0EqiofTdOq/pgVZ/oEjiuwY6z5WYRH
1qb4qnYDvbcLnDvUxl8QT1LYqQZR94qTHYW9Iev1EFUbTJdtngkS//beW8ywUw3nAsHgaazf
GC5QEb2NlqvJKvNA1/lMJEfeDnWaTC2b9yTl3lON1ZEqRApX41/P2YvGhsecytS43RuTS3Ro
w0I7Q0LZwDPQ+LwaQEjImU7MTEI2c/uha7+N44dO/7SYuakgVwWcCHzVEDTisGGWCIg4t7tS
51KXG5L4farOiZtUO6HPfDV487qbtiPDtq9sWEsUCBpapCYybRzjGh58/NmbsgrfiLJ5KKks
wKvp7Vuv1ZgCaJlm3wsMIigZ7ygbzzQHJlZYXVk3qIqtfOng0uMQNI70XTj+CI6Do/qb6sgL
C35K9USkNqrruzKlTMnAFE/UqVJ0ZjxKf81wi8w3MmE3np2pcnIy9VQdAxw0MdVTMjJFDXgS
KxWYEH3FWDQQ7YLL16gNVgNNs/UI82dT0PnvI695K0BUdZyq9r0fcLB+qrxEKjQmrk4TPWs+
Lad2tj0UjYWWRhN8U4iBFb76tWTzDmMCs087UvrbFkmt0KNjUe79LcMmw9GUgEOI36ZSJMSM
+y9r5aGc5VPD2BcGgjNYninu0YtBKaizvzwW4jHbAb/hRrezlZOyvhHAZWSWmeapZvR9hZGW
29xJ2Qox30ns87CBKNGFrqAui17kK8fMKE6N9/1foLYCUSsvP71VJ9i0FxfYx+SRgyoPb5KX
3k3XtOBZAe1CglmOhTDWriD6Q/HQcHnmsgN5xnhWSaz2M9+LzOAj57iH6r6UGWSOlee9e1Hg
mHAjBWG7+uSVYUpwgOmA24AA3b+8lZD5ofswuoJz2nLW9BRVnzbWwzhYy4wBDiEiqb9wS+KJ
5hF2rTTUqZWyggkpTYqDIrojbtTU5fQ+NUdEREoI89TM18Yk8DrApngk5MQAbnXd0gTptNEm
lVkvgFm+gMXRNe1XpmiJzFAr9o/XSnkyLEoGc+J2/OklM8Sdqd5nfZ9Kg3LsOqZQitF43W4j
rY//F3fvHddUtvUPByxYQaQpCHFAQUVApEmNjgKOAhEBQaoDCtI7oSYgowiIkVGkEwWlJAIi
JfSI0qSKIXQIvYfQQkJIwnu893mfB+/nGX7Mvff5ON7z1yJn773W95zF3vusvUoJFMOzsPKG
QCTUUW8f88xA8Sh75zfmctGufrQ8RWqGWuC94koyp9zjFfMrwB5ZZYmySPiJCqPi+jKPk7nv
5wPBHAUrs/vfcYwZ4o3kdPV5eITTJZrP7PcfAR81z1woTUpKbv0QpHSV8E50zAAzyb2gJC3d
OVFmHEFyAdJmV5D1PVTpwe26+M9kp9vTCpbdah8dElz2MR5rYLDZ4wNIGYxP/5p869N1kB1o
/Jxfm9gDFa0g5UC9Ea3Bvg6pvtRSd/lsxY4YXXceHnnznNLFU+j4JWjoINR+UQf6TGjogx7H
fGKIKmxR6oNF2Gvn8j2pSPDkVavEMV1uWV1jstHAGD2tfAU9ZqQDQ52QUysv14Xwr8DhRm+c
nAK8LSr8Ke6a/JPpqgQjI+jvoqLitnafQFEa7iqld82s5YoDGpp9ewaye+Y09MgVrh8/fCzh
GVwH3ezJSelW0K7TscAsgY/LcfsnlIe8PrJ7TCJe2pfq8rra4qqSSrLEKYoxJWomt7nxOdkY
WkvQTFkHCT/1SLCft44QP5FWlZ6Axors0qjc4sSx7Yp/xV1DB0bitOB9Q1+DVBdhGZX41W50
ad7aWjePyKSK58tx3GRUTE1Q7gBigGlwtZU0jTC/idNeO3Psa1IDwXCCq26a6u/CMzEW6hN6
zV/O2qNM7a7lOZIsnjhCLur+PNtW6yxdhlecSt4m2o+7fgqljTdfq8ikvjiYvlEHd9XOhL3w
l7g9n+a1gqLiDAnyLFYGpSaRbx30LrSY/vNMASDjFD1IgfZVRgP2zK8yegBpVbg1JpVMNo60
JXqrXzd76EvKssX+YXN9rr8/evxT9wfSDE2ZnwTsRo/x79kSpx+t0c4syuX0U6PG4Z5L+WlQ
+sgeyC4FiZcVtAzAxUQJ8dx6EqZRVN7FuHX1wJaQfRm4q2LqZhNXMfZmQVW3X2W8ub+HIG8U
A+OPvKkSNLOM56WtxRE0FWjeBrw1ljt6RG3VTiL3OMTvZx9eB11mORR7GjH64++/ct97FWtk
oOuvYXizKb1PG7Gn3JG1j2YwPi9l5HPh3myOl/LQmKtpmuN0WZ33sJ5MiMd4/0CXsYeo1Mq8
feqJRiTYlvj0Ez8aO4a8LRRVxSpK4DdSlJ9TnUdKspNDdZUUdHPhMj3okhS8XDgc7YAFTHKx
OdBskWIX4m6/xrHIKIJJzdDEoeV9FRdFbRP9be9MVbXkZD5e4h0Z1RSQJPUEFlTXtc1yToST
x4J9rerzIm3LHyV2zPZgeYxg0ka8eB3/JbnRhzvzFloz10GnkjircQ7roAPu2AdY1wr5u2um
Y4eptsWYKnRibBam+maC3WhqWbTV3ZR2gmwXN6QpVy3w49LL3N6uUri4S2JR4RGMT0F/zAu8
peZN40DplWGKob6Ap7Sv5b4ajX36Awm2QID52JPex3r0iyNTlFsLXAmtAk+fahretnaavbpg
lBCYPNJGzVpVDkc960FxjNh8yClGY9wO3hHUinnh7Pd5WUqORw//9owdWIDrYLOiU1ehrnBW
asTJh+kJ1qJfr6MHZLZqOnHINdQ5teR3eFjHtFBJMm9BnHHJP1oPE64ALYHeP9pu+YB+n79w
7oy9gXHd6NBkPLdIuVnu2fi1WfabgHax5SRfXFl2gV/1xaQ3y2lIaGMz/SDrIAHxFujC0c+W
D8sePHKRWRBy0A3CtPsMaLwE/FajYnRLUJ5t+uR7v57foJ9sYHXHvLvALuhlouzXXZBUJspU
Er+UDh9mG2m7KB2xaj9wiBsibBc4OhBH5xv89VLQ3IWfNvTfIrlFE6Uxzk/TP/d6kGVN93w6
VchlZB0UIDjaxk2+xP5hi5x+sGYdOa/OcWd5XK057ZeBC8kYvo2411JXQgtua3l42F2b2/cl
YCDpEd8xR/wFPoo4tPurgfr/cYFjjHRlB9CpYpP1GlfptdGRPMqmOcJxyNnYqQxS/bnAgeNu
E7rhydoIUrkJEoIkOOkDkfaHBl425Ur7X6Kp5IKLXe9ruHQLYdiJ/RbB7p3KxWM32mGYeD0B
6Je52T2VhM/u3ebTi9FhPEp+UUMUC1yeY5E0s+b6Pq6HSWNeKwOlCgGIcDVol2raVbQ1+u1S
wXShpAavHzpCTdcdKKLOI2JCYUvts+0KEqY231QO4EAKtnJ5m6aOti3IXeqQW14tA2o0z+Qh
BLMSrAPbTcscUvC9HbOC2tXNoR/702LhFaF1umWV86LkUOS5Ur2skFgjHKrEUVIw0QuK+qQ7
zXzibgaLSIJ206JDCoqRpfI6d5du4gsfPXJ0Z5JKh9kWXCyWKrDJXhYDQh/NOh2x6pOY6+0y
d3TllsXHDLrAllU1Q+k38qFrWY69iTpfnAmaRoHnv7gvvZPRvr+wrI38lKeblRBIYCDsU5aA
TAA/HU3CLRHwazEkjZNDEBkz1kqhUS5fdLFCgK9AodrDuIdocSoSxadruU+nt1CXV6cOwYF7
JpyG6lh7cGMYLu4m4zkKzRqh6ARAPHVv1VA0iouxJKua6rHnpBtzveg+Y0/fGj5tXxKx6tHJ
tVsEl63uXNJKhr+c6Fj9eXhc2Ium7+pgd2eFrihFm0TB+9jl6RLT1FlPofLlE6gmOR+jWXQ5
DpOfHK4Lsabciv9qafDWVjRRcDDPXkBw9meVeIzXdNr2cwuPo0d2LuO5lwOq2SXoZx14f/W8
g7ExNrw0MZt9UQSVJhsT5kkye6L7zfZZPh9TGQ5Yd3KyUEYivJM9rNhkHQZg3XGCUXObAl5M
wcP8l0ed5k47P17q3WbwJX+kg1VcGP11A/VN0Pb/Q+H/fnvr+5ZVOZVE+gLiMeB4XwxhDb69
tqXxf7RGKhIpby43j65F+tgCZbZspMkdl4xpL6KAejZhkeM8AVOWAgwbW+Po3s4Fv66CdZDg
7rjNEQLJNaZLbe+n35nxH0iLCskYNMmVkJERJym+6crXlDOCSeZkAcugfXh8fErbgV2mE2FZ
nQeKs8tznDktsM+xBYrSUT7oEwT5psg40wdYf4lGuIu+fH++taoP1kE8Hi3uUDKW4NzL+bS3
LDEzndnmTuXH96nVzklJKJ5KCiSpylg01lbwEuQJg+ZYBQNjhyx0PEnjl3DkNbCTk8ar0rFW
HoTT0mG4XetkmSBBvrXMs2Bbt/EJiwtKmpDOvjPDeobGE48YDVPkWdrMWy4hYYWSoWYUZ8p2
B3XADNpPKKCLB6H2irKt6H9ZSkGPVKjtRasnf3ql3dvAIZu+jJpwVBH18PV8bc9ksML7TBSA
Pe4On7e3TYKEVys/PUzE5y0AhTttO2ZSiDdtX3gU+ct4mvmodpb53rGbojh1ryUpc3Qj26Dx
9LlLd9z33l/JpudrpWUC1fie3udeuRA96HVpeKweGZHk2HNoaZoO3nuK2q8JmpAtPTJ3ZVj9
cJNLokOQFV+Ri/man3woGfu5YbluvLxVX2cd5Jkvjuh9cSQ9+fOIaw9pwSqOeVGic1mxM7Wu
/86NfU/3pirtvPuQ9rLWYgoeZMWDDHcktV1TdhTmVXZOh+T4xgCZmJi1tjvArgcvrJhOZjfU
lE6hx9eGY+qR6nLoqQUe8q+wtaP18ixkYMpQtZaexnIrCfB3dIwWXgdV9b46UjH3LOnZLftV
gYww0xxNnzedFnIwtwm/4fi4VaEnu+q3mgNVpTc+SpSFa0TyeamZkBHXuk3HpXIlEMjcnRR5
ZnzwJbC2rmmUUmJvnLdRj7dFVpa1gUh5TaNAWUCH3cD24WAg+kxo+Ea8IJETeyMKqHxtNxnf
lS+CC7MuDQh6cqH1yn5rrxafFTgv8LgquwQrj6zQDynlIg7unt6o7TvRlEsfc+WiU47VYAws
fODHLB8ir58kuKudpJ6cfyUY+Zl4LXWgonb/KQfa7CN1HlGxzkjvcQNIUPDVoxuH2RK9xVTR
fOTufEtMO+oyzkHtZEVt703wQG0JX9PXlJXBW+LzozVSCUhy5I5uQBxyboKR3ikksLAHx6yC
uR3bTHM5EqJawepvPdOYv2a0Dm4nbP4AVin7L2775f0ngoJO7yFfEx/HeuAq4SfdLLyka2Rs
YeQTYf8QmKUWL53/STUz41r2xThnY4nQPtHW+pqhoh20DElx5J7IxAdMPj9JtNpCFGB90SxZ
PfkwJ5M8aHDeEXnEz5rIqJglheQsyAhmy5kQ47oT7gsqNIjLDFr3JMo61lFXhQppDehEuL9Y
VUSZ0ZDBZV0ZHcTlzn2QmwQN3sadbRvfzD+TJh3IKeY1rRAELJguBkP6iWEBIpmU4VLx+LVb
IdKxytgzq+ND5QY+d9NEFQKAJKtGPK/vNF0CCgvzthbv/lo5kiNDukb5HDYP/XjBp98Qmifb
xceaQj49VL44/7dS3RVoMzpTRhpV+22lbra2wCV7XkfzF+6enKWBJ7CF+WfXgoR4v24qusTs
Un3y/OtkVTvPI2NsZ8tKvP0QRnaq/AnwGnqI3PmNgLdEb/VrofP5uaiP7RD724xnt905V1wR
VlX1JTDc6tH/1DU9LfGKdaURrY5nHXQetn2tJ2h1+zUvG9xwSV6HFHXV51P7iXXQ1Q+YhQuK
7zd70Fx6trbiqHAEBHKqRVFaoTTXssK/OLUf41Xnj0ZnAVkXLuk0tf4uyrZXXcv/4dhCp6rc
vT5BgoyNG5mTGpI5rZh+N9fNIjWIVpNuUyHPyrE+hfk0WM0RtNw9VaUqOWx1hlF112pVW1bL
srv3JnDqrlJhKnc2E8WYaFYkQRsCY4xElApu7tubIzHZ+Ns6yEDBqnIk1FPFhq5V/Cu9JWs+
3URxYyDvP5fVKzdMwhD/UQPho4j0yEqVb54KuECbWqTmYIqjRWY7u/5u5OZbHOOMUJS4JvX0
9aoUPqSCPMUN1BHng7kPQxr+IQ/6NszqKzzZoe/dgqtOLXZooKGrh4QxpFNadkymqwPl10Wi
SmPOqfXZWhOM7dt94GlRgF1DYMGFibm++xunoM1ey//c26rnZaWwGjrXdCLxQbySTQWM8qgJ
XRFXXV9CY7s1/z+D/QdR3mRZFUSNi1Vx4msgTd7h/MI38AFc2H0f1IddPpOrsZMubtk3yb1t
ZnbX82dXEo1YRyW+OYn5xyfh21fi0gxof4kur77OV3v0XaD6sZzGK/ZDKo+9+epHtCxh22jH
Meb5b91zdLPNbuQZ4m9UeMQvtl1aHeEXV0N1i6u21q6Ec05NFeJDFyUXZOIe31oGU5dG5BRr
e5qwq/3TbYkxwNw7IWKPdYAbjeZkLqTsM919bvtlSjXzsBtq2hZD7XNzsfu3Lg8gvgUUzwuK
NOVkYYY7vi/CGQg4/gT6u9Nk7vMoB3mX110m7TpteuAjmYWjKf1ZGVYP46gvvs21x7G/fLlB
oSI5Z5KAHzJApd+xbvJfsEBnkVYubA+S9FalI9TMOAQJFpntTo6HsPAo2fTbfcjF7C+7geQW
f/baorJTbvdFmlBdWqdPoHP92azm4jpSgWPzM6k2zQGGucCxeQlwbH7mz/L+IdrLthyzDrw2
ND75Po48mSyg0upq9SHPHH7gQt2VI7SPE652NjSLCuEQzMia+lsZc9Zpnm+SPf0jxDMsWZ26
Xdjq6pW43gTUvFlw6MDzAFVHsp57Ua34zOcFbzNBF36frCi7U0jO/nKMYrmkceDhRV1Do4V2
ajjJUFN/7GHc7kUQt1gnz/KdD4ishFyie1VJsixTzPwM086QZnBa6NIGnv9UIiKQcV1SRNZQ
BiRxxqRQp21Byc+kE66oVjGTeNNTY7az7+/BSnwLw0ZKiqjrUp4yooHgnxceZ2vjEgv5HEVU
UItANaFzG6QAgWMM+AzkCcLDNgX3KoPU0RUFqzNDleIwBxkbR+VS79aMXB7RaiDw/5aJ/MZu
W6K3aHrYFtVXwh2OVTDPShmQ2MlsYdUA6fwyrgZ4m09gHuTrysleclQwWhYb1roNo46zQV5s
ifeP1ohWWMYdkzoxogNbKMbepU7GATWnytAngCdgoFGZJ8JCJoLeborpI62Oru+K7BnIYPAP
Akmd7TKUtOhh6KBRnncgUe3/2z0F0WBG1iYFLqHPPVHyqpPSoyds9RvPasaoluVORSO5AZmb
qaPQfJ3LGsEAAuO6zO19PYEr7kKq/Cmd7gpN6loPlwK9TbqoabPte3dWUx/Pc33eiNS48ZZm
c1p7rPaHapLrZ3PbDOiKVEv+sAMyG33h1jctN/b6Q3prbgD7jCNWozPcynyngSQ9e184CJTR
BzjVPWlsu4WPv7WRSdbFRvfiXhQkm66D8oj8ZYhadt/zf8jyB77BNuLxsMQFLUExbGKvZMq5
aj4G8qWbt7qsqkSBLdLvGNAu3HqxCTy2sAXkcioRXFgBpUm9/xl7uVXPJYrCZbhWL3EbdAlp
Dm2L3c1Kd8AF1e0c96pbjnL7SEk2GNJ563xgw6D/TDQ+iG2bsEnBQ7xfd398NNQ1otTlaazc
zMqHQjvaEz2ufQonOnztCwojHObTVH9+/ymcwlDzP8U4+ikYOEKyYmU+t61TV9NB7rSWTBYp
XvRbmzoUNEGc2734eelku7wuRCOefPhcUe4l+oIRN+Q3sNsGWUGSYzjxcfy0LmZ87JL+pIZc
Jwr8c9+MpUo8vTv4/3AKzfZLaEmWeT4nOW1IJYe/U+hd6F1L2kuAgy5JaJub1I+vlFWU0YUc
HIyDHlNP69MGk65tFPo/hgZiZC6RtPomGsOKwWKHyp5K7sVmDxDWLCrrTx/ZDCSw9rOemY2s
YLMAE2bxrhtTh6ea2ypfTqP8ts8G74qeCaefHYK0NxuTiwf7WuJY0TmH4PnowJPP96duGPWf
Sq4G+mnvm3Re6yXXULgYNk3RJ9kfjnR6hIYcONjdUGnRN2fiezERjttDYoa/MC8xzjWcWrGF
16t+3UgcMCIQr2ToTUgaNgHV4rNe2Pt5apTXlOQTGa1d21vm5Uwy3IAMLr33EspPtK/kPI3n
81/wPEgI+scULsaNmeCoHrUVd7Aqp5pQV8K4yGvXdhp9wZ1cvUZhr4qWNbxUvSrR8O2cvAH1
H5JbXf2zVotyaxaza1UyCF2mTA0Wyh+yS/RpKhN1uNmnxMo1xsmJvg7Cu9nM33N6/4fMfuQb
OwJphz0UyfrJWJtR61beib0zlD3ZgC39BP++zWAdQhwCQh+kFtbM2tdB9/q2S3o9Wh6fJF6j
QMvv+Zz/v/2UOpDdga4x9PylMJfGw9vfZaLP5/9UNtNBeGQgjlp1Iil+rNb1ZBK4godY1e2v
iXpTk4qs4fAIBuLhePw/jxjYJJB2zmrb13d1CUhMNtlOGNBexMD1XfHRDRkc0kBdeUWRUO0y
vR0JCJCq08YncGA3QZJzTkatT6vEArfzUYJ8QMfERBYtJlyntdPAMCA4JSofpYcpWk6+HlGG
jw+1EZXojCDhjYc4xDeOsiV6a07KXp3KsSNCz1rOmMeTiHemV1hl/KWIXaIzqdnqqxn9fD6L
Bm/lynGlKr7imVvi+sM1Mq67VHjI4ur8ab/UOmEpfbLjwn99UP8Rkj+xS81bPTRBfTa3bzEr
75xjtcsJ8y9UkUhHjaQ+FS91bbEa3SZGZAHc3qHG0Ggg8hng1qZetoI6rbOtfGb6dX0/RKxm
Fs2MwqLhR9wCqSrZi5ra9Quq+iXLZZ7XGIq3wFIDbxgxZqvClOw+ukVFLO1ucCCstHTRznVU
iXOibDlhf9eaJ4jmSnkwyupsmBnorHx6KV1jenYbEtdh96xRnWEZWu24DsqepOVRb17jepBT
aP7GQI77LS3LuC1KUo8EmXo/n1KYlE1PggwnranYJjPPiZSWdizWgX/6WHkCmp8xtcDq4jIK
clJ2QcbM48ONghTFtyMKL2sEJDutwpExbpiHRkEK5YDV8u6TwFj/3vkrGgZVwEkW3qI6g2T+
BJB1wA2NouG2K1kgoJk2BitloUO4zr02BkDR2LF1kEXuFKVXPghznVNVLEcPCUX8vNgZ79mx
kPguQaPjWOhISskAVhK30gtU1eBCyeUoNL0x62pr5JP37fU2m8/wh5EGVIEkPQ9DjbcaygD6
aS17PJa/OO+js2PV4phz3xtLFlC5bb4MkbJ2lOiSTC9wVHs+jzl7ar7cMtqTBzdzWOnNCpA2
Y38koCjbFbzz28brwCuKuJ4A29lpN1bYuHKJwjpIZPeR0YsGGcajS7+VGBKGNCsKoyKJk91k
R+wqiPxko4pdyDWxkE6GJAnFu0Pt24tqE2PkZpp0ZyzWQc3sv5Z4dEj2qVW44SzLiB/bi2zD
Y40RkIA4RQdUEWf1xlG2RPMt9yHkMwxXFnHzjHtVt/6gjwoPSg13wcO7BoNXL5fCRtsxjgE+
/Owq/sdvabaokpuhVUCCIxKYm0hpauRD8O7+pjzrH4z5A/7Mt9Tu+Egj3U9Jrc3mMYFAKbuH
ePL/WNWIBwuIkUeU+0210+bng4RT7Wz8Jc+SI+ryhrpyUId9KvGDbVA4xagn4JLOvYOlWv6e
Xq6Z/hkDF1SPsh/zH4Y/KoZS5IzW5s6d0bvpf23UU+g9M6/W35fs6oovnmzIkZ/qlYtRVNMz
6gVLLRsBBV54hgIf+cyX+QXAOOy1L0qi0OP34lYUrRAr835wfWRuswAzfB1UFzpTN+n42qC3
zbzxTh+FYfklHYmNPzrq5KXWLb8OqvW71ykdJB5qi8T6X6B2T97/0IAYOeLWb8QUT46C9sZz
9Dqmau8QG+uzHqAwpZKuwPtLOAiuqXYyC4sDpxZ25r7O3YMaPgbWFOZZdUU+d5cLVwiSvrEd
8a5evX35+tjvGtCH5VCUzTX8CPORSP1kRsMEpprzZGte1hTx84UxqKblDVFrO/jCdXhYjYUq
fZdGr/BhZd383loXETEi09OkBllSE+yhqKLmEeI4Fl1BDtLA6gQ1Z3L0272Cij9nQc/3C8BR
lmVgh6Ng55zfv86K6sgcc7rzx1iaZHCQIl0fmDs/uTVeL1nuRULmLYLh48t5owihbeLMI2IN
CaTunFLb7E9Zq+In45GMQe6Arfr5sfEKe+SlRhmH+iWXY90pMxas528OM9yckVev5nlGuwjh
wYvejvKtNOJZxC7Fr94z3LKdQjul5iy5HSzKsfPeiTyQ7L4a1AhbsbDM4ty4h+xH1VjMPAar
lW2Hy9YVzLGQryvROa+YtPG/5kBGR0pd5Hias0WEXSHpfqhhq6taLTwwKDP4ipWEstf4Iqpq
pr3VN+P23Y6gHlmpNogH59DG/luitzZBKMRmWSKqBy6fS4smYsPCQpEsAf1aLG3wi2VYV4oI
czgd5vpsStA5Zx0E9Z9lHT3+eUu8f7hGxnWR/Dixfm3sjm4aka9mOh+OM4qsWAc17AgN3gTM
TnAt5EtkILyDAhnEsu3pF1NXLlVqVzcgH01+wnZQ3R2iZS5Bj0czqUeE4vHgLwofuTq8offP
VhWc3zDoP1c9ZLsppQGf0/eFpoQxWCwPjAoQyU0v0dtvyJx+4aT0yxta02iG40iNBXMb2qFD
YhLWVOJJe+9yFGArisuxFO7JK5bNNADqWsz08TtiOtCZ+PE4aiZmYOcnr5ctGTK/6yYjeQbc
8ikBPMvinmRz1hmhwA0Sg3bBZ2CvDOwijyh2BoKlbfsbqhMqfPOfDgFfCxANmlJnhk++Xtkn
uz359rkfIk01mzSAGHywOCVlYCJydv+jjSNtid6iKkPRupZcouVXkCkYLSSl8ggL5GB10VH2
BlA7+DHxp6iX+pS/ZWc32RLPH67RjiDlzzmKE5DeGaVRGwHYiC2VUlaTWMGqP82/GZbvaHIQ
C8uuRQmcO/mRZFy1ODKXGLcAybE2x9Be3Ok/XHiFwmmgYH6lbAUP5JuPhOadK4bB+7t30gAs
7EqlfVPP+geJnBQUR2NkSa7NJXobjL8UF74GalZRcKA4mL+aGILCe24stsuK4bLP0bC4xztX
gjc8BvYTpWMjBnppVUktA2ZF3muekJ8T3kosjAqZfWlgKvkdGiIUo6QSE5p5Zhk3GjELIUUb
+m6N3Jof0c7XlOu570ddH/IymEwRFCX9NKC0ExdPIRRGjCwLVT00WtIYwTHfWPa2xv4HaMVm
yXrlZRTVQuVV202SRd33kJhs2alg9Rs/F8fkJuJ/T4UlZzvHYZ5LvY7ubdRiVKdCKvFLEwsX
ZibTovk88OWyqqvO5KTE5MpE6Adk9fbfABDsGvSO7vQck6Ln2q5SQksHH66c+q8uL5/qBha6
HtFgmZlNiM7WfcZs2wMY2w5sBL4LNxOV1kzK+6COKFj52NpxBvgg6VhwZB0VHvsCMXjE0pFX
M8GUT/V0YKJkZ2A4JUTUzomN/bdEb82XR/A+wYccCVRT1SeOlfRogqdW7Oa3maocwmtwCc6Q
RuN7o3lYZ9dBa+xGW2L6wzXaEURP1B9eHR0O0qhgns1FXK1GfdjL3oP5WKhpWSELuSVyaxNI
f8LY8O92swHyO/RccjBPNWlKCGBc6S/1MYdmD3R8jbybqKxXWQcBdc4FfK9WRwF1zofnTjvF
I81qRzQh1czgX76ezsoj3igi9TI+MW/ma/t9gWklxvPM6OD9WxFL/RWfvWMvCZvKuDWGlwrc
H6vufPtuHGVWZ0OAIpbAtw6abnwcu2Zn7EIFlBFdPbGhY3nl9nk89HF+wOGTn9MmtcOi77ER
VjiykPrIgprs0hdIkgsJMXbNQb9w7do4xpbordXfZUtPNnP1zbmK3SHMsnhjb4h4hTceDk1V
OWLjK+QZ2Z1caZaY2kNeLlqcWKg6cX5LjH+0Ruy4/mv2835Tw04I71dQ3Ktf6yVGdHNrp7qw
GvBmvoDl9xrfmDX+Ad6vDBvmCWwdydWAtdftQPYXOXxiWtBFgsbi7u7/Y7cDBwGjvhMNwDRk
BXhaqJFEl4M4V1fuMtwcrS6qYWJujmjxGbHsNM38SfJ0vKEDt+E66Cm0fLc+IP/OV943qjMk
oklUf5vy4bG71LRJnWmTZfg5hdCXMXOd5/BIBehzRZK7MNM1QlZu5dbBNxtB72eb0Ud6kCVV
bSm8uvo28F+NzOum7ZMhGqprS0Ax6RF/8XHNwArXIAjuectSib/N1Ly7De3t5eCNY2yJ3qIG
v0q+dVYNKuGnuMbAeUw9Z60CCoymHx2hqSkM+xi7PneMU1xjSgPnxO9/n98S3x+tERtIXX/Y
JqVS3E8NyBuTDqmmnU9pLoTVkZpPUVd0JPkCVoYvbJaxZxvXCHhKsxLi6P/Vw+a+S3RKUj+Q
1iKL+kSvHhQuUoxKk+Zh6hDga4/3N00hpwSHwmZUMj7E3+o5uuFJ/TNVBUDbjEpTTXLFouHH
a0rF0ZlRIhN3KaIKTsrxVLFiBa6Xtbf1i8/hQoiNAVyXKriXY8a1F4KfXwOYOnIZCJ+dy66n
8so6MWLKnVUl13pVnkv1VNYc3C816ZeJdwxwN/tlvrxE5UZsNPdMTVnn1NciJ+Yb5AWxvQ6y
lK9vHe00aACWA93O5fI4lFlFQzZCkDNh0g+jSQKCpfd+WByaTrC0Cp3xnVGaIrNsZtn1zm8c
ZCv01pwb9h+YkX06rHwVLwUjTSZPZfSsBNjcIdBeVKuIdc/7SlaffkyUKHVuoxQ/n1gIEXu/
FcY/XBv27f5vRnwfw6iFA/0VPGGvLFYC7DtOMq7pIbjI/hK/ksofMxku0WFWONtwjs3SJO+D
PEK85qcxs6cRVS7sfJsYJJXk0iGvHB+A30yj9twJvRu84ZH9M6VdQPvhE1SdKKunlqetmzUE
Ij9LNpDozQ3SrKNi+FStbH7f3mphQKfGSGZ+7tDcYQ+SARGoAdO9vRbgu+2V8gB+xGCMJ7KY
YDBwosf0gTZN0sBzge1wP6+CUEfJ0wEVnUCMhM3obaMxplE545T9moDD9s8bJAZtu07Psqlh
aVGZ3UhaBVNkNIiTni4FebTfbNLOR0wsSlF11THNpZOslwZ+tPvPf/lvzfIgvy3bvMkjvzBV
ohU3HwBY1AsPuFfwOPuMkQMGVkljFhornKdZBy5v9JreiOEHp+9Z5pxjSSSRHCZcYycTjFqX
RLiG7znQVKMnK7lnH+UwGT59eGnYirtz/dnNFqPvt6vwWged822LbQg75KwDm/fRKPScOTMH
zEOR0pEC1kQFs9/DUc+dTk/brINw+Il5dsfzgHcOQa2rCyMRk3OmKz08B13EjxvEcw/YZuLJ
OkFPLpG1zBvcS94RnJpWkipiMm8iv4ZfWg2zf5OZmO2NsM7yTEKGWDm0tnDR0AYoNDaWDeUf
ZUYcE7T6vKQiRbaUnEpmlAhaxiKwMzBXPOPW8fI/rSpbdN5FthTG+Iwh7NtmyH3K1ALSxdUL
05MvtV1MYfdbU4jK8ms9cIHFez//afY/RIftgpT7+cMlVTmVROkeujPClgKJ2B02hpdoK690
+yiHQ4DzvcwqWIk7m1gHfA5tAuk7miZUOuOTFcfzGhF8BZGQ083dgnPqYF2gVJHNbL2oQFp6
4K9LAZ4iDqRJUlaWTV0byaOmdbjqXDCApeZc/muDnPl8v7sxBkNaL7GUI78gLaVtzDOw3dvF
lmM77PHKhN5zBlb2hOVsM06xzgR3yYpeRivCjefrDP7fF2fERBq7gjSUhkXKU+cVK221aacC
7YbZFeni008d44JIqasBd5zK4g1mYIXJQLmVL7vj/7vvVomtTcZivdlBQSWO3R2sgMARAvmW
LeDBos7knQKcU1ZmMJ3E7mhWDn4d9Ozg9q3y/bHa/cT1JjtXoLloB6LbxwVlTNcyhIOuQk7x
6QZmu3mUZpS3vO/Fyy3DJUw4HIL/GNl33CCHEEsDHXqF3O2NDAbk5JPK/ZBWH/ONIL8duPkl
zbAkpHVnTU2qRNHryDfWnbNaidEwUk8w9OvSqhGkLZLUDJE4mEnWXVPoRVnbxzGOBmvEGafW
qTFkc4LMEgrBFkDpQ8BX9PxG4N5gpefWQG6TQOtUG5xzeE4npVgJzQBFtETCUjsVAh6Eo2Kd
dOhiQIDqeyByS2FwY9+t0FuzBG/38c4v640lIe1wn8iCp6hv39nMh8ZMYjQNF/NKT8WRhlwZ
U8g0ME/BJOua62br6FZE+ou2+a2lgNf3SOddo0BW7XsMU0kFAjru+gxdLm1UrAxZC8WODOBn
QzczxX9HP9/pT/mHD3U6GYlcfWZ0aS2vi485FR0NBG26AUGbvR9wWb1/C9r8sHdbMLDvneeb
n2pUmCpfcKslEI/7UNQa+QLk7kdfYr41Ob/x3Qi7NuUk3shrjOWTj1Cl3eyVMK99PFDhK5DF
OPpQ5HF3W3jzclc8abIfk2WCTOspE4BEbh/Z2H9L9NYswNy4jmFqaNVjERvqqnqrDy67Ogdy
6DBK640rd8ONlzCs6yWy1M/k/F7wQVTNt2ctWxLih2i0y2AGCnVx8GlnrHyoQlEevNitN8rC
HW5AcjhQihTDoRX3HSAgVd9NsHxPZ0mQcePTAC+nHESRYvxiqRvsuVYs9zhpSHeGGzzm8/cC
FDuC/C48/Fx6b/aNVfSCUK8YDxFNqSTe/jZh2E5Itdqh9pWd43jblIXYtPGuOApDkg9Pu7BT
/aS38vuJgDvWVBS1kcu4llqwRgUyg35TB2OTh/M/t7aokskdQK3OqqHWvQsBjHyz1hJK0Qmg
dqaTV0jdglrSsDlpkVmX1bemOMW45lL/P4P/J1H3XQq9mjx1C9Gk0eSQ0DFmW/uFE+axFgt9
r93uVbKcE18bkG3awMHCLZuA/n6mA5DkSOHdXM1p43TrLsz7ZSWh7BE/DdjwrL4sGfZf8WHG
db912lycVseSqPOBVgJZ1XTmDee/OSVzboTE0ZzZ9SgZIiloU26RbyHClAMFW8YJWHeqH5FF
B5lS/IOYEmchu07v3NhnS/TWHHA1O80fobZdGGSBEc/HHWEBQVKH3GmD5JbfnwcaH0/0Ab4r
CBQgROeLQ8bChZKjW2L8ozViP1zabeN75ONsUgtRqtuHBKObz2Yx3H6REaWWIyQYx3Jx8F4r
TmR2RhUDRD6/CbrvZwdgszIPf2SZTj21pJmj2rTWG/z3eY9vsY1UK2NwRMjybn6dmeFa7z22
b+O94Dqwx+9zkXqth1M9Gz+qAQYgIY8WTHykFd4oLNrFhvjERG0TvP/7rS1+t0dUluDpv+CJ
rN+hVS+6Hz/zKbc6ZiZdSTzdTJheB5lYId/v//M2g/9dor/YrwcoHTPgKiDVIqdHWWC+86gZ
ebnECDrCfl4l6La/xFNpXnMysShsmFVEaUCAFHk3kf77rsk4mK4/AsioR6mft+0UyrWkakg3
66+o/j2fHntlSYyWjIEZZTW1VRiNCnBjrzq/EQl7ZRLWSMgm83F7DfLRI/gx8/cPKeWny54H
IJ7t3RG8seVW6C2uuvqdijnUYkntbL1hFNyLPLrzi1dO2vtRxzBCIJNknUtJBz44neO2wvDH
a/OwslgxEEiw9KEJOJtIm5YPcp4xoL3vr0xY1YgcjbzfGUCdd8t3DrJ9+RQ6HGp7/o8Bfr8v
FRDgKBacLm+Z2ptAraflSOjHULrbzckrF269BcRls2Su6ZpCr+s6kD6RFGl4mATuM8ZsfmT2
8rdV/oClGyull9yer1uXGgjmrpO8UZ5S4NjGIzK/eYTb//pEtrjIcpmj16YDBbFLRQr0Cvpb
xBMhmy8dKX2Rbj1w/2xbRMdq8J+ro/i/yvJX/JGNR9g926evXLSid3TeOyFoJu4p7QK2Qhqd
UMI7lERQH9c4XVfxxjZ0M4PO91S4wNWBHHk9OGzOqp4O9rYeg1HK2qwnEO/2/m0/9jVTce/P
0+AyDw3tanfOFqvO22YlxNl7/zjVxVNqBQx0ElPu5tU5TNP7qyD1/3dznEynIDmo+YOkOuvi
tpsYYkkkOGI/bspb09BD8uMJtKpObb7G6MzhfNA/kf/9r6hg/ygTG6+FRyYpy81hotWkc4qK
fs+65hx21bRsUerj3dWewrh1kNn4tq/nIH90fVdtU3nak+QCo6Xpavyy7LK/nsTsQEUZD+0I
TQ2ohub8LYDU+GPm/k9tytPDWnc0fqnrlD3LQOW9MWccffvtt3sukt8Zrl2KdNmLX6iUiCTY
MuEYAcShb0vx/tEj+Ob3rZmuRSVz9pP3PjwiVUdeFFRMs+q0KgT0rn8qP2pS7zLNzBHrupdD
kdw5MUqgve8O/obBf8ofbHzCnvaM3nuF/stzJ9ZUYIuh9irGxkOLSh/pcA9WHpSOPwXEYTRt
Avf7bufIWSScQCuEJ4syZ68QQNc7wjoAXTkOVzrYXM+0KHWgDooMArIb92Yl5/K0gnlPkCbq
8Y50khw/YtdpLpdczn6FuumscI4nGwFKTrXcd8f6MYk3cWKHenFCSrjsgdP9//+KvbHl/5Pe
YjA0u4h//21f81+HOmQQMSQMVTVI0Uif9uKJNCqO9WC09T7/mg/5pWZrToVH7of9X/1c/wMv
buNOlXhS1ZUyP8ji7+KImhfd8GewQLtjZmeRs349FZAp6sR8qOv5P0b+HefA7SBvrYyqidzw
FCik2h65oHFAosxlYFmLiD+rSl0o9nGkToZziAKiA+VtvS9mvJ/AhOcxO5AarOiwoyhncTLy
y9tcKnlEltRJxh/kerMRI9/CtIGtu9/g8H15hhNdjn3UhzKNX0ADc6ez3JABnzZGuIq+sf1W
6K19eBxo7KiT+DgucedX6uqNxkIYFm93p26Y/ZeSw/nDyueHhIXL18w4cTkZHxhHNzUwbEWi
v2YbNoEg94Vy9YoP+1qIp5o7smF0B1mJBTaixTGy78BVH4owywAzXYB4RTAe2eYR/McYvqdm
7qFYflxWUg2oXQe5DES+/yIToP72dBstOOnxkdt0ubAyKxngvD3tV3PycscJ1Id9Xw/2DggQ
rnK6+40SqRPrINW8tAGk59WatAU2VVWwWFuipOsYoKrL5VeTmYmGrUMcihtx72FRzqfVLLVV
T9sQci9jiF/cJubvwQvWKiHbBKmI5zdTc+FxT4I29tgSvUU3zT39DuMIdKKjdvbbM3BuwDSr
FqvPv3plaIfs9Gz/qVyESDjj6Fzwljj+aI0AFy7X2RpzlaGgddCNKFeNh1QnM1QNYJu/V6ak
rPwx1W7MDGmQqlEKPIH+bxa7fwD6Ha2BO/qtZMu1z612BiBqfebiYd0kXS/WCXGrkMMI3nPg
j00sJpOnUD6yn4nYy9nOOmB3HhD9HjwnLuXBhJxxRS82tUBKmprf0wQod4LL3jHGtcG56tZw
IENc4esB8gzNpAhYP85uhLt9m7dubQ5wWK1ZYpwoOhDlgbIZ1jsOcYnfvuC8D6lJUueRxCGE
M2zMybM96Rcagzf23QK9xXPoUxT0Mp6E6NnJ9UHl4XHw07vzfrqDDMScHhIy+byq79YWOP14
TdgVSgf0iffNFXI7+pTdySMIZki3sIjkfMn5CLin17Q+SzeecXTgwCbAvqOi7lK//cY3x3k+
x2fVpxWPAWIwY6DD98yUDSsstSX7wDiPgE7PX53p06g0Fe/wJz5f/92OUt/4QMLHZ0QAnz2S
lMrEal8EgvfgVMOckV9fvhtSceLTbScLdpJls2kQAHx2cCPwC1w3+qAXPV8Xy/iQJivAVypm
V2rTgXinbrenkm19J7vjK9boYq72nQF0Fr9CCeNo48bOW6G3uknlU2lvZZxSrPvcdQ6yywH0
rBIqVjV2MbRtHVRMP70OetnD4bYVdj9em119M95QOJfbNM7Mg4hE8OeO7oS1fcBxPTNPgHvC
HIBUAPG1qA/7JzdB9h0jl0EHkjsiiCHNLqHGK7qRIcZ0Fy846ErdST5aIHreI8j5/gvtihBb
tt6jgPiARwh/uZVCD19QpVne21PrIN0W5PvdZmPiOK4YF04oa3CSm2y/ckv47Uaou5RmuJDD
frjEZNyIkJluCctoGsHLs6PRxa5GxKLYLBNGnsyOefm3OVjRbj40L3hj5y3QbHx0qg5L9c7S
iBX//LsC0xURWxojsY+AaUxPLMrEqJydqU5CPNftQjukJqSKhz8m6BpSE24dP/8HQ28/6Z2R
wmgn4V6+fQs/0M526siLOhfDYlXwWuTLVvr+Fz6bvcc/GPNH+PmxCJaXOpjBhaFgdeupC9KI
o2fnHlFogekOzxjjy+0n10GaQJTd/vlNsHxXLc7qSE/pa3f2o6zs3AcUXvA+cEVbHDjrPNkH
zsUl3p5cDnI5XswAzZ0B5P85wzQhwFO/SGKi6O9tQVegEgL/07b9v9oe3Yj1Z8hNjKVMovop
3GyZJDSXKXkWcIeKfNZNbqjbCWyE3RSXEZg32wqDN/b5V+jtJ7xfpTAIpC5KkQjHPGP+SsaJ
vN4YPU7452XwIP+F3lv/yuB/2b7syqU9eGKI2R6cmU9TAA2Ge3KYS7M3BXzKlAlRrswH3EZ/
rgK0kLYJgO+qhXUdH/e+H1e6My1cafXOqZu8HL/6lHHrGCa6HHlpMfSDavLaSk/xDVYRkmN+
W3kwcMCzL9nJrdxKNkDmOuAfE2Nbh+hYejdBe/+LtthNjYixbb/BgDMsnyI+3Ju0KsY1WNxG
3D9pZ0uJcCkE+OSiunx5WCgUOPhgRsNxuBygJYQZJ909qICdTXCQT9fGTv8S/dtcgQExoZ9d
3TkyBDxV8j7m8XUx7Km+I8yXd8Ec3RxOAKD/wGvXzIw9dB0UrMqfa+ZrAJ68Ca7nNE590wR4
gooG6a6DkrlZ0vgQ3OAm0L9jzDE72L9/mHbk5lCRq+tzUl+iBeupBG4kFF7qf4eu9DuLd4BM
rGpDF1LiBe4yrjmdB0CIbsselwip0RO0A3awxMZC4tRZa8QRoSk8Tq6t7/k8ehmK4LhcYscQ
0Z2G8Arxb4S9y2jGSLgko2dpZnYf+DdgDlYSjw2EAUn/gDn4zhTvWleB9iCHx8Ye/xK96+qM
uvpqbptNRxeNmxWfsNtiTFrVI7eqtYeTSNN4r2r+L43+l+2sjTA7hRhceneKgk0uXgddaOD4
qQ2oB1Za8VaukhMfcnQzwb+nJh4rHTaZhyF3vwNcRHQI2UznPj/GLRdjHXN0vvLhoaie8uUe
gnPAM4cSL+2uV0JaAIxdMTORNlX95scaSIvNEGMsccrFBjqyzV3Fivg1aPOweYn6eIJCAHxM
peiO7IooW8H7jdgfiBQdquQ4q6qkhG300YwENB9yFnHkoFk9iQxuENg1A7iktFelzTjXQIKF
hzd2/Jfon8TeECxW332x6eg2DUS8tmU38dNdfuPmuhKCreR8y9nxLw3+l+3MPdHxAUVTdiqt
cCbZQj7Lsa14GS5nu+T2slyretyObSb3dz0i0uQwx1gUWu4fIC2a0CkaFBM52oUiCyn0fAnf
UEEgybQJkb0kMR/6tygz3iAP0krrYPMc8bidmwHZKITxomfueQzNPHJ+GJWUezOD6RwP+U3o
m1lnl/eMO3JwISOsxKLyZuFcL+AXBZNYCPnJPIS4rC3eJ1FCxDnjXJDZJRaQYKHNntKfu/cT
z5tCi9VCfNoEEHUCnlK+9dzFoELyiNAKrpfIsXmsyZ9j9JdqvWtlxgo879RN8O8dEQGU8MKy
lwGKJj0HTJLEWWJowfzlXZvI+x3jxUARj0sKVkqqTJn+sCMBRB7cMyHNL+/Ij0Y9b7UxkWIm
GUy7p4BmOQDS70LPJIOFq65U+PZFz99V9HytThaqZ9Wl4Ro8KBGQDmU++BnF0Y0oufd2sFpD
q3MO3fZZVedSQWbXpyIOCeHxz4F8I34nhu60MNfs4/lZ2LNMQAO/nkL9e66ftr2JslgtqUYm
9wh6IVI+bS/yeH2pd8wztGiiVa+qt41s38HWc+vfw+svNgq7hkqnNuNw0W/03hl+CGH1/YrX
dRTtjEs9oIZ9raHzbEc3w/09V+jTpWPDBEuunXJpo84WffwZ3TlnxDWGL+RZiJNpc7+sZFcC
0XvtFEfEVOwpYOU+BDx30aUcDSk+0twB29ZPpsAhmHaexaGnEHcQOeV3GLrsk8sAVsNRpRZz
KUAkHJ1bu3Ns46v6mprTjFReDA2YKGi+gfKfgyyGetCtR/0lolMOmZPH84Haav3G0qj3+9M2
dvuX6AOwDuncvYmN7ktlUF3kUjwP7YKMWl7vgnmRW0pni1PQTlQAe73q6X+Jx1+2szbRtGsd
FMr/BcVkVNMgauBk3gzWvsRSdWdqDGSaAbp8YhPRv+f0+Kiy+Nwy4e25mzGQ464m7c51eUaR
BhBPEGnuCXa67FMlyiWwA7YzC9AyYQX4GSUTAAb3faDijtgHK7QpdiAvpJ8pViGuIkGoMCYP
9g1uRHmp09xf1YXzgPnqrLoDyr8cMraz36sYRdvj1kp1HHr02fnrYP+eK9TlbaGv+aAxWLVw
GXgPp5ZZB3SUpL18cyxpv7pOKLpEQitCbws/+Pcw+6uNIkbNvo2oCrBvZbGGGMKZ2whtWojB
tnKxDuJNOVZu1fbNMnt+v/BX0K7PMwi6mdvH6XHYvD9bT8VRdQkTXJEulNS7kwQ8YvYzpcPw
33yvUq7eWOs4o4p7BXtVd4mORTMZQkkb38CulzMxUGeDUG86jb4cQLgFzKOKda8LqKPGD9pm
jN7U0YlnhL7J0rWx85+mj37EMC0FzpXoL5W56iDzPBC7xKHBXr6VO9zGiS0kKVFUAOdnufd/
etgfoQMbuN9RjLU38TqCurZ3kHQeLHNpFZjyfBYzOgaoE8xt+w5+Y7D4B0jfMfhK7GL2OmjK
+SMXJp5YNcnhsBy8nGzN6laAYJ2ECgAxd30A6o1wD8kQpMzIJu/nWNEDT4V5pgcw1HkXt40o
RGNz7kA6AwUwndhim9mpwZ7K50awUZsw/RnzDhum8/P9uRtb/0s0UGtkGLc3KVtPA3b+ywij
34B2Qf7IwbSaeZtbvav9ea+1K8KdDmf+Syz+sp2RrEJ4TDZmDfGBpqrP8bFNJZemQjYFAhB8
EJ/d2X56v4ng33ODJ69CZD3vO0MvSWaIBPvkXub6pUOG9NRgzaeq7Dwg8iPpYtRLkYPM64RK
yiNO8pTwlGybRvY0DvFtKkv2UyrjQFltPtQcDNyLDylIlkST6zu5Rjpwb7Tp+BNCtpug33AL
CLymj8cmwc+6Pv4VNj7UFWg74K/Vm2tSEfnKesosVFKIX/a0T77DGD/JPOLkwrPeyKc9aoXG
curjF3AVwsVhOFrYx8c/jbsyl4qVFLXEseGOInN5WcTmnGYea1v7VEyhkXx1a2wB+8/nQSDf
Tgv+TPRYw1RqhKgDGp1RcEk7xfZC2pF677uDrrvkzvrg9s47DmsN1iVk95fdf8ovXx4QPUpS
1thvqWLT2kNQMNAwmR++8DLw4vTHFhEqzvxuYq52d5y3zkrd52WMgQZXFg9MoraPvGyPRlmr
vZ/qv5rU4lRoFtPfMK768JmROTWutk/53MKcJnrqIZWN3FbSOU78uUJgvuQRsdMho5E7Pnug
MWPGVdddY16VfD/5lvKrbj9FZ9dp+f3MDE39EfvmD2kc0neR1yO72nR5W9tyCLd+FzH2D50X
StgzS2JK6JcVKUV5wZIrMJ26Sq462rGfO21Gzoqq5feoGveI2z5EnlAE5giOTxiHnhuh6Xcc
TcdfR2bY0xTRuJjYGP/EG06m6aoEC2+CrK58tZ+tbcB5sbK4x++OqHeXxJu5xjKzVuVb8uVc
vCu00AsFDY7IG/3FJJiouh6TdGl1KiGtYb8Y0QLq10I8LHAqLcKL1Gc6UXEugT/RRjAS8bO0
roIlabbvifdjYyVGh61FYmdJ9PAdBR0qydFrvCdjIHX0vHIyrtXqnJAtRWl54Fdq8nRmyoLg
g8AJ/Bw+mq967e3+yCGZm5a3fNJ1H1lKkqJwlQWTcZGd2aa0eBRES7KQx65vQZbYGfyLsdSR
aTfJBKfDaWG9D8rV4TW5QrHYwsvptS9t45Y6dWXldKfFcJ960ZmPF4Z85dRDiBs08W/kPb0c
Ppr5xAxw3hn5Wnv1IerD7uxBpojMb2XiyOTeUidEmtnOb2w7/zjAj/s3kDLL6rWdY8CtW8DW
LPTRZLwxA6xUo1G0mAPMZrgnBzez3/0nrJmYHK9A2A6JSRfIOig91K7UkECMJoWLFOnlgWdO
P3Eu3tqb3X99WrlpJbkRC1LQVdVpP5nh5+oU0KMYZh0ZLeCEtxDZz2i1FCXw+UmsHb8x0izX
dfTYQUqbwHLusBVhFjK4uPvk1/PA/sv00Jkj1/sEM9jPyeUah+cVNBZaO9BT+KYiCmfaVyWx
fEC6nAS8+hRJ5OpTHkNqRtV2/9ATQ+S9xVE1yT6KnfsV9fJLCpUfot8EKR0sW3JBKYWZ44Uz
M9bQ6WKToXeLyL/oeSo0qXjkrxQNfEbnqNYka1vkK4lqPDJZiBapc3MTmkkXUC4T2lOhlcOP
zx0xIw+13M/saioRqYlDSxOYpIP7rQgFUWbn2995OcOuNuIL96k+dZTgka654XozR225U1Of
z0B2RgfGgeGSk4E25qNCYgKEJATHlN4M5Ju3eRAa7CoUDAz97OPiwsORp3XY75Tae7M1jXgn
mu8ZUczSbV4KRSpM0rN7yoyyR3rTbUul/VcVp5B77FjXHyZkjGShHXZzgESUpM0KXTBYx/SI
E+FoNDqlTQeYzoMubz9M4ZvAmo3L+I3Pt4b11PS5HJq8KefQZ5JjHwUT7bc0x1RUXmk3Asfr
a+i18bXW6Wj+9Pr8rAjPIrM2R3m8M/SDi+BM4u/ORryWuEhkr2CzwXhkPB9NMbsVbwTqlpJ4
BT1Hf3zstu3dMuOrJbIDTndmCow8JDrItglTZOb8mbmjy58nJMPijBV0Unj6Ot1m2xQ6Pc83
5yebX/LvuIupM5rTP9qh1qRWATm1wgmXmnVK8p8u9G+eFo8gdfL02KPjF6urV8WPgV26+3rD
bB1pQhj7mZsJWnmviRkSXKqclBu5JiXQBLQD8jR0kAxK0UCZj48s/frRrCsxxX2hOKQwC2tn
nuciGiEnRRiQGu9Ja0/H7bQutfkErCqX09FshS++1eKjMIwmXECl7Dkq6UtBAqIN8O/dXTp0
R4Njn899sOoLoBYR8vzZ4G/7/If8xfbCwuHE/OqNXqPAcVYVhmmVqT3Esb9NOoexg+hF7620
Y+4Fr7KJvt8E7n/CJq50wo8msQ5aBA6300NtS68TiL8LPxUpss0Fz+wd7H27Cfr/vmWT2PmQ
oTZUtD8b+jCR7OoceJVipIuht2TY7elvSFVtMjDqyYpIV637Xd2XQ8tVI40RN5vo3WIn5NV8
naLOEFJRVNQK7NQoMLaNyK7LV7gUdMCh9XApgZRkrpMsF1wu09rahA5P7cgukUyviTRiLNvc
RKNz6vI9iG3BWlb8tJrqx8pkHeC7qUYKH5PjeFOfn+E80N5m2w6bdzbF6mjyZ9f5kXRlgVSA
gUtyPz1gtywVZcUwrtIrwhgiF44fBe3XmbZrEoexKd9tdyY1tV6cUychFlUz+lNzOmVJfVij
m0pTlAC8Q0JWRFqjLuwu6toBkf0Ro8hnwlXNnbyneheeInR6TIUVF6n8GJe4BJIp2vZEnmO5
ju9Mvq4+FHFcVtdbBxo62M7T+uEx1zzxnhBEwHoeZz9011TrtHaA7zLcHl7Zn06aebrQ6QJ1
lfJuai05sK8e5CWhEJjghkzox8C2+dj7FJCakbaZX2Dix9E2MgcnXKPSSxZ9Z9QZK9Mp/WU0
OV0LdHBwypn5WL95pXBB4l4Ya8e50o770cMuND7fG7n6snxmFS65BLOciKyceBJPT+7pS9SH
nDx35yqq8pT0npavpL+GQTvkdRpv0pRvZBTeyDVDn0rPTRsDZpnfbcqhT/ivjK1FllqJ+MoW
+GJftWliApBAmVt4DZ+vPjIG6n/2NJUSuLfdPA2HGQx9G5Kprk+biq1KMVbQlbnYjAGbE+N5
SU1XSISeMhPqCXQ5Jhoor56KCRpp5PGPp7BtO99XmZSEvDmeCBsnaxzVj3YMMzNl8uefKDTs
zTVqiosYORgx0qjLi5cneGSi9pzMibAnKdAMfxsiBWGKfLRCwgqL4CEhqZN07+L8yNAQpG4k
P7BLTjj58CGF9aipXvkaW2bSmsfJAuXEbsEHcz0JGtKoaqaEoKt9z320aDjhJFan9cWiqp/k
fKqaoCTqcWouR+MgzbD+PGFNYMG1r/ZTvgVQjSVB2iwnPh19KpwkK6thEoe6JrxajxT0PMfX
zP+pXz/WKFnGoCXtQoc9uSdh3mM6vd/TOJd/JhEWlHht78H//kf5OxHi8gbwqyTN0eGe0C+A
S92FfMhvPMiPEYGcIs7+GjDND8gl3m3/vjOYf+D+ff8UFOjwJ4Y1wCONW1wD9+A+LwEZ1Q5N
PjWGc7jS1Z07ddZoPognBxU3EfI/YaeZmwNj/bYOYv2yDlr+7IS9cpj8SaQFaQYxRi6vve8d
3AT9f9/Sgphzfbbbo4F2wPm/3fUM2DTKWHAjrrCOMy0/sriO/v4EtF3FO4eo5K2hMOsi0vsJ
Xe68zcU4y8hFYuQuLjbaQgGGtHpfU6hR/V4siWcCz/Wbb6DkmICDnd4xMwLsjXFJ4V6g9pYo
Y6V2cZVxqDa99WnzgAPqxoUiQADRmWzkroLVNh8BYTd3KdMmbLyn47SxPRKJ0/SZqa8hL6dI
nlJdB5FE1S9vv3bPrlTG1TzZNTaq7d0iWbe1vmM8p/z/4+7NA6Hc+/7xEdGGJJS1UydKi2TL
NupEOoXJkUbZikJk7Oswo5yOLU0dR3bToYiJSdIYjKGs2dIYZDD2fcxgLDNmxvfqPM/3fnT/
7jzu333/ft11+cP7uq7P9vpcn/ks7zUQzdILSZGcjAb8tyYZTRDLBe7c2RNM8Tj/sQza3yHq
MLWUpuAx5CZuCIl721CXYmc1v3zNmMg8JXPyRS3ETP6aJzWuV+ZmZyezFXnlg0u3dsDedLJt
aZraQwnLyUbr/B4x5oEnn3SSNpSF/qRpJirKejfwW3hW10zgR+kiacLOKv9IjJZ8u62X2KRR
wCTKU3rOyI+Sn/JoMtk1yyHXNQtuYhL8YuvpW+6uI0MfdZFedrRBDdND4prlvQSKeoeBr8hn
vDYQH1+PJYbB6qde5IwcRUHYOHnkJiWLa6S+W6Glxs3jJx7ynB74PP7bl/ueCH5D9rvW/tm4
28DP+QgYywx5xtnzhr2PTA2XPZ3Z3r2QTa3KZPGtdXAEfQd7qEPBI6Tejo2u87ndXoyAWf7r
wRAI4ufXfwR33c9TGMedKt6znm9eufRnpfyOmWwZftFoitDPPZLqJdO2bzIvFA7urbasMvKB
JNSr7SRRO4XsV0AXUErE+aCPVG7CCqhbdEJsaJGH1QV+cy+BeC/hFsGps6UN1M1B9nU93Zr9
ir2UkiadaUE9p77BQCkHso/9XQiCd5Mmz9i76/9x9Dw5asmFtHImpxvttxKrenR/rqZNBrwB
DDtZ1JfCBhvTAy1wNHew1C0axqkjBpfpIo1AGynoSnqNZezrZpyKB3C+by7USRdUUu7SRD9U
NzPzn32TLZ/EUrlX8y43N7MT9WPLovnkHfHKo2nbmZPtxX7VwlewW6uvT1rtYrJ7JUqllDE9
NH/0i80qAi7zG4eEEmFOgcBEOdaty4ltjnE7/ZbkHmxgkdtEFemBKmMHHaLL0qaD9B63o9/B
R5bbPxoMlhCTBZo8s92Gp+4DrUx4ZvTs3Xt1YYPzxIFcxrOZR6pjOGg4+HlAFvzs8ccgkMTi
hEXJMZyzTve5JhLWwrtG8pJ8Qm8SvWtEUyJGy/FjzOtp42Lhm1XVdc3vCu9GOGFws0ctXMkl
jg22fhCXSLaaGugVuKVVyd39iDjMUr1x/Iq/5s4m8M2ZSzmZ9UywuuznTIMNfCVZ3QzW6MAR
A22PM9lciyhg5X9beJOh+VsEJC9r0JiVe2otO/r1DKP/0DTC0pO7je++k8st9/G/SUam1KHe
iBDHoqAIsRl5lLXXIIQYo1C3ef8arf+aKt1ifwJuDZmv+yPIjfQ+Jn9R8MlgswLkrWQ05bVw
F9BmgWt+VdxNjISJR3mLz68GIM/Sf74fNe9hubykdWI1JDHHjuMGz5dUwUU9bxUcIYLVzBT0
kjgN8meOK/XtUX7PitWJv0zf1IK2/DwCpcWZLAfwCT5OyI8kPkXu4GGvrYCEHvx8FsTfX//+
lUkD+fqIS6cWHUp5g/eRjwYYJF26jbVI9ZP69g9ji4Dwf69aeB+os/y/zwXtUXgMAv1gjEk4
rhMgsdSQzUDdnNg57JKqnTWf2tCOicIhL5X2LbEdHFskczIAhi5RTr7O5YJSQ5bQZrUTkHdH
KZhL1UxwZplHb4/2ThP/xMy9B7IViIUo12pbAmTLVRmHv7C09fro3GbgHsUW5rjoBtiQFhV2
HO3KbxaMjfFXsQgPdnxl15TsXJTrQpcIxCfmE380NDTpOHuyvQAzAQ+HNncUPafgk+8/jQtQ
U1Gk2U4SgoctAHY1+Dn5YmNL6wN3lEn6lSKwzpzYk2mCsVm+P0r05eHJ4HQj/+Wu0ngYdquU
pFKThqV3Yr5jU581lpiu++vc3/VwmPwzXnqzImKAI/rr5omutiUZ57PZ7RW1qDnfcGCH9T1e
0qfbd6C2xlGKQkZGSc5TtsCv8uXYXXuE1MxxlLX9WzRSHtiOX1oD+fewHW/It6l9HKgmxynX
8gzSbwTdMv45OQfzexpW7KIJKde1VT+7CRyDB1TvotfoiFWv+H8uKQ+GHCfeSnamFG/SECD4
GnEPLSXMw0WX9O6cO/lXysBuPIxckt+Tn3wgQxHgXsKNVOWDgMOwNIftZ/jevzwlxxP5KC24
Pbv4+EGMlEWPVXx1YJefmlwuLsom6GjvvN6tkBsKOcm5LFBkTMJRW7wlpQgQ3jSSLS0hQbnO
LWrgZ5oWD5ot/BA3lxru3n521S4WhYN1NXd/fNib7NRo0rTrDzL3dyZJnaVUZt5PZqd/kNxU
XV1TWV149y4KVgPWL3G/XOSamBXjayGXk5WIAn6LhoYn9R+DQDr2qeU/0EV2elcDorcXfsgo
eLgh6RnxdtIYHMox9UH0qIE3drlmYGNzHYsuNgad2pYUaqo90ITTpHtRFBMxLZqACXbbMtPR
sEKHDvfxaaSLqeb3TfN06SbduswmKa8DZNjgYHdW6Lm8K8kuufqJD/xkGxsXkwR7ZtEkx1ib
eotsGM0p2h9W2RBJkG6+bhQwdyRgtuaoHuQuFPlLCUdaN8jBldZXZ+ossLT/bbl9YOjtt3a7
Xf4YZ5tJwRMO5YbosgImIqNnVToog9OWXbotv+/dezBrb2JkWMuqL/iJPCl6EQlxFjfwQgi9
EZinRZcdKXpCnuzrRAOzQdzfpf1ObqWN2kWIQnGUNg5vhLSPXrjE1y633YX2Vl6xY3Ky05zu
SOY8/r1iDbBf0eJaWs5jBXQetivUppknelIX+kToyaTUQn0Ot/Rqz2OgyWekbCDvUZsRwEob
XCMUwLzPTBxDX5q3J4b7hK1CxCep73Mgy3NJ1dtxMKe0eK/SmMlNLq+N/xr7vFWR8+8EnHeP
mCl03v3KcD2KbDmWO06nW4hN83tVrCpjDfJ/W7mBrPy2QUmjxDAb7CCVtGjWv4QryckkpOGe
WJpONc8pyGhlE2+jII+UCPXRWXqvSNBEMbEmUXMRsI+a9hWRSzmsHR8Tsm7GEp7Y5iarWM+/
xAYdqmOrgoWJP5qYiw8L5oeX482HKNGczukSde7T7I5s91RdZutzmAnGYsxGJyTOUj2ozG+a
NFRksjhbRVYnAW5qUsI4m/qpR0O0K/qzhX1zqkkFuj11daWql874m5qL2Rmxl43veue3TgAz
hIWJkaoYX+dVAMY4wnspqOwEtkFyBdQ/UvEBrAwT9jDLqBFUyDhiNUOuXvYzCQxwzYpGaCal
z1uKDQlodHxYTE8+mDx6u7BLr9y0IbNxufWPbef9ZuWaJRurMWpXhpf9uouMkVt8u4M1dmft
a1HbVWSTiMqkvNDRukCaY6ZS2DBM+MOIpFgbCgH10BUTcAQqH+ya9Swqy7H9gXO39IjCvW5Q
x4GOQAhx3lQEu1tKZcC6VKN/OHRr53wAzqd+iG6pP9iWiD6gaPAwPVMXknyw6G3P3N2Y18UP
XZugB6uLLtZI5hmJ9ZbMOOUk5+TvKyM75SRFRuUm5e7FCny+zwN2hBv8zuP6fEhVweWIWGns
/BlZBAgi34J526Wz3648LdZgJEfo2BoD5Rt+pe7x3BYheuCixdwy1jSb08PigCZ7I//w71fZ
cWh+UVId3tkKTCOfxsiXru9iGvEeZTeEi032dIsvqDNu2f8M2B/cBpPZOo/yOMf7tLZ9Cfvn
zwXj/EKY6TcQH9VbcJ7bXTcHj8WwoTMqEwsKjCCBP8KA2UJkgChV7FUpnBZPDMwsecGUkxGv
1/Igq9lOpmU5kDG+i/mA11D9ZxmKIXH6pYZ1e08n8/Jszg2gMjU9QM9HbtkW+LwpssNYeknX
uMuXQU0aHUjgInwyB334/txZdX4lpX1qe6ftbJcT6NR8TAKsO9c1v2QE3mRpwnJyci5rDE/6
aC0VNLPPy4EmF140r1/5fATiduIKQgOaT5bPs81B7VelNlxciEQdbjz5IzE+/z5ewraqV5bk
+qoVpifzyl1fSYlgifRJiDdciJwfK1SbQNyUtxJA0+TQRf4iPZVduoc8rroEH03xqHa42teZ
1ZRykTVapF4Lm1NTUxtNSkqiHxe5+l89JqfVCD0YIj4SAOv9cOJh0a2QX2IQIpKEu0aaRYeV
S4MUY3pKyRAsjLglav4mXezY9h8aE1RKGx6ZHZ4oO9SbvnG5+KGZmaBfrlPKld8kfMCH9kai
tZCCz5JDyoV9OyBBtN7T2IWFvvaF9NLs6VBc7vWbJfnxcR5qW1Xk8RnDMe0T0c/yk1DqVVVn
D/u8Q8t6se71yX8YaNLMu9xE9lJsz0bBEJrNfskjZLaD3oxJhyHZBJJQmfvA//1nn3sDf3Bu
a59PNVGZxXGXx87D1BEgs9fVmLcfZYKJ6R8KlDhNe0Y/y/Hd3AhG+8VhK4b3CaLRvTp+BiPH
sxn8m8diITBhrx1Ee5+PKLgkaljgQdiXAX8H+sH5kylQNz2J7A6MF6STBNj//PDBX9fb9FV2
R5vfTcDRRolw5Zfxr37D96THXl8pyf61qRqtW0D6zt/LPEEaK6BUEa+loHfgumxoB0fO2tf1
D6hZBG6qJxo23CH/M947pFy5Wo3yBvuK3VbV8mA7pLbcYamgMX0WTziRg4c592a5Zm8V7IAH
XgnNSecdkm9BtBn/rtvyKLfUkGxpMSxke61/xFXb31OdY/1R+7LWwSKn6mTF0gS3XLiFqXrt
o5ykxMjI2bof98XnP5Q1GjjyXL+/UT4zroApUy7cpW69k3SpIM4YPcg5kKzq4DiaUcKZUbcY
FchhOIfp7RkG3JTVfOw/WktiyrpmoA3tiowj4hMuInK57NLuUjCiV8JCjAro9j2Q+/X/9skG
reB2zwYhIJpW3UDPPbj5Mxcd8pUjyw8hrpPV74ps66LQlw7iUXKZbTNF/nN1PyyJb21V87/u
zPCJ1FWmWVp6nOn299tqO0oM323VakiSfxVQnbTg+uAs4/+W/9f/DRuDseZ9PrgyVxZHeC+W
uVV1iU9bVgfztn+hEzv66hYg6lM9eXzPZ3m+lxu+P9Oc3RjakNYcFpeeTeJFpRiE7SIaRsM9
TyM7JqdL9vW+LeI8fvhiDbzfwaIvEepDZP5NmeJG8AVj2M+avmwWu2wFlN0rSA1bA/6qVx9g
2PS4RixFMWlheoPwqb8X7Any1d5Xo5nZFwNhaQvL8k36XAJJ3veClaNhTtctwcKpcMC/m6Wt
j6k+pxXQeXi4Jx8rc6KpPJBbleYYLftTW+47soYbYRyQekdVFchx7PSTnYfcWyG/72sBX05K
znI6PdovuilgUXZxIektTHosQMPUzQILrLk1XQWuYLP5CU47zVy8Nzd7zDAgKfJB6n2zEgQD
Ex+qJmPfUFvbzfkJ78ame17/SDc7Ymlca/02A/tH63Aig3fZPoiuKr7zpPvZT0g3lNkYj2BT
5LKr9FuLHBPz91rHylxpIg2g6kVMAsGKXF9/lsH0qU6bVJ/QRnBOk8I2pu1M7ZHx52PJr/tq
Sd4MP2FX7hR85mFvk6qtBFmdPLN4MJE+UbXBvwKQhD6xvfpypgB/Mr+J7eDW0M12T1EDP/WS
wiSh6C4YqoDsHShbztE+8/Sg4A07qajShD+7MtsZOZnHXZclSAt8B8I+NfBv1ybZiRbj8Ob8
Ucwok6CIZZ7bx9jgccIWGvFWP9O+xcVK/JOGlOffkn9PBN/jtJv5gbK5tBIEEtFH4t1+BukT
EmpVTu8WpMazl0txhLuOrFN7+9bA/B1I95RLRpFjgHbUEBpYgQWbfJ9k437UVQ4N6bFDtktV
4q6ugX7VK/UUzOiTuUML9VmhpWHhF853GNp/IEYhoS8Au5S6H5+A+MT0XQLHHz73SMM2TMcl
gcMoS22TbEKJc72d+1Juyk5LeUIpWMKceRwR8WDfWfEG0vn4NJUEnsB4aakVyYWTQu8+r5Of
89DWINnRoUNeXlM2YJa0s/WipU0wTjlXqcwCcvW/9QokpicOvS3lnBiViizWcAx87u5hHvs2
Bgpr68nUjCTYmk/Z5dLUmDcfuI1QOzTkCrA3SxOMiZo+zNQG7U7cvnmpPKhEKxRvqbqnUGVT
cRJuqeGtXGG1HNZbmRRwNM0ZTAbvNPmY+4zzgWxLtIQV50cTSzJOJYSBQNEiRSGupLl5ubgK
OSWtGuqHCay3m+Z4OrMLbyvutiOKR6/A7M2JmrPwjuJe2Dsl7tc6GnFZ1zg+Na0/zQETgMvv
e9dSoGHssXVHtbqjOc+bzKJPWoJ6H6zqY+DULTbvkVk5etoW+LHaKiNbBwxAisRfNZaaxady
eXDYeCEv9tZul8+yfDc370UAY5TYPNrtcIZ/hohaxg0DBoIqEbxcAxw8f6rhXTj7eVd9jvtr
2nXGiuBWQE9x28D5zkihx3KYD/wf/GKWr7fxel7A3gPN3Lc1X2nM+FfixSIPgiN/Kds42MQX
ggnGUivxFatRROfjqfsrz7Jl4gAbqscfp+PVF4bgDi0tN9zEeS/rBClhqxN/mf5fVt+NnvhG
qsaMQnL6gWl8XcpC/rRNmZ5bnD7ncMgVrrCT41hgqbq/0C9j+CsIyYLbSZirlmnhjork7tQr
sEA80TV5wA0n4Y8WepOlqLuQ3sP5sNksM1/xISzanTKcqZh8MzIysuePKsPgVq6TqEpDzYcV
0AQ5fpmWzd6lkBD7dAVExhxapECYxwxUZM6vgDCXoPTX6LGrCDtNQBPg0nMs1d3gfQWnzF2F
l3fZvrwL+edtVmCXPffKS2LoqxXQacFR75tNZwy0Uo+0BSahXh51d/Xl+vOiTvhNiCVpNJXu
WgxxjpCkLdDH7veKhrPTuRzCY90hsYL28wkmBHKhurzD6+Y0W05TNqQqFllN6sVG4Q4lP+9F
T7vb5Zc443Ie9ob80VhhuEsrLtvjgtUweu/o1hM52kGp2m2zznubTZOdaDTRvcQ4vKnYcH61
T5dbBvowJHg8Kik3+Y7TgugOTdGdC/NpHW9j+59M6yuugH5PJegqx7QZ2ZYuaQSq9UYPkrOe
RWeSIwXPgjSEUmBPQnYPU842v3/9Gzab7s7twmiqp26LLEXdDcDVj9hlEtSN1EaLTJbq0Uqu
Dk7Fm7SppXS/Gd0g1+UVUIib1rxtgM07jIrWUSbLLT/0LEpDnSS2k2TiH30zay9w8TUyIL/K
FKJkzSkc5Y+BJJ9fOl6OFw46JaUEvnYczB+yoY1k9IhZ+jAP0uQvR278PdCvQF1Eakqf+DYv
D6Xpm4bPtiJ5HUT/nuL/LNohN5ucmw8cSyYaG9mP6z4fh9styL0ooVTCLwj4yQ+jnO7aPoFW
z1+Iuyvz7vqMvq5JAPOOvHD6PMuXx+639WaDAZvMvuSPpQFi6z6aoYKo4QSyj0ZwnV98ClhG
n6oSiFgDz3dw3H82mWKQzLhkgO9GroDMBFuZedm4fSEG6HTicyCowgGZdS5U/4u4UaghZ/Tj
h1fdBMhe+JW3Bd5c5HkjtYvcyI3WPoXHNWS7Y08fHepAKtMC8sngYEyuk1MoS+jxXx0v0Ma0
YWKmIRTA7FlYT4YpGm77nhnakuFMI7zN6mxTJ1hIT8vD9rP1DgVM2WTdzO8xBwcmOzk4jt3Z
gp8aEgryriye03rUUvGuPfAa+qHGtdHWXlqPshtaUdMeI5cVIn20paZDXjQoOrtS8DF/IkWm
NuBW2hmN0KSSolh+nfSel6/KJotxmbiUQRpZfOEUJVFvbg6ZfTllF6fK48p4IgNObXMlQj2y
8L1wrnxf1SLueEill4JInm6oFybYzcpyMbrg+Pzz6IIJ+mQXo2zz4u32vneBbm+4K6AauZ67
BSfcigqLuB46+e0zBe6LDIApqHXU0kAG1qM/+CY/J9qRnCgwOvtDXXvP8D6XXrJfSmdX7fb5
yZ2tmAn/DKd2jfyZiw6OJlUm1lGRybmJUfiLho2GAGvjN3LY54P2Dg/btqQ36ARpcW86jqiu
44CS7DZ0DJ7Y/RaD1n/FjCZwdE82V3ye5zu5E0D6PWfm0c4CHk84KuFFoBCC+CBPeLkZaw+n
opjbjp21WgPod7EjgeHjuH6VwaFu8N8QzenCOeM35PC7+tvYixpJQLyeG+G31uiA1a+u6dn3
EYVPzBfmdupZUeylfKVn3W+Qo8Ya79kt5i0ylBlTUCOE2dwQozSYIXKPgyk3Qr7y4Ga1GzwN
xxXva4gQ1Pb+MK8vFa6rNasf8fy6eXyKx8B9O/vYUiOwsEZAXak3oA5o1tZ4EvB5ElKSn3Q3
bzwoWTPbCdY/OthdXYeTIBt2wEqckjPfZDk8o4sD+u+J8z9KV7KgIdErIBfqsulz5Hn+2XyW
BK+VuJBixXskNGw7e4ibiaRpFnAPi74rHYIun1kBdbk7sq0U4gPqsAuxK6BXXbXMFwbK9If2
NJkV0M0i1PhVhCV1L7FLi0dyU/hQsRrF7c+qEvLztA7jHBwedR2aShd1t4+UPuoU2mS2oJX5
0ptzOJlGwVki5I0a4muDD1Put+qXaxFhc/pvDUDyqY16+sY7FgT/jHFWklLsuYS9TDCEwoYl
jF1zAMMrExMTwPbqR2nd2vSHqWUzxoeUbPvLYR7Cfveic/G20qHP3pGUc0MKwb/m5zpR38dA
D2SAfaX9CMHqc7qPqQS7991wFV8HC7WBsm2TxUEStYuXpimMg2iHoeU9k8/vP9Kb6cTvvNK3
ADY04aQR6p9WGXdcN+SG+VB8ngRoB/d0HZmA+9yisV3TST7mHc87TA3OhAoPOvdGCdZ5JmT4
x8c8dLwwGCE1PWpuWNX9YaFdJSorv/fJsH1UrkMIScwpiTaSOL/h1AntCrPtDCEPxJnA8wW+
NGKMjcVYzGuX5FnvXJQGlN6h5j3FcsbdvbhA79IF+KNhq8cYQG/SmNwMCW8WrmfRCrJaPpYq
hImLNRQh1BKmd3WzuGkZZHr/FaFrf5fpO7ndxJ28bMCw6/JaARE7kUKuICbzAmpJnb6FEDoX
pzC26+RasgfQd8C8BOKL5dKB+GKoKzVEMNdKoU74xbib3CcPeOx5NzUerlGwPezf9a036UxK
QcKbaOJzFAtT9FzCIGODHesGtma2500M2uClujKBs3XP1ON/V3X/UeXwKYS6OfO26Z4zWJwT
7+MwEL6/oJaOw8bnF3svIjGMU3vWgv01+WlqwX22GSeC3kyKG8jZFT2DyldZ4cQXL4hQxoVc
MSGpVzsuBh2FHTHLDUVtiVz22tPziSm6Xq0b8VDvQ3SsJ4LaPODmB5/vXwHt0Rx9WoWssPgN
aTzQ8nb3464X/66vyCfEvX6Q1tR8mLPwnpTNWTi7vzT+HMcDCMuAn1sW8iDTxwGndCf/XbX9
R5WzARzcAfnklC54mS6JBJzSzY09VWBc7SkEJj08Uqhvw8mKL7f3a4YoujL/rjFZvVx4nPd0
KjZ4sd0iXKGG/1qwieNS+jn/6maqCiDTQI/7kZYed18AEBitgGzcmBavTxjFqs3Mj05KVIVu
cR+o4rbxE3TOUnLvn2dK587ZtPtdyVnQF1NdGDiFD1uNOwpcnKA7zRO/zOrRuoShlqI4Yd2I
RE0lhYf3d1HQl3rz7DtcP8YjtrsfWJ3rX6J/Bb98tTBCgaDTP5aErICe3NhwmWX2yWNs1wrI
I0Tuqlzuv1T8f2zmfZQ8AG4l1tkYW+4FuGZSl+dFA0vwxp4Og2VuEsM/ffOGNdr+VW0CLDo0
sai+p+BXMO0lLRbfKznlvMByY385IC5G3HMo72U9EOn7NdB4Acv55ny45y/dJgvoetlGZAwc
sf1W7bnz8od+l0vwwTUU+gWvgNqlxjkX3PtWY92rkL8RCD1ZplJAHVK3YXOXFwZnTpWlnTgc
LPM7TNKaRilPi/eZLPRW5uz5eHJ1xn+F5tvEdcqhNT2KB5e/I41yDx3bUf3O46ljOPKVMIHh
F+b/b5uF/5VG/vvzosCvxQEulFwSBEt43sIWvApujk6PJ5ANAGZhCsM/dfNaVX7VUWjUoUwP
PR9+Cc6JjUVgEc9FhwQ7fYsyK4esf5ubI/+1cQPGYR7QfoFf5hvxVLVwyXL/9n4MNc2AxVdk
ezhvSfae5wQWjX9O5r1uAJJ+9oUF9PzwxH4vVEQggQd97WFDY360rB24c0oHacU0UEw9gKPg
QgVT0Lb+w/a/ygiu1Un/1LsfDj1n+o+8NULbX78KYTu57If/QVRR5shwH7sD8rIp/qKKf6q4
byWxQMD8SwxPVEYRbR9sjWbKYof/26k70YNFFbpZ8WAtIF/xCLIjzctjybrw18QeHjTbdX6B
7VbcCqzEdom75ge9Vd7KBOjNm2NsFpXJhcqogmPCWQAMARO/GmI/zE7MMYBlJ1JoD7DxooDA
uuXjATCMTTSjOXmcpiZdbTc0wYpTcHyh+WQ18u31f0WdPPRX1Ml3f4s6eU57VdTJLcT8zE9R
J4+tzviv0HybCS6OOI2SbexlqQ1Iks/tQzZPWhCWxdrLp96DRV+KdP4rhf/n5hXraG/GroBA
mhrg8pks5PuXyD9ksUYAS+9OzThb72Tzkq6ZIBAW48sAviaf/vYkPL5/5vxvibY8S9zs9AI7
JBFVJcjyna5iSu1PVS6k4O4+sSHMs6AYztVbVwEMe8XzFqARVc27+gNYl+6mAPFMhywUIoUn
x1sixkTOBUIdgXDP54lwjqItewW0S2bPathA2AuoPiurq5Xa9N+hJVMTr8zoPWXcud8bmvSk
Y76zDdIv5LM6y79Eb7ow+bMcHkMhTU6ZbAbkBy0CubOx+qyLfaM00VM8vutyr/6l4v9jM+9D
5+XZFou/eDa/eKuFEIFknWph2uD6vLOLXVncRTSULSKAAHnUrdH+r8la/g3x+nK6wrHSfRD6
bFoSbNEju/kdaqDyx5AYR7ZUHG/HFRrlTddSArgcvZURTjgJaDMJ69+aC3E+pqtgRp+NTTHi
USEpcQrVd4xZO2uYSkplPxYBo/i1KowbYmp/T2RxNWwgilkW9s0Ixr22eerwrhUQpE2Jceei
9qnM6tnsyq7Q0Jg/yfS+LvQbkZ7Vuf4levvT9mRdH8vXvPtvKnkKzzZc1P4pnZPD8EcuSp1G
MWVO0t7/S8X/p2bmk7V1n6BVghXMJ6cxcXQHW96FG2m7XRjapmRgUE4+s+TFRCiEyQys0f6v
aEj5AzTv4uII2q0WiInryHV8dsccrwbEbzbp4wLxm1XOYicLXDCMcDzQeL4tBNdsovqynb77
7XCFSTnDHbH1T9Fi75yFxmijH4ONkLYxRva/yn3249v086R2QI2PY2YrN+b6OBNQ9Rhp6RfA
ziZBwt8RBQc/RU3jAJoMQNi0ijW65x+94hMtjUDfv3HLbwvxpZdW2ceuXTZnOL/V9N6DW0TY
bZT+9RpZbaZctid3LyywZeub6AmagozYWcVN/6go4JmAst8z1NJFd3TmC89PMf8Opqa3IC6e
0DdYRmUYs+Ue+y99IeM3/ji2F6fh30cXAeZTDdZigSvvgrO+zDNG0JkGzOgiIhPKSnXh/L2e
1eeQv+LOczPXZTowpN0d8KXkcNWCl4Y2+HVH3jsNeZV4OxGLySl9QSxyQyNv+192Fj/o5km0
iAKRy9BTcKkNaObUOGdP/H3zsZlPMS7R9tdcJOBLkkDwydcnV8HjE7J1mNUL0HpNW2SdaSMB
x49UInRwgx3++ts0g0e94n0m/kwg3OlzLmxjIgc09dnhaVUxXyShJC/OhzQLyrsV0NvZrRvD
vpDwrl2RXXIodvlk5ZKxucATbw+wFBDUEM2tbx3k7ujUjfxCtm/88Rmi9btlz8zf2oKXI5RD
pwADz2JdmUyCvOgBcWjLdN457Oxh4z7BmTVQfs3d5+nJQ/CaOffsVuqwrhYkk7tPGVsj8Mo7
0+gS3rqPVjJOs9QV8jCszTMQB+Y+AAPfJrnrL4Ghtst/mZPpPA54nGgZIi9VPJq2fA6NaRDa
pJpf60q7dYRoZM50hBTsEGldjVtgx7x3A9NYu4uczuVuzbh5iXB/Qc+gVoDs6SH+XvaHziX9
0mAF9/FHpaFHjwAhMBtX510Pve4AwMFk9s0FXBHvr1DVonFbBsp/KT6lasC79yGztyaD7/O4
C+up+ZtIswHwqd0d2Y/bdnhxlpzvbEnprM1knQIiBRxpkk1zIKvONtXnkOW5QM/3PF4D0Fec
SQX1rx4PQZ5I0ixdZIIppCNwuYFh+3ubHwDWNqIDSL4lj9sU3J+v76OccXl9/V2oim2flsPt
UPKoSqvs0IQmfJF5lPqBBpejke0H7zgHykXMGNwpM6iIpI255z29TJsMPPFokMGvtRq8gMC8
eSNGKd1uz0e05v40+Ua4+NOBjqW+tKZ41JhpyuMBf9qAb6N1KCHmYm2fkPrqrOuht7BhBskW
ufAg+yXEqatfmpm3V7e/laoYMXByWmDB6grciB+cRyCDd85ryxEGWT/1yyH+Cg/nwkCCdKvW
U+u3l+aTsOQWmv+WZ4woscFnPoZQ/qj3MOKELulJLEqiHhEOsKiL0i4RmVHZM38nJ/k7rF9T
OCkYXDASrJQW2+FMRP50s8QU7VgukbsCkhUPf3vY45Qn1fValf+MtPzGfOp5h0gOqP4kMN/y
cS3nCFItgqwCKvHxjDpcvjZUV350JiztSHjsmH4U7tiAbmCskgjV42mhCQLkU7EaLnbxojIH
HByYojphmVlLeHKtQol6rmhAvVFXTOFQAQwVnBgWCtTxz13YrEHWU51sXPwKKGJIcusXMvOJ
9MBUOfJqjDkVXINmNSWUl3AUz/E8a7xHiytej908HUCnnMygtnfnA0GTbn+hkG/8sdjlDs1h
c+ONRww57hbFE4ls1RktHOXBLew5GTuV303T7D0ejU7Mf7K6Ajja5WuA/Zq8++0byXuHLefI
VcW5+TOGLm0k5r6BM7Jc/APIpc7CMfeiJ4MLtIEXt8zp1ll89WGA0RSRa67MwE8M3OLKSevT
FDaJj2ZcZoJjb6PEKNUOXZm9GXsUXFZjPTTaVr6Yod0/cNdLf/nGTSD8dUoMpG/jnWfZFRnJ
++ZVt4vuWZ18PfQ696uR94sl9eT3MkqVcPVjJXcVrBHdvGNaqCweJIO1v/9GL5cjZ6BMbXe+
brH0+N8nvFoPgP/f0vBJyPm4cjruAAa009pLuoCAMPTQAYa2TKdECJfrgJ3PAuYU98drNOdr
sqmwoxZsjrO+rBmmHftzdu8HT0BDB3nMfen5Ybi9tmt06FgYvAKYQe0RWYshAXqpECwxmZcE
ITwdMO7bePtW68BUq3EzSWyBb2Q1vi0snwaYlhS47GQl68C77qViWwKifcqatsB39Z9mC613
P7q/ZKCLVhJojMTVj7Or5ecbLwMx60TPU4rsAAGZJRRslW2V3R1rf3zf1EnNx6sb+/3QRgo2
JcsTsrtxc6/92AT2C4MHMrYfPqCFHsJkWlqggLSTCkSx1yxeA/BXDc4Kbci5QVdoXgHtdANi
9dptVLDOdrRY4rv6zrEya1/7/Qou0PCNcHaExSVsi8qOmbyWYKzrUmDbsmoUChiMfzMB/wve
xpClHm8tKfO8WsehjEWJTKFJDWl3/xXQj5Lb1oD/j19JMLuR6tkXF2aJDM6dyqv/OBFob3i+
ZXkXVnCaswAmQAiXRGfDb7GtIQijQDf5or8Cy/IVhX0h77f9eINiyWAPvbj4lPOoZ1EugT2z
j8EPK7ExhhmdcGYiDnNUk4UxayD8mguzxOzoy263ENaMkCju7m6ZOCkpHJYVHxNaXnFY+lOT
D002ebgHPLvEqGGpKBBvOcA73P+axR6vxsNnf8ShzWn+WFPhaAzHFw/pgG1GvdkqGLY6zXro
9R1jxCAdmukfZSWxHZlexgSdgNnwmyVW0H5vtbddCO+FQgi7Qxm5SbNuPRV+e2kMPWwO9Uqy
+y8ZIB988NPhlcwnci7AcKaH7X/yNnizbFsaaJV8l4pt8/4k5+tbA99XXXKxqiRpqrk+yXGo
LGCHuwMXZlv6acTt/NTeQ/1VmLg8vx863MlyHOfdRx1YSHy7nv3AncrP4Gwov6Lf2Txx7S6S
GFg3+LSEV+ppyNtu9U8fnUHr3OYBJpetw32pvI8GvGThlPHzPjXep1/e5NUmYUi8F0TAY6Lv
Gp39Db/6YTGv1/hudb7MwCLLrqceTxl/6WSwU2aeRFF4353omUWF9TAv4+c7pslLpwrWwvk1
j8yE5V63Nvbvk5r5QU6j0nSrxX02yfumDDe8+dTgDeXJ8WIJbS3K1HQVr66SUG7lnhdWnyHB
ovnyakYnVF57g81UZs48X+LNgUt7gMgOG8M/S7eem42hWgpNB8n6ZViOwd/X8z/5N+Em42L6
xziyTbTZ52n+Hcjs7C3I7TL8H+wWY4cw7ubUYZ38PGO2rR8Q/VX2f7J9T9RpiLUeWjRRODaC
Omytk0IoT9FSNNi+w6DuKfr0LPzNOV1/+mtVN/ZYMnGTbvcawL/ujo6kmfhuwg2B1rMdLDKn
T2/eeKcCaOvGUPWuwUM5WUda9OwGiyTgy3f4Pufa8dmLoMnkYtZkf417l5Pru47jc65R84My
e+l9G8M/lfBPXescc42Tt1H9nst38aHl0OcTmstcjRiLpTBa74METoDikiTAqvecAHaQDRlA
YOvJf6oB30ziTdBJqK1FkyIZRx282XnCQozpbN6my30mgJ6FulXNPnwDOF1d8E+AdjiSDH6V
+7AGrq8o5D40/KftUnZbKb9im6l5XK1ugCMuoV6HA0EGSgp/arEEoz8P317ywAV6MJ2ndu/R
bDnOagYdvVUobBUeflKS/2EHe6Ja1xFKLjFY9w5Ix+FyDGfOsyYKpdFziZj34eUoY0PF41VZ
1kVuKE9Bjfwxkd4L5Sk8sDr8hTwCsHl8Qb9nQMRl/fLTPvaZkwVu6GpBr1acUu0sKsGNyLEP
dNXkLu8iA/Pfsy+U8Y0//gl9Jbp0zuK1Y3vnCVXeC0BKX5ZOmQl55hmMtncci4cv+WczwnEV
X0b5FY0YNoawLJK1sBdiU56FvEztWYZfjJpbZKgA3sdWQErFh3d9avShyXcJn04WLfWfThYe
w8sdsG46wB95vBqRZwpVU52WgJ0Q18+UOv+OoDYZqJmLrtikOH75to9aun74Q+MUIQWrOmxn
mpoilYIHoU+uzr4eer3sFR121xV6hVwMElfnscVlkfFSaeZUAxPwDxOCmXZVRu8ncNNMwbVV
XDCiu06LuZ6av700PwVckeaA3XylAR2EPgteShqgg1Dwzggsqtwti+K+ea9EJU3V6V5fA9jX
XI3lpfKNMJY9mCbAKcDygy0c35YapodeyDGcfa1/fRuMFRqs3g0IUnZKbvkEQII+3m95hahX
pl6Pl5sgYIaHyFM1ikbIMMntq/EJ2fuI5p6JqBBRdLOAhs8YOE9q23I9+LfQ7MO2j7cublDT
flvwUH2RKdLVRq99Tx/IA7QpN//TMmnQ+lgw+zryQss5r6coRN1y1fFFhhrygQLESIfYhy8Z
n8ct3AKUj14xzm5a3f7vh/7V7CXg1EWzxE+OBy1UZyM/eI8y7lzGm93vfs6AGSzy/6+2RV9v
yRZRCHI+k/BKo8kst/SMYkocwrmd4W4J7RPYzsRWlCa1KIliKfeZ/ZfbVbrZlz/MPkPN5v+y
eQH4dELZR+dPdOJeKqe3deEsfaYMAzYi2Y5WTGO9smO4STvyIXbPoaPYiq38qz8zfw6+uFQy
yHJQzgccehdLovfZod5syhojOKj42OZ3J7LO1LTgFbjTwgb3Nr9cnXFd9DpH6lyeuz7rapcf
m7Ioos81ACw0Jscy7RGXF0OJadTLavTxJYM6IPTpd3lt92qXX4wdWQFVAJqxeVmtPNsJ4i5x
PkBi8Bjv1++kAOvdd8PFH9BfEf6kaOW5Rh98PS0KP6pqyfMxG4LXaZtsYqiuk1uQF6Wlt1d4
ggj6YTSzN213WR+lPhnO5r/lelmMqduEQdZs8A4DBCn3vZQsso36e8fbXTGV94SldJWd26MP
Q4HBLsP8s3XUYtTH2akWuZjND21MpxpvmEcP3ta/uroLxkUCCh0hw+IxuBF4oPX5CwW8HW0U
ztUzAUbbtuK0/+jVeRKCVXAcssKM5zv3Wyo49JxMXp19XfR6NwWAW59ajqT/8xUQnSda2RV5
gheF052dITznTDPxUGJ4DCfs4boq/OYS8W2Us/XWC9BOJpSvgA68f1WKHMkClL4+MOwV3qfK
dSYSSgPTip5SaFMOlDCnk2vA+4p8oYmjHtgaLWUbBzzgJqLArwFpG+6PfrMpbwzncHQOWpxv
EpJ9bbRDgbuwEZgJsQAGIaiPeUIA/yN5FadOYGJ2dHBbPEKetJQOnSbRFwR+ZrpVZquk3OJE
3Z+7W1i0dYap6K0KqFHu2kxYjV+wcF6J7HxmKCZa20tNXk1oq1T9Cuh1m2oecpfwD2PI7Orm
H7zOWzJCitmaaBS1fSZh2pJzYX/n6iLWRa+TsQlEMUssjxzWNS6lEP/EvUYHdNKjUiCD/JJj
D+Fv+lDbVZc5v01kEPOrihSiN3+nvKbtB8kBSrVz+LK8gBVQTN+4JOH+kqQr56oZVOQ5WyaC
4qiA85DIvGZOt8rgexD25d7/ejqY/H8GzbZlnhuix1y2gHqIug85Iu8muyNO7EvJsIsbLF4s
n6cK8ZReKYkT8wYLvSZ4e8QVARgij0YhOmm6f6SrDFnqZxDScq0WYY5kj5nbu0J3Mqa7RwL8
nY3kaFadSf4TQGBYwmnBm6jgaEKf6YHVXaChm+u3VFRXK3akkVMyHWuIjPVS5lxwxZ4+L3bJ
Y/csPMi9i8IM9Z0QX3oc/yXVtNXlfUavcyLmPxv8xnFpGgLrps3GtmR1L0vd5Fz1Qxke4klt
O5EUQx0OXpBrppqiLiIO/PhPt+GzBv3H3pyUuhg9gUnP31/VEpil7oL6U0GMMcqoU8p2uzID
RPcqoAwH7mLC28fDPq3CX7y+4mxMzs/+GOCJ3zXgTpFY0oB6/FzIpQXn79cwbm8MN2PL9hs1
kaqbjHGPatCZnVFseJIFx2r/EwCIdGtbAjRN/HfwQSeSWu+IiLwC4BXTA41yXqpwARxBco+n
lBkO3C/sY3n52hpIK7XH4KYtKZxGeEXCZzurm+hLtDPH8CodBVn51J0aaYfkwahbkXiOlY7S
nzVxmv5UqaJmEkVF90wVWyGR0oBZYpzb/sVu/NKLdaq9ZdlaTwX2np+npJVb5N20BJwkGBnc
E4kd84vrd7c7em2RdenPzB4as302c4ZPqe9LlX3TzzcQey7k/qUBtgLyy6xlZ24Tpz9tHXjV
eB6p7dADnj8muhbf72uyGaRjyY5HVfEKVEknePAhFeNCBePXmSj7AX4r9u7L6ZybdcnOOJ5Z
q6ndE15gY22XQG4YENvEQufZEMnxYfmeK0mzQ/atNOPWRLKqKzCNtpzWVSfH19y733vlCG1i
X2eu32bOhXN1q7+tukKepF+33UXmNrilf7Za6NXLeHmC6t00+x7zsyfkowJVPcJK6b/Qhoml
HMOWyUCreeSuzZKrC1gXvb5znQZ/Lhe7u16RgcW9KxLeS2ROqi6dykvblm+puUR2ch68iYFZ
Akz1ARSyCBS/Z10Vf2uJ+OzvZ0ssNQcFoqF58POARhmgDrKhwv8g4zAlc/Rm5DLo08H9S9dX
3EGc1XkzUZDtHeoj4kqbsfAZL34oT3QhwHEs9AuRgrHwp9X5u2d0rzBC8FemJVWQ9tWOZKjH
HPX6jisAFuEDEyyMRba3V1qEhn+ahdfNxIfyZdWWvTSe8xT/Mx0FF2ZnZ8jFDo7oURg2q7/J
ruxyYXA5dZRX9+Nn+1qxwfbao8nafh+t5Dg4XB6mVeGne7LFvGMKAUbWasaH4FnzF00Ce5ZT
upz0ZoB4vEvwOye/1JFffL4+YZjwuYlsj7dDPkjLuSRpfftJPRfOHvL0b5aImzUlocH+Q5wf
N1/6YhXf9AsJ+gTEp9aHUC2d2cCFhxsTsgcB5bLwwXq52+w1gH095tknd3b+B4fhrpfpw1hE
P3n6TNoz5GH+kTF0zE5valkhPAhGhy+UchUFZXknfvwkcRLjtucv3n43TS6QMDFtWo5QEwMH
xhoYMBr5h8bQUaayeA8TXq81pWs+Cf3nGUHZTye4z5TmBK77vWk/WFAQaPk4EGHTZG3RGB0a
WOjUJAfYMXEfBIieNVVWnzZlHB9IJ+VMy0GOOnfQbCXhQAD4ZVDP1TX68B++Wu8O+GLJU/N+
7yNV0eXeedLI9iWvpVM5PcIeRjro3bcCZjscT2J7MToGu3aU/cNavvmHh4ZbhIu7bZbpU7uW
6EawVBuV4J7/UWP7EryvqAUFGPfnh1j3mb0h6akcPUNL4RKQUhEI9CDfQ1970nT/bGb+UA9L
ljaDRlA/1EgKE3Gwxx6fji774vJeZ0oWy71QR29tiCuZqIuc59jJTSBjBSGtMSalt98hChN8
hvzkaOg4j3FH8S0dlKILWu9Xd4CYacdxpmV8ZQiCd+XItPTo8jgJcLf0qudQQU5BHVV0uirI
W2VSynms0TXpIu+A5j8vrFgn56FdJCtQ7dmsbvW2YDjHCZyCBPgghW0zMMQB9dI/R6C3CcV5
d6nDJZcSAnAf7IgK9zd/tl9fjejbpiVmB03rum3P4OTQv8d0Q5lS7a4Xu2i8s/+lgfklbF9x
6O6l54MxlmnEN8I7dJe0g5J7L7J7aOYRJqHsU1TbH5lLb4ZwHter9QkKz13x4kz4dbLH0gvY
BQDI3o78S0+DexMqCXvR8devu33UYCEtYanSN5elXAXf+iaTBrf+HpsXt3MhlQu5VIfOpBwf
Jg5UFoet7oNIBI79VCsw9g1X6s3SlK24gbIjcKQbyyaykhZvl9lqqQe9x//YD9tZVRtb0dA4
uwKizb1UAVhrj1YXsi56fTteHX708xPNQ9QYTUXdJd1gGp3h1wpoK+qV/OhsVK7lxW9Cn+Vi
AF8WecNd2UsVJlfXVfU3lwj7COuqFpw48pHWqzLTPmxgW6xosGntAaxavt81gGkmO53nLI3e
siAYlRYP03NvCJ3IqPYzru3KTfmD5dhidJEsH5iY/mHTufHd402t5X9OoIMEpsI2PZyMYh/v
N2hrgtKL+9h4vYmYChF7bc+P3Qq98NOR2iXNvbikM5ZcFcgbfIxNbxMRgd6ASfKF6ueUmkCC
9zWIj6IOR/h1Thq/S6M/usVTsuL6/FyJxjc+8NbUqZ2NCRhOtF5oIY29dp72qNPeqm8fpF06
G5w+XchkS1gsatSBKbbW+KP4WXipZxc7lPhwae+pecrE2/ojyP1VtleoJPdueiXsFNOcbP1w
gnc+mvUqVJPSRtwYJVSensO5Rx4dPMIOTSvK5W27Ct+XC91LGh1095qipdmzD+gRjyg8hNAA
U1QnP9RYGLuAneKtFUepnqFK6q6Arr+fP4/0iwUN3fLbNZS9bzgE0bqP2DJwo3Xx0lWF0HQk
XoM4K/vG3YU+twgzX7x4EkyxmZtFwoe0oz6qMrvi1bnlFey8Ocw7I+rDEa2IVmYXLRrRc5Lt
MirzxzJ6XyNKOHMcp/kjELZn0aKJqhzPwsf1R5SWHnOk9QhhfhlpiE8pgdlKsgAmhKWlw5CF
CYxrUNYSDoY8urMr2CYYfsJ5uYgBdlE1OxqM0EK/XshkNF0tOPt3Q3kvKt/O0BJdmWrHs/YP
2FiPysJsAPRJL39413hlyDHCsiqkZKTQZgUU+/KTl8AwIPfegPwz16H5nnB+4qNmRXyw4/jk
G8CPzGvu0cOm942W3PrN1cneftEjivqh1mqvlntuF11dXefd+0VB0KM+p4q8FIeaSnVFRZ5l
t+fmnTYoWy4wBTP28//OkfblAYbbKCAgxoJTPLIHH2tUv/w44MTqQtZFr5O5Q5IdG6yBHLSx
x6lSXzeRYaEwfT8EyGjR6Hw8oHk2UdQPCberbEpC2Tmak5ZD8QJt66r8m0u0hTUesE8r59F+
qp79YF5Jeamn8eydyrA1cPDLDFySiD0foYsxq69naqTmies0NfTQamOyMBJV5F6aP421F84J
9bUYmiWbBCSuOWUwhqWeZgtq3x0mOc9E+NBp41kTpb/13gja1SnltU+++2Mj0QG94VChpd0V
dwu13pzZxvDXMN9zfSac7Bj4LDrrng4xKiwkIHgv4w72D6/swFbmUmJRaO5VBYnpCI4OhqdS
m1ZrTBqXVF62rDixzBXxb7Llbm10yvZon0lx7UG6KfLV9ozdcHKlOyexx7LbMTeqLRbUHsvj
xxyhOU3bELPEmb558vuWvWDjJIrP1FQ9aqEvGDPmlmP8jpVQg3Z2ISvQfhc1ao6Q+Q1s2eif
BiW5Rw9ys07N9owFEfYN61WOxYdq3vZHDz5RkJuO1DPJHpb1o0hwwQkPIV25pxi9Y6iaYOQA
5/pHSy4YbKvgGiWkgMzwOAZ4rKkOzASiNeTbNWfSHM+Ct7CVfX6WgMQMCG1Vzm5Lapvfhe7b
w0iP7m4zTgll5IfGQs15d0S3lBzxgcq7j79hE2KtDdjbwTbl9zjtA1b4h5dG+4t8uzJyJxga
Ic3cDF128QMR/LjX+FQ/erqjgvW4+gR+fKkXQelCvdW4U73n7759pB2u6w/bAfttvsitDbF/
Ol9vDO7V2huNjFoG9SJSrxi6pMZ5FoocZIQ4pcQlUOY5lEXiPcG/rEdlSyiT6tRBpOgCYF48
/KaraMQU/MquodQYyUS+2Cw8tPVc9pkhyq9Lf5D6qpuIHiq4VqL3J4XuZv6rq9vAJ0RwLJL2
CSqprcnKn8umyenKI35t6o5B15zcT3kkp7OAarDfzExNpMFFHccuHTVe9O27HLWsumeqYnUp
66HXe8jLCSrGSWkDmhtqE7eOBGPhG5g8kJGxEaXAI7kHgZoqlQKjmFO7OaCU7eup9ZtLw2cv
L3oltrrNx8OOdYBQXdzEbvoFtvjJqE1kLSxfkxu8vai98Cit2fl1+s6OXnJaVJR3cqhrbpva
AKJafbkirvkcI5P/j/vbO7N0A611zxN44vLJAL/hL9XiT27vEIAgGudexbo1pbcFCLdJbMHM
3Fa2eexoEfMuQcjdQi4jL+bP7kW3N0XQQX7cyVWdwMcXenFe9yNnxmPKrXAm2R+MinVrYCeR
VPMhLKiyAO1WnmaajNOYjtHOJfW+8cTiVvlX5q7JSJD241WFrItc79h9HpRRhb0wjI4JlCyH
KDlMtucsuJLohqEvDO2NZdFiTe1G+VyC+Cs/GbsWt+J5xAGlTeuq/ptLBG353fphMYvdGUTd
v9saq6RFxHaldMC5YVbH1sLy9VR9ftK6nFpcP9JyvlCc+r5UBVJocLr80g3k/c3Xh8HVVt15
jOBqX1MN8xevNuUmzVVxIIW9+gz/T9KZPbXPBbPNAE8rJx5Cg0j+vUkxqpMm1Q0EYvMdR3xw
6wpoX/eG/qzbqqozas5jnaHZLax0iVwDkO5n3SAxN6EbPEJs0RI/MmAxeLS7zfPYWJb+lbHK
miIxOqlTcktGtHuraYnjKwsxsSn+zwQjn5XzpZt1MiuqAivvSidsDnidpkpttQ74pZDSwSjI
N+4XOMB80HzPzFf9kNxysJYR+RZcv2BkdOZqWsWXKvymnwd2QG8bWUJyxPdgsaYy8lGj4XcX
RnQXGtqOhsLS4qEAo3gteF/R0lVgu58bOdN89LzXtWpb3v5x6Us/1uZRpVN6iC2hD0wTNr2q
az0BefnK9SbDkR82Xlwgj7sdC0unXv0rhuYe8dxLlt3pQUsoI7+li4OkzC6cgi6kKvVcFrgk
N7tHgOmeKu3bhHt681WtS1VlgcO+9mh3kkKYbOLqzjg0WN01QZUzDhAUMZKXyjyB14HenF3M
iv1FdXDKHPTin2durc+UQkiiVDVTzc3tRJwcB4F+6IErhD3j7Lmd/ihJ6vBc69sYX4irR+tz
Cnastir1XXnPsc3Lqxv93dBC9Ri7e+6HtPY646Jr8fYEk7o9Sk9pYvb6NsejWDSHUNq+46eu
rrVr+nrmFHz2vc+0HOj6eqa56F/y9qLhZ9+iKjYvflDN3HruzdssXaN7cP8M8KNEVIXoc+B7
ScxOHLHtqWwx2DHlYBzhv5ATfhemHzz25tN8+WGroIUJ8Cfvcv+96PvVHxfaAOvGePkdrnhX
YNhzr1erNU6/jDCWFvA2F4Eru1P5eHXaddHrM+aWT21A6O7gJqHicJZgzgZQ8LXuGJs5Rk3O
PMy1bZltdh2x3Wqtr7KupvxHJpIV2n58kP/atMl4em/EB7Wji/NlMhotfQJSzGwSd3czr7aO
Rn1/IrncuIBqVofjXFVaU3Dz9XYH0Nr0RCxybrRKTmVL+aLaoubRWMPahCLfKwWxC2Mbwx3r
h8IQYZ+sbPWu43U7nvUOvC01Ie8OuZym8opd4GFxD1l08rDs6i8k2qL1h8Tc0JUS3Cg4BEw+
7pKENfC54TpvyHJSziJzUAXq/98NR4W44dkN5fraWSMJLQrb8uyWumgTQcXzcLW7Dw25Sf8v
TC9XA/tPpfluey0bDEA3nEDlmtoShF4V3bvPw92O8MdWbHIf54sYS/fyUvGnj5nicnoXdKtL
DGTF09eCcoJAfmzVA3e06mJBJwudrSrqKvDekVG50TBKblSuLku3yrJbYr5HF5Ion1pW2+9s
jTeTxGX0YPada3No6ybNl20pbYX+Dg/0x2Q5JY/RJVrBN7OeZT02dT6o18WYS4HJmZf6p73z
5fpAYvwDBG8HT1k+zLpuKU5pGJp55MZwTQlw2KscmZiYVeKW8YC+xxBlA2lN2MzLciWG1gqO
+NYyYz3fzqdZ9Ju8cF89sYjGWXImG7kon+nr23d/GCR9fGvQg709dyray4c0U8bFFSn85rYx
+uTnwPns5X6JDlD4pTsVHm9KCY6QdS0cTueOYe0YDvr3Sdu3/mW/sIU1YJNpOXHDiY5gOnm1
JxMSsZ5IbuXVitVleVFQF7J/pnRlYWzthE8EQmcVQ10yojCMDQJs6/7uhtGUCAlzV7dMeQ14
h9Kog/rz4ig0PStx8ZTB49WlrIte38QMgnbE74otbVNydgi550hvWLIleGyhUWzL6/7LTcO6
qvqWEonkjLwj8sffVyWLdyH3yIS/4o3aC5j5OtXOdH+cSNANybwxIWXw4cU456rpmocMwLom
YTg7Qu+DJ1UpgrIC2lqBh9yFnyPfahWPezrsT5PKM2ENNkmYg8+Nz0ISXlWcai/K9JEghSdS
oDMvnU06fHOSZ46PZ+Uye5Cmuc/ophcXUTIOo+FilnIDuYeyFBVj/rC4KNAxm9SEEmEV9VcT
hl8dPSNYeLvPqoO5tcOhLFZF8Vl6q1qX3o1kjnRWT2dk9ICi4sH85LHH6vxAcPGGX1dAFhr2
5YPhPjqO7DPF19jNOYwsK83IVZ9KqD6X5zeCqMUvHt+0bd3cOmzEYflDUdxTC/5Yk6UujaM/
QLEkMIKnojhiA2EVP7DS+1QDtOGRVWao37YunYiGg00D+5vslFqoFfX4OHGesefnzjvkvBof
YeEes5PVR+AKwyX+De2zNBY8xK9Mhmz8MVLAgBnw4WZbEJF54+Jimoqb62Xfljw12xR97iSJ
fserYhWc9ZHrE/aBsL9V5BKkcuRjnNr8U2xccDGU9ugirJSBw3VJ0fVV9I2lErrgcxde5f1n
jfRIyLKCdebki2nS0ilJW4mxaHxOd1HISGUzhnstu7ZfoH1tZBMizqxr/R0aelp1ndaTUlU3
LjOwY+zqFC9tHbuLtS54Y0SvhHjX3lIfVQmS/JNqjV+2I+NiGyFm8o7j+dGj5zuYSUk4772f
fhYm+djDJkF6MP0W/ob/w917hzWZbW3j2MCKw9AUBDwwA4oCgzSl6khxlJBhIISOA0on9Baq
MowUgXEYBEKJgiaQABEhhBBCLBTpYgg9oXdCJwnV7/Gc730/fM97zUSv6/c7x5N/XMH1rH2v
PDtP9t5rrXtJXi8oQXbaEgSvBUWZMlwqRNWqjvNV3ns+UW2M1QwqjC+aFsUm4KYzH9ir0mCF
TEkJQcFhUz9paUzEdfeEgiffkFB6Tzx+lSqaQR6+HeMavcuFcARu0t5lLgzpfzq6LV0yt+3k
DjP8OOKoWWIuMmmSSS7YUrE8/9OuCwBx3xitzJUaUEQ3HGOhRSXHN9BdCW6ZyPKDfNMx8Sez
V3yaEgoQhQR7bFB4rjff9WaM3GDcgegXQFXUMJyp7jlAhiLoQG2qAA+uwXjL22il4fWRYF1N
p3OmZBVdBwUxGCRie+PKxxXSATjNvjQx8Jkt+6aSkg779s4l0rZ4lzxeyvmZoYaBju72vHMw
DC2y2VPX02vhju0qmYgUokrO2eAY+zuiP0bPxbtz05U7biaFzPGo4fV/UFn8bxftcbBRPhEB
KqZOJJ4Kjtugv3zPwzpw99NH+99s/5v9bU9H9fJtQ6kz2rZkFaCdBbGipiZl39IdsRzBRdlJ
5f52c6ZOKQs0F7WYyQmMEjqU8+fw+Yz9zZoa+Ndxw2RmCtmzXjY/cXjw7Vqzel5RjpK8E+Ee
OOs1AeruOF6YkTAi0wwy77D7m8O85qJSXHbVkpTpcIqgavzrzkWXekuKN9myl0MzrqvOhk/I
vMY7xOigy42NISBTUADNmJe+3EoL1ktXPMjMPdo/dDspkjGQLxvXKT8Q6EiLarhtR1mmXIUO
sZZqjjeCo/go2B4JLNi2JW5d17K4vbR6Qq/nyqSEP5o2DteLHOTwRISQ/cqrgOOvh9lYe0oC
vXxgMyQgJq1hNuYZhjlVwzPL2o4SLe7FMfuigfg63ecujtN+gBBLedJSh2O27JvHd1Gjy5Z3
BL1ndH//DrMZ/EjKrqbiVCW4OcSlFhGZLroXxyoAQuf46lJw4+JCgsCcWx/QSa9iX6+E+7r1
WhCfsAxbyWQn+zhavFhUHrpjUx6SlbIxnxqr5595elx5o3Y5JoxwHx3utEPMM9Xzh19ptJyZ
bsxhMFR8YWF64Ed0JDGTj+6BlfqGrQuOE6vDoft7U1nFb3RJERCiJG6sEpflPV3BeMo5f003
QRO1rAxF3mcXsoK6ijnKd+aSC08lgJHJgpJtvV16eTErcoUNMvBf+U10NU4xQwJ7SxIcJwZp
XuxMVFioe13cfmhA5SrLp53tMRT+1jHbdnXLW8+LaTSMeOn428dzQyKiRZfo7+mzLz7rYYvx
wLugyLIcfaNcd3xsUCVz/t1B/6ntvA6Mf3xKDkRi0qjfOtdLZaUMmlg6yKAoz9/1vww8VF56
kw1zpJzmFawx1SdevXu+7AwsKlshkTxXHK7nKE48bueva8ofCxiwc5KnOAYMJDrA5vaGAxf+
92sPlmyiprUBlckGvanHvSQGtWUmzVGDzeoIthFekH0guIRbgB19wLoLhUyuo5ZnWyKtFemN
GKcP1RUPX/y3GW4F7lJzAYawqnNYkxkIxqFEW0qw4Uh3eA2hbhojx5j7mMKE22H/7fX22Wom
Tm6ZjKETMgV1qnUU61IWiUEKOxdVb+Txn4LWzsvOSNSYPRq2WlhdFwYv3Ux/8ece7ena8hhv
vxteO21prXEyJCqGeN6NIE+K9Rtvrlw/QYV68ysMltqJuqJwvMjDGZiz2JfoarDrnISGjgJR
GKmxXz7Fyd/9Pc+7OzO4p/dk1MJTeBc65mB20MWxmAniu6zfD+8YxWaydtJ9Z/R+XY0ZJb9z
+h2L/FtpIMnhh0q/SWb3aY7S6q9jfeymVRDNaY0MH9umXeDXkMu/d4awySlq3UzZYODdI2dq
YxIpHS5pNvgQCzZOyLOh2LD4jvKOhVAMVUdo3WYb/NVFtGQbGh11hQ9Tk6D9vP2Nr2j80tzk
9MpO/fHcBf0d203j/pF7AgVxax5vXuYOTr09FjSqJKejwZHTWNIAa9iky5iXqnVYpD2BC5o3
o8aVGV7dhjqZiWqRJKBC4coTm50F3jOdF3wrrdALNypVW+DiGj7OjjYk26BlTkiXAkRoPWwd
B+HsiY0+SvkVIXWEwIsXixIKiS323DqHNzWo3taDmWH7CYxITWwnXL41gCoJ/i0xDdwWEx5y
+93VewNufSxC+uFLHR0E9QfB5aAtHbQKBDGRga1jEC7VSGTlYOKzgs+iChYkRvakDkx5FTU0
EVNfYacrnga858G/ubi1E2dDEhRjgXJ/Vg0rdadDWFhvu3yK68J27pUSO0UdnWyV7T6OlOoJ
tKiOnnh7f5gpx/mZ5Yd6qV0vvusr2MKOJ34P6uawaSHK/i4zQPPDpFlh6zj2bLShkoGO5vaO
MwFW+H+XDxhsF9Ff77BbStAZYPnwgf1oH3b9SSfOdaDM1wNSTxRyqOvZYPYD4QG/75RC9Fye
SRvlO6ebPG6tgdmZMgLoyIJxs1VZ75G+TegtwfBdOHiOaczQsB2oZWjl4gy2fKaqIi3eGL5y
0tyeuWCFDJHY93bQiOxydZSXAm3yW1411tRGYsoMbwdGJK7eNY3ebYgrmdu1PlrZvJ4+I1fl
p2t43lee4d3tbBpMWb/8P9jhuBryC1BSg2LU/I2kq40X3TMQNTJmYxua9VJRz47pT/mmCMP4
lcaD1u0l471nsS3Iuv3Po7nx6Fjk6KDOwPPlUextZuTfFnqJxFLl6Te4K+9KFZ2d9SHGEAPh
VuWRom6ICrAu6f/DmApRC0V9I6ZUt1MRln4B2xe1t9IoFtW7SLLpZOusvyFDBCWjvu/BIBRo
ghOZZD/tXEtetMcpu8n0HIXrrMF828H+idbevDbDtDwnqAcID4KEe6eUJYFEzqbMzzcgtPH7
SByDDmxG0iSoaP7svBfl9YDWH7RhS0SN/IwQRHCJzLTCZEkebQhdmEpeGlsAI5/BJg9pGi9n
vrbpwkvU5XuIb5oShrqF54++WVUTrg1C8onVqU9hMpe3vAZPTrL2PM8Kjq4+1qeOqqcNdTV0
MGnjmGwJcrzTK6R9+BFfRuT9mCG6drkfk5xXSM8+0mP9tKkQoR1kyKjDrCnrRvFO3hmmzhvv
+ylksqM9OmuQf+fxyySbn4bny4TY+BS7WcSvmX4l2xPyeUwzeDxSAw4LUW2YkWs5yBiw0cji
z822KivotsCWr2lBnbNBUF5MybQmDeEs65owoW1vQEymqpcYxYJDFgtQJfS74HWtmaTX/Lob
fI5LNm9txCPpS0EKnP4a3nSsPXbUUbmkW0W9BAKFdcHAoYjChHNEFeU9VRufsSGy2Mhxh67W
GF3MihKbvOO3VqwkTsGB6GCRhFF6HuYOWoe/vEoJVqMwawZuGJneMDwPLhaF3aIp7zjrDN34
EZhjQHotOTKJ0EgQURNPqxMI8x54sTBIayq5H5ISBKsNe5Q8H28TWZSr6U2nji8GMNFi4Rv0
ZZXz3VIvbwme3j1HD77nmTXLtEuGBtV8KyqL1F+o1uOXjrye4KOCLn/PEzHUXnn8Xl4Q0qDG
LrgEK7QVZLhGSlGZras+dT1/4fmhP80v2T3M/5O5DCzvrQEKTAZy9uXWyEx0SKDF7WpbkhnV
o5ZEzpWbi//P2n+Q5O4CEe/wBmodARpLwipcryujjLMHa3e0IJ5Sj0VqGdLRgzlG63vOceXy
3gPwQh/0uV+zGfMSNvV2pDs1yr5s2W+DZd0XncdA2K6ts8tgjy6YsX54knCHJMFnkP+H0INj
/XbAF3TUwEaRPFswLyFfHzHD5vfO9116jkLyyYmdNwWRhKmwNQ2vHTcYhtQxnjvEaBW92hHE
SE/J86JLHblBLT2TGMLJsFy1LHWOWzEzENI3M444GB3xovbig7odEZ+oHzjEOsnTU1oO/AUY
L0jhpE0ZZB2ViXHD67ffC6rp0BPXhwB82pfVroYE/jLG9hw3S8kbZGQ9p9uHbejeE5lC997v
z1gL64zJGaZAakxCYtOc9mkFz2xqnJMdsyF4+7mlOievzNDgdVDP/pR5bEnGxul+kKhNB0E2
NR7nRbc5Yk5VYZpFCWoc3hadu2WN0aLakYDHq52KpFt8xm++NkBaXJhUQpaZltOSqMf0Zsz3
na6Lft+VeRkEQPpbIbrFwlRdaw+UI8ZZ2tHRqVJaJdskVZz660pOLb/t2TY6yTGzZMdwELcC
gprkEyK7wqLqmQ0PpaW1PY1iJI+1JxedCD5L/rES/aL6+kX/uhkVdn0jwX1CrZDk/4q2Wrmi
b03yK0jsml5uiCcp92mfQFWdRb/87eUGlynEx1RmBos6ni47lAzRHNxoaznnDmesT6OllVjs
IuPN6Knce5rf9ot7J5J+L0SK5uTk36TOhlgojEOhiwlXzlwGJlVnCSa0a+nSqcGetXa31jcd
c2arzmraHkj3gRiLKrGf66xsnTvl88L6CYQ5YDGcm72OAVKvw8A9+4t3z8i9qhuM2U6nxde/
2jh6MO0f45xd6nSrnUap+u3EqQz2y14diYDjcVuPaAWsDA6pCq9wtXmGo2rZ8J7HhXcpercl
rmRuT14iUV2ODUCbgjyZ9ihj3Gx59Q9bp58pJGzdzgqWWTOvs9/a9+n1PFwB/Ncq8WavuTTd
j7xO0PmQRIZxUyfn9gZAOdHdNb9Wqtm8q2wsBEfx7hjGOOpkBUxC9MKjr3/4cfnL1+l8DFSQ
k+igaUOB1bO6it2yHNvSna7VlmXaYS3N6VRfnN1SAFVZAAJV7DanTeYuSWzq6/PdWLqRbu+p
XkEjUipJr1tnUx5Nl8IQawr2HiQPSSUoSCg8EAKOEYYC+wznm+Ir7xKzYCfn+B3Y9i9HRb8O
KCa6uHnoJlHlaStevQlLKgqtZk5i8Uh+pjmj9IEfxjUBvRKy9hLpG1U0uEc9PfnlsOTbbgLr
tu7xO2lwuevUmfgVVglTzSEzxdrTTHCFUcT7wNcJY3Tx1M8Ui3sEDUXdppdtiNLiIabxD/i0
4NdYvMBJtdZQAf9WAXUMgeEy5tTYo1nfLbc17j1LIBhC91YmFtxyGcjqLlMDdgOiy/JInUDQ
Dq17cBJNibKVHJw5Oim6g9N6/Z6nPGV830bMpTqAZK5tESi7kVm/8sbHI6W6dVmgNgzh6Yao
jxWVR7FKy4P5v+2/2MtCN4rK0nwFDcwEltKZLGRS3AJEUviC4N+agnXCT0y8vk6IJ5SNXmEE
KY+wHuNX5hvyFNZ1NavDcvKys0yV9aT0DUwlj3YbUA6fFj917PLkObTewUtprzuDK5JgXW0j
x9RR7LoiLYm5GUFjY86lh9KOisYNqfXUvrFw79AShGP8wRfcRjZkVortHRLH77kN1/kLRkWM
QJQFl82p6MnghXkauIevvUOPNzGcsKBzXWZ0ASg0lY2MrT56KaXm2t9LTcX+1uVgQ37ql4ma
ZkUaWTGsIyUGlWbO1jdT2BZuvFIdUvp5DQc49ypHkmmTsERLMyhORFmhW2DngS7nm492SAJX
u8+pJ6zpHnNb0pNyrCfDnaagFkeNGGNAh4vmr7NhhiGhfmeZFqBWxzV7sPYWpAklx0DtqfjL
Gf5PClyGBy/zmbuHS8IrM8eYgyOqDRzkQcFBwsLGuStUv7wwzpyWhtamqn7Mb/9k/j/gD3vy
yY7+5ENNR53YzCk6DdXDCjONBFL+ZpPjQiL5DlemFQStBw3Xlg1OK5M+1A6f5cbn/TxrRqss
XxW26FD4aRDuJMfBKcmWh24rT56yJBIrmHOnbDLNWy2KbkM8anRm8qRdVrQ6YBS59FHt6Nik
lHekbPp45YUAnav3erQs6r+F2JAKZxHFCF/ZSmbfmexQkt8YOOpbc1OI7g8Lyjp3qk5JTeFe
JZHtkm4knTLqCo40EK5rpJZjTVE/G4fooOhNm93wseAFZYiwFVIjtX1Aw+OXrapFjTuVf4ws
5seSomBQkby60JCeBxa3Z2RaRf2wizi7lfbGbt1QPidgyU7I4Le+qNfS9g7ntmTj0de6FAA9
IZYTh2I8RnVDYWzlBVZmXlidimoLSDgEiPaYG928qqdmp3dxtkkEr32172TmZozLzdvU1DvE
8hCit8p1RKRmwvMpwlLPmpl5qJKZCsz5LPJwAibhtLpKag3u5Incu8MLanjoA5fxi/3tIg1h
fxjNOKnXVXKmVhqSCZKibzjmEBXIi+uy6kNvCRYdSY0VatkKNtc7fdzfvG57RQHNnhTB5AGp
BkT9VjUz3eprp72fNqDLfo0iOeybiBEamUSPhm56u+sd7ToiFP3xrbzPqBTbPjGgPRzUhdiE
FHhY//pYaGMpxZEuqDuZlz/I574a/vZMx7pOWQHVKEZzfqJz7TB6EpWBTxlkNMSx95AeAeaS
dSs2WkmnBIZ3GIgdPY1AaBZgwulrpqDetMBCjPxUc/4tt2y0ey97dDQwYhqZ7tK4keDre36b
hnhZc3k3nF9LKuDMlmQ9T68yZV0lcO/qpP5GroghzECQpVy4P2lZIs+UsK41rHigSjqDVFG6
Qoo4lcyeiOglXeD/s8L+3UPskrnd3QDd6obgx4FudQ/6CfnldFmgxLf/MB2o6rx4SrmF8/i1
FxopONihKXlgfocSmwK0cLj1Ytco/zGiKl8xqKlg3MmjA2QmqRJ1s850FuAK/j5y4PLFtvjK
JbBS2CDQ4k4jJ2hzW5H//M533+hz4/qHtmqI/Nyab1uoysKGScoM7aUlqYMSj1O6UhHGnmGW
LJbo4YksczN942l4SmSHRDWl+wUr0s5B9T3PKl+swwjQQsBHKh3aqre9ZxjKwZruZPON01bA
73kuh0B25Duj0HvWA8Op73neSgpHJeClpl98yrX7Xi1Yw1xxfSV1O5I+ueOkP1qFO+xTC4Dv
mHKfo6N/9bNjiiORW69HTOYb6ZXh2n1ZSh0PBION+090Lz2TngzNLEnUAFZXZjoj2mKyCJmX
yZ0N6ZVB3uezp3yxacXfM3PSirZM+y/RgjuDGPkQ6He42gZ3LEFis4fcF2llBFsR4vjamgnF
XOD2Z146qsQkUFQtkt+tVE/KSdyOoryqCIkRYBN5ewPKa1eVZLQvlbgi3N/gLEnQEObg9lpz
HBKewdsN3Ke9ZzfGJ1oYQ205oEYmSOvuWkDwMjj0RYKz0wB28Dev49eLDn+3LtGTKWQmcKlX
s97AwdDpp0YCq/iF+sDuu/xVRJeeRb7pxKw4fwKpLb08YO56flcmOTWMQIbrLN5AnxezMLz3
oeLIs0r76H2FB497yOBiv2xxZWhvPJ9z9G5TXMlcbil4t38u1TnWdgBKClq16KJ6h+lgyEYj
e28SvTt1z/ktvKJbyFHy1e3jHwx2Ly56Am1Ael5wNfwXpiQzWBw4hX6YA3AyNttv1OMI76bX
OzgvWKs/EQSaeedIK/3sC8gw8IudH6+d4MY1TXacbfWiUqJYm/rIiMNBFmqCpnx+Q6zLGf20
jwI/X9tSRyzBhNH0QRBj4Dsgi0FJy9460b12wg9omQnll9hhL1Hm72wbnnoaRXt9L4q85b35
KMr03lmHNZ/hwYUo8Z0pqc6fm6DbtheDNwfr3/NU8f1/delUspemu98SudKoMhAm6rO5z3lB
QdDkTadqUZK0fJmL/DhGnjjl0eUYbmc+wBzi+ApABJWVVQRUzQUo3ObZXTWyUYDNG31nIwUz
Bie+6O10puqiY6M0ZOM3T6zevXbp646Ct6E6w7LHhEKUgz1HJlgblwQ0gJ824gV+NnAv9l8K
JAzoxo8GH2ehQ4GtfEUx/N7bHWIzyXv7j6+FqWzvjopQlWHDHFjKXiVX8xkJEpwIhd0y3iyD
u9B5PypJ3ctTlT9Jb5tMj1ulwT0IiWKGOgXrTU436jLjdjY+VAKwvFrVk8S93eA6mHCx73yK
nMwEZgyEDJRZd95EczMrPtLh8gt6iO5aZFDiEXDkgZRiT6VwO+BhDnjkLmTdkCRKNB8a99X1
uveoY61SxGlxX8Wno/gI0r/nG0O2TTaH8LJEYjpSNF3Gn/GGucFQAOJkYkep+RbpS3p/FF9V
Ag55a8Kaf2xihTmNWO+cEe/7FFeAxJ4Rueut8clLF9nSjpEPr+zJ4TLEtv904APamc5LlbW1
QA0pinlMS6RgDeU9Rmcu2EXfuHeuymtb/GHy19NWFltHOFlS35fBkdbjF0UcC9ibMWUvgCD+
wYjbgddV1ite1OYVZFKDYMhEczj10kloWFj3za9pTTU5YdfGU36BO4NwwmHiTq4W8x16hcQT
IuFnAAPl0bucBHrKeFQ7CMPveNuJZS79MZPFYjByGWRS1+KEzqY/z7OQXbpcilzuFa8etzmm
OV5ySx1WrLN1NOeBk6ROVuh6Gnjw5tc2b1gB7qce+yQD7Un2ud/sec/DB1PYOfOf2YB6v/Va
U6eizTuOxlOjpuULanMJ5KyAIapUxG+eSj9kn6kbQ3sMAl3EW80sKHpGFbeb9L4ST+DyTvxd
bd9wtzvZML4AmuKuSEeLzHXo04bqICGCfVobOZO0A44cr9rihVfHZtG+gvfE1lpFfd10td6G
djFtiBCcuDtJQ8vMD1GYy5qHgh/KjVXn2r/jB3vCIl5Xhww/WdB5man5kFg8Xx0B1pCucsvz
81twNvMb9xeqNQPH2pnpXotL3rkWbVX9Md79+wKNO70nVxprtTQUQywWi6dPdDlNunHSE20b
ursdag6N9SFui8l2d6x6BHBUb950GqECz0uRaZTu20sfDugua5i3muw8bpf6qmiAONz/kvDE
ySolBz3irOAv5WDnP383VB2VZhiLL4/4mqYMAijhUhKNjQpFmFRjox4++d1YDnOmIDs3NNN+
Hhvtz+paU9QwNK7TtWfNdIdronsSwtor/5GsvfsSLmTuKB949hsEvnyRGPaeJxaBjhl/07Em
LgFkREXSHOpjgjY83FOxy1dfzREzkaKxOYkA9UfPzEl1ylfiqlwA+OJU9p6pGh9MwPMfHWEv
95fhBpirtJtGIzEeVVZ9ieGJixOV73nScFYlUfW9vpw9+KFP8U8XBF3BqbB02om/XXa5kQJ2
OfqeJ6iGr5X3bF07uH6FxeiMPFkk8j9OY4CS8uBCbFz1pve2nMhYKzx5pr7jLCK8TNjUINuh
VHXvy1KJ6t/+XioFfZ3tik44teNdLFnn71CnM+lyOR4VXiNcVexoHJZq5O3zcQYwX1LzH0BP
hr5JvKo+TWVWf28NWVfBnlHNWhxV+onpt2OBz8LQkfbMauP78ciS/P/bFedT/P1QVMNNMyUe
gR+6FWvNcl7ez2VYM2GHdSt85Jbu4CPO4wwYhhcD9cFNJR6qYE6/ItDXq+fTAHwh2nGRlWK/
2I4oHVmlHGlOyZscC1qrvr0JLBCEjo1ME5+GG42lxlbmkEJajlbjFnt7RaPu8zZ/kmvrag5t
1e09bN0J7lcGB8L9XQmV8HR7PMT+AiO/4Szh77UjDkyBuaDfLC9+GB/a8DU2LLXwNvYPs1EF
d1u/xNxrC4yEtfkV3Qa3+Y8fWPsER7qGCeUhkGq23cxIgqoduWBGDaKyrOwiNt6IXL5ycFs2
aM26W7Pf4afk7XIJJYtOd+YsJN5fqnl+7LLcZ5zTcpmsJz1aYpJlRxeNqaoNXlR+jm9xY8E6
Ys0jZq48k/i2LF/pdzIhBSgrt64odoy8F46ZB5i6Gj7po/9ClPccoXuUAZTqNi7TqcvVEUlJ
kUgUEZklyFJ4d0hlLOXwd5f0h4Xjkhki76gL73l+wQvvfKdV+Sm+fVbVxrnhpvSEkagfddKL
jEP61IB1oAMqfHvLbjbTV3db4PTf14R6so4ZCFSYfugtoCrvJ0Xf40hdKffQ1RCoP1vRAu8n
19w3ToIukzbTTAf+0V/uv1DzgVbSCm3eEUGjvJC+PGlyWpGTfjsuWGS8YFPthfRoXhvSAqya
la7pZdz/uqc3dZi1bGZn1aMsMNcSErl61/3Ff9nh/l9uDyUvwgduGrQd9tk0A9osbKLGk9/z
lDjaYjnPbtNP4jXL1o1pvi4ULy24+4mOORNFicHRW+JD3KP4cjT3Cmq+vWUw71F+zlfvTE+P
yOR7HnIbwDByzja/L1Ebs+gXtxYkcgdKueMcdfBP23r9k8ufMxuPJ1q359/oKFvTSgtCC4ox
P1RPnEFQeE4rPWV9M+Hf+vp6uC0NhMF70IyNovhevns+IRvBYGztfXEaGH4oeL7MG+bpVVcJ
6x7qeDp9KRMP0X0CpF34643dPQI3dyWK4bQ2pS50Rro8GZlZJ1QjC3K0pFui0uDR4Ojd8NX8
C+uLH+T7adU2cwjSiYS56cqcbbjijGXFbEpQApY3a1WzgzlIr7bunohbyrAOenAPZF9uT0q1
bViPY99RuLnbFncyl9t8KR2Pojrb58xTABW4BkNByg49CR6502G4CmlWnG9YGM+PGIeu9UUe
BVocnOBu4C9La/+JtahOGY1s2yJXLOWROiMzRe9qtS1x66asXjpdXlVxr0+3fkL4CSrr16RE
gdmQ6nPmrE2e9hef4uTn1PzM1jgFYvv902vk5k+FZJKezrV6qA965xJi4JWbqncl4Tqune7h
Q/2tmOSVJ15JNy5krqEKy1woQACXvn8cAAfUC1a0cpBNDScu5I31Y3ISS6gGpjooeSzvmmoL
GMe4KWDQkbj3fptn4P2E6YWLWjI/vkFPGY8P22xCvxH03O3dsW9m91ROvV3XaqLKY8vnJRpR
AB8FTrW1JZfBAriGZuzv9fu/JR1PyCJ9OAuxrslCsdf0iovoxJ2uQ2q7DXEnc8n7w3Ps+KwK
CoJsck5LA0f2wVapyy492bbNDvUvlCXj1pf872ZfoWqt+7JBpG2KbS0BvHT5wRB3CL4sra8E
aHrq8w7a1d+X+YVR73kYlXpPu1wHKmC6f5SLchk2zCoPAGnKlDtO93Q56njz0pQ5ez4tVecz
FqF7OrUHW32b0k9UH9cbE7Vlkw8EU3rmD+Km8CKTCHKDGmsx/+dJkGR7/qIenw/IB/jA1RoK
Soa37vtB60A3qne8nlpRt5DAli3NRZwz5OqgD6J4yyVq/0A3M4KvMklJ6Dq76o4HqcMtYTWx
KSGC+3ffsYNzsy7Y/rLmnfq3qIKlzKz67Cq3tZE2EZCK3uToIJ9yh/91SmxT23CnUu+ijClj
naAAWWFNv3qVT+mm+um88P6MrQqX51VuDRbZJ5rHcH63jINXRYqfDKY8HpRPjKrf57Ah7g6h
d4TU5bdH7RM/d7UxxZl5sryd8ejr5N2e/afIe2voID+Zc7m6cgPxC0Njbg93yoxr0UAzgwqF
uiyRuQZEgnQG+7Tki0/xV0oWu96duSk5OfDmtAqXcXZlmPwcyfba8K8Lw+ObeGtClarEVcOS
cV24jJwkycw84sTi5t1jG3beMxzvtoedLzpxprEpxKIJZlG7fvitumAvUJAXC6kGudVbauRt
X/IC+RUA2F0UQv8pSe93nfF4Ozv0T23vlN0Axk3dVgZjrZAXv6pGxZk53a8iB5GsifYAExDF
HuOkiRkdSChgv5Q/vdvhhBKidVoER+OJKdwxhb0pO16z8wNyVswVE5HSKkP/zXPwutcFBt83
4jLydGVhdytEDcR/tsX9kghps+uReMBuS9zJXO75xZA09Ra7Mac4fEs4ZiLJNiqp9OzWTXf0
1RtLJsEnl0jrHnjC7EZve0r9/uJo7kb+srRwyEtd04xTOwvFGmOjGiFO06mSkTvH40uVd8A3
/5xp7Z/8/Jw5yxNd8mjrzIB22UoKFhaBs2Nqidp2ei14EXJgWpysbqWQ/gdgePgJTBdEQ8t0
nGmUkLl+GmSkMODfH97g4+K15OLVDcuglTpmb113z8w+taGrISNZsiS4lC4dZlwbYt4qbPR7
wd+Dvm/ty+E5W4oQ1o5wYs1Rd/FRXlpfJJx+0QrP2phxRfqcUtJvlU/U3jNoPWC2tB72qsgK
aa/wsxNNYAcesXjt0W5n/1ZWjBohpTXkxONl5ercSEYjsSozIVaX0oF81lI39tDXCm9M6Hj8
+sVh9Uz3AVMQk+RimpGS24wpykQGeRtvPlp4u9scdzKXxThdsKeatjNbvy0ZfS0dpfLqZdNy
1FzgUQ9K3DGZqQikCEACKfThcOdB/nT3JnxHcbsvKml/VTR3EL4sLVwyOxHgiPwpwkHsPU9D
m5FYiWOYaj1hZDoFfvrPeTD/yc/P2aXxqKUi234qDS0ZqqMrGZY5Mtj9Kv6m/VZqHFVOsGzG
UmUgRE/GYMYNpcWOS5jCm6+fzfgtIdmAWEs/le4LNu0jrYBpMs7uxNyYgT61WQg1FXW7D+PV
BhLxYKraE5RVbfPLQQHUofYGU6O7gthSdlf7iAWNyq55NRCiOR+L6VvqyeyBOo5j/2AzlQfb
hfVrqRCVPox7fDzA+cKnycOTZE+oAnKyzg+juhGb0ALY0WoOuvt+uGuey8CqedjQnH1yWGQA
7Mf5GbPB7W06IvmxxLa71+jout6mj/eZ3Z/Q6eYi/mF8sX/8A1R/iTz2Sr+1M9I2nAkJ+bCe
NgZXHUocH/Qe7AunLLZ7jG2RrvVuqB8blIOt9b3CG5gtUE/Pnd5tjTuZyy/D1HyIj9OP40cS
HwKc8+Jmmu95OFr+/ktXxOwE18QfEn9jWBsHL14IMtiKZ3lNDn8IMBkvcgfgy9ICOKS73Trh
mY6MBUZ2iWYHtEwYdnDnx/8/Hu/7fiAypyn49RwM++vKwLT4ispU9/YY+HiT9ikdP4Qb0+Ck
7tHgPKayAEhjRDb8xKJHQt6ZrJ9FNs8l2PatvucZATH547oqHnphqcFaMPdVSPCNzvxqMw3Z
TsgIzkzZKEZ0jjYclHKf+NUh03EoRm7/xfc8UzrFNSVWwxNrFIh6watOvzwflRKQ/THlpDRz
M0lhB/E+2htUyZqBamsb/WUVz94zmuMupv4WQ4wswSWW8trsitT345aqDUDG8M/v2vmVL4kN
0xvz3LCyE6XwkqV+yuZsmjGYbLzP48WuObDHAfYkNBBmAr+YLhYhCGeGbgQdqzqz3ApVmOZU
hJ/Y0BWWuHNT+7xNyMWg74oaPEJYhXh9o0KhWv2IR2HRu+xwKXJ5frevMJSIB1IbRiUEJb3u
4aBrlaLAqlReU3Ew0bZrljURaVfqP5Wyw+bF1e3v+QwYXKL9F6rhkErmZqSNeKYnJfV+iSy0
sHZ9k3MSPxj/nkfuUyNJn8V8xcN7si7ymA8lWct6vmWkpokaLJlm22pu04xfR+kABw9LFTBq
33hWDsrxHAGiFpSZvPOjgZyazung+frs1tHmoMdRIVPmIVBs/3qgmUlxIvj3MCuMlmm6wBK1
f1QxaNEtAWbcElO47jqj1qIn39vF4mWWpZLUS1KDfJ6rT5AhzVYI78QF/b4GijmoJTTPUaYO
CgowE2pVNhBUMd9P8htuA+8h5lHdiK8jeg3IfvRCUjohUIlPyqw+jjkMGSG1J+VpyzvCrBFT
8RhpZ7k3B7tmnYoH30yI32L2rpvwthAywelrwSt+hdg5p7eHvhlzMMi/PAYcy2eoTy06zne/
bmWu+p1dWtGdo2fywXfPsL01Whg9Obsfyp6twEI2rXFiLryy4eS5NrxIQYrjmQSngQMxu9W5
nELcHrXwkyfkbnCIzWzBchP6zhlPuocoATf6XQnA2MNPl1IZPZ597uIK1NvIKwcMdLd0w/tz
nplYconhS1Lbt+x8Nj5zxegP4eXpVoNWj1z7k/RGJP84HawhT1ybQR+RHWunXPuYdvAv/fu8
7wkPT4Deheo/FsURdrqYyjsVTsd9OmAKI/MgxbOlBb1x62LuuPK6WaA4+MIYRIARLsXrUikt
k7GDtH2zHF+4A2YxTJxH++GQdgMnGJkI6j8pFnxHEJr0Blhi+Iu4MVVGpTHFDakr1zLn+GNG
RU9VZja0+l8f2LIYUCnxEDNM9TDA59ghFOikJBiz/4+Q9r3S8iWya6bDQfEZcQgSjVF4ZM+y
V5V60Ph4zK/qFbBpqlq/pjr1nWo2qVJjGlc7bgmsZfqhZ1OSCX7y8QsGpsJGWJ756F0flVSq
sjEIAnaNW7hwmLNsp7/khMy5V+TSt+BvRmezhQNo40y/7uTWhXmINwVIsdh96S4rfyZyud89
pbj2KgnsPNsX0BDSRL1QZAzfEcbkL949pGkxOfB6MuWmU8fypS61+/DtOOoFWATJ59Dan436
pf5fOLzN+Oep9d5Unbx6tf5UvRvGAKXogQAy0DVgejhNRdIdn0AGqG6jeM7v/SQXj9+zI9oV
HzclwVqhHvlfr5n3oxxliQly5UZRtsJpw6IiwYR9IfeeLN24Zx2bLfE6L+Q9z5Ux+4a8baGQ
WdHztgsGvqo0Br1vtFnSZHtr8Tjpe4YYa320C0lhCzf5qxW/JM3NnqRZE0CV5LQodcUBhBsa
r8ouKWQKSACZEf9LB5TjWT+1lKLdeq1/Na61qi+1m03V9eZFOLvMXT7n0Jy+fy3yNqc7bzHG
uLvITfPXUbTuePVcorAdHjZ+X2tdeZhqXFunBkLuddbi6EpF0oIWb30LRjVIZ/uPO8WFUUKX
jHymRQKYZtc5D1KeTIfix0wzg5Q6/LKbc6ZRiPDDriUJWrXdfdttS0aIR7/d3PU5nsAJExSK
018xR6u9BxIUXK15Hxd2m7e/oTpJklJ1107/opua5TdPbKvp7Cxu4YhHgWj4cw/620GWwcr5
FHavanvloYld5rgVuQzF61ip5+3o9KtMEA3M20kSdxwYGexR8Vz7E7aZTAar0BsoFq2KOnj+
M0rduQX6r9Oru1hWUJ/yijyObbU/epO5bSTr0rWoXALwtxzS+Tagsn3SzGu8VWdHdlqzxBxc
PChCsgO6gdwNufwpiPcsu1NyQpGl8xEtd3k2brshYKVt73mOrTIdwPVtteQlp3rLRjyoP5D1
TkVWi2puDHaLQzqfPtEgtFT6jLhA7wkJYRU59YwwIrAWxaZCHbCEwIQRhBtK+4EA8OIp/XD6
/j9emu2Zrf5ynsv0OtDL2CCFselNJes3DSURN8qH7RB6TXMH46bGH/XS1knkArs8eezVPuvk
CCKykwYZAHr/sQxM5+/6vNhlcs+77NlZiwB+Uw45J7ISlUW6+tOreGTum1JIghM9q5TnfmQC
Qm2r5DbbmTASfj5C79ZYL4aSQwrWOP4iJSgrWGcI9DmBR+7CnzwHwokyeHE9ZFIMClxvKDLb
SA2D06fILoTeAzGXdznxnyJK2LRagFp0oRxKmjOOd7z4Hq7bwB5vih5ksq58TRZbkpHL8tyk
SmwfKsMf6VjVGnPs4Axlvfgk7z8n3PlhgGNeM5eIMKb99YtPCy3jEcuqAxEa5eAZv5XzTpAd
0Ax6gDd+9ft+keec/NrWSdVg4tOpE/DbavDO8VugxpTgtwGbL9KHdgN19zbfNlGdNwreRoqr
z7aTnzh29IUZAzFKSxpNkqkKGZwK5i1cVX83RSxcSrTGDHAszrtalkP7O0uK+jBxyB07qZuf
1daUy3AQkDgt1dpK6kw1qC+VPDq6lMsQ9dZwd+8Khzg4Fv5nckJLaLUZGjv65dQfKdOpVkgt
st7YuvHHznfS/Xl4ynFERLttwxvPU9MLq5Fn3Ja2HiGe7b6bfyl/9rSTm1knTr29dLH1HRaI
b4PqUG4BQHybZg/tq/stgH2VXmav2DhSsZyJ3GdGC2i9kLEm7VvEIOpQNqsipvZnR+8Ctu/K
xlsPK7Fg+Q2RzBT42SQb+LAlBdzely94YdIblzcQEz2V9ri3YUh9a+CPDoFgrWA4L4ZshaoX
ThjR2UKQF69V7jLGrcj1g27lHNpkxiVyEpFtr0mDlgrNH3/P8+z85zxbuYX2L9PrZjwS+8PN
FuHrJO/OHJ5ScwreDmKSHJIPsqdSUAYMVd8jVkCKFsm+SynKpn68H8tBPjv0STnxPJ91xv3h
80hWrNi826axvzIK714iPZ9fhe08i6YhfJcUO8w3U9PANUdx+Yp3Up8s52PdMwECmGLv81sk
wf529/ueNnrB7kMaH9FEC8R0C/rZ1/fZyvYJNYRZJwMXQdbDaU59DQRwTxOOwRe4Gt+vHiAJ
Ui22oFeiihtw7oicRuYyxCxIOWyzp1RySMP4M+4SlwfKe2tsa00NX8/IVJVNrmj6cDJNSlVm
Q1r6LjhHNc8f4Y3+jJH/3S9Rs8HIgkIGEpcUvbqBBpKqiRGjtAS858UMtlOlmuDjeiHbgVM3
O8NCPX+eeugYmVvduHP+64/u6F86+LkHBnsE7XzXPDQIfAdV5d1TxO/dK75NA2OFGDh+hMtg
KbT6WNV08JOBd6ESw90pDVka/nKQZoysNt4A/hB8B0rSN9WtfaFetBvdV+tdCwGm6XVtpzwr
MxfLi4mpGGN4zvPnzgNR+37zJpi0ltq/GyuLhdv5q1wSA8i5qjd6M6HP8+fsoz1dd9vhUub2
OReh+dDJJKtdSnCqTMXAPpH6XNqpUVltugfPZs8cuHt+ALWGUaTqjFQ5FrBk93zOvohLvP8y
NdUVrOxjE9FvNnFi7sxLGw9TU6QMnS7Q20delmwfC5jtWmVccKcZTViJrp6Cy21iAeIaaA/p
2rfnPwnwZwWvgRH2ClV1zNCcV34gBDR5t1qsMlPvGfcvjOWNh2amQXRbqOrbU/uf+nk96esI
NRnmFcZoH8TddjupZgQblAoTofdRmkquDNzcjTQG9oyU0EZoOwC/jX0AsYnymK4K7IlfF8Ng
WGDv4kZUxFtjKYXNKDm35ZXXx0qzjM1Sn8wxxfm39IO2uhjCGI/3PPLfSNzfbZFLmdtl3h46
pJxUFaUtPis/+WbGssoQQnmapCEJNFA/nQOKLzQrmosgYanQ2JN9FrLGYJxwLwr3iv8zMji4
hP2vU3N1sWo1mec7u6H7LeVBJ6GCV6396X3jZgqMdrpu45vpzr6hoPc8tC0pRZNZtJhLd6Jl
kPuOOpBM0PNJkD+rXOfDCPsPrJl2+wXmBhMYav2ldjmy9akxKf1rquHgBqJ51C8kH0H88wBx
gAbRVdxJLC6vK+XpyJANSqZRqA8PEpBcOz0RvQvnHgf7PCuoBk4n+1rpE7PRhTH3SjEI4uw2
ZNbSsodxvLt/7sheRyfrV7Vl9xwzUPREoJ2pTCcqgynlKjm0ywy3IpcRLp6DerN/Q1NjW9vU
jc36/FnJOQ/0DB1ZIIA3Q9EW5y6Kt7e+eKNwjDZs39zTd2w2dbbb4kAmsuwCfxu3QL4gPYHx
roYLiEsBvfCoKAXmrPOq0dt8PkW9+9ERZGFPUA1UA7RRkLFEYmuUt4ROJ+ntW2Tvj/4k94Dq
3ijNFT2ngc3M/bzc8nN/GAFKydCMoicWBM289VdoNffQNk4iqLanvyJ4q98/w5bN8l24++oj
JHvJrK1j650PZTOw56SsRh1iZ2iMOvhgVHGCzlS05eWPdLl8w/WMspyFxvsNqoqbqbzIIEQ5
/twhDF8zK3Bhp/jJowf3P/JzyDF53AQ9eOFs7pJh67uisIqlKYKeH/8klzi+JDWBpO7jVoni
52LFw14tT8wgUN4xs5xEizMLOw9YVwbIf1tFBMyDAlreoMtnEDuF6SqzLbao9qgVvZviBZ/k
5vFUaEbSOXXnMH2ngczMDasDAUS5UdkOoMQzk5xV17puGAEXiVky6jC946w4iJRCj412DHWo
mQkusQsWxlPkQjd4OBr8qx2V91rnn9aC+Bo6nszDvrHvekYW1Df1yw5PMvG2WZyOzwCIuisX
JCbL2ct33wz9M0BclKLZzlzE96xccpKdmUlZLYKgamzUaOp9oXqaPU3QefnzR9fAVcrOT3Mu
nVwXNlAvLYbCicifEI7OkbV7KeRLpYqwHTjHK9iixE/JvhN/zIQZuD5D9uCTk3mFzB/u+PrI
/uiPbHH3htsfaAEJH9UqzyXR2L7umPGmjsCjH1LZHAhQ7xXqQkyIptesYInfD68G+khswp3M
ex8KaV3GrHbOiytyB+OL0pJOLbE3UHNedBKlPKQXv/RzmoJohkeej3GvsnSiujzIlbSNWx4k
FQ0g8/WE/aa3fvSK+yT3tJWs8KnOADFAwAA+KDOvSj55CaIigZIb2O/vniN4USm9eHLCrdqW
3iN2e7PMXvb446V5WpL+Th6MJjGvH5rnnJHLCM1cvnthze4eenEU0VJzYnic3vayb+t73BV8
5Lay8CA+qRCUUVKZ8g3QxQJgtc8ZE/nxnxACHQxaX7q4zUXUVT33AOIpfSb2j/0KV8xAWWpQ
lYWfDspPQx+NzdrOz4WTzA0sysO9bPRkKIVGtZusQuRievHd8OhdJvd0hbd59GrZPNw5O3/+
XKnHOZNeRJehjv9EYuewXVbUeMjpuEggN6y+rHWcbsgUgMBFqJ2BR8z0CjHYDM72DkG6gH3l
4m6Du2z/qchlBJPHQMO2WZWa+tIzeVDCTvzXeNbZHM0osSvl5HN+hW/GvG9axS9c7F5LBCjU
A40x73lOiX/O5uxPkf4b/Kf0keJ5LGj+zGL71cXqSgSvs21Dsehz6dz3PBNyDF7W6kRH/pUx
dGyIMjhmNIC0TqbccnagDG4NqV/+NPB77GCK8EgNZAUrf7H1Zum1f7qaHzGpYVGWt5xZt9UM
JFUN9MIrvjHeWttyn6NKbr/Zb7tq/Q7m7H+VqHa9CGQRsJ2auY72/lYU5gwEF8NUwPfZTwQt
dts85jJzg3hBnfJNNbi9NmOJePEiwtstlz7V1NZQ6r+ViG+vPCY1dafi/O0lqQTxNqyvRjlZ
cJ9xXg3DEi2/HSyfEuQzzb6jtNsitzK3088w2PaYZNaW5nAkZWjdB1+0dRHbldil0N2/VRv2
gmmf0leniZTL4Jg6hL4LVkTfA1o5c7BA99xg9hVSNLdYvhy9vcLwzjGIP8IO5/Q6E9X26hWH
sXMNE3h0HVnaz9if7+dxz+T42WqpUuOghAqLB2F0YiKMuPko+PSnebi3auBPWsAAtsSe0mQs
sNfHwuIC+ijqJRO0p46myjqoAuxP9YhptiuqEvl4QCzt7eAP+GDbUV4iRArhOOKa8Qekf03D
owVT8J5H5dq3Hz35xdS6lALs3obqE55Yx2cMZOFMqLAgpJqQDSWNEVVTj9Lp4bMN+L6vYumi
Q20rU0BXshj387SZ3lVBSVjDYu/+h5/m3z+0uf19l6R7LLnhHrbmZPU3e4Q79cVvCA85t49c
1iEL4cyg57UIUpQGU8qFWaRjsd5ePZErp6M/B82/9zV7+TfqZlQnVkK9xeQXNCOpVF+UjltW
OlAXfwg+nmVMylsefJUjJTNeqSXzfT1xbBtyQsQNWcYz9+jT3DoQWEmc5jAi+/tSXqvdrTv9
T1erniuaIKU+XUbnu4WwpTO6NHL51TYi4bQTxOCaefozJ7uvA45c3Do22J+HkFacEX+efRiz
5pwdrqVGlRwboy3cNYzeZXLPyRwfDfMRH3Zsv7QWENeranuMaS+W/KUU1hn8nmdBbi4GD9f1
surfQlrTJpyjvunP+okmQynWt65djjg+a7V5mj60yxq3IrdZczyq4CJUigW6yZDfM5j5ZEFC
60IYnJqS5sIZ+llHAH/d2yc4rkopdrxuoOICSseVlAjSec/T0l59SJpbJF+Q3lfCtBum5Jx2
SaC2gKgz9aI0f9R6w4qqXAJeh8rvn/cka+bIuLhag1Q5yrEox9FaeIcBxm2LZ+Lyp/ko3PVn
vKqArfsmlWEP59Xbhg3bULJeM9a52MJuna0HFmpYkWn2tiiUfHoe9lu/Y9edxoocTH8+3ibV
BwiY+K/QzOwukrfnLFN8xDG7IR2MmA2ummoZaT/G0jfmwE3oTTRnrVCt22Ocgp0Dpwd1c4BE
1rdjuFiE3QzKo/HdgnvOhHYNvzNkDhMx460fFt2zuNsalzLXM1DtOGbi2KXwB97G8ckrsVlP
HFIeqxRYAl2f1dCPc+2ain3zebGpI1NAi588pLWz2kFMVCOasb+QSxhfktrhjcBv3+Cgk6nx
jHsoGNQiCJkEUp5EFFCXilns6bkj+/vzsiymCWBEgmMG67Tk5U/z7fDsn7XzBWxdZdu0tnsr
JWyp9z6ANkzbhJ0zx+i4NjUu+epN+S/sC4f7M7OywL+XiLilOzsXJSnuoBnh28+XF25RWUrA
LOn9CM6VYGgr1cVnJSXnSR+ObOMCm0ZA3qxhShDLm2G9wNnQLWJEvygLuqfSu2y5xiHPS0EG
TNYhBRM9+GnCYG8U6goy+iN73L3h9tcWm2MSsNmXLhNuUuqYu9Zf9nQsKszbvLYEt+z2mxvl
avH3WWGERGto7FKvWNCDBwKzdSSi6nsecZ6Hnxbt5w70v1hrj4Oiji06IlB4gKNmdM/ERcjp
WgYSWjdJTerfiv64Ly0XSP/yx/X0bJEFxcVqgpWjSfOFWIt0UgM2Hwguq0HstpIZLAOV+bsO
l1zf+gVRFMMV+jMrRu7nqDi7VhKmU35inrDIoyznXek9vRsHLkWLKBpCaq8AurKV25R3PyiE
FXnhncOXROdMXfgIRLvCFB+RI3hYonpBGSwDlXA2wS1uTVr7xcpuI9zKXIaU9+WHjlLdaKFX
RiYUzDmmhrS2RuaqZ8eo0/weMbLgmk1F6H0G4nw4Tum2fRN2utjF0UzKce1y5gtuYXw5ensc
tAJNsYEXULjf8zWSS3VboJV6O0PPbn6iB3/57IIOFvLaheXn5n5rhjLVmB/oVGXq0oVCnbEV
5Vs2kkcjpA7HR1vy7ePvQsak3AGCGV1qmPMdAjNmxvpGPdFhL3bB2WO/81X3zpyOQYCE93WE
klV3CE5zC5x7riHpelHVJJ0Auvwsepc61yK3W9FAI/UgObm03O96UfElmAoRiipVgOHsBCYr
s24K6HWkXsiGeeLDVHTQSrdmRJymWm4Pd3Ois3y4xvHFKALPJZuC/MhA/j74L5FuJt5fn+uS
BviZ7O1ClfXGgj898RFq8yfdi4FPZW+NWMOdmqrfxywbiZdE1JLVNsRkcUphwh6RB5TnDCTy
e6L/0cf7vz7AU7xA76rKTaWf50GjmX4KPW/L77eaMP118hDnrUrG2snGd49oWni15ITlkB+k
uw9AXfTraYGncneeSt4hu2e+5zkE75F781/GPuVfrldWyvbn3VRnBxQYmsLAU6gAyPz9GmCZ
mFALYG2e/gWWKtbpFj7rdf8kllCXpGTxKm5t69T1BdZ7HmXWHu2bnwLoy9BdJAdlqcPsMeEP
pxHonrgDkZquo+E/Tqb8KjLPxgB9pikqulaZ+aAmHAUojxH6RJ/+6jCDL3a23BJvt4kPUbVB
eWAigKKR0zjC6QolX3GkpMTkrICon0rgVitsdSMV3qVr6BCFIwyIHN0Ngs/Qv5noW4EG2i3T
LpQYCDn0Eas8jdtnlqdWFQTmafAM9hWxHCHWhIm3ctZrf04BVvR6b7eve0n4KoOSmaQatmpV
fSh3t0GuZW6jbMcNg3QuhVidSDOCe1uXDDS8zcjYz7Na+wYtngs7MYAJ06fTvDbxblYBDf0H
7lzmevgvRXHPiwX69Rxxx3kdR6Dl8Mt3/hf+u+Ww9/Uk+Yn8dt765nxKDMrRfT1wUxB9y3oz
+Kbg0Ce691cTjZevobXd/7aPUhypvtN44C0LVVzQH5dLVeutJdkpSxk6Z+xXWf21j8Xmu6QJ
K7aTFGIWUzDuf7S3tVpM1y0s3DYOe5RzeTcmgBAmpznpsR+UqEpiSyPYACfMdIWjyxgWLX+/
MG6HLVLI3oMj8wdNgIrPJZIqmBmruhaGSWhL4gwnqLCJGKQz23Xl7OndFrmVuVzMf8iO1yIY
vgII3JymHc6hwYz01ZAUDe/D2MolqfGgT/+h4Bbfv05vT5d2hwvjHdFlpAudAo0JE3Xy6C5u
L7a7KIrSbbksrZEfiTRx0bhkJQgOfdknlqwfcSirp+s9z/39Q5+KuYTwJy10AYbuYrohAcLM
aXQQCtQOWfA/Z1z6VD+YychuwV6kbXbaYyJeuN7T13nqrZFQfX3Qf7DedTNK8Ad08xgzM3XU
pRHortHQu//FblB7L1b1z3t62h9a3HSB+MnImNM11LSAnhKtJyrTvWi6YxOmCzFnp5oJFwIi
IWoRLvKdZmKspdamBoz2mhUhKdFlzhYfID612yLXMpeExkDqQ7MhXkzppzltd1lX9PFkc+vl
UC0zE7IQ0Pn7mSvXw30xippOOUdnAnZ+qqQ8MGclsGBYJzoxxY5Sv99h1byO6I841p05MuHV
2xP6Bwjgc3U/IZFPT3Bn31Ed+kQPzxX/CVcxYMsVZ3WM+uDRclp83igLOL4vA1MXGiKpIwX4
B6mDU1uROpXsK3cC9PuCfDig2qQVkB5iZjNR/AdMFLG2PrGU5e++PzV6F6S90htD8+Ge5O1X
5EyDN9lJ54w68Tf+CF6uOwkttkFF9L7GMXhnVzv6rbQcfrc/OTxhk6A04TgxAwnahpw82Sta
DOZoMmNcLu+yyLXI5TaS5zBnySSB5W26HaYijeN7m30Ta7aga9LZjTXgbApf/sQaXq7R/SsV
j7nNGBWZxDbKCZU5uqzYHjXWk9sZ1JJsX4ruYMSJ2WmEJNUd83i5PDKVcaJUt9yO4ocbcWLs
r/5UyH/1WBPN8dXQNdGlDyu24M3hUloaFjSlhqjzUEeGGsm/v6eRtLCPrGnkZRxBbkxOxPbm
v8T5z8JLsEGR8CqlDUFK14gZkLOuvRvVV25dxwNGYZI+ODd1RQPgkVmGcoPmyY15lMDGa8Fs
YkB71aHYcYrn2FybPed2+YprwoXypMf5w2P6Rq5LnT/3oSbXTX/U+qw6CK73Czy49B9nlLyS
4SGpqfFL6aVr4ec3o8D2kjpTyMhHlhcQeVWOGJdq4+DoyOjdrv1HyJ01mNAAJz8NyhxNBy2/
k+KOzFfGOEFZBb+5d1/VErAAi11w1i43JRTXbqoUGG+37LW4/Il+/9X+81cTfH+WnFZGRFb5
1i1I4hOvI6EBVMFxFMvQWR86uNkscuWb6gQvTztkI/uQavYNX4OT4k6CkIw45tJ66aXAdhJk
A03nC9sNam+N9tyY3aio7ubmDx0e8W862c66vaU6pFqHUlD2cY23JW/PizrTqsNULcuMzQyq
HBMcda7FMb86/t1uI9zKXBbi8uzdp1k4DV2dDwmegPQwDZ+mPLndtxyJUh3wMNuBYO5oictA
8u164bwEGO5wztUbdU2oiBCiO4K0/Zv/TW6xfDF6qi5FMNKSzB83NKOA5jyRbFjOnbGdiS5D
o/T3PAQ++4CrHa6lr3K/hZ3Jx1v13xM97L42Uq9x7x8tMp98opd/dTJ78MjMY+KFYD6tsEkR
5hTRSb/h3eoAbLAw7ztPeglykQC7G8iS7K3rDROHzc2d8/WWuvLOV7VZ1Uziw4EHiq4sOf7d
RxnhfEPnBl/Iz4xG/dhaWvmdHBlg7BKUH3jPIwFutMpXr54ZcZrqgD2y1P9EN/6hzvVs+2qj
abrz5ooXeowKdutUhyFToR0Zb5rwrOLL32LTwmf/D3dvHtDktfSPg1qpG0oRUBDwgoKIgOzK
qi2LrQRKQwiyKmCARIJsYV+s17IJkaICCRALGiBhEVlCCAGUTZaAGMKSEDbZIYR9B7+P7X3v
S/v+3l7ovb/fr/3+xYnOmWfOPOc558zM58yU4S7YSrWrKPo3dYuJXCWjsjch3vdc3uDCSrWv
/SHJ/syd9gX4FrSk9ykGKZlgKrSlA7srBRYU+ofpQE3gkFQhz/PFjUvjjXk99MtiXNXXyegf
8SmHP+dKTDEk+s/s2+W4/tVsO7jsweWLCTHy1dWEkE0tNfoHF9zER7RrrQqJRuqlSzoWYJ6X
kdufqcx/EclE8R3wK1nPr3Qnk3wVrB115seCEYnBOOMPvAdCZDRS2Q0taSyGK+4hS8uSSLSL
Y6/TLdWtCrYsIarTe/yrtrPbcXun3g+ev2XkPo3xlkzSjS/Fu9SO3mFezEaD3xRgE2w3H0Zf
PXMqavI4IiVtJkEjuvwcqUT57vqmmIAGTHf9Jvf/PuetQECnpDXZCXk3AkkXHJz39k1hUpFL
7oPmkm/O8wX7xLeN0S8rvlN1A0DGzBZissXa/ElBIC80TLcfabXjN/ML4b8IDfC1ZsG66BdV
fC8QBmMuPUVUAhhKQzW6qir3ivwmnX6Qe4w8PdBhSdaLqozPcUEECDEkz4a2yBhZQPU3mjz1
3l74Yrs8R1ATJynwbtvEWSg0PZmQkyuaCpR+3yz0YNbgApWa1wVOv+OPXP/G27+hRndxwOx+
BoeoBb0/4dfciB8yA4p/hqzuq9nOb+ftHRunBlzbFFGFyWDx9kE9bWkR2wLVBYVOoOjE3NUS
tqIKoXHI6YdZu4Y8oiqRmZzMZUpDmjgSw6o8zKqdy/IXoRRQ7hQzx08PDwjHCwWjNPgLE5Qn
DVlJRfW9mb37+xdeV1Ez59Srr/txVoTYGZBKVieeClYkuLDxbo/cd3sE+lez0GL+VqmiO9LK
Pz/fqjHlzkM7bE6gxFTAWKXl2UbAjJDkJ1wVtBMt2Ux1wOp+ZUF1ebMSUTg/rwDtXz1HtttA
SIR9B4vp1G3px77crnzXTitqd5CHV4yHYaH4B+/pXG0QRXyjYyx9CRqWV5eu+8633kAhw0jy
8KXkSunKCOJkV6DBanDqy9mRqTB+4Dbx7m7T/deTd25PAECWQJF0DZcDy/puWy/bF235tzIX
a3MCP/J03+vZ/Ntimbo9cNVAFMHV0qgk3IJIaqvb4j/yeARumJUdaf+vx/1f85f3sDhi0WZ5
Nb6beaF15ARWpg6k3Eez65lqhK8LZ+1L8rr6wjxjLuLNhW/kZhxH6FWNnAUP65hCvc0qP/9d
KuFfTMf9Wb5fd068I0v1LdxoxIosamPscUjHIJC5/U9oTbll9zYvWSDtBN7n8jsFduclSpmi
U+vD2pq2lxfYmOAEEURj3rCy/gbWW3lqj1X4Nsl4RaiemqameqwBjYZiiKqTvjaE4fGL2axL
AbPG6kB9/uLD71Xdulgpya7MWkwQtMwXqPhG0aNa2C/I9gx+d+TdNnY7b+58RqKRxSuPoU32
La1JK5PaoxLNZu/y92q4cO8edTG8gEEMJ/jdWl6ZtOGeH6rPFXJbUZb0PP3o250L8hehPBbQ
oWmR8e3IdMtZdb9UVTe3rmLjXFU/Ka5H4NQe+8tO77ljwSUzGUaNmcUb4vE/fWCjp8eqCkEO
sDPiuwXB7ilPMaVnNU78jVzEnIaALts6NaYT0nUKRNQxlKUlndNWd36rM+NKa2roxQAPpk1g
rwmLQvCQFyGky5IeFroclX8TtTgoT4aHJIWH+oDfyb0ZrvebPj87ElOGn6M6YkbSelUYKToO
+x1DrKKn2WjYmS9+tXt/7jAJIb9S53cqecqIWWBEZUytXxYwABbh+MT4D9rrajdeHVAYQiAG
3fm/9Td+cYuFj/FbyhPOVhb4yCOXbJxOxKEoi2Zl/H8IOcKz8zn6XvGltZAoUN+++GDWTKZB
DxMWojpfCI2t53KdgfDMRF7E2uLJUzqDcV3R64zMSevQYPqkkWHMY4P1ih9w/l84/1ahf/nf
e3gDX4z20oDKs0/zbGeyqoFKiMxPlRDtFcCSdnZgoBJiSQnWKLbEJ1YqOlj07l3l2XRd13S2
2haPV/guBy/fV2OGMcwL8rZdcRY+9tvOArqdYg7p0wVvFPI9pIJ17ri76C1mERuUUeXWCgzl
jzyNFAF9o6sl4gpqB4DFtQuq6ASKWXvBButNmaAw5QpfbqpBplnpQGR06kjBdt77eH21O+f8
zHTEtmqxjGEb+gTdp9zGp/6B2soJDR1tnxrAOaBB4CZ0PjIzor9T1sB3tJWUfHa8LTZjfGUt
BOOGPqvBscED7pvGm6eytjPecXunsbb9mYugukzp+DQpW0xQiy5NgqP/Zej5QfAS4REc/ZVt
47n2laZ7qrOdOa4i6XoPhFwMNud45at2LMZfhVB+uNUCWkmeH+RPjHEISl5PFDFOd2pililY
1a0LXrlwUgDI3dfON7bL4RxcnhUciUek9XTqnfzs77/tvE/a92knB97TNV5mh52H1oBS70Wh
0IcaDIFyqvmr1K8xSjbL2nusAkzeyTM38mdwX1FjLnXOLsHQl4UBz6VD/hdsP6lQdATE7jXr
V6zzUZr3a3szfKAG0CxHpOJF/9CwQ2/eEKFc/V46THfi6q3/8Rn8qvv/+mPHhrPWXlyucGxY
QuiF/k7jB8Iliz29fcYSZUo16wmIUmlKuiVlLFSLyy7sDctfeuyyBNTtmb/QtvX+wKP/9dF/
1f/gdVDw6htCZyNh6hN4zsmNu4Qav7nl9Nyg15FLOhLvdp+MZg91w2D1ufUoSb31h6u/vuoK
6IjXIfSn1U7SRx7dcsO6Nimv/F7GS7U7QT6toctTg04fQAKToW6G5lPL+z7yjHdpqFH1RUxq
0+UKo2AxwuNoNbChsokxlWftyjZt36WwvAbv0JLzPY58Oawx66OgKv9dpR2YKUeCMaDnk5fl
Hl09ej2XlEBeZXclCzrVd78/175oUkZImzcxvx+KkV8K9m2yX5Ht38ZyF82dhtX4s0aavsiZ
tix9HWNIzitbkqGqgQGMXVYVVVlgumaP7JqKi3kU7WkuGmKXqXkbLiy3pnrSyk+PQd7HCt+F
OH8N0nw0z7nMSLZBSckLZHZeypZsC0nIYHWw1/eG3eYE783+3Y4CWhmJU4uxXRohz7y9cPq3
veXZBeUSCr6i9OIjKuzL/syPPCKjEI5g7/naVGsvRbOCwXQATvLrFcdHSc+GJHnby68210km
r92ZUx4rpYfTcqvO3MiJ3Hd34VtmslbERbHOAP/jLYoxRYTXBGC5621sKoAICi4kdWaw9zX/
Voqd/d4pYpMX7SlinHF3Zt17TERuJru96E6PVvbi4HD0GJCucH+InDoRA9WmKB2MxPFZvWHM
ENcETohwQyjHDnB2JsdfiCrQW0WupqYy0XYJTyvLM9n8HKguGS60OZ4YJRqhU36x2O8DxRnu
t1FBFYXZAVU2T7+8stvB/e4BjY+vwk9Rsblb+74/rCfGf034SWK2fZ5LEdgQq25LcOnBX91H
vYAaMe0f9XZ0ti4QUV5AaOFfJPQtHgffC2ULhT2gIPr2rW8Xae+1tSrkR563fbJk0TNgVe18
L7cyk6VFqShyci9Qs/UaGnZT/Pq7jzyutjVdwd/1AVavUS5xfM1QgDXk8gWtqRi1FCJm3FF1
pms70523d7qiHRV7Ok5BEiH1gQi8W9LaFwfXfUaofu7zbdXXbxQM5t9on59BgvVe+PYPdSct
T0wd+ix85zL8NSgv9qpOFrmHHvXIpXlV7kmVdocHLEImDXNsnix/5DlzLPu98dVM6Kjxlfbz
GW9SjxoxvMdxqZiCUclKarzy9Pd+V3Y5SgAlLhX8XsGbhRmtPv0y/De9teTTYttiii7rD/YS
E73OpW91Nr8fhIVBk81+ckWjiAv1ZZ93jr0oeeVNjurVJtYaAvmWWskxEPDop2CvTtuWYUxV
8rvtPI34bHVZ8bHF/uACBZCqk3m7OsgeuKQW4JYvyo6x3MAZqeStV01XxIt92cIc6jTpyF2e
IcEAXN+ydmuYgoj00YbJgIsfpu77bue58/bOTVcgl57GLFY+WzjmXpSA8TP/etNkFo3Jti7v
IuiVAPlCr+z8oX8NSvGvWvjtTthmzf6w6M0838Vk41Dl8kXG3VkCNm3eotiNDuShYuOA+i7g
6LMmeLnr+CbhueDN3Q7td+0CXrydraalXu9Qte17pZ5oRM9ax5MXN6I2IT4OD8no3BoAgudj
/FVuQYKTxywigJ2uezQ1+bnb0/Oc4egp8wSvKb8lFYWgqsdXtgv15ah1SFvYdyPGcI61l2M5
SNDVijr4YctMWlpeChm0xOlavicTjObY2mEbZQ+o3bmudx5LgR4C58WxKXbNGW1QGadODJeh
uuAs3r+d7c7bOzVHeYTmBjUfdodcW0yZqmgP5Hv4BG63wc5l5BiuuUzCd397aecS/v9EyZsn
brjY93b0rI5Fu3azP1uxji/hI8+c15TTRx7RI0fHItLNw6JTrvd4G9ff5GyYnAPSGKyq2tav
6QRVJc7sVubfPcp93g1cKp26NYOOEBMlVGowSBKmuQaBC4NOIEJmHy2zb79vGwnhPGaLh03e
UBYnSXBaWwuUxTNrzV0kxYrWPvJIor379i9tF2lPZeq14pTU1VbNY55FhGkYA6Fp1nZ3iq47
omhdXQAnAjXr59NHEzqT961yOGKCSFdRZG9V+rna9zNTA1Z46SIwki1g+DMM4cp2tjtv73S3
5ZEfb7ensQtbjb/Iv9kaTXWxqGolWQQ+6XwQGyjbRyy9IIgsQ9rghwV7MYPn0Y5Xh3Yuwl+D
Ul2aUOJ7IgXtUR6YWTQy7LoEWEiiT3Vbi5FXc8QPz8KQnhkaRG+mHKsjm0j6MWjjW0zGFJhb
dXa3sV0eIe6gLE2qU5ecF6xy6PPfKGfP6cDeadaNlO8G8LV4lzo30f2wXAvUHKr5bYz5xv6r
1JBLS7mbuAbooaJmnEIPVVMaksxhUS8H+L1y/cgjtag8vde5ahtLXvuWkwyzU4GR46IV8YYn
/bHYaAaCig+i20vWar3KA2wTN8LVWxe39dhFcxdb6L6yXNdOnwo/vzz3li3+/AfPYaw1K/rU
DVwh7Jmpy1H1QM39VSytRSF/iwlrPWFnyGRt03Fo39T9v+1CnL8EqahsB9iG/MIr4d49AzN3
F//xFcjSKtNzLn81hHXssGy6Btowjt9T0CE6VFvT+0Y1hupfGGPoKTk62rcvfrcD/H1HyVVj
qB3LaGhUybJtnNuHcNWyT4D6z/nltQ8DpfMqSw6k9uu1UwouSVazE+J1ua5iNt/QFVuR7MnC
KCQbPE1TPd0Svk0gx1M3e9Vm5v9O6QyDmDDEEMgJrcr7EgELeupN1Iyx1vDPr4+rFilOh/qU
9BINtm4XL1DBVlST+rCDyXVEYZxTcYCFWemBD9sY7qa54zXub5I5HZ+dCO52u3GczvQuscSF
5mcoP0n24NiEXxeR6/Z18SK93iAmygz7ToH4qgkuTepGnyUB0fMoPsRu5Pkr0H4+PXk7qw2R
SEM/pzmIJ5RnvY1cHOzlB6kud/HJt7nsn9aU1044z8nGqyx3uKMmVifkXr/OrOwEakzsDdvt
+H7fsJBvo0FO9riPjga799hiqEJ5Hty3xTEkOW4/rTz64rk54zTpWjprzGDPm3Y66HgtUIwO
gOdJt/8asNuR9lybIn17DlLDMeZ3m13tOrFmqKyOmslqaipE+5HaZqFIs9IjJ8YeFE6NeupH
YdfytjQN391diNapMONTlSIWAtXAxpymvne4stvB/UK/U+wez+fIScRPpvriJcIjHN3Cpcf9
m0cng5sWP/IUfW+wyteR1fmpGquv0Io5Asl8w13wnCTU1JM1KHsrw/+YYH/aXvtsfBsY+cz3
l7R/ousnDTtPJvtJV07kgh+A9B0Xb3aZJohCRP3OajspYoJMswnwbl+zfOVEu7StxaTle6XP
djus/DABPTdhMofmPfDot3k5+WJ96cjoPKgFGKSsqqr3HDD4XthQ6vmficnbNeHLFCe1R6Yn
yWZhFyCwYfaXjiEsu+fCR7cLsD/cN50NVYu7gZrurmua9VPfZMeK5H7kuV1fEBvvlbUkxY3E
efHW+pgySy5eOlSh+fgD6KRW3dTCvh5MkH/TpdKn8IyitQKhYTu0S+mZb7dz3kV7x6EJnmgJ
spWPOeGux7eRK5Md6pOq+l9Gv4TprZ5mtjw92fFqVXSAg/VzLJvhIoQVjUPnQQ5CKsRIHBeB
D4kKd3+0C5H+EqSR06XWIxpGywOmTPyCqdH+JwQXW9IE3XC94xw+H+VJRHOdxZLpRw/mSBiV
3oYTsjF5NgwPE/oklDDMkOC6RS7zFj3b7UB/dzY6zPOVeaH0ef3R5TOUQNmvmIEVPzmVL3FR
HWeZY4Dv0YjgyHuE+jeNJ6n1LXr8BSgZOJPlB2bkAtUHoKATYQiVZ6a/eklSZnlAbfcGdo9c
V8crl/pxJjKT6FAoFJohw4mxJCQteXoYmNFDjiFlTXSz/eBeZtUTKgWOdaa5pqFElF4otpuE
Z4RykopPM8N3O8xf6HdxTFQP7OUQL9sCtX5nCH1BZbD+JrpbfkemvKiiSVBhlFk5f/XYQOn5
jgCjt3R4xuuV+xTfU59vTZwvRsf39b1NWuYt7/9jIv5pe+0R0qK7tJipYREHsalj1V1d5mob
HF8XF4jehj/PY73rRXfs+B7nHbs5eCOdIYJCPsGq0cXTEW+BOm3eUzQgOLWmevpX5f12NNDf
M5H3Wpc9mg5OzWzQP65+yrRXU96slq5tssQ1sr/9MAg3ZJcHXI5sNRAnOqlGpZj2LoJXSxJ+
uuVmAZkEJ8ZDmBl9b4A0R9TwbWLsOVhG4Ypq6l/WSos1MNv6ekwUFmvRioERfWEB+ustvc3X
ZJzCbfQ+8hwtPVlNi3nCahMLQ7gFIg1qUNF5zFqSIZCFBB6dyd4fuI3pbpo7rG4AXNX7yGNl
l2H/YXgPFc4Gmw3ZeI+X5YZkDGXnKQ6icD/1KSYvnxa3a9vrZ+rCX4p7OSIjfa3jpbo/7rsQ
EUcAKda1cDxo5oDybkT7K9AeE2HoeztPK6JILepNCz31bRfcMDAlj/a2ExpIqNmKDemqFuvQ
Hcep1FgSCnakNEPs6vu7C01q9ZhfLlhwwTyj4bsc5+8eJ4+IToqUKY7ppNu8VzBoRoI6M91I
2kB2KYW+Ru5iV3s9hWcyLtLGslf20EoydVC2mlG8oXveZczRida1JXb6x6rtskAL49JEJLUe
IHX5vs2n5jbVNGrUqrMIwaXto+b3kY6hsYRzj6y+kZLSNkBF7hoY8V8P2jEImvdd8Nodis16
QsUFVyg+fzKEEmSV+Xqe5i8ExpoEFTvVBD2LU4wO6thKqOcMF8hTDE9gYxAtLm44hYBLyRqD
PcYfeZSkNtbDk3+1O/yXGH/hv7z2+QfTbgX+4G/BsM/NnJ4+HyCjDRlwS8gOooNOFG26n365
e/zQ7+3Q+24vVrHBUdVbwlNJURzCpNYPRNUJ45/uABHdatneR6hKYzZxVXJoqSUfSFnd6N6U
DU9zmNaxlAWcmsXrN9nvtqlacj815xaHfci8RzT2LSkK72jfXGnb6opnl8mU4UManY8J0vON
GgfNdHX0mzvlyKle6jqcMI1Fi+UNZov6RjSSMRnqAapUyr94aE/4Nra7ae54/Qu27kh4kD+2
uib8Aq44CL/U6alyLokrxCIb0C2CClQ+5x3KsGy/xNeKb3ivKfnAQ9aUfVn7K3MSPHsmGGUc
W5W2hVygo4bVA0K9ZNs/+75qNzL++Wl573lyI1XfxB3wqDjDmvUOc+dMbRqLYp/4q/W8JTlm
Fxq0Zg/YzsgtXz0sfmZJ3KYpJVXEGjN4YYotad6JBKstR68zH34jPWYCTQY59O7x2/WAPwta
iZq/VtyKROAO/6ZGAQ/PpxzMo4WJNVsnpxqRBuz3C6dopoQQuNcrOZLgdIu4/YwmMZOfRS0O
ODeAxMbrTr6lv/JV3KQEI+1vb2DCGqgmQCK8i9tEEhdqNeXWdW0880TYNJLVwGF3hoEtXsKf
jBWI8tgoj74qShVCxRllN5tyetWt8OUgPreeupnRViMjUwhahNVNgm3scanaxnA3zR07e3jC
kRnakhb9idqUfOt3jrmagxVIxbn3KgpLM+XuW52K9nFb15KaM6Qnr2qlqPaJ+gn6+xavxD4H
qw0gQySPQgsMHc4aikzRveRwGRIibmj7MyfP7UbOPz/tEbHJz2qYKJfzqq9yoAbDXJqHIAij
43Lf7lLH+QW7psf1RAG7mONm7yjTewlaUjPMEYnWQWMRryyS2kTZDzK9b5Izin2M1MmVoY4h
1vAUrMAUE3f3zNSux/17x809xwIbJoWL9dxnXuZ2ClomFC5MaX3oIHgM23O49lHLVxV6ct1E
FiRulIIybt+YvXECK2tQHIpOpZzQKL+0Nt3/KzCKqG6HWIAty/YnxjNr9EE/5Ai9iBLfR0P2
2DVhKijCkVtrvIzNYyjngZnJqJ4vCeSkDvUccVEMTLpY734BkEVUF2cM7hu/+YXjrkf4jw47
3ul59tkslg7oOLy/FFB/+NR1c/uz6+sOYOrxLTc7ESkvZSmXUTeMqs5Wbtfia7bu31aKjT7y
DFt2NDQ1zCwqSsLJohCLzkAE2fLsRKasBDlqjm42QnIHSyA7dNKQVeyZPyr+n7PfsfwOpxgL
D/5bRXrC/UPm3oIRa2qBUkl4R4LqfPmhTjfuSNLs8VvNqHkTxvS+p17Sb7DlosP6EUHaWrUo
X3mmLXwtVuTcjKJ5AhZyQ52VpxfYFxtjX1vKF7rr4f5uRBu6nD39QitTJ/gbArbYNkOCqiTa
48c9viIKuwAxCQsbMCtUObDYpsay1oi5l9GFlyPdj0GIRn4CJAqYhETyMbdJs0e+bBA52d41
oFdd34gW8qJCoU0FEzSLOl2i0DrD2bjsSOz45SLlksqzFBeL4lgNj+lYM4sOlSB6P823DmTV
ztCj5djYZXZMHanZxnVXzZ37mvY+J7/vX2zRmqutLPW7H2NvlB3/goF7YUPqX/EddWScFFag
qw6h+SnmSJcOMjRJ4Fbb8sOC6unbXv4eWc40qmok87a/Rc1StNO3tdH5HxgWrcsSUSSBCQbq
Eah/VyL/2Yn3xvVYb6GLlrYyy/z4Q3IU5I2qqVkut+2Ir9PrdAkylMTzuO/k8MnJuGcH1+9S
rjFWmaNoM3KeIwTVscYm+cZCJThMQoyonRAjPrA+QmAoWjmXRtDptUrXSX19KykSL4Vx/GSo
GGcd3X7+3JFWftfeAtK5YN8Mepin1j4faROiZ886DJ6i61kR2KJPLhWtL7TxvLy7/SFAplTT
mbqeYDb42QcHzCicE6JvUunxZs48cBj6aqP3Oa2caD9683q+PNZo6c1w5Q9iXykJp9yhqrqN
o15xjDEpyXXpxL5RmZeo8O1cd9HeKQASYAllpfSKI3RezBOJI5xDAvcQItZ1vSxrMsksOp3d
1BaPPJeub46QiilxlC1aKlwI+t7vEqgmde9DHVWWzrcsER0FTW+3p+piajRziCWszBFR7OCW
NMPpHDC3MFg9j7950nUXYv/5Sd/r5er4ZT6wLbLrErX0iO4sfRKvZUhwzS9uVJsMPRJAktI2
C4QlkxydGoYauBI3fSQN+Q/Yza73JYFsDr0mHQcXF9k8MdnwaW4LU8nf70RKKFFQYwhOsDMb
mEF/z9n98H8PU8nrICFo2HJ6Ufyd7wWt9NL2SxTR+jD9B8hYSy/4Rx6ZqM/uh297IK/9tKui
s+dHnixh7jsFKASLvR/GZFoCHqhmQ+LSwqRvfaFwNkH3kZUeu+wCC88gOGLO4eXwSfMGxhje
PwyT2PlhgUdguUM6cTLlSn9acl3u3j0e8A2dtxjfoyImND+1lOhs/NASXgY+C3VkhNq3gYQc
CFfv+9wckR7E9/bYFiEPN6SkCiN6tP2qk9NWEuXxKZTjq9oG5oFlijV+GMKCYTeHGf712DZ1
/PWb4RXPNuDtq/gRltJX3RLaELqaDtZG+84HJ8aA0e0xqpotGakjhyfkO3dagC1QM7l0l8ok
QUiT3/6iXodS8cIVYzyNkvDMrd2muRIp+7qBlgcbAY1xVZWFevOGzQX1riWh1a5o795W+L1l
du+bTeadG+RQMgdUBiMvSWl/XymuPkvouDw88NiZoSlP1DRvJBDKC9XNM2/bcrn0HuGD294T
7+ykKF4i4rkLIvBBFykm84Nd4z+8DDBCZk/koysip8tMjUUuc7tEf/iQntO0vDhFpSV7VyWj
DZy6qcmghsVKDZKxG87ypvCBbWx31dx5FICH5xKnnlTkziIt6hJLF9ZvrFkWRgTt1RZe1B2r
RKOi0ofLMhjR2QTHkEfQJovqPl09cnP0lDU1/snL4lbJKE3YuRXic7uoyJVpusCHAiTEECyg
9xkEIhF49aZ4DBU1KrAEi6osiQuGjVEi9tS9uBf2GgOjaLpGj3NNVt2IRUsYlyZBQUHmzVP/
N836IzcnpJtT82wve3d4F6Uav1sn+dLtH5Cy0ys63dlkM0S32lrBoDsIUmtH8W8oFpy7gjZF
b5S1CpR2YutorzNptEMRqA/vVL2iZpQmlrOTSKxyf3V/bKh4A0d3PI8oOPE9PHxX0+FnYigl
JbWwJm7/fEY5qSS/5NVdRbvebpuMK41Ndfnvkjsyz6vkdCIrz2q6ReZF5snhYolv8DCZM2Kr
TS5WaSc9cF+6p93y0X+rV+z9unjW5SBmTi1msdWVa6dn08UeCaZ/OBcZhcn77sA+1nrEFTZG
Q+YDk9m7v+CFCzOmK7nrpJqzUx9JD55FNqCpG6zNnh66sm0AvFWefN/Fit1C2v2S91QVyHvq
sYfmG8pzNewbdxmqcSpQIMqk1V3pKLSJ2JWqtYkjBfLq9m/joKWU5j6MLrj85WALNQFF9PQD
fCSWk4D8iiM1jjYc5RHcUalHRomGsbh4ovfJMtIT//bOCNJSKktCJXhpzsvrTm1FL41y49iB
n7Yx3VVzN18cD1ovv/yl7aD+4YvkcKa1S2yP2EG2pW+0O3h2VUsBAgIDlx9g2fVkPUnkrABy
2hA8p8wz2RKnQ2cSxTSfgAaywKAm7zAoU52dJ12NhyFvD4BHuMp6EobKAqrKlwVVBUyunP1V
6rhdjeRPR8w7ABS1F56kBg5rcFh4eF5ZZhFYYBg4nKvt4b08MsJnM6qUPKHGvo/cyvyp/7YN
k6V5sLnZ1B3SGy2zqUazPxoRH5iVlNbeGhOjxhAfT97XNpdbJS74NI7PveX4uDJs2lIIbTB5
8ul45AIyAyVFXMYH+SXNVKjEbVmRDMuCNly1/8cF83+tIj6+8iU92qBGL3CgWke42UQYNXM+
zKjrfKNyAaqsO06sypPROZdGFwoYdJSROSNQ3xxhZFeQEyjt5dVQVnH6tln9ltEia1lpADKn
zKxzqLcvHorOLO6iDEAsgkPKbooqp0/3egWGcCujElbPdAVA81ZYZfa+AmFfMxxxe6sJclxL
DQPUjCu2BA/PLK+Bmnz/ZcDdyZPV4lxLGdbIUY+WOsa0ofDWhf7aAC3QZGq6DDyzKUiMCtZN
D3ZXFuglPgI+Y0qCB3JTRNDLHeRn1uGTsu7pJ6K9V+bhw6AFMwxB0VwVZL7geLVhmya06Mm0
L0cSmlyE1a/rX6juWps2lKCdECGgiz7/YWz0wUnbXrtK5b53QWbmVMmvqM2B+qcEI7d132tU
VsO9zkI8DtRYRO93QU0DtgpVfN3EuhjUQyaSiLMrHRnr/b4kA4XEE7Zqgy4CMuTkDvUeXWE5
nLre/XosXXlqTUt788Ke6+HbuO6quXNDm4dH92TXpcA0YSNs1iCzsaap2C5mSclciEVBZiUR
orNxZ2pqmk3M0s4IbY3kf2/DerTldmd06k5K+RGtuhBt9G14vBBILyIm7bgVgYAPvm0J32gc
Vjeh+ayoQwRAXeEgD3mdGk6o6yXV9Fkz5EpOcEp0yKEct/aemQl6saiUjm8UTt/jAtSg2YCB
LDvPEV+/gvqD14N2pZ//j4jRaTkbbJsBD/7MxNwnOIEyUou4g7Aii6N6LwP4psdw1uVxDJtI
jm5ubfdKN+aMuH7b6ON1TFxmAs10ia6fMwObTi0cI0sqVM52zBVqo+bNxafadEdkCPkBUq74
qxeq/sgw+PmCphQSanIpCUWl94rVcmszbi/Ndmk9VTgpDE+ao0Pv25oYmgOGuE6BLh74nunN
YUbumXmB0p5ztLJKaXLC7EeeeJrXYtOKevBDVOGT2c7cAKlsjpfiCgQiMGCD503HwAZG5TN7
1xYOb32NErY3bD1pvx+i/OmDTsp4kxS3+MF5KQqfTEbCCNpL0dmPrhkrUB1XXKjUAyXkH96F
/U2UFnqkMsbqeM/b9x6duhlUnw3fKeS8ntvsYwMDGlQu/Joiuwcb5DdWik2AI8pCC5+PsmJK
yb/sy+nBDHOvKAwcnfEF/7V/Kkf8Oq22VaQx/8QEDnoL0b6+IpIx8/15LUXmbErHJICgc+oi
L4Zl3qwf2NcV/s9OPDzReqVBbxCtA0ZV9S1JMZa+ICclURltswhIjKU8zqmqIXLJWcz4PdHF
hhn8ZGqj4U3Kndz6xGzEZWWILn6I8cSLVjbayYXVJkctUvYir2xjvKvmbr5kns5pv8tW7y/n
9eNDafiHQWKZ38wUixfgULCkAixIVeJ8WUaTcB59NTX060guKATv+lxA8O2yWhD2x1CdUXc2
oAlVQfjE5WJXStN1MhxOuR9K87V5iHGNm/9wBzpQawHAbqPIZm7EKsyXQQsc471Q+qyvu7xG
HUzYHaOi/OqCbTSnt9hOGSLUZhFwHu/oCNjsyqfXdjXcPzOxL1Q1uPrOllXpVzmeZqhOJMe/
KFDyGzp+yoacPSFEt+iuSw8yqQ/AwwlZUTOu+DKK2f2uY/dem4p4grM81LpvBCVqSg0H9t6Z
FCPdKDRDBKL2mYD7WTOUWtX+WuELbbPsCtVyfzXIRcHNoqW8vi6W0zfdFPD1wkxXpox4zid/
/uzTOzZ4ufQk7jDujPHT4EK9G3P3d5uD5h8K5jtQXmLUMijTB+zq8/9zV09OL03iCjIdg2eV
BcWfC9D+6osALz14uIfQJ5dyk4DTmaLa47w8Eeg3n5PHiAI69Gn0Ty9VKwTo99SvbJt+pwuJ
LfPFZQH17Wo2Fs2mbaw1WKzt2hMIRGgkQLe5C0ioI3i2qaO5sjpv712uIwwMumzN3/l+RqX8
BEcwtFe9DNnqkWEL0RvT3reN6a6aO8YGf+IqrUmUPbM4TVOSxdifdHscbNlWEDZXvZ9WGddc
TTIxvNy+NN8Ji5xB+s0z8RhKfTTu84u9j1Pm6S8c3gx7xJR95Lljgo1H3IZf9l2K0YTjWhon
ce0Mi+XCPpoFLSt5JhfMeyF8V9L/eYn5NT2ndQ+5uorGTfSs5WkANwAvdaqqFqoAlaWdukgm
DDtfs2wBAZXPBUZGk02lvIfrm4/sdR5b7RY9+5BZFJv47AaahlxpHMQZ2EVxBAKX74MgfoB7
RQoT1GwO8d1XMQdq/OF+owtfgcYLjVkVEixfeJ5klO1CNU9I7F9VMLeogWhcqAXiM8ri650O
90HQ8+F3TvxRZfELBtyJTa0BVSYULY90vCfxxyaz6vvh/o+drfIcg+iqhp7KvbJFNavA2Vz7
mjQ2aeshy8x2wejDMNY31Nhb9sNHHmnM8GTiDHz1BMdF/kO+9ZwhmDlkN0MgSL8hmew1VKNV
t0DNqItjJzd+nLpQHpOmUn6Y4LiVQKhVNn6gLD5Z18ARBKl69dAs/DhC4NOP4mwCa2dagwIF
3b2PPNv6Uh2zIRYm/FKOHP+8Ly/IOHB8ZXKbiQ3meWRHIWsscds8NWXaO302Xb5uJYl4er9U
cX1bX2mwSkgfFlRjSBqdOfXoF/1oOaV85PkGKvKRxw2TPwN/LZIqpKu2ngkkTtAeEL8kaLFN
i3uowTc+8vxd6dtUhFE7ck1axHdWK7YShMIHl5rjTMXJUWjr2uOroRF3rUw/hTf2Lmzru6vm
rj5SHUR6zGMIcvg4w9BcjQEy75WRbRXk+bve842Y0TlOeZ5n4gNrkM/dPrtGALBYE4V+uxQC
8ZtVFZgTlic2wUvnwLqc1vvMnp4jTePFrUtKkkUmyEOeThbpnV/4PHRbELaboBgN1JLMnpYm
zw+1mfiRjdPKHJHgvuK3zzSbdzWqPy2xhEj+jbpCb2kpjnCuNR5B9ipLx7jipcubm1elpHS/
/dIPzB+iz162J78OFUSot/IXmeAOaatKkKN9N5q8h/LLg5+ql2VQS+ehFv6tSgjva+71JnFf
ZdwrOxJ3edbh2oz//bxBFP2uyjmO/f0HXjoFaq1vh3rwofpAvWGDlcozDK8zmv9GHJz3jYdC
fGFpFGkOlbYBhAIG2gq1/TeOmH3xMEaoGYhyuObJaNcsJeF0TAzq3fZ5e0u2Yd0m0yJ7gguR
+W+nnTfChrxtqV5bRxykxXOGg30n7a8RgmxjKoQgBv6W4+Gu+OTSgMbx5QrqXv0f7R4kxnvX
Qe89MXF472uFPzeDl6b6d+umu+GRNsmEuM10gvMXAk0eVhUnuR5fuufdKpJ8a1TocN9jsOMz
TRU17M/+MH3xILHyVkzwbQEBVUjjzS8OkfxketlrijJDTMw0Lmf88tIggN/cDzp5YnkMp25h
mw7DZIzV3P/x58njM3pZY8NDrudmZke3Vq390tmGDZ6YuOhCFiakTaKiqgW9GJdygLBtnt0V
+8iDujmlEFW63JFpC44gqT2k2UhlLyp86CZwwFzz09+HJmmbqQbPk155e7mb3s4VVj/irTXM
xBMyagfZMX4yLq16kWSXJr2c5X3r4dsY76q5izAfwNfTJhPB4XBI6goZFJ9gd6gRY5ZY3fKm
IaO6OJTmySTA0U6M+fo0nWff8/te1unb+NHzK76AO7nG36ViU7PWZBHIU4gn5vGZQ216Kg9t
OuU4GnPnZoBZoO3f6IrJ5qh1gnilN8J9D7B6mse6yjUHNewVn9SeOhzKsEnrmJrsGMuk3jgB
JPwrMAFBL9RjizoN/AUsbI4wdjXgPyuxfw8ZCaRNYedhzqXLEAiEIOA2c0Dy4uljo+0RWWxb
MCVr5mh4GdtiqgkCQedPdjGWUr2y0hhOXQT9+Wu4s5D6pswGyeQAZITTwrtxun2CfUJzhETR
15lauL2acM4UJdQ2YJ7V0pAeNqzDsCbpSw/lhWq/jv7SvOrfUcj/66dq09FR6cyWrVStsDNB
R1U2W096mzWnq6ilWmMcowhZcYtOzjUGdJMekipEfESqzPkLEeATTzvxyeWdd0tN/63Gzy5v
p4Pyb98rfbKtLVY9HJcJLg3Qh+lSMnDytTNHPaYV9qJcu7BoBCJJtO4JDqnk6HLTuS0eHdqz
bT/+5O3SwmFt7LWfhCq3CfSGnbbeqAk5Qeea9e8z93FszJTEHoExwEwvlFEIIfRhnb1QGDxq
3/aLIOqUrLpFasFlpcHQ7Nh+2uZXJsXp5iYM1ptMTakO9ZY+I4VeMrT0yJGxmFfZ7ZeKa0L/
xrD9yFNuEyR2LVrXdJUsoflmyfGijH7FI5M/fHgCrq6XbrmZZnOGwwZW/zWy9AT3mH9I4SVi
oa+95OwhD0dEUJh1waXV0htqy/iyoJpac2UmQR6fhScgABARHI/JTkqK2ndy/qe3ywKrF3tL
WVxnuHUeqj5f62HsIc8PUEg5VV4GUy5v6SVPYrrb4x1lYopWlB1cMcGi6a7PNVsf6b3ASJ4q
KJoWmK3/tub9pRhDtQ83JyCGGp5++1azOQJM7A3wBCuuvVPPJoSyUvZV6L81c/+dWf+f68s7
iwjsjS0pCmZXlxbbglSv0+9AnyRjkwOxGspTbcDJvOkJQxmkVmPQ3NzqGrlPbXHPhB2ujhWw
IdZvirRMfYnA5MAxlfCcoUkgTMtW1iUUx+jlqjIp8UMEOTwsir99vIn+3YgCTQm9UecqcYQZ
fJhGLi5UCHDF6Z4MeAwZwam1wYJ7vyHGbWaHP/43NvqfNXLXptNxqkKaM5X6onIp70lp0Z0K
ehAfuCZDiuYNZEMoFx10PB/FUbYIcPyH4zzMCPTJce4511C29Q/H+WTnz47z/q4mDuTn7d7u
03ZvXM/C82Zo6U2MygJ+thXsz9t96BCbjB9pE1lItZSL1tFKTwMWA8DRFkWBA462ZkOft2eU
nvYW6Fzs0/s7y/aNa9gjd/jofcRg3XFo/HOHT4fz7LneWq5F64/5Jw0MTBhej65J9PVY759q
K9CU6Oi8qB4rr9djX9NS1ZAhLbFJnocYNsq4EfQeXrt8jGe/Uq3C/lRGtXhf8WTmm0yrd76H
D2R2xpQutrE2nn3J9zX7tWVsS107fTyKkzdeVoKzWGszFW9Gk9A8adtAPkBBBmLvY7dTFVOb
aBctd+dpBbopBOWYrzBla4uoOGUSWCDi8aG18Pj97jYHWLDxMMuXa/LwQGF8KQnSpME1MR5Z
KS3tcEt3DHGl+MnoJj269t8ewN3O0N0tDDyelAR3zuaHZ6Mcd0bGrQmmUbZjzp2eC01q7MJQ
hjnTLQ9TnsDzoCIo0AUZx2vXvpL/Ouhy4DK/GyEnJ+XSTN6o+5rOor/3MGFJXc+fMmcBHiL3
vcYWR8Dm5BlOsgaxqn/XaZtIfFW0Eu3pwx5FZZODJEk/xgRGpBEfB6ZFzjEEWXWG5uq2z8/e
N2lfYCNM6xgLIV+J6e/VYJw80W3V6UaBbRIyqOptdqrKEFUgRA34da4uhO9WJ382+sOCD3s8
B8J4NG5vrta6d8akuz3Fu3fHJAw4NFGZsAtdxZLiqKEakxW1+h+lYEFgwYvHntDqdXWcRo19
2qo5L17ArZFNlamGuZLw8XZokBKYPGAcnX9eYRm7jM+jgwiOrunBJyIJhODbVynBD3wq3peC
/a5/kLxYegm47lmoNjweuI8B6gEJj6ZhSRQ//BZIz3+eRYI+1Tk/iBk7IPRva4v3tYddzKsV
NOkV6ulHHmaZ5WDbq3XQlPgnY0EdMBbgM4ioSIJsUa35cFRkUtIjY0nlzZMadQVjsfVNMpMr
957oS66KdebbVj6Avq2/76RUDP3ZT4/65KeXlEQm7X84tk5MScMFTQ7e+eSnt1tPQI1gsQb/
MBcmooMYsQlMGYwMJxuTxVUWop9+VGETWDNTHbwGGPcHftq6WkxMO5Ifc8Lc3igewJeITwCB
NxEqWO+b8l/shaung8I8XcUKjWp6gmxsqzrUctY9gwR/CbwtjdIgIueS8VlryqeHrq5CgHn5
yRjWNgnszw87/2RoRiRrf/M71XTi8oLCqp+bA0HbuN6e6m1KIK8JfIBlrx079Pm2+fu3D7kV
S6nGD3V0BobVgmH3SUoTdIcw2QhsgsYIDia9PwpAaFfaaS+Bgg4lAIh8Tfx5Cu45I5cBRbI/
aG02l2mvH3dIx3GvFjz7w29tF6irn5/BN2xBt1M19Km1YIjjAaOvSvp6alwCxnKOklqzBZ29
W+QOIyAqsUWhGi3C7kAOWv7spEyJoVWnWgizfTmOjiiqvYq3fTVPaj56xgYnfXMy0DT0p5KZ
V/Ikwh2ql6KTbTVFdQACiSbiEbXkXhhM52R6/kEYQSY7+pmMQyL/nRV5miKbeGMgdDh6ftYV
n2tsQIsszOo3qQl+1Rkwk8XVBTwvEHLarJBfVCT/H4ai/WFt/mc78r7o6fO9NCCiuDRfgqqi
RFWU3kNUF16yIm0o6IMogmqt6dw2PevspLQl9+bO3mR8dnHv+X03xgOV1KlGpU3xCYY97Dai
v0WLkalhQ8Fz1xPFDGbSomt98WyhsqGApiJIyMSwcUPuUWILaPWzAQ856zuTGojY1kpVBf+T
lAjFGrCGXBIHknI91EHQo7U3iOa7jDuYz/c6/RHz2H9gnHyfUVGKTYN6QHTe5iMPfNwmxqiJ
o/nS91N4vvNTeP51noxUFhCeN34qI+XoePVUcP2CM0u0Pl1T8gI2f3C/BeBU8LAHnApCDtIS
Rx5WMH4bn1fNmM77FJ/PjypcPdt1w28axMIg3X+Ozydl/BKfN3PF/Byfz/glPr/qPilYfWR+
DFTcLBOxur8jz1+j4sItwwBRw7XRIj8CTmHKftFk9fw/4nn77nE2a58haWKCnhx3771W7ws5
tVMmU4eBgBKX9d9ehe95V4feq/PzeY9WqMfysy1fKftpaExXkb0w5Qe5zoY53IO6gY6LjeNz
ZmnJ6G8FZ0m+HFVf901V7zGymrMbs0I8ZeN6u1kg8gbFAAqEN3NA6gbrz7ZBd/bxLsr1rKYY
j0YE3xz3Q7RLmzVUsZgh2DBxZbschIVtsVnbgiG0PI363YHBbhsb0651zavd1oYE95vAQ0Su
16YncY53F8CxPgbGucfpPCPhf/Td7gp988tDxuxdL8v3o9UxupbLHRGz+p5dxaBycRq+zZD6
lYRcMsadYVFTO2k3kt88bVDjDwHpfQYeuPJVvWSAwkjQj3atHmHjiYuH1hQT4zXV2JwSJJt0
gj3ihvfwF/ygLI+BSTnmLZh09tPtQr9155MXd/KeofIVkrPen28umC3JYjONdAwndIrqHyRG
GaDy9L6BDafRmVJSDLDqt2f33po96uRp7O7kISEORCY8Xcnxq0+BqmOgSW/lUTxM9gMCrUaH
wj9hDK6p/Ce+hj+q9H+7n7hqs6ZmMN9wzDdEpWjtFlquKQXsJ3i1KrKhfW7jCaDxyKQZOYJb
UkwiLCZkI8H2mpQTxjQr2HNEeNqofiA2h/qgqFAxUCIFpLEJgZc9UYXC3ajxxvDs6PJUjjVH
cABiCLGL2m/XaPy1npSnVo4Ct1khgCKJYKj1ktJrBUwLsmwwQfURQn4PtWAw7RWgXqdG1sw5
LuhmounJu/kR5aLdK0FHf9AG83mM+astAaWBDTZC7NJlhhtHqX5IM9eZPKg6BEpUOZzzbyvi
ZwZ/Nsvn0hbyMm6LqNtUUhqf5y4GGDX0BbgPCJYiXyGx/7ZGHsSrwxAD33jPBmtywZAyQp4U
FkWB6o6cPkt8ESFx1/914zS6aG7xkJ+mCL9jKhWHVgcL1Z1VVr2POhfFPQ6KjDG3WOLa6/ZZ
iUX/U4FHRSfT2UK2ZCA5jIA6RHUkEm0hND08zd5y1PrePRVFSyKJ4SJJmnaTUDfu6oOTkAkR
16Q1DU7ntQsy/+Sx68Yu7RaAfyC3qzABNqIBwih2U0zavNjAkaTTpN4tKmrOxCQw/F2oW+C1
u4nRRcPTeZ/ZVw/0juadJ2uFaOB9bBs3JGPx7ubDNVzdCq12kLL4Rx6V5LT+WE71y8vNQ3xB
psWDJI06ql1XMeIGHem/KQuOxGwchOfhDklsmBhCarFtAzUmIAvw6Z44h7L3NeDYZ96yL+HJ
XBC5RxsZuQiTfkON8Mr/TpsBsSQuaoMR7fuiZ9DoctEPFehZj7+nGLSRzgKef0qHZ/7K5Utt
UGy9UyeTkwwsPvL4tM17f2EQkXof2nZjrrqpeWicRYkUVnd/HTtgMKa1zwjlAxWntHnJJZEc
8+OiOIFlMk60HoHMZmNonranhlcR/9Gb3QMVfeQBm4dYoTrT/FB0XNx8vIWhsDZdrRVhYegD
EWRyvj2sFE69TH4xEmG1kcyVv8wCG7RPr8kqeSGzKPYwlwfD2KcFk0nUeIvlqOhJzDmC/jCv
vM6ruaNNo/ILVoySil6iHfsxmEltyDXUnBtPAyrayXGEZzOKIeDVVGULurIQwwHZ3zWz66n7
v3TgreK6R7xaSSCpoNDHNPISS4tsW3q1+b6rBbwo4P8HL0o1gFQAUQhrsp/gh1tSzq2f4IeT
jN4aIm22RGUdgur78Txu/xQQ4SQOjYW7wtBZ3jZv+YRc2+Hvi3MjSuHpd3qKsbGAnQUVlcEQ
SQPBvilEu5EkTC5D73DrjwR43MwX2k1Qq1ARj1YARnxzwaoLM9y6v7P24aW8LXS87Ypyb9bK
ZCl1ghD8xL9RLhoGp1w7c+hqj6jwRNuspnAXkNgjRP7bYtCGydSpaKUPQzY4ddQ0gEC0aM0X
vMh/5R9K4GXYdnhYr/g2QQVJT/WcHW+7sWzMU7Tpaw/LpiDI+lUmp0rKLAPfUEgOKKSSvQrg
ebEZJd6LYiLBkrGkeBTRqqgeqJHWa7jV96Vsx77+8P9Ft//6n3eceva/WfHOwcssE/PGyVoa
JPzgxImTTycKE2KewLAlHjYEbRAADQKpg5VHo+Kq3ivqL8QO90X7Ok8Gq1CfVOuiFmih/Kke
bVp2jSOOLm9q8rJmQ68lRRZ6sZX7Ku8Dl/zGa/VSbYfnJnO2vl4a6WzX3K+R7KXkiFiXlxle
XyIkJ0Wn0yT47crSdYohwhsnuHPeTOdT+XxrWfPuryefLigwcge5VE1+gvK0IzI4kNBcDBJU
tlN+YkAPRJph4FTNIJOA8s1qv5WvO6CJ7n3wDiUhjZH+ga1guipqOToVvEfb7Eep4WjHjeb6
RFJkJNo+5FtWr+j8gapeZXOz9SRPJ8S0NsMmpjDqQbY18TxbcAQzO+LIqYQOZaMvan/+3xr6
67Qkn0BAx2m+jON0E7/kZI4Az1jLufnqxkQ+AgVNvdRNooo7DnWT7+Htid81kbykK+/Z5ViR
IeQ1f7xO77duOJE1pnu5ltL4xsEBCeSLoNd52ED8aOWJJVeyIBOTIVwLgaKi5lc9rIm0obit
K3SFjzw0rlZPLwJagpIZ7GGm5qwhMKgS2msKnGYJk8KMETp0QKyljQoHccjbuC3/ub2kFZG2
PvT60mIs+KFoCbY6VyI/Ll+CkN2urvWh3MTAuhganX4efajJru9gMqe3ZxUoPFoBJM4dxibK
J61VMLrNc6dNQhng/OmD2bTm9FIuk2iuVksUlDhe/wAefT5pDqK+1yn8P/i6PhlrMo2DRr1v
mbZXmJhfuXRM/unSafqnrXbqrc9tVhkp3U/2QhBxUMZkOX9OPd+eHPRFvmZdV9PKZMlGvMWK
piP3AcRB1mCvsY/CcIuZGXV5Vr5iqCsZmkebZFqGlFY+nygwuzfAOL5MlJRuON6mmWvSaWJS
qw44dKZttKpn8sMCj96Z35u+dWWxKe2z/OiVAnsjdLxX8AkuNG1aKZCAO2uvEu2GhxFfHuB9
V7x5yGdsBRtxZ9JKq+JJljV+SwbFbygyO6fAGI7m9AAR4HHcd44w3uVf1Lb3Gy2qh02QQ0Lq
V1cIUQTqQP44Rle3Ejw4bXqHof/VWiup0GLvizXJqZguFjTa9hoVJOhi3q7GERQNlozD5wT5
eQDJForqIGjZ5dMJf3xP+QM21ae3zl8wOHqhfO+H4mjOrM0D6/3UeLvS4pPLyuWmvseNn8pl
nG+nB0auHe88duTcYKYhv/BkYt7ozP3ospGOvLIJ8pi4jXCsmaiUUwOS7cOADx+vWZrr1HTp
3p8xK/u8/pLNQTj1Jw5VMMgRPADRLDryHZo/2onW22Fyg6xuEoqPzO/ef8Qp7hSQz7rNqxnO
qoyxMaIpCyvPLis8JMxKSdOEp0bNIfm5mc3877upjmQyywo1s7huI4uCgMzVhyYwuigPBpB6
0PgnxW6SIIsxozvjp9c3GZvVJuyOzLOdzTdpNpxcCx0mdLouwrBQZQJ3CuQ5db9wIa9Ep6y3
EGTdd/hSbJQf6WmKbfCpaMdQTA7WW29G9Qi5QzCB43U+1XRpgcXOLDJ68VNtyNbDQNHh/tsr
7O9WT7yNDtZT6ymA2Jt2onqJQ0swZbzeW1VdMZy9qe+EXD5fknsG/Px8oOb5nMvLjptqJntl
a0aqnzSvjRVHNYcdVrQl62alayL3QYAQgQl7+nDntUH+153jeCpf0JjoEwBxPAhHeRisSxz5
jj8w5rFt5huSnToYCPH0/vELk//B73sHrHQvn0xKegwKCLC8Q5cIINuCJZ1P4Cl19sfcA+H5
XrM2Lm5qbXPg1LzBDzVBeuJ3D19XSuG3eJmN4XqfrT6frl+ATJEv5Jp7OZ8IpbZDf8wlC2pF
SBZpUysXD98p5/YvEfcrYRnQ+B5rGeIp6+bmpE1QLCm7prWzC8/7/aQdLMDk/dxE3et3/jE5
Npm0+IiMQToy31Fp2Ca/7/kJ5PCk9+seGyFG4YpyebH2rGC/efZtx366xVrqBAmyig682r5e
CGSn/ML7AsS0rt+U+V4p8MkEM88owyQsCJ4SgAsWV67QKpzHUkZfvyeFPijKNQGps94tXNcX
F9zshaLzcDBM+tW/23QBk9r7a407o67l9r1dJxcDZWrZ9iPObt6667UWtg2EFLh001BkEtqm
mX9qwMMozmn5zofhWXkvTmpEhJdsXTdhYSJgKbN9o7GmNjqj9SNPSlDaS6TsAS19r8qXIy2o
jzyV+Z6Hvk3HyJT5Hk6ufh3zuDXsYMyJeQDvHLzQQ/FK6zXtDR0oZUlHBPH9gNFx3xKfyj16
Z7wAGnGpzPSznOsQyARDjYWXguMsXZpOvw3fwUvdBQkfb4UG/9tBezawBVxlBn7aAiigHvHr
wg9jICbBseYgc11C1FytOQC9LVA+HSfhrKXivglu0054qts5KyYV1Lkq2pkP/ccOwIGwQq+l
tbNj0oQgAYh03gzm/kUAHzCylipb8aGLrIkEdgCjn5BK41o54H5/X0NBdaehACmMzGI2Zjwq
CQ/gA6SbjK30hD35R/gZH0aixA7ZU9W6VwrQFr1tHp3MpBkCBo8cXIGYLEVv3D5e40eY2nPF
J8TpWo+WvSL5Gbw0MA2bCseukJP8xqmOmwCuSr3tE/oe70RTVv3i6MtPauEVCrlLKvY8JT9Q
p+HsLzh73YZWvxhUH1WIduhuRId17G/wwXULoyJkxBDfPbSecp6mXv+uY86xDCZDoApYqpdR
owpj4E5jJnvvhu9Cy78m3RVEb1vXo6Jj6cOqho1AND+OLig+eFP8FoVsPVwYetsZLka5Jyb4
Ha1xFXWbzSeqggw5SQUJeLmMrVwZp71+X/2jrpdip9ODk9agSbo6iK3v0Jr5OnmVKU+1KwuJ
zHypRbEdIzaZ3haZfFd6v8ZdY7FlHq4Iu+V8o1j/+hgckbSE4C5cvT9hx78Uy4LUoZs1CmK8
4CuNr1CLxIWaQPrxvozyTYnZqb3itDEEoc2kBdecd3aNeo1aRCiW2IBZHFa1HUusTwmsnEPE
aPPppW0Fc40GzTy4F9j7VXFtWKyOFiwnJCziMl0yu75DJd1lQ0bh4mHZG+PXW5YS/WoH7lLM
GNlbDRGlC2tuy/n2JP2bp470puosuGMLUl2+F2VjOzaKeqoYL/M6JWq6K1W5e+c3WwLjpyhp
f3/N0nnTvyIwtIL9P+y9eVRTybo+HJtu6VaEQ6MgyOCBblBGmedETzPYbQBpCGHGBmUmYR7C
pE3TCgjRRmQmChokQBAxhhBCQOYxIoQACfMcCFMYA4Rv9/3d9a177zn33Hv6fueu3/qW+6+k
du2qXc+uqvett956H4tqt9od5epxzBvBg5JthZEoU4lC0v4vTesK3RvWFE9yyMpAgiLmtYiK
qfn+IhPuc3JXWrdcvzJGmYh5MTmGN82hePpMCBqXRDgvxN4gz2hHPy/13wIOKPQy6+J1DnYC
mZg3QkyBCoZedHiroZSgcBgWAntcMmdG2zPB3ZLUuz/EQJ/nHoOe1AM2642JY5Dmlvc3O3z+
9gfv6PhQgvOlB4OGfi0UeLleVJBDyXiB0b0sX9PgSHFzHf73ewJVkzDeq8ahlXmzWFmZcrem
bM9t/FxRnXxYdEjLMgxVHSBoQ5I9nP9RiPod+6Czr9Jc14cdSzbPq99a8IXBdQ7A8uTHawLK
bezsjjbLpKkN7FwqrmgMz6HAO1d6vKDxj7xR+uCCwoBBO3eRK8y/DMLmtxCuUzSyxFIx8O5y
uof4BYZ5hbXX3k+hc50cc1FysHxd6VCq91qwdx38T5HCFDPXD7sN9171w/MqrKx7FzGReS+k
OeQhpN2UE9k8BFypa9Zo0vhvevL/DT/j9iX3DMJ7nWLeqZrFzM91YME9SeIMg873MtXmcH2N
c5EJmVayzrg+hmag2b+Kvny+/etFQPQp/R/RV/Gvou9X8qDdb5R/EX1bKr+LvriK30XfqpCL
Pq5KofatlYMBITdXk5dvjLRLwVRVQwVOM4w6Q9Ev6JOTfsxjkFPGUb2qjFSr6Aof+RhxLd1f
JpAUTTTry36/Kj8LY1uYP7ygCeYY6iZ9NWQ06+uAjDYSVNvff9qQqB1umw4f6k8LBXdoUm7g
1ZfIZm3obnxWGrzM0Pi3uT10aAHqRBI7PoD0hJJQ9tEA2ex6Q2wey5eN580cLHYVQzpPGuK2
0+a5N7F+LTXV4Z0YXcc6tS4s5P04/sQvPhE/LGTrcSKYM+b1zspc52qizissxtO/LY+yLyhp
Y8LiIXm41o+1zRTdU/OxVlJ6Z8gRZsegrSG/HEEOJaAMMZ1CTn/FVcOY0zTmJXTZi0X8t3az
D3ZO7FtqHJnVpkOZg+8kpLSXqjrtAyJ8HFN24s/BLu56hncvZINN7uA/n7NMnjtkug6o2VDc
ode1KgVfZBsZUXTor4LOUIqt3FFhuydNw2xqFmPIsutaK4i0giGPYmVyvYFXujYvv+5deE88
QrpR60isWO7cWj901Vo/yESqdLZEUEBJXWE47xAefMdxTGjNJsmwoM/WBtgnDwpcKu9k7+T2
ot8KlVotJjW7wDn0ihBG2B0ntGCbbfpLwJevyoMAg7laJtp1mjY8MBZAhvvPaVt0Pky3c5w+
SbHJpDzkeMiOUbfiYiOAsS48NDqmt39p1FAzt3RdxaqHAvit4hbm/c/aII+KzNmcg8EkUqTH
F7XGzSg2uXn8LOdMTWjDgFuvgllbC560zcaNiWoDnVL7nzBaTqDXiuRWEhQ5rPSSFrXSlwi1
Cypvx94PVvtS/f3RurbnzPZ0zfY9X3E0wY45jywmtAoltyp4b4gQ1QtFhVqzLYx9CYYGI7Rl
H2wppx6n8mS//sl46kHPPsIO9LGwsqUh1ChxDfVWRCR4BTi/mc/YUnNmoD8SLqWUNuPzFL17
hzEnL+cP+a8Xmzx2/cycFMg+BjXxFYCN/BAGFFDGxhJ+9wTKOgdLtOgggYWi1g+JmmS6tine
3N4OGoVb1J+xHNJJb345vZx3svx+2RJpqIyalns/IX9Ig4kzHnD7fSsfIBocENO8+Dth3Ikv
ZNz0CRdqCgrtzIlmLYFHgtB+xaofSbjUGkWv4YIJwRHsNW1pamAsS2fSQ6Q2MeushcM40whR
mKVjN9nqJL7xCstxo1hvt9qtJkH++Mf47wf8+0/qMAkgIubAX3RdxuduK2esCwvCp1YbWWdh
FpTqHf5LK49vJVF38vvBtGRo0lfdc5CsHvYyKbv7vpA6PDSW7jF74zNlXHwMTi3qpHZlqFhn
H8Xc3ieU+zbI3D3xmhfsPnh2GJdy96dcUzVDYNVUL3yaVa2bgBuapccVtcAyNXdOpC4XXowx
opfhCs4YRy3WAHO9TGRAXjxazrxjt+nBXLjtXHGd4pVadAsThsqMMgZE0pbnj0LfuS0CQTXl
ExVMEhmvlQYLjoT7fJAVZN/zeOR3Qc5jYkZRWrXZ7G35nQHcYOxG9s0rvWHFHrLVQI/obFAN
lObF7nNL9b+OjT3rVCfkAynRBwSslSNv93cBa4euuAMIWKjzrfMO1R/zCzlau2nvpyIx5XZH
mSIhS1sDfNQ26QA0uVnnF9ZeCnWrumc4tli0oadbqLfS0l45eRua9H5BvdBM75zckDRkRvac
3mF/CauHwhx+6M8+AB1xBruvl/T2zJ87yx9Wa4l/luAyL/HqaXNJQwJ/Rk9G75BbYZsfS6wx
1KHvXJtLH6wqstLy7jWJpK0D+9uSUnqFka8wJTOa89d6/eJhpMmB1b0evMqUvz2gNXQx84J0
jkF51WZHj7yNEp2EEcFlDzqbhg25sniLNJRiYtPEM+k+JecGHw4LG2aQ2Hx6p2S2ON34ZnHZ
jlJ/puiawJWPvMmQr+maGwF3mWHK8U6t9LWZlqMIiRM0p+Xcx1aaktLVLvh4p5IYK82d4NuS
FuihY9B9/aXS6WPQiV1FGQ/cQ1P3Nqhl9VQ/slbroTvhkMCAovR/rb9BgJeLv15XtxzpfiG9
kz5k8yTdOtZ7qeDqRxMKed53SHk3UbOjVogqiJv4xim8ZWI6oSRZm+3BzPulJzGp5qZhJaSs
XQFVuFjtlVG7s4w58voLXdVum6FZDOhH7VYLaU/UHHLKJXIq080AJcO6HCkbv9wgciss+nB4
k5AF03Gcv5FMhwFBGjCdkZhz0AOxqFqtMaXUeg1GGbZSJOWCi21q/UBKhdd4yo6J1KykOBgh
66bpoO6WP0grR8zC5G7J/nGrzH8y6v4byYIL+X0iaG2X/rc874ojj9NSCjT9N5eKFSYeeaIY
MrV/freEq2xts0p/OWDZaY2YaqkWXdmLunh+3lK/oGzGTtd13uZXMdEjdMQkC4PKfyMU5bCw
kBkvnluuneNWGnqZy/v6KMZuzQmLn2x5Y1SyqeGJKwOOJiyRYNqjnuNMOta0c0vDb7fpvb+b
s6FyE9ZHIi4g75f2PM13O27akCnfZ+cjnw/dzzIxHgiQ8AvRNsrhula/mLIDRPUv3diq18IS
xpXZGpFLmJR61WkZQGunBpwcTMx87Kh5xguvN1wN2Yd0Y8vyZQ73838b18886Im9OxlaN+cf
MQD+ea5EnO7+YmyM7oquvn9dM96rknEeOQBvET69wrp8BJ2/c+c2YDb4wuEgSYIylJ8HBKUp
uRPc0MPb8jPkQua8OwzO2FWIGKCStc/nxupDc7nW6venoInJJEdNIXyZCXeWhaszYFibnoup
HGWioObglr7fx1q7zc0+FNF04tr0BjH49lgV30YA2kL0IIkHmiVt4i9tXxw/12YhuzIvqPGe
G2dV5UA0O3gqr7AisLOaMkh24SCVbsx7aeUdYvKdGeXY+NzyzrV7YZkJiVEcmW33sxsiN7EL
RboPSSXUGkkJr5WkxfalFJqelSas4Qv3B5iV/KQfiOBtp5tCmGtLSn1Pq6x0/S9AkIuZ4Gga
6zy9F0x7Pr82fNItvT8srxvw0IhKFAopXUCwRwY0t2vDQN1b1g/iHDuwuayCoFFHXZtOC+GT
1q6W1bp7+MmukDrJCczJMMP8YoxqtP3oyAA8cxE63z560q8k3HzqTOrl9Ka2yql8OLtURERC
XGk4dXrt1u3h+HP7LtWhabkuyyn7YKFdXMrg+uXiquemrw8OPgoxv19S6fQuNNeZD6TE2udw
6dm1WmW5O3FW9le1rCBYJQVUEC9UdV2rl/kkhiJa5Z9dhvFO3fTO3b2XvxT3W2jaC9uznqEL
r/HmYKS571CozwT5HDRJ4SPJe675L1RJZyWNQ/1GitxmLRN+kp7oZvXqkTcvcoSJMhVFfs8c
RZzT2S9rayEiFJY9T3SaRW5ehVz9b4ymP5zlRPoaXzpQXTmo+8DywcF3P7BQYJun9aZA+OJB
c/eX4bsZW3DZl+E7OKVuMVD6+G2Ull9MUSqrvhpBTdmNA45cGG2z8Y6Y1ZDNA6vwfYCyDqWy
pj1Hggr88I76dUzn0jGIsnBtfVe8mwIboSR+Rw+KPlL58UFenNFSsXfgWMqDVO/tvPpLGRtW
wV+dnSNWSHwZnbJoSmhPV4yOr3JdV4uzI+jO+o5IKDVlcOFPAUs21ofQgU/1K6XAr1Gd1YnF
q1ZKYu7MugbxMqzPKGDIRogDYXtvO/+u0JCfQAH3PFm/lJxH8c9Ap7ZW5QRywc9GHEnnYLgl
cndKf7KYWbSte/biHgG6D7GzVtOc2y5bPX36D0MJ+gfPIvwXFUW71vhvg88w7eFibBgUKpA8
+E6xfcgvLyI+/7mPuXt050DFWAqPfRuYqbp21aQqlzoH96OnitzY9bsaHJNTy5jIoCjBM4Wd
UZed07WtLdVNTIqVDk7eQ3vGH4Q3Xjnywk58g5pzF0ee0CGHTVC3i15iUmS387eSfu5acuqY
N9cWj/4uK12bPcrKK+iJTzC/2krIQNcX+YfTzzuSu78H5h1Z0hQ0VtZorNFLou5yaCsMMnRo
Np18DrXNNoq33bnyTPpkWb9EEqMM86Ded9wgC5WZlZL2WHT7LXNV6DuV54UkEszRtQ9mRcKk
F6/2rWNN80r0jA8apyKE78fW0bU3VHKC5BTjr3cwGYEtR0G8pvv+hWL7GTVR79Jb+i7Mje6v
FFQcoihs4Az4G2Ex/RINPce3PcMsaYOenG3VZUlb7e29t0lfD6GswqpetvQJv++PyBj3fc8y
CAfoc0XcXnuNyGjGzLdi/cmN+dtmiV6MrfLMNbvMi1vOs/mYQozNwch7q+3kszElVr1Y/Hh7
CvniYWHSYDaCtXGe6ZNTEVPau2hsRLdv3x0it48IZvWsYlERkLw5rnEaNG67t8nsKkRtY+0V
/kMpbzk+pErqErev1CJ+fLxnAlv1RqSDrUTTSwr7MCIdwlBllW5L5nnLRMRWh7Z0gJnxN0lL
BJmymZdhW8yw6+Wc6aSij7wabmVpi4U7r18XPB7TxRx+AjTiC3NQZzCvk4tMF5V42yB3Z2cb
6cuYoQ7d/lH4hwnnDP9LGfRAhDhjC9gUF2nKE0q6sYxsY9rKideavtEqpW+pseoTjkFuoZNa
rta1zKcP0JabC1h3DLxl1eUpf1z36mzQdi/e2Hzc8TLG3W+8sKH92bXHfoXBkV8Mo9NMBFjn
a9g8Cefqx8zlSuZJy5Sh7uy6aVOZ933yThh4q3MTaWfzsqBCQKWHSgTUvDepVdmY9jRB0Y8r
ys8TQkOXv+icjzObu4NUM6YWaYVDThP3VLKS5FvZhE5hM7Px6YznaRODZKLuV5ztp/6CCj44
DXkGDvtgBn1P1waJZqLqLcngZA6oM3z8GSuH3S+W1iM+WvKei1Jq9zraGTO998iLm9/lbW/u
QEJP0U2PQW8QqgGJEa4CnJJ8BAwf4zcPT67eYlJt0MRwuUgRbRMiO2xyqb4pmKEeN1aBqD+N
CYu89ugnYL9o9KHZ0uH3oyNuh+NKju1VVIqj4cP4bqLWtJKExwAyihtdT46ILxNkIpVkV6II
CWOJN1yvmz77Lwb2P3j7MPcBl3YLhViYHM7YrVF14QU8lguUjrTeGDVwW9CO8N0xjjlEROAS
xq5OhUX3N41p17NNHEdqKfV8iFsrkTlRIX3SUlf69bRrvlNce3BDb8gCdn5tYAmDQgrMkXon
lJ+WUFy7gt8nZEfegu3gkzJ6FnyeBEp5l7PaVqSKIa+XIxG0fbGLbbruJfWZixva2e1jsgtJ
C1vqwgj4eAWdJf1tX1lcmkvG1gZ+jvbceoR+DBJWFUjrZbd3glWhw9PC1bnMwRpijReVwXxx
vqF86MaTeLBiiM74Rf946rabVCvwfd7P3hQWX3Med/SEaE4tnA3ArL7lgDGE/IvTNShmsDrL
pmVVdI3MZUfzXnPiywkCEnSjmaByU7586ELZHG88lfVug78gNWkQOxamhUP3GHoRAEUtqh5b
RUgCTWvXTa0FPIaIxcT3q9qUzWwvMxLoeSfS/AsDSb9SIGsap6Oj0gC/J2654Yhc2ONAaavV
twX0sYzBwPHzzjwdP8OBXac3wnLGFZb6IyGa6Atyp6nlXmb42MRfKDc1g2xw7SaS29GO9faN
AyXUjpmgXqNXwEl2T5LgudiyCRPGDCEugiLDD0Mu2cf3qQrME2iJYOM33uOFbVYTuboxxn7D
4n4Yrt6t0wW27Gt1ymm1TGKONBDqaw8TBidCD57GXjWZn7Bzs8BkEHtWYdrLbZP4b2TFa/UH
kZG7pUreIRPyyptQf9uy0ZSduLiPX7hBYpZZ9NbD8VMIV9xC9zkftsEgnR+5dR28LKNhuEid
3JkMsjejFVHaXwCsej3W8MTXQlXfL4n0Oby00s59znFT9qFJorbrgHjnYueSvmlfJPcG8TwR
q/zzM7TKMIe+3GOQkvC1x75jX0cvJShsftc6lpIMrnpW1tPF2d6pFFBrXkTi4dC4m/M3Tva6
VziNEsbQNVnXDSs1nr9L919LrgxTys9CLoREvhRX5rHfLB9c7Qnnp7ieJELjYNND/I5yekHi
tZEU3rJuUl7rYnVXa9oTVseEtE1natwWHHfLzsqdlnRfbO261pHGi0RFqXhNyViXEHaYbEwX
Y21Am3+6URDi8xIjv1PG8fgCP45xp3SXAx0hMxPUpZNQxMrxDR+wltBghs7azW/dgW8ujOUz
VFaFSiQyx+2vLKUGhTKbfyiGvOHEGdesMRDXaL6H9cECCFoycU+ymaMVu7t2/11wBS1xTa1R
61CGQNTp8izUvzoQIm/S7yU+VouufCCoIHq23d9THnz3n6uz/fsJ5Pz80VRf8/RTFvVtdPpb
ncr2ktn9gObBED8KQnlbpfT9v2hw9v+qwfGBvSjfff7vGtwqLSW7lELr6KOgynMA6z/Yw49k
+ZsSQd+zgQt2edKokx20IVCQgSHPhzuWhwSm7ar3LvPUSwPal4wAx70pxlko3fMQamclhup1
l7aM/n0nSgkIzgj+euP0h1gfNMpyVsCdNOm8V+bV3NH/Rt0mySYGYK1134bBf6vFj+kMjJd/
OHPYr9srEbpkkMdn0dcJbtpguv6GdvCbS1QvebrteN7/cUbI4UKhLUkXZsB7gJkL/Cdkgny0
rIyLD9LfiHA26kHecjXarcsvg1/Rqym68rNYndVKbD61gEPGtSfpRT4FgjllL+GK+GejU1pL
hnNI2Qj8MYj1c3TjvwfxH/n3P7ZJ/eeViXQ+yOFosuTULR6/9DZrc89NSVCiSagOwJl3g43Q
p2o9ylsGyoMnArxb3aM7+jdWo3jsb843wJUPq33c8vcLSMFAqNj6bdaoVDzMhqxHTkJ3zi48
OazNIXdHnSlbO0IHTrsc5F2UPlnSIaE4+gJ6e3OX4Lt2DCp3JqF3cUsrQl5KL3fl9+HKZA+B
S8W4er5GiP+gJcnK0BawnmR0Ltl1bO/lEN4/ZCFLAkL97ZjLVcBq9MYLOSXJfs20l4gxCLU8
HU+HI9ffDgl5HoPMExzUGbBIIuNsYAvtt9QIK7Bf6fBasjawGp0Lt54bqsVcC4E8GCod3CCd
1wcP6V5sJ6g/kNYji23IZTDzxeNtzJYcdw/ig+wFpCgfukyUS+Vyl1JjD4N0V/q4sj1tUZOC
clkfJjyKlT6YdPjt+gxukN3JiQHKz7zqMGYITeeUPXRbfH4WuLQ4JLQiijcacNIwrLhK5y0d
rJGw/qYudl9pGlsiprmC+lJObTXtkOG8f4bebEz9vny+fczzqgELn1E/PrO7AdfTs0GuONM7
1rZ3/AQFCz+6FEKt+fdHjMSRyJULSeLGgE0A9yg4ysiFS0eUYQ3+fK4lAVfY/SISk6hSCw6g
aJLmamSWJ63NjhQpL2E7b27L6Zqa7C/0q+TX1ouwxFXQdE+2QSZkfq3DtKZb4+YRWW6IZTo9
bgJMUuIWVgm7qfhr7PTCQcwPVa2OzPqOkbzE117LmTZUs0hBItUuzoDLNfVU2Gm6buqRaf1i
1CpBjz87/5eegWNQxe2ATBuK644gkVfKux80zK+bVhLXnMZASkLeqOweBpEEcaj73O4SuHho
9EyVEx5il4WdhoG3u78WwTHs8DEV7f4GnISE/KsfcQfRH0WKGfZFqCDGOVgbG2GWgKUQgBbG
iiutJBU2sRl9RUpIM6SpoD5xJ56aDojTpoHrhj3u1XHjXi3RTGMJJeKOm/hsFK97MOk3wlBS
3nKi0ts9n6ilrYfDB06PRLAZBNcBs/b7r2ud7FHUNfcSsUMD6T4RF4QR88Fe6XvT+4/BVQ/K
tWhjbhXSlAzi4fVSvnZjOiFsSTdgK77uG7kIfC35DdijuyHT4yNC5e1RfYwgA4m3rpJTm6sS
rno5lmV58E3ShI1rT84+2LGSVl2PhQxfW8kgDbA3KXJU5CEIXO9OcnaLp1zotoZVebQiRhHx
9UbXuma2m4ZhkVseAHdTAjVtaIWxw/ko/EO7C14EUHMkJ99tELdyowlHdc+AN3hX8Dkmex2T
2L/1OBnOpIJ4lduv5xoSXJqtv7Xbqs0R49NBvMvLLt1ChxgRgxLZtsJS2oGvyQygIrvjG6dL
96qs+QUiNRIVu5f3ZeoRw9MO+st1FtI7vJ66e8B7JM/ydpGSYagZPqnYDgLopx3D7JnO5Imn
iMJ2n6Wt09xd06ZdZ3ZTpxotc1qvPGBpZzVqknCRx9m2nw2l/jY97yZn9W4b0oS+uDtA136M
qj/0J9nUvCMgm1JFDNjojhfHoKUur2PQjFH71tV4vbqCUF2UPM6Aky7Dj/0L/fJB9AeR4oyX
Jo9Y+7Kmfv1bow7P5ZDSsjyjjE0rj44NriXaR1APPPYodpH9beedBARkEcx5+Oog8t5qySuI
ou4+6WdmwooHmhgoy445mh2i6l/Jh4+RQ8FjoJ0BGkYJtk/6dVR21bWd+UJ2NIY9y6vS17yg
MTYoD2YJMG1MXJ/D5udVvGLrKmsF3xRF7puX9/Z4v9+NyNfcu7ZSWmj9ozI3TKZ5Lcq9Hd0G
ZAiLuQFkSBSmjDWny2WIGCwoPGHXszrWJ8ZYtY/3JrkZwfs3Mfparjq7URbSiedFLs0fZF3m
AjuUGlERt45BBkDCctb3gFNK6eljUHyOXF9SlyFxzjlx4fL7tYlIQe6zzYygGDhmv2u9Zneq
9BhkJDLBrpnz4r+pVznaW5qgnThycK1IHHJJ9qCqGe9PQnDdWWhed3DV7kxpookIDcjr8f/m
FdiMIcw5QxZU3k9MJGAOFyFK+RkwL35ogfrR7q1EIxHJ+bWs61yuUrPIhLcI99lGEXL/RzRE
K05rV9/h7DHovMhXC2JZX3K5Cs0eYWFTtI2760WhMValtJ77wqa9nWmQDJFTJNqcOgaieWi8
q39Sh3/FNCKsssscnOAVnbga8FRp495yeeG47WUuV/L1Ua/nIP9PKNxC9hOpuMPWwMQw++Jr
y+VF4zZ+XK5ojWnPHoYA2qLTiEpnY/Z/HQXPW9ntlAni8M+k82wX5kUCDrLVaaPPZPN4yaEe
lpgcGfKq7WOI/7Cp7va5WRwaIvfWcEfzzQLHWbC44YXJb/2brnEffYYHuKUcRyDlZT2aua9u
MmnzcUnq4VFFcByjDhOq4TW7t+wfezg/Ti8/KHASLEa9CL0sizCAHlzwceSnirjF28WcL+1t
i6UfXAhwODRo3F+NgM+i0I+n30XQXjJR2VPVoL21iDuzxRMdSI732seglY6D8Kvg00duJJ2a
idblg+Jj0DLqzPBB2d0QkqmX4XfVE62OEzFylYvvZqgM97shTjJ+hvY18IBY7ZTdGQbxxaRZ
YlY+aMvGucHhGGTXzFe2qXm5NDFwb7mqEqn6eLNBJgQcX3AGDGF+I2faB/jhWXbV/tSCasiX
O4nZyRVsj60kfra0b/nl7liijYMMxH8laZI6xE0+u7ul/3nUHRpDe+PVgVtT2+3tlpG3u1tK
Gij6hEsb4rR9fLmuQBqVoS2eR/bcbI+cA1N6587aUM5riZht91Vtm1SZxRozjkEgEVh8mLbS
XNwbJ7RPdM8xqPoqOBZgjuvct1Eb1jnSW8JX7TgCb4GX5ZbzNbrn0ywHlnf9DxxuyZ20dBm/
RJ/4UC88+u4IKVl2G75TfKKJLRMY84A0Me1xei8CvYySb4tYI3U+k46I9zd8hTPJl0h+ciDl
8Hwv7N6mx7Jhb/pEFqfvwgjPSkE9YVn5Wuud7aSF04pKLbOBPe7HoOFww6IJj9BnwZJH8H1m
T8oW5GudCtljEK9hrKloYkrNXlgR/6pgGyZTmhG2GlQpCx66CA4YszKcoc5WZeyHTCzoWGmh
SW13UZVhS7SEqc1bG/mRc9EevKdfPDgYyxEsjItna9SWcM9w28o34PyXSKMJynTZXRQHIfuS
NCHj5TwPqCTA7jhNwQMHbkkacVCyc+3YO3T3qWrhbSFO3VsmNru/MFrplYgsvUIElIP+p4S0
EDBnvHGH3iV3061VjlFwZdoaClvYQtwJ392JCxoG9nOsVqMjTs2vrCvAcHX1NTCO3WcpGJ9m
KuhAbatxoXjtadEXbmgsy9kKgrwk5650QzbmjXq0RK2ujzg4YXXuIxbS0YlLaNQSUn8cNz8X
uXEQFji1y++tciqacJoSyG1bZPa27qEvvFo/Bslt93of7vBYMYJ/RhZP6EaBb8QEv58Y8B+Z
SBK+tvPT1o/z/nPDD/ny6229VQ7lTrzkUcpSM+C2qVUIKRb5erUlDjaDH2nDwD/wHMxXJ9xg
oAVNnhQ7wgylkhvnEsbeo5TAEpFaJzomt3QaiVHvB0k5HVTkQmDQqSDYWt8dD19JBwxgzNuZ
BitvlEbP2pQvxkFdTPl1eU29M1s357A5gHJhKaZuw6fpf4YmplycfW10JbTkfljb7VX8twuW
fR709aXSw/FvAd0v61b4o1mqsLyWXtF0H4c9G7AvOnEo/VHYv/0HvkWlmXmf8G13nu6qmwN4
QfFE59KYdozMx9XoHsTnPzHAicvpAXYdaNS81U2hcoHHCJu3ww/a55h34MwDcKHVMagh+up8
YGhyV5FJJLHbR8iHSONApfjswaQnAzH+czSLqjbfwxNTbWfcDvYcAfP74O6OHwHUFax3suXj
tAJ0xFn4G8s8Vb93QTs8gAKgt0DVJJqDTvEetCwzry3lCLD+c8X9n35HKCohmOu58R3idpCs
PEdGJWRxBOySg3qqJsHZs53Hy7/aG52hnbMbfYVRhV5XSMwVfpin93yxsrtbdnkvO7Y7bFO7
yh0/b7LfoC+n8ZZV0ik2ml/tASzIum5Jff9u716fpc0Y10gVVvvO/CDbe/tIwo4ws1X4o7zv
+nKqon91guJlbArFu0pYod7OTevM4xl9WDwEXf9yDXx2VS07m7B3r2Lmp2nbLCxD4m1Pt22W
Z0XRuPQeU8ztFQXqUg74Tx2DVKagV7Xw9w/E0+omztZmZ5b2wNLSSn0dnexERz05UcjbTOAc
gYm1Kq3m+re/hyb6g9cfdBP/g7X9/ti2a1sbeZaM9qdii7+RE7YYZjqFaGYT33b3gxMlUxBV
RNAU18Dqfa+Foq6wVBAUz0+UKfGCT0w8O89Hqsa984+IRmVrxOl0ldPG+QON+ITeZ3G6m4+7
CB0cuJqrGvolsJiD+H8AGx/mhmZnikkYBk8NRvHbidWvfl/JWXj82bVgfneDVc85FXsM+qkV
x2DBQNOhqJBNm6yJtvXTlqXUHRMWMzEMdaJ1fCmxg8KrN9qTQCgdpLeW28puG9qCtmg3EOY+
vU2nSoZZo+1bz1DlSz919LojzngACXVVU52CtLCX+t+cO0Sf1uYcqc8MJp5ZAiTIi/Zv9RO+
81yObMgMnqONwS/OrG39Oju6myhRvEqWq1xmKK2WPQrJNZU2NKdOtPogVwBr8/B2uTZzueK6
AXlM3NCBBE+22J3OerU/qusG9lqZgibR4eZgOMSuRfhye03Z0gD/PSDNzsZ4Y7I2LqQMHhjy
4gB51ggOKBQjRWGebHz3YPBI91CKOvJMTmY1xUQEEGitR1zLAWZzOcf5bsgu78/B7/D85JkM
NpE3X4j2GM0RlMz8sOwHCLm4Fv8dClKSGOR6AF8SlIx6npVbTsnwWS7GOFNyz9lQJT+IwNyE
8Amlead8RkbcqMwmdtVzbHhcVW75uVhjsNfRu2tct0VkVXtXzKMBNi+oyg3C+VHkacP9/D4l
LvgnHSd0yTM39MwLWVydHHJ4XxjiK7aymF2y9wGFW7zX4rsvbBJE2glP29ib3Ib3n07V3JQO
HR1YWSKJ7l1bqipWklCYNWC8VRp534VuFLGKF93rl/tzm1UWuA/smnDRVHfr+5kXcVVp5K/j
88IU9soA3SmloLG9a6+8eZSSn1vNp13cgvdDcvb2PcQMguADd3zaD1STFqqKs7X7Nxvkgxuq
sIMRXx6DPB+hjkGX7fISefHvqzbwJUefy2GelPdCjkyn4HsMW/7PgnPKXJtjkI0BnK87mPgs
aROlwrU9BlnXOkHq6u5v/SmaZp7hn7hEPV26C7/J/0VEcpHQ6xpDxJxe2HWB8P5k4lO8pls9
P3aoiRkLXFu8tVH0UJrRnh8R/DE+3UObd9FEqUROT3OeFaeP8YJ3A8rcV4u03hcxhHEZm+qK
2wDXveBKuPd8XxwPsCh7jQxpUYuT+ow0w34Cx3c3++5ExFEX725mAOt2G0zEep9poYc+UORM
8YJu5sK4tCb6X6oE7rvSgSZUGnjI1Y0cgz7cm5MRNyzDHINcg99BIiJEFq8eHb5E+EOWGKch
bb+3KYH/YxXgZbLFTU6ccbPkfSn3pAxABPyviIgML5b1aiRmTByqPOBJYQHIZNlGl7jaENVp
fSE/nuvRXxKHJ+XMZcRIaZinIZD7Z4/ULcKPQTVXTbfCb8ysHNakHkJKh8v1Eh/cjX21mNn+
1b6PxI5OrDhXae+VYEPGA9ZtTOaMXg/a64Jy4llZNko+xDPBJp38g+lD6VzBd0UPTKyB+1gG
2gvagWkDEu4fmgEJQ2NoL0sqoOoHmYpEDR5i5LbO7+gYDxz6mg7xZFaXML2kX/uX0KuR26NU
9N34SN6FAO3N8dvrZTy3MjcPTrBIvIzQZunsfgFBtq0XsPAGCb4zOk9nc78TXQmsOowGP0T8
mqND217Qhq+282k+rVRi/k1D14T7ZNmi8bR5QVfS8h7lVK8cgnN1tiLcbOpbU4pYG2UijLF+
BZijQi4erGz9MGkK0ZgeOqpaMhW0YdYAq9Itm7k2sEvL+DewLZIjsI550wFORQGbiHJKLdaX
bKpf+W3w20Ruh9vPBdAnDu0xY1bGvC/BBYi0+jLHfQRnGmGzXPfubHyftEBW+yKn60zGuF5U
m+Vy3pjort4t6ayMxwW5zvveTBajAeNBkQsbBpbnmfWZLvtgWfZuAibEm3/6kQh+4ge8pe++
upi3Ky+osyzh9LpIcdFT17SBhUnCKKWwuzxB6FGswkuq/OOFyXDgiEInAb10ixdSdztUP2UT
//kMjHmgTsa5HlTkCqqlDxB/63EfV7krdcaN+saji7QLvy3dpiR/iJnaSTMhB+aRE+8M+JF3
45s6R2aXnxzI/mCImKo4Ao80V61WdoBxMTfm3NHfhNLf06J8lrg7K0lZjXPMbI6yvE7DF+u7
IsT8DwdepyaQlQTQwgbgkVr/5YOmYZewC8T8lqXIS5y1H4Ud2u4Xe+48DJI7yUDq30ObQ/xP
bPf702s55nV+Owqv/69zJAadNKYaxFRHPydq6aFFIzOyarcCMWo9pjfE03YOL3HhovZxQSEL
qWUce5unAIEBFTgRbHrhR1JsSGg72fcjgg5PdmCxJFZd2x5sV29OK5NtEOM/IFr7fjdct0Se
HNw6nPMJDc1vXElPp+im699kSQ0RE136Co38cW2Q+/69eap2oXV+uAV/VXM7sJAZLPRVxoYo
7FrNxT+kB+iczsVXXgi46+oxtPc9cU83m4wMYj6Z8ZfcJYyGLyek5F3G4dRszwMRBv3Wi3Nx
VYIzxfh+zdEyYdxhPZUvQeUQ+SCR7u5j0FQsn5k4CfoHUk/IOWdL8i+FqWT1QGaRrTylOAYF
rMDTpiZN+fR5PK9PvDfH3ZPVbj2SExz8/Ge+u8cx6PTEDuA/DRKcAwjK1ynAcKeugxL+4Rsr
6icikpjSHtNDzKmExUms+yCxTrtiycD5KZgi9cQuP2FOb8U2lPG8EgrE0zbXBoKoC/VA2xHc
E/J/COJPD/0hBBh4jdDTXVRp4ju4aPT9ZtQb4sl48cWe7ha6VrWp6KTd2QFYuDPJSszeTlRW
AsEVlZmPvXqlqqt0Fn3gyIY0mH4HWK+UMb9BOF6v+HvbIgt3D3EJ1wEm+4ySg5lBSJHAZtm+
An/ICL2GvsmPFvnPn7s3ZXppX3GjP+qod/s69jIH8Kj8xmlciFa1OX50NN7I/YPF/t3XkYQL
oaI3s97LcLAbInfWu8pRq+lh7ZMePfQ3m4vt5FFPdTsEp+tV3kx9r7YOLckUlzEgeuXCxT+E
86eHPiHwCYFPCHxC4BMCnxD4hMAnBD4h8AmBTwh8QuATAp8Q+ITAJwQ+IfAJgU8IfELgEwKf
EPiEwCcEPiHwCYFPCHxC4BMCnxD4hMAnBD4h8AmBTwh8QuATAp8Q+HsICP0FOPRqYJtGDQqu
Ukpx8RzapEBhyKtVsGqpZLfF9Wn5FvrUbh4YrECMKZ2pH795Z/Lvlfbp3r9FQCTbjq4zJmFD
LQ+QytA7KawmFsm3tmIHORPMYti4Oqx8Dk/7ol8eNr/Sb0c3SM62jdbUVaw+3NlGsWLCfQGe
Rwa0ByZn8Y3czX9b6v/od9XQYm8PZbDdtouSjZpbdg3Gp6rDQr1xfkT8no4ZdN/zMjbPU2EQ
YPK5onrqf1TTf/GwQLku3j/Gl5nXgJhg7B01HxnbDYSqe3r/NIdQdYmqXmPi/PBj4TAPlD/2
VU4OcAgPKqA74rJ7O0Thu9Kw4IPIpQuZ1/GcSL++j1y1Ocf8J4dZmm4kgO8vUTVqU6Do98rl
xMsrfXniqgsBqHeymHSboh03XmC/3ARME9TIjcmZa7bCB/mbNK4zxWuLBqw4jHtmLbwx7KKh
qUCGtPhYVFnbKMtjxKiVvdCEHcfUamoBgWt9U9WhHdo3E+7+Xr5BfHN9ZEZ/jbXF8pgzOM3/
VS52vqQwQCoX/Vxf+cFJsag8dacKtw0JUupUOrnwIPocggNW3sUualkRWhESyBtvR0ZY34+O
crr4Funaju1duCpPNYZpU9bvZf+vXAIOqCcbUQnrHlnxPmHrE26U4mWnugzxbIsS9KjGjDPZ
tberEtqyp9urYwUQsvutY/1ycPK3jBgvEqX3StrAoqsrwpcQR9+FeTCNevPPG/KylqjZ0xpO
69ixbnpcfEdqGc4TN49rAHtRfbEX9Rv/Xpu+kzi/3z6vfZ2tkP3ST/rm0Po7fgplY4dTSPVR
rwsn1+rcHvCuU5+J2ohSJlnBeuHKKXhF/BbdJsnyZzGjv13wld6mNvwZjjHdaxWvFtgrxRGb
pFs8r/KcoUN5A+dYKXeDh+tpoYzCSNWfws40m6TVgIVsAyIn4fBEl7duJ2OKV2UEQqdREMRy
XkJ5mjaz/afb/QkTDFtt0L9S/3qSs1NZ6iPZ/jX1BpmEtypP4rKkiqrRaTBwjyveWOACoVdC
lYHfSzNpWW+bGz+qPxUVidGNHdeRfDc+bmwZ5VSu5I8oVHCusXlanhcZUZHnNZIfARXI+VuN
8bV0FlphWcP0jh66du8Eea9VnJbUcSHpDKBYtxZYqSoP9pXjjMNho3FF587Sii7KNqTV/Zrg
oUJGS2joHS0bGE9o9amRsxVxgS4FqsrzqfIJFrkAGQ9H1uYUrpSmdeb38NT/31z/xEg+/+EF
hfQfxt3o3zN8T6G3ykTWeYkE+UVtf1VcxpnB20H3yLZH9CjFVIVFOqhinFjBdkE701hGbVZO
hjwsjNVTTo9ZdSe5Mtzstrxx2PgP1iLXE7/vE+TctzuoO1H3DAQyYqJNmoOrnnIyo+I27EJs
S6dpyRay39am5aKSFzP4KrKM6Dw2Nwrzrc7uGsy+/YmoTI+GQ98tA0x21ov1PJxBCFF5DcGa
jtbfvjEYtx2jaxlgB/6e45/njdG/Dy+QciHtZqyO87Kc+7hjRg3UV/BNJxQ2glU+sMIILStf
SXoAkql6D/YnJU96w9LqtacbKC+nh4s2Sl07CwpOlQyVi68l+8cj+CLR24onLrk+374zUgCn
vZ8CDrW/DtZDzHXh8s/n9abOFyrpze7L5x0a5rbifXoB6msxCK60E/rLLy0tLVCbaIxO0hbo
xMe4/rCQ9wh7vSypY9CfdE9tRrjyAtIV/tKc599Dw5twRcE3Iqdjo+HKe8Ncy2T7Vi3RE+19
pQUfQkq1lcT+MqZvEE9EwDQDrJjZuJrExm0TxO1IiptbfeZk71mbvqu63/04uK3mpbf6spwt
aTgSxV7Hz94ew3G6Fhg4HNbbZ0SwR2Q4F+uJ8/b06haTfWY8kBS3Fmba2JMv9mavquK23zvv
nEIFOMXo1y/sLdny9CWMhBi7t6y4qvgrx1lmGVHYEN3bPLUDhMdpH3E5UCDUx6Gqoga2XTDG
6aFVahJKgzUeT2Nb7GBhE68R/0K98h+60T/jr8D3vAaUjRY1MM+HWSuMW0zhuYQYs+dF1lFN
3z77OxV+RpUO2y+5kMn8AfPLpS/uNf6trJa7BkcOeoknI0z4F9a1BQSjESwjXHvv4BpD1w8V
NLxpJToJtbbq8unUtLLvh+4r4rDKxZ+p1ZJ6EzWlQzupUSmuToxtaReutlFQRW5bI9b0+sMA
8Jmqb2KMe7W12T1JZXcFvyXu6s2MorIoPv6rZ25YDKrSYmNQCW49sYOx5/o17WMnWRnuvCqu
xPu4ejeNFMP+lnQidMCc6fwyxOKlP9ohaA5gU6az+UESxvvkgYXP6zf3e+6fiskbOYtMkAho
SCUi/IiY0lkzl96BKigwn3OiMCfjMkcB4Ykf0KGbvpABIBKwiull2zRnOG5q6cn2v6+pj04y
h+RN2sY2NX+c9+o0hF/e7E3w29CJi0L+lh+/lPtlwYy+8SEtZEBFPqr0XERgkN4xKDpdzpLs
cPILHRu2Ir0MLSm6PJbH5l1cLMvFAWPe2zu2h4YTaYw3QpSW+Y68I6gp3Oxs6q6GJwcoSHEc
8C4Y97wyQO24dcGpMaHUtX/dQ0VOzHGMqM+fIGpKhI91hlakNQiWT2/yPczd6h9PwdxEub99
FTXnUpAhGnaHqO5/QU5vHlM16ZK67UYphGnm3p94Gx2+s+lWow3QyINtVM1trewmkyh//ZFP
PHPzN1VxcQH6dNJ6ZLGIjbnHDUXOEWXuUO7uVwJ/q0/8obT/vZn6y8dsWl/CfcplQjfkNIFp
9GthUpa1w0pfK16lJkqe7sb5yc41Rjktov1+GDE6dYlok7AFBz18Zh317+dkoRtp0taj9een
2ianM3a6C+IvIKbguY91dvJWoZGparZimmJuEb06djIzFJjZZ2RWJ1eSul84HZkoShwKCjGP
gAX8MHCZpOs4cOXwcp6qM/qbGIVumFtxQDnFboFzgu6e+I1AKCl6yavHR1pnxa2/luMZvIu4
M2DVbWg0VsfupSLi6KMtpYR4coxXGx1ZH5mzJsa68NOLLYupiIJLRHxIc/jc3J4pdlWxEI1G
vt8+PIWd3eHJStQJSTw4+lp3xRUIC6I4g5B9nmmlrTO5PBrk2O/anid/lFfO3a9/Nw1GV4ge
tLl/HuKTfdS/Lzo91NP7IWwZi9tgk0fJksAEbBWJtNU2H40bm88tGjuw8dsUOPH5m3DsQtqP
rOxqksd0X427w538c9YfBjfxUaRIel0svZRhv++f55uCG6Sx/XAZ/B8ufp0AugI23LgfGCyS
fAGdZlxXVghBTlstVlvZWsXA2TnY3lTFRFjonL2tGDvabaHz61OLG+UPyQvoguv0vectatYV
FDiMPJ4n763m6ZjB15DthZQRzWLkTT1Ue3rttP98f6kOUVLBPj9qjS6dXfDxdsO26anr4vBj
lMgyjtVZWyiUbt/TYmYWlfsImfi5kWnI8gNUgh65VaYVG7wsqJiDL7gx5AP5MdXbuIXhmVpW
PBHNmcWtJctWamoOXxBN6Vf4JfynPUmW/9jum3q5p6Pv24hIatUkFGbacD95NanSoKTfONov
R2Jb+E8haQKuVAT6VLq+S2OB8jJA+abPobsBU1y0vZ3MIVc2+svt6ahTe8lNlRPZr/cKCWGR
fFLyKMJzzk5OxuwwvTtiAKC4Unq7g0/J83m788hzR2OilYpUktqORDrh1V1IQFw6nHLKmpiY
rGMOxl6sbEA//3D89h788duo8eeL6ftvLhO8jI7CNnhPz9lq+qjHxxYu5anb0MyBcLuSowJh
f2jI/uMPnczcjtsqupMwokMjBsvA+sW23k1H0XvkJrd/vnH17xT3RYLBAtdCX+ldFuTLm6cF
7v6NrArHIFy7wWj2yUiEhkB0SDn8Ppn467fwbVXmuR1yqZ+dtqW/oslbFsUeDoXJOvsWkzIG
dGAnTt9dQXy5ud266hllwnH/OpBFCVBkJDm4m0USUpLNdjluB9uRxSwbP44Y+Jwb9nIK5uI3
gvfjRQkqe5GAOtAuHQfNK1acF773spfnh3n+GIUDYgX+fDKoDBiFMJZfqcVM5HJrx7q3fH2F
UGCqiYZHU2krDfl8KvYZvegnlG3Y6aZ4FZWIwMOHYPnF8w5s8mP3LO9ywx21gQV8xQ/YMpxx
oid+tv2pt7xCrU6xp2csNDJHMCC0v8dhby4ttc7n63feVhFMgqsjPXwUb6UXoXo5Z+OpumV+
7xwguyYZZ+myiI/iqlPzh8w42+FRCVG9BGTx26DWez4335M1R6skQnMwJ18dWYXTUP6ltHNm
7a+EfgH5I22LEIhNUtOoZuRTt7NIyox+cLgh55z1uTpPk4TbA+DvN0JgOgNis+vLxd6Kl3En
PssdIdUVISxevpob7+ruJrsd7K6x8lbdSPY9dDeYzdPfZZt3XI2WUP6vJpemNSSJ3nrtUwn9
g/rChKyNwRlPlzXxxTVRfXW46SsCQtGLEtEDTJn1+9cu1qsvYijbrheM7kvsNWEXJQKwyuVW
/cH+NJJN4iA9Yc5hEftqO04qIIPvhzEw/k6p2PLLgLbU4L2BerXbKMJYcyvJcqjFDjIn4F47
0z+RUW86EKq7eg4RZPygNnoDFjHlXG0glX1P1n3LCV/HGcsB5iNEtJ1pvZS3z2sdFWNB/Ru9
HQMRJsZ7udHAkipR9ohEDKV3+RDs4VZu2DzgawDcf1eE8pNd7cZZEhOjll9Hx1a4DkRQxA/d
a0JzMZ/NQcoJoUUbU0x80RYd0HwUr3kWuewtEWMyJsfHpodYWFXbcq89w9oEiWQH8SDSOnIY
4xAnNR0nWTR+TtvKjWwv3PtX3fz/Z7JYl5iXEbd3rcuC9JKTfgx6jii0sx+6onSzlVAy7Uiy
TE3LctnjrY4TJ2nJZvvF117FMis5D4rJ0oaT33aVF/FPOhArWsxQYysjxN9DTDfqymUUWhpi
Z/pOut+rWLvhgkTOt/THfs98qiRM71KimUd5+1MBvoDvsYhobfbHM54gscKPch/D7h38NMhf
vYt4BfpM1YgOrJR6AvEeb+P/glPzILrPDXFs4d0K7/Mdw2HMwZRS+TJsvCMR/OK6fMXXyR+j
fks/HXaLOX8/1Vm34jDWCTYyKpVgVYvvYQHRLsPAdT6d9gOhucAEkodTKSdGF9/69hfQCUZB
1KSl8H7q1HhJc4LC4s7mes2l3LYubGq8WOlsJMfCwjRMbNIVG9+ZsUUXg/Zch8eiXSVZh9SQ
gJD17Mj2+/nP71iRYzTN+i28AUoqp45iJWobA+FXTozhAMecn35zHktn8ea7WKPW60zD3SsR
8WJ6fc+TMpGzlR4EV7i57QoM+ll3nMS0Q2EbWCxI/bJfuB2ibeGjJkGSIDbRwsI/yH9K5m3B
p2whFo+876auvpP+qaO4MrkxyFjdjxCall8KI4ptJjhXb8gn/AK9A23hNQjx7qZ+gJZ+P35T
58zj5oeyt6OwjwNUIlfJEawPFFEktYWi5+2HnavF6DLHsFXCJg3KOHnjaFjLL/fvgnSpRX0w
HbDvnkqZX6ROtx1Fj2+6clSdL3qW9TDPb81gAL5j3A+11QRfL28sp0E/oxDsYOeszgGqOXQn
Bwile3EEn8+y65ry0D8QPzLURgqG37EeppVQfckWPv5qZgeSomj47rPXV/9qLP1zEj4mVBVl
9lQxFXN3VgVwdfIJT1nWPFLSoezr733/Xo2ALOH7ts3ufCydOnXiVvBfZz2xDwMWUHSYrajo
uLdP559OjXBtWg/xxtwvGgwwUYpIT3Zd5ajOOHe25DPGvOPbFhQmp98yYTwmF2N/vv3L2ju1
Br0tHML73koryNldvZKAz3oj7LTN8/wxaIqrZXYj0Qzm5ka1g/7cFndqEtE4N/Mrz0doL+ql
bdq9ewhFvrl9O5rWmYOWfJzwat84CxorKlOGlc/zvGj8OeiEcLzb/o/90QF1Ww0/6clmIwWv
jxtmTQUMD3leJgTA8vxJ5mw/tH5GcVqNvWVmM0E3Zvnz8M+8ja5s2KiEr6uEB5MhigjWMK9X
f+Ny7r67bIQu3Ep0ywSwQFGpnyff/fIL9p026Qz1MCQ5yLk7v86hB19YWdovNlvyYUDzMZgY
04k7BmUPpXoNnqz2HQWX1kY8lBEwbyZlv/J30nu9oclpR625k+xtzc+2V+lCzWIvVitdMqkI
XIUZ2CbVvA2EBqY35/qPW8wMXS7hQg9pQOgO5Zw1cd/cvKD++QebPdEwmJbMPAj0MOO1dJkv
Kf/HCZ18/RvE9HK/7JVbq68IolaG0UTlNAct3AMuq3iWSdBeyEPYTXQiTnx964l1iqtdF7Ey
ROTn3BhtB9NDF2PMZ4O038bC4dZgaPuAeY9HxedVd//qY39QJ8hmVVYeJDbtGdsKlhZXvcyM
5I9v8kUaP7/317n/6vH/XsIpHgKSZ4eLjfHYS7h2659nixD985CNJzKd0VaZnk14hyBXDNcQ
AINsXUJhrHyqypbb0rq3L9ZT6W3LDsZVdJ8/4+rBpxu3H5pnHYOCRXalgEASO2XjkGnVqoO7
01En28fJ1vT8g3KfZZRufSo2TZctFc9CIWCi4565+Jw1TdnXBlf/40rtSxA7oF5lXHpp47O6
gLzqLf/1rVhRSFna+XfFs4nJ+TWrSfCKEfJj1MNYcTYplAP0FDuZeRw21uyq6sx7mXv33uPF
g9Qv+L21tUonlHj6Pdax9MWXO5Rh6xYW6fYwe1q5LjRJAyDU+zoe8U78pPDmVLaYZuBO95DO
ypGE1quMfp1pFiGSluieiK+yrIZ+pnXCWOZbfVkLcmdRSuksXNfiXgUbFdTAHfdMoSw+QCfK
XyPduidbdoDdmVtwQXnSIwOqn8345TlAEgcHrGXKCe17LowTZcPDu2821Txn+qfGKG56i6UM
nM9by4bT3wX21iS9eZeQXBNed7lE5NpASHgPyo9r59+KCxoQXbUDzV8FgRxKczkCYgFhCq2m
5NKR4iFFTD0h//zQ4r6Uatudic9ydi5zQJMGkPzH2A3kbX+DTHuPVhYq6MDOpkilVJHVjiwZ
vyge8d/rZf/jXFI2dO7HmKwDQPMca4yAm9l8ZKZMwK8kJg19pfb3Cj+3N4PpPc8qGrU//PNV
VeG/kdVoItdqIPZ2KLell5keGXTbz+WGQ2c7zmQDVeBSpHFI/fzci5Nb4WGjBsykfOnKROUe
2P75UdL+3jaNrcEi+UgZx0sSH0et/IxoBIH8o+wrBcRcZjMTbnvUmEe9zR91T9CFJXay0v/S
WocFo9PIoZCGz0/+/ANP3nvWZRou9pbtXSWa+F0T1RVVJCN5ztyUjw7IOnp0o9HUkBSpc2i8
vw/b0wuphAEEPgSdlh4aBVSOnWfU6FvP0ongEldGdvmCB41qT4vJz0bA3OzW6BeH1QuMLS/E
cF82qxlr9bhWJ2Eel9Mneq2ic4hv1GCrboRAcRGgkw7GjS2ez8/PKlLzk3zqS7Jy0XegIlS4
5ssGRPXRchbJXGz1MyJoLOFRLul8/fRPwzW65pL5YXbVscQ83wfFtWtbJsqXD0AFQJv/wyX1
xVDJRwKBityDCPpf3NqCbb1BTDDHPZr2QI+u/Ie8f/jv/2bwx3R1YuJLqhAY7xM/fdfsupLx
C8iLBYGd5rKjMdDYTdDnF7mQDrSBicW8RorLAiIYbtv3UbeQ9mrOb9+efd6+9dCJCk8licIW
cfI4+VyOptjcZouA1BTEGoF8HV1aE0a0/LxmfSswvqnUbTBU3f+8rp2PeEGeIifs7HhuTqp8
GUdUe3bzqtJDACvR74cA++GtscFo2GtV95SetuqyZUm9g30/YmS5XgUNWaJXdeQrzxKr/miH
mF2My13M3RdXZAXU9ZW+Yq7JYOvkdx+kUg7E1gRCm0oKkEuW78cNNzxCQ3z+n/beBK6pZFkY
jzIjMy4wDIoKErgyAyqCIrss0auId2SRgRjZFRRkC/u+RIerbEJ0ULYAURhZgoAIGMJiUFlU
loghAglhJ0Ag7FtICF8fGN/MOG/eu+++777/+/++gV+Sc7qrqqurq6r79Omuthu4NVFL6SZ5
J4dKSXxQo5erGKgZqLVYGC1yjIKH9iRh23x/WDlTeLPArL5mJOTxYVywGLpK6/kOXwMzVKRe
3pwpuvYuYE9GOT9/bEU5Nfkxuyup5KjXYZs3b15XoSINcBbm6ihbc/Zpc3FV/bLNT9Pte8pm
FOKkqNF+Zsid6PAXeW47zS0C0lxevy6aMNevQ4lNCqkMCzk4eSukiezh7NPZxYzjJW9TlD+Q
MLenYklu/6rdcAFKoftzqNT/ib9/3XwF9LpIlbrc9JLT8rLF2vwt9QlRH+9rQr4ft7MFHAg2
kuaQlzLF6Lh+rXj422kUz2vKc1oL3xJZQzoLTlx7JTDTjCivDkha6lhoLnQzjj82XPMdM+0a
0bOB6vsyt54q3lsjBj/vAcxuhzx7vC5e03k2EVeqPNQmeYtLe1I24aZiEeTrWs/2KeqO5nbO
7DRXHWfm6J0/mfetbxa8rrn0kfepmFQNxds2VSsRUWAatIFmS0DbkWXOOCgP8vrueYVJLt4/
U/WQfVy6aaEz26yuJgbJCK8+tH9Y3Igmzc8YJHsZJv+G7zKuy1jiK2XLitLcGV+PGVFfN8lb
GfGJWM/d+j26Vik1rh40i5addUvRYDxykiQLg6mP4ye/calWGRaPOV4UYCwx5XZcnVNz8zRN
DMngtrfqGqiwW9RsikgCFtOcvbla9k5CHE5c1Yq1zd+T/RilJeXsgYrT3K97b/hqL1FiLHVF
Y2IotDb196Oc/xmvZRe+WugS6pl3a7D7OMujWk/z3OAZJ7STQavgc5zEwtsCkq1tzdmc1NTF
Tapqc0tvaiLQlxaLqwKGwis3cXLxcJPxOd9tZXrdJCzxrF7ZHPXNqh368qJ9Vd7p8AoQIzJI
+xSIhm/SsORvJQt/G9w1DAfB9UO3MT+4N/aDYPl+pO9AtqdoDTOgLuKo7mB6q7krFE2fHOg1
aDgY2ardMKwPEPhaS4Hy30RoAQC4hXNLM3ZHOJMSJdMg1KpdM/x9WPcbr6Yl2k1+n242LhPp
LPAJO7q6CGLpHwex9Bn3g0Esffw2cngnCKW/tPKYexHEzvciLvX+HDv/6bCz4Gn64dVll16K
EMjXtgSHVxRvXYNFHA+cq8UgoxTtF+732081mQiC4G+184Z/mHrLxfb7Y85Vq3EFWvAV7dTh
5yNvuT/0l9ufq5xWWH4XOspSTGbgFQeLRV0XNfVBgElJ0fB9YX1Iyv2Z3Mu0CbSutuAonK3V
+8IN/5d6zn1USYWKwnJtaN6gzBcFXJFD7is18b4SmH1wdlDxS7rgVIz1hWJHywZ8I5CnvFcP
+c6ACL2gk/bYdDCSYfrVsx2YvzzXWLVryHXC7IHTA1vfFg8F3orRb3joLJjWuze14xHq9WTG
/vDb4/ZLNyZy/TwIzw29XRInrjIE54Mb+t8d4kr7muId5bHDwuluVnp2HtYi4XHzmAO6gxZU
hZa8ARB88jh+WPiecx8Fp1EHjqqS454c2RtUynpTjuitRTisxszZZWGeXw82aPJlkUyfi/Zu
TV0Fb74CsTYyD/6bjnCzWiVTkMQ/ukLKWIrdJCabPnlHkJguyhDJXfIT8j+xTn3TC8+MqfIK
jzJ1j6WacpzkBRCLsiMVlxwSao5mqrANM8Fo2UCtMZiQHx2dmnIdZZ3Wc0kd7RQ0XFFRiHdl
acCvdta/PzppmixuWt6DkxghBk3n6HTYeypE2frC/yZsxYknFnoqvXnEUSLe8NVEfig93HfZ
0TphwY4cUJEV69hFyLtu6flDtSq1Qv2l7aOXLcoTtiXP1NLD9T1PB8wsXcvSvdrT81OHfZT9
Um0L4HjTjLNbiEYy2tPV6rnEtxVzNMz+OG84xxzGnpT1DW7avV3F88qUvrY732rCMGTGu1wx
ODWCpRdTNMG794OK9jg70jfB2hcRWb2DurBD5ppzYwxtIex1nGXaoyKBtQSnjhJTgvJMmNKX
9p4p3Wl40/gk/EEy+m43ns1TMH3DcoyuNA5KS6iK0gq1/npV3JihhaSEkvzNEXKaoebGZLVl
skhYic+d/3g64L/Zpr9G/5fNSIBCNg3a+lljt1aO5egFZ9b2lReC8M0atMoptNL4g7EL4Mmb
3dL+uDPWsSO1KG9iR8Cg5vc95lonb9wdRe939LS1i3VyH8PZEXyrr9r9ZGKgOhoiR0avTgaZ
SfPM9S+d8lSvbp8SuFdgdQaDzTyFhLYyL1Yqx2N93EpyHY2W0hyc5F6RLOqMA+X3u6ZgvzE3
VnsvHfgqYt8UXMkzXC4KJ2xQQxiv7DHQ6qxYzKbh9fwpabEHExaQNtyDOfLOb2Alpof3fd6m
7daX2d2vgQ24HUf3iKnJdzITh9+mkGY6poLDnm+n6eXHzNbvbAPrACxAdWXuI41VevKjsXYn
68DZ9C7X1IxbfP3GJP13NgYXHDlOS4le4NEshLKWi9ul7mWKXeohF3hjznaUFlL1t+CeFVEJ
V2yLEGY9zS1V/hEkW7H5k1/tm5h7Uc19ztyTVEBlv9O4EOVTOR8uobzsb/wGu8XH51BCm+1Y
7hsxsb42oxZoaQdyC2k0Tb6YpB6mRCbON2cYmrd7tsXHxMS7om3JASTwTsscbkVITYmO/vxG
8JfDrtoX+uzkuz7kldpNdhTxL3QHFiL7qSYGFnVmWGO7Qo286NzqYHkSySL40JbX13+lNdCR
hM0ndA+9BmeNTTFyuwiy8Li05/fdhiszv5UxDknhy3LRky2FjsO85O+I89ykQc5rfanus/09
mnzHCE6T7XOMRYkpI29fgKHksnpMb5uNdVdAaDDfqSbOFCxBOKKQamfzpGpFFcvXLGFQBgMv
fI5Aj+ofYRcPu62fm8KF+omzlaSZqsh9fxuu8hi1OT4w+ZZpdT9+Kio5UNSgY0a1mFFisiVc
NaAgAI20MNuFMlC1aEQvmMMfCx0ZLRi7wiQTq8mR05tkL/2qVv+ty82kaj96sPVSxqTshPvh
goskKfAK5lmi02pnahYtWLKGYdFhYZhcZuytyviw5QOqTfH2zOw+xy7zic4mbJ1wzvOYal/s
/RlfB9NSkyuYXVAA71MpX3Dtd2mFo0p9NRDRd0IURx81gwjkMemaBWNPSwdXk06OFmcVq4Ij
R/4yDYX0VgchvR3vhJAP2qfZg4je5PWI3qJvL7JwgszpYr4bOJfwpPDI8OE5cE6CybLlx5De
Sr4gPrZJkDW4RzwUmg1RmjOTERD7/QTskTXYX4Vvz9uychCrzq++XP1AWY/x/QKK8Y3Znrtk
rbOyB4rhDcX4tlHDM8Moo9dBjO9uEOPbx6sHxPg+snJAz7etAHdgzq36ON7x4hvBbdGtlZq+
bnAP6yjqhJu2TNuL8YLsZE0xVmsnMlSyZYq1CdyTNb1ZVSWERfUCfDMICW/Y4zk2Z90F8pn2
t97pIf0iR0TwGlsoBZ0dctNQnPb9wY25Ldke39XEB2BfnQUA2JFjeA06A2As4F+C+Onfktpy
W0rLttbEv4hfdgXh0hO7x81ndYTOFHd2a2Fu9YGI6jkjaPzd/kycfUnFE8SOdyGKY7aUHQi5
l0bfCZJ9XPBRsjJ64UrckeyhIEU0+VF3pWn/2+tBEchePXu6poB6bQ32/gWXi0qfX4Nd6+UZ
Z6/BzgnNFgePCdpKecNta7BHkQ0h9nNtMivbC5be/IT5Tnho/sVIJmJ+r+9SPTh56Tsg5rqR
JMT87sClFz/fvx75UZe/9fWSOkdx5ayuQo6nrspInwmKVDiWKHgvunfsUSs/eFkMN+l23H0N
Vib0MsRtrsoUf30likQYmxO8E7W11Qym51Jqbc27258oLE9HNJpMBh3mRwmpv41IPv+Kv/vG
yL4ffDuch7SOVB5csT0lM20nfM9Hk/IIf6dfZC53zJcTsa12VpCtjHHnY7curSL+liHzwygC
ky+XpwREhf86f8XmLTiF9h0iPzTvKkgZ2ZVNbB22x5d7ibL92QrOQwEye7LHPIcp9Mdw1drn
WYthDMX4EsaIGwVffh6h8Hc9w8PcZxi445ijBb5cdjpTyl+mlEVPf2n4nv5BgSP0MsD5eyl9
j9Lmv4crK5NAPGtw4k++OkKOSErCOorbCU4EN0S2P8XfbQtOBeHS7cH9mcT2l3iN1OZuzGyg
8KxQ0zs944Nzl+d0ZPg1taK94u0f8Fxl52wes1b4Zjsdj0odXZ3eNFqUU8ad1c7ETi3BdJ2/
Z181xSNSX6/BWJOiw8K3x23Pjc2xu1sMSzH2gvNBrQNspOkbt+pmw9L7xWuwA7oK/v5y2UNE
mWN3J1huvW9FO3szzh7mLhmqeM9zJbtXScLp3ufyOHh9ziA/XD2kbLVC+J53dh4Nrz87+FO4
mqv54phwMo/sL1E60rvvGja3PAOBvg6OSbDINduG+Ja8XCX9PFRGPoIJwyBR5wsQ39ZFHGik
Otjiie6i7Fr2585DFfg61wjcVsyOB0GU4/xVS67yYU9CaNji54hb73SdMyfDDvPxe4j+COPc
Lr7GyUG9k9qs0tkwj26/VQ183LJ75MuQeF+iayiyMd4Bn0OdJu+4HmzenphRGdYd3F7DVN2M
iRZO9z80EoLXhKuuMuVM8ItewY3mIkEH57x7VZltfm/WYM4AQn0kQbc74M2Sn9KRlaO62fkU
3busQdDZz2y5v7oHbtY+lwkMhPqot2cxcXUnuF+DZQaBhAxMTYvcygEERkk4Mxq6t6+p2bgX
zcRzhhE1hTIrsjJJMRTU4iyIoX8cMX8iotHCLsQhlLLPIeLvnAyQrdfubzTyI/bHwW9jBTgP
F/tIyU3zZjRUBjviXGyFOk/H14QvsWkqmzClo8ZPFpsnrGZURS4rCTENL5j4H5ybyvi62Nlz
IGLrpsnsAmftee6SE7Og653KGuwzIaYpSt8nf25yRwmq9AGd/zUIrm8XXJ9LIXAO1WRsxb84
r9e+gBnZgte/0AJQ1mA/9undW7jJWsQjhvYXO58unrYFzwolNkxDvJQDcmKUiMGDh60SPqMR
b9IJDoMAZzX9JNSa+TSMbog/0z/EO65vOg/CzT8ma6iMMPjaeGfDt4J7olrj6i1+wYuUHbld
71URjyLfHqf4WsLDc19pL/ql945dn0so20czxDt7NWB8fMk5Qm+Pt/maywhi+8MEw85rMGPh
Cf+fWNmCyOlnGJ9y0bEHq/xKtMsabPTINkS9VdR8X4TAFqHWOy96EzNQaLjihcAo40Hn8Tno
PC5kr2rJlC3ksRIUBp8Jb5PXv5Wc18jz0pv3L2BZ6Vu+StiLnK84/ndM+WuQVMTaD5JEpJET
F1ux4JSr5wnPdEOwSV7Zlygle0v4fpFMQ2t9TcMmrZMlI52kZJmGs6Ddng3uDMNvCXDn7bU0
W65dMv8wGDszG/Y13XfCeagWCLdy4EoYXkijjieZczrigF7ZQs0AQNj0bIInWb/MPxF6cDz8
ueNQxaaHpiVFdtiBGyXpdxcOFKcJ5J29iPb9/lJu+j2pgRavmuraXd+WBuCQbcYBk+bISqcY
jo0RsgeslgDrNro1oQk08Cf26MPUPLE/itY8VX3+i5jPRvyi5tP7Ijr9EVUPpAjrIEIFQUvN
lC0kN4ZvxXJh1cz8SpGZ+uWxJCflkZHmiJz6aPzW4iM/uma2m/foHsqf+0Gc+26kKTqd4aby
k0Ha4uQLanELU+dkeeBLwoL3UK6ccsWsTRWDfA0bnyXvkDnXUxmJuqEYLs89SHlfNOhrVsc8
VrD7yMWieLD40JpjY2YTpM7edZpbfciJoBQyT0NGuBBl710HjLkIXwRH1f2wXUD36yVVf6ED
g31napJgon2iZ/cTIquqnrkt1pooEntsjLGTUbxbxrgok6puW0/e2fM21pUjZmth7sZLq/7x
S8voWLCXYv9+3btibKH59Qr//CVt3iIKnxdYLn9boVWfd233Ajl6xoEWr9/SWT441VNjUOBH
83EIs4Xv8lZH0kNPm15L5XwtRtXz0szNb5qMg7eSA7l3gijWqzNsLyGweQfeI7gGF//Ai1hJ
3/wO0Ygi44Rvg6YVza+1rRFokfmdus6FI2I1Jp95VCz6u63Bljb166GXk9leR9wbSwlXMEzh
vy+QBrD5tauF8Nbsu3ww5CDuu7Cg9W3ZYBfljXBRCGPGt72v6B3WWVWRC3yeR8WrlcztE52L
Pk9zZ0Acco8gykqmiHveIuiZBiM79NyXmSuZX7kHLaKvrp+e98zGb9X0S41vQtWdTGceTGcC
TV413aqxPVQFh2gE3WzHnNBKpoTXoh4uuHS9m3UjRa+abtfyh7fcBpNvLsJFReXpjYLcW+ka
WGdxfQz9Rj/K6vlVsjkwGcPSyDxT3kU9f/98VuiCrl5/WOjxgIcIDiimfN/7EJwwsMMayA4R
ytnADoV+tkPRplxWsuCGVzEfmQfGakKzY9ycNdgDG8U12C5XBPUGl+vHp2Le6e9ag8WWy4zV
RthqAqMWv4nfMGqEMg6c8bLtJWXmwsNVLdGmRyy8INKLCIhhjMGA8L0vONPl5LKt4FA7Iidy
bnaUCwp5qKsMiK+7kJFh4FPAUHDZXnCQIkgTHn43h1yDnQq6LDjYKkgRpTQ9YBULoqYb+eYZ
q0fhiGREi/2qWH/ycq7myiWEwuMpdfy8+S1vXiJu9bBM4gfftKmVI68urr5uFiSJvgHuDbO6
t78sYugqGDIBRUhhvRIkeA0gfI6BQZNQQ0iTryNCcPJVymoj5A7fjB9subcG48qIDC7JKIBh
kfPjZI3ENdgQXw/bHYYdk53JfLqPDqZL7k8LEN6giz4LSCawejB88qXGSfWpMdhMZkl6N0Xg
/GRwSWJqrg/c6jJNcTIOjZNKlJEbg3qXSdV4dSk4wtsNTDWJfxDHjc0hnzp2th0S+MFVPwin
fzln3+U9cS0RTHQ5FyxpmbOau9p4UWuwVaCldtw6vEZ2mWPnu0HBsq5CQaMWlUVbTA+V3CWz
BEjbBr/Ga1SVZ3e+81gfOxRgtX1Z3dZOevFbXgPoQO1SFlPHRy9+cy24Qx0XZzF5EXrxQjJc
QNqS9B6vsfAuu5OxTF462a93kUvDa/DbHDsZnZilTeOZBfxxCi465HSoVOg27hOwoNkzI3/O
W9EI64juw6iJ2iygRgLCus2og52MNMyc7HQBIVlXnDXQui9UytNYcAleWZnr26iPPurYWPJs
njzat0CjKWa6zHlntYdKuf0NDNu/ZMdRjLgV/WITHqDbPYBAKIlnFnPACRJOfpjR6xFWCnr2
jCZB8+garG0Tl3sNGgh7HuGpgoHwaaHZd9wxQY85jw4GwlmbuNdsoMyDq5xrPwOv3x8ih4YY
zp9HgLEAljOCmvI8Cw4EojQhRrJ5wR287veILKCaFNKIoMdfsOSHHX3A55f2BJOJjyg9k2BU
IYNPCqQcBmeYvp+aCv3bOqr2SBJmfix0ifwIYyA8tKA58iNmfhzDP/UIcwZofdpcI2LFHwxg
xFwwbTe4ekbcAfyqzlVM9DxltHYmM2ffNEWQ8XQNVlfpPH8pwvT7yUDwOGTCJQ94aK5o6Trn
2+uAE3Zzb0/NnMlY3SeT2J6dAY4XojY8FBwC6dlguP/jHBGxEtxOrg/BzAG1+8mGYyrILDed
QQvPwfj8kp6AgjnvkQt4R9MXQP5m7ecyVgSGCWlDPMkImTnZ1YQH3bMds7robvMJl2VyMziA
lDdSRNaU1DwNABAQQCh3urilQY+h34B35t6JaNRNX+lgDSzOAYrl/NcITIEjPo3fbdmrOnHJ
jP8O3Gvi2fxui965iUuNcycwF0TPH+J3nx84zNtjDmUTGHnqEehvZ5TDbx9fg6UJrRBW/g7o
IXY6d9ZV8TtlaCfbNciaXy0X6jcogeFxrSDfJGsXl7gG263Q2QjEWCG8cHpBvLiFrFWvX3+b
zLvOX4MFTmaVc4mNkgqd5Tjwul4GPznS7kDWWBj04+10lVk6ydW9xlYHJ5I8rhibPPNo+aDw
0Exg3jBGUDzYQTqeOys0G/SoPYC8BrswA47sLr4gOBFhKraCBSMndtHl8CZ6XfiDoFY++ySg
QNCOWzqmXsH7XnRvj95Z0GssaB7TZ9lVybie5EkV5O/jgjF66Rrsw/ogvZv5t5GWCu0kvKAY
jOqDz/SzkfoevqkxgK7/GmxYeMKt5pxzy2NwqtPqGTL/wexyafvzMDpR1XcNRgGF35Mh7wpJ
oeC+Z/lguIxI7knejGF++hpspLsVeB5NL8wBeDzbBcHtVQUlNnfDVudNzcGEdqt2Jh48ZMA1
88vWYG999fQn+4TI5i4LwZn4Xhhc2Nxl1VCVOomG6RpC0HdZIZiabhh/XgG6awnOwE9pwo72
HHaYy3ZzQdpLqyx3nOmYNyBvDbwqWXYJjKaPxE2NFjfzEYhINpe3+WSI7Iri7Of12kXX5jXr
wzXr68KSowbQy+GCKE8hYuWXqr/u4D+93tXKGlDnjijGqo3ZxWRYBX54OCpzYtkO0bByqFh8
gC+TMIP/C+PF7LLdpauZUWw3Q36Uatvqem1c9eycs5dqRd80sV0M8QqpdAy5+yvRN7SQlLaR
dlJ67hoso0JuOvKl/+Sje2FJ5c0t+q0mZJm/wyuJht9b6Z/z9lU0LU0uxhxAuEAPUsHQgxRj
ZFadxPMRveJtncfB6k8OTgRwV8oteV6iBwaxZnHw8PGG5ZUQ9S95fpFNK9nHYxz5SfzBHXrP
IxpsVithAkLEQyCcb+vsDlIZIzNHTBnPRN+MbMuTQLwBx8eVrervFEid4GcGBi81cvWVpkIi
8Juxr67AxSmNeilrsMOD+mO5Y/N8DEiqrIz1JWNnW4+P+4Xr46PAw9Ni5k/pHCprsPXR5FiK
OP8EGP4rbjwq1Ww8Kl3ha7L1KM9KyGrSCqcGJC5Mtb6llLq23rwQGWnjqqpuGCo+8NjcZ3/e
lDhS3VxFmiWvE/jZNFVVrY5m6pIy2xixemPlY9P8oF8ovgbbIV2/IPedYMdZtT6Y0z4Fuo5m
mGc8Au3ZI3/JXW+3fFGX5AenHfzKw1yH/fuZaU5OzuTM/Kxojqr6CQVcItxS26vPrr602EvT
rJYZuFAgdsZuKvfQB9uJ5ZgpNTOf7haJwnqzWYJOsIPuka15kzviocK/mvrwHsN37Z/HTJZT
+gM37bsulEy3MokvmjRGnO3Wyd3tMUZCjRHvE4Yde8huX/cW2DBKjFGKK2LGqj2hwdnVtSYK
stU5PsUvmSTHGBv5nhB7caL0uK/D4njOcOXqNnXzmQ/uF3MINV+qig/HVjE5quIol+mTpI/1
hsGwcIKUYXr4K8JE93NYw2wzXULliHX70cX74/PD5nnGlG+b4wIOxU5a4yI+M9PLSZPHZfBl
RHRuRZqDGYcVfJOGqVRRIDB8xfaDvMoHMqVvEeeNzYf5qgPIHnDwbMNV76XAk2zSa1G947l8
5x+q0pYwq47nG/ihtatEqnUGgyxXG7a84mFtkssZEhrLzkHo3udjNxc3lhaPmS3OnuQkJHfP
I1l9V+0mh97LrebBm2yVtUdIqEjUZ6NEGb0Lw+91wm/n3/EJYh4I7iQzGqbH/9a46ut9ieJZ
SJIdmvCLG5EHh3o/4ITKFLl9GJl0OPnacnSuZbg3sdiRvhLuSuLhjok+7T3z3H2cq+QbFSDA
XXzD3/NepIDlnDslpW3eeXHf6QETYtmxeaYhqjyLTvzJ+YodefekZU1IKgGXpETdGaS1sITf
6lxNHZpr/izyf/GiC6G5spB3opTNMXNU+DQC7ICao2ePX5JJjMfqh0qM8DqFb/f3U/BfgwON
Z/vg4rkucyMvGvFONMRr0b3v1QjVK07f8DRcBCeCTG5mIWet9LfztOYx4IBBtAf7+bmT1Nyu
+mwumFp09XB9fs5jzHyinyE4EcLuwukX/0gPUeNpSZAnIzsuvOqk8ZOa3+V2UR+vwZjgXOt9
04vkxM7QgGLncyWIWFGkjXJ/BkbhVQ2YEvjJkTIgREV9sWxm/2a60YU2MVpBXb6+gHoRIdLN
1RefACfIbZPAfAVPW971Qgp/uI/VWNDF6EzkX9TbNcurtQYpCS9AykXz9ZTephpKktfuKGSo
jvUWTCyYoryo7UKabbXTuoqieijpQ0lFFiSbolBak/M2+YiEVio5VXhkQWG2HHSPRbsEc35T
rBOCnyYvYNgdL8k9ARlgCIDI17wPOjWc/TZE8AoY9fEzv+eCU8vLp4lLD4ErVhPdOyx33wUA
OG9bg4VclGkRagg+PXwhjP9sunEpP5IPppDuiViMUJoCt6+2FN4ET2YKia0WzpQmzI6altIo
mfrIl8Eaw8eLEcr7tJc0WIcjZHUPDTXeq6zmk7zmut+pZM+As8N/LAKHs8+OPNFrEQHTV3r+
PoZvlewibAMUSD9ZgcMtbW3iZ2+i8Mnhdydd7hnSgcxPc/ULKE2tLUtHQ8Ohs8X/SjpeTGnq
eb+kwsaWn9dT99n0pjAiwj6gkWTQyUNG0uxN0UaKc2CCiBj+dlaOYwNklxF2v2OkTyJm8urV
RnolmADW0pYvHqrY9siwJM/ZkP5c1CBcjfsXkCIaCW8oyWukvxa+PO1838ReO4zSSqtAvNqh
6cmWjC8+NeREDVg0Mb4QSrWgxxHHiyo9WizAtibVnc1Uo2ajurM6lzYc1X8+e6DC4dUpYV9y
Su9XV0RVljFrsvoNQ7tIS2PlaIX2HB2ua1FoMHjxlI//5vRruW1pyiWpXZlxdN3C0YXLXfit
NOtiVGNMFSq/32GA1nNgYaCqTXV4lpET9iBeiVkdaCfo3htaHIrWM7T94Ds+Petbvj1tqoeE
OEPIcS4LztJtg5/lwAafHFUtN2JIolNvYo4cOTSs4e7YSdRUBhsxFnPSXHKr17c6GSadPMCP
myc0Zx8xGphSs7LV4NDTfMqYqSH4rQT2XJvv+YX9cm/0o2abuftH0DTrO/d1Ajh0onGBhbnB
ztPgJVvjtRy5FjH4T0KvgWSkZVp3gzE57fJL0aWD/DQBOAjWyOMceAoQD5eezSvSFd096BEM
hiw3hzisO9dok7c68omqjqlsxeL22MUrVPHJBr/VB5cY1KxkqfnHIcUTdoc8drxAiqlq+ILl
eEuKKzsXcziqCGOkyvzJR9VXhuduV5PHL8zrK0/sOOdpR1Y/o85rr2+2KRamDHgy0gq7OT06
9epGjUFTYt17TOIKx3U8L9R3PJssxj1iB2nuX1R22rXyuLfER5dm5hMTm5+yMHDyiO3xkDsj
3m7fv+wzhC9sk/mxKmngQ2Qxjd7tumAuMxM6IyO1Vzp70C2hzbesrg5FR3+W8EvPBfaF3urR
0XSdEXZnS6mGcvjSnqdoHkHpzdsZKj4t7NC6xhBnWmzWoRjsYaPTYIvzWXXWcScfHTj6swFe
JSsXwZGdy81J/mYnt0Ls5uS4JHjuLRPqMjXOPDs25yVlsuRv/FcMVjjdr3coDa+5yY8caNaK
H3wxkZBefc+c1QfHTrJYlJnauYQMm/tUFmQMw2B+48FcQua+ZJAvEjnZ+wY/eHJEWi/4aG5L
k6Bnye01fnDTiLQ+VxWreYThyZyh8i/pDt4RMXZsaZrsXLpWBQ4Y1RranRg058MtD2egFGZe
DO/7+6wvHG23iK/CWgjA4pE7k6ZyLU0f3i15y2O+0B28q2+a3QLZsleo4Ktgw/38B4a45Phk
wZHrwY1yYQ8N+cxFw+Wn14MN5fgPG3HJHvGCQ89EDwxh712c8xkvQdRLkO/Azd4gDoDxv6bx
TcG3pXxw4ut3pL9huaQJ0RlpLO/BbMI50nfg1ovHP4Vdg/kBcOzBuwAcDo9YmgFe/a222rAG
gjX4qrhnUXO1NqJRnp9ryO/W8uV114OnFlDayP0vgA/E7FiDhV7EL23i7cv0yZaZ8+wnTjmL
cp8EGyp05xvyGRUuvI5XAncZcnvk23RMS9UtTI37EdYL3urZMALIDrrKo71Yz457+xjTQryF
qDGSYd0A2d0FIFvrMo9aK7gGsO++Ja5aa9nz3m/c3n9LBre2vLaN2+S3jatWy9a8d9T1Z7BE
7YtrsAL7bRjIf59YFfzUs+7fKT0ReP5rmfaMtxQAbclb7wymQGcAHjjWO4Oy9c5AAIBpP3cG
Mu34tx2rVhUoXgvoOYRW7mlbAcoosMYmuDJwTnY2974+yoULtw6yhDesk3uaeYF0JXco2K//
76FSp0zBnJ3fbH2TLUKuqWOHXCc9CPQWXaZKNiTzWd1N/dWhUigh7oPQg8ONyWkRhtf5OlhH
tz6oi9EaHry+k48VCgqHN3S9FLjDvZvWYJvGuPAvJw4savTIzF1aNNxUIWX6etrZobGE6AVa
QjjdS/OHe3ys8DMwnYERB03Q+NmyOoBIvNpY8gAs+NYQ1err+OIgF75zYnRR7bA9D0yDf+WV
hNfc9ux2qKQ8aOXgxi8rUACD4mpYku2I6Ra+51V8CxiSd/lgZxtQpkmhVi3HV65h3XoMlQkX
LWiScWSfRn978DORbmx3AXg0Hd6n07+q7xFPHOykHgZzjvfcd8SY4q5eA+DPMJORrRrKr7Ea
re8Gl/Qpq++Cz7ztKmHRrQ5j5qGBxFuNgDasBq1tEEyjge4Z6GTZs8fBz1oTZVZ3kYeE73l4
lMI9SI8a12CGntxNw1JuaEPcCaojmPAiAv2OrwFGcooKkHPAmIUnKRIF95DaglgJQQBbyLrW
xnp/lMwDNzIl2WMqrPcziFpzCEvxHFYDFyfYgh8SnnCp9At+okJ+ATJWl/E34O6KMn1j4Ol5
ZZuIbmcS5kUtIvzLOBluefHj6xErUpKIuVCMJWx1RgLxhLHSKTwVU74aiy28HrFchekcW7o+
fYD7NrwvYlmNPxFaG4C1gnHgTxAnfu3nPrn+1y2LBAXtEGNRH40smM3kmgFV4JEizkQcAJvt
+Cb82yuatTMaWdhtDSvKvRGrVYvTcsQ2YUO2tIh/qN/Se27iq9cFRJycK9JJh6c2/EHk7kDx
WYGbVmgk5gJDa2UL71VpT375QxbS5IoZ/HEn2Ri+cw3miyaMfIjZkua6ol9IXDAqFLV7PwsG
21s4F46VHJugOS3E3aO45hUBL56Th9c1ChS+AsIH9O7mOjGTiIbbNfX4buo2OY9X5Vf9bagL
knJv1HpLe8Da3aHYwXK/pWX6A3HKW6yatVza5G5HT06B2M28QZqJMim7I0CxKmd4cUrNaBEr
wjSbabfhiCH1f0LuMj8bqAWEoDaVUZRJpsXXBAim12D+va+xdUrKhZrgLdRXejKDVT2Ekaj+
FbBTdda2KgCvGdH3Ib01SvKmBG+M3zTYU/yhpuxQOZzvhFy80V793ehYc8+7utftz0xKygPL
41TUzeNj7tvBPV5jrZgrDh249plS/SdqBUEThcxXzPrkMmIrvb1M2nlLsbCc8PkGQv14OL9E
1dhMnA4CYrBSUlJSr/uGfTOoKR60t8p7ibhNMyIiMr+LgBfxnjSNfQM2o8WSXSOOcUhc+oAj
bY578nhY/FzhM1JVZwfhbUNDG/FDpLHaeJpeJesaIXXW/D62P9ipxXwoJTU1qzg+NSXN9bGG
+yfqBoNtueGfN1/o4ckQiL6gR+vp7Qo/jCMuLiVPR8C+2f476H82AUX15r/PMGeAl96vZrd9
fv2fpfMP4MmdK+wd83wlWpDaG/RA7OsvW8dEx7RrV5+wMYEnNKGlRpLOrajvi/bOdozW3H2q
NOCp/5e2HmaQxBTG0sU/hBt4YLbFe/VWzDQfL63Bq3t9KmpfcAywFpXQzEJaffxgckFPluu8
/Demca9eZGHMHOoRe9G6baqMlwVlxuYW3JMf+hhwy+Puvp83ox6q85nHAvRbyX0dM25WJUjN
Y0oUdklJ9f2e2WCH/GklSr593pfo4eS7mUI+xHhPTedr4gXo2MLl3UvyhTt7WgqqAwg4u7M5
9eLDywxvcRX6IbC7/sWTn2UntGsgcNuiwp5Fu+xXAjlOs7Hb6XaOcdWzI23iaki6Ay6JPccg
gfgKHaau+fjDZxUpLcnKK42KfM8OLVReb01ypINLS1vpZNvOVjQ+sJpO0qvO3GmERBf1mIow
w6szbtCOnynMH5V8JlGVNWL3sl1tIi44KFXDdRptWYPOI8SO4b8nuEan4O02XXluWUHyTOj+
rJOPislukxQkoll+ZtL52RrdLY8JLlirI4wqsfn9m7oe/AON938B5F+5KA+w50Ix0/9OY0Ql
Xb2dyKK2KV0csOsCO+JuJMY77Z8sdmLqsV/WMJp8nFLwu1SHc563ie+kWZw9ubOubjFlC3O+
ejAJ84V27ruABf4KZ3TfyaKMqrzOqZn79qTed/6L3FGyGgjHYB5AthF/ty4KIXtuw7C4o6/9
K/caUfOX9S+ZleFpkxxOgNJpu3qymKoxgc3pKdhF+bFSt8d+q/7xlDuoArt3C+ElRa46bva1
VZH5Y9ooL19vdKPrBNii2uYTm92RQ3BS6BR2nw0F+yLtSFH0fQaleDv91DP+1TvArvX4qhx7
Qtqx/dD+b4xaNJfnZ5q3TZrLfyK6wdGvWuj/Odfxmc2CJNsY93DENZ08O1NkfLs7uFjUBx1m
JdCvj3CdOTqOvVukW9YRoFtGCbnGUVE/YfBtU7JyN4FDZxdVslwJhNzqZkqm00kGv2L2YQP6
2tI3o+kqjNILIup+1Lzx4ESNMv4X+InkUNOQqmAHphjSF24vXGZUa3REkala8WUTs1rvVYUa
L3QuxHIabVJY4Fg36GiLRUlJOF0j0kONUPZRPvI69RZLEztqQCsJU/D4yEeXhlzTcjxu6+rq
IHtfvyb7KNFLXaPTCEWVBM5Oqpi4KghRI1dx9AgbOzzIC5seX2qL5I9qxxfWT4pPxZv42d6v
3/GoQn2rBzLCW63GU0p53jrHQZ68memLihRX6QkNmK09BqmFQaA1J+OmkVdxtIT7svZ9/vdt
T5UDuDreA+gurI8reeH9F4WfDcyHdfioR5w/SJ1iTo+2aZ55FOmk7xObX3pXZaFrl2nljp5f
qda/8PJfN8LaHhrovTuqG5EtweL3Wod6UDPUG5Ssnuc6ihxpka4+kN1AM73JeJkLFuJWH1h4
EQ/WKmGOyDBGouyf35YZOZnCqWl7FpiQ6GZP14kz6lBrWkAaP2ZqKvcYx7JS01xj0dapOU7y
8gplXPlNb4F8Nj/T/eA+oXSjuVg84Faqc/2lMUauWfbXvege5XoUu4ipP7zLHN53NFPGjSRl
H8EpbIkKrLd/rx6mO47kcwKKzWxMSWq1Sl+ISPlN6eFL/Oj+GRywQLYmtyMAt3OYTfpQcpgW
4OB0IHYSaaxqAZ79DSNWs8IvOWBoMk2Ni9z+jqlsYe67qzqm4e7xvJuhZp1Vjae6g1KWwgzG
V0weOh9jVmVkhW0llCPNdgWkZFKHOUdFvADXX21rn3O+7D7pF8iU9Mfvwj5e2WY5HYp5a99A
1MxlVu0+JFiWfLxNY/qU7Wvmvt2dUrhjU/HkAk644nEORs+2+5x/M6/UIlLjd/pxbbcV9rsP
H1bJfXzpvEhqG+r9myqMZzBGuG/zidrfQf+TCZ+Ha8q0HKTpVRfzEbJPLv6TVP4RtP9s54Ck
S/sIbt9zWy1NTxf3mjPexOf8uM6LmoU0OmvLLhWxxPvicCs3DpiBovwI4jLmcW1qZbOcXFMJ
+ampsyAY1o7qIfE7TLc0Tr1vAHo81cp0R5ludHlGstugJ9tSTAz1UIXlWBYQk+NGGp52yIue
suBu9l6Uf9lVrUJPi2jslPLddurdfJWZ2+5tX/feMBBjN6+UI1WHQZQ3VwKISOLkdJJyHdRS
RChaKiLQ6VU37sKB2BHL96pqa7AtYdTBxx2GnrM3UIykSSsSsqAMaeBnREWqG7rEYHWNhDxC
UJMTHgWtCe9KUu9KuI93Vt66qw5ifFTOFBQxVec7lMyMwvdeN70E6MsJFwrIWDd3r1w3gxUn
gUlEfh4SrdC005roEA3id6ZWqcDJLgs3xE/gehJC9Diq98JuM8qC1NiMKrNmIkLPyLKhtHf8
MQ3ep5kCqP0P/P3rNtzKJRcmMUipL2xvVB0oVTd/NBmaot4hNiuWGGdrZ/9QNV7m0lcTX5aN
MqtKylsvqEuXj0anFxIrVQ/T3MhJOM1Ceo2BXR3NtnPR5Y5nEBCEYkxrAhlLIpUMNBTHROA+
OPuz9yxOmuuNEXCaTu1GpgUyqdwXNJ6OYU1FYEDUA0ez/p72hcPuOn78BZQy9bQhWbbsotpI
gTKDVOxzuaKUY4lLfMCm2z3Sy66mit81jinovo0NrZCN/prcJhzoaNOmlftkcui0fcn9HPai
khHXNatSmU6yCBVHt5tST3z7FeDoKxWas31jh3Y7s6KzY6zKBHvj0dgCeE+2v6KO6EMIT8GV
is+H1qpvl3DqE8GGenrJRUluMYZ/zlG9NroceJBLL+ynZzn2Xnd+8Gkz79g8bjZmRe8l8mUi
y78KCTm0YqnpyZk60seHnd3zKfA/fV+cM8h9dDyXeH8NFjUkse2fpvMPIJ5Jtia/770lg1J9
PnNi/ze/C8TyvOZMRSPmdnXXlC4j2DfwOzpX5m68ckpBjRq9jkBQblFlpRTxe4vk9b7rk/68
RCOgpE6P88BdCexkbl+C58Y/ukzV95SO4GiMTs3r0KRHPnyepGX4crX4RYSUx+Ru9+6LJT9x
uqWCApxfRBMWzIZJIc97QiZR6igL4CJkm2rXK4Dand6z275vSm2fQedCFy7oQ3lV17KMFF1B
VHFloM4wXy+vylhVhU3Vf3K8I4rXYdn/fIXRfZJBPJhtwQjJ1CiIUQ+7zSwJwN2rN2NTVU1d
sBfkL0kg+2XEFxsltdyIQdmls/nkR+jDUsFJWYqxhFKbRrckNw6riOmN3GWYj1SFAT7g6h0G
lYdIPnkgBjJ421t2OmT2iy1sg2a7jGbTY1YJ6M4W4v3yxSRdj1W5/TS7XdV5RFuk3eucMOou
ZlFFTt6s8U7rO67Vp5sXo6eObYP7uL1MT9jqU/+qB+48uBxvuO1stqIZUW2RcLs5jfCafHpl
zriJZrY6qpP+D7Tg/wWQf52nUS/II28rnrG/J837qc8SV3krJu7MQF3Owekc11dFyt3RWN3m
rrj2OsPkGrOJzc9le3rupr+8NF2QwK1W7k79MFNm901XaYwDh14t6cFOkifVJ8wNYffuVqZz
2B22eQubNICGHAf7YS75wa205CqCMgquOLZG6OtdpMtL06tMAh75pMZJZOkuGN6cWVgE+4dQ
+g8UMThccr7TkKv20jg58X5AVUdRhx67aNhcFQlivjpdkfoLFX9zr64Va8qhb0US3edRTX6j
/9CC2oMLeMJStp7O/kBYg0Vn86YvqkkHNyN2ON/W3d5rc4y4c0XO+5plUFAiKi0dvFtxyF8R
CziA99qVRXZYVB9P6dIoKA+gmRuA+HFqNAPw/lxeoUVF/4GGfa7n0YthVXPqD8crBVf3MDx9
rArQ44FFSHqcxJGO0wwQWeDH/Uy2EhJp90jMvmjbZ+ZIdeoucwsjo8CYmFkjsH50U6y3eQzO
NDJdryMotWZB8ui8h5BIdXUsm7C/IFFsJikvhqt4n6bWZqwfTMjDWuwqHkj+qjzzsLecr7eq
l7nx8VsjNB//c4ujqWlKxoxEC+tccvKLHPmD2IdGQunDgzdT090Hb73pR0unFZ3p+6AyM+uU
kooLuouKuuv7Zi7JhQRi+jzlVAVMMHJohINZsQdjXXJSODvrgrNk4Sc+Vc3/17xnPzFpuK4L
d8qmZ+9qzbaHLiSr+5NzjDkdDQIJ1ZlzEsUxNWuiLRyusT5fpelT6tkNnrjCFrqL8gn5S05X
9jWKBi6O9qMX3mvdfFpa2O9WKWF0te+KTSMxAodykN8Posal5REcyYnVpsllK9e7jjSdH4ni
oR0Ei2BdXV+EVZQuguG7e4mYgzEUmm3X7hcwUsg1NaorWjJJDymii931q5wxfFstv1wkCPOM
dWTK00iQIDyc5/tqlaiCCQ1xnvdCKJ3KlOGQ4ngMKiL7B1uSxEDS0iDqUJVUTLUhbbR9SaLc
JFub5Ddo1RiXqXj+TakhKyA/JzbUGgr8qLM4pW+ZKhy+WfP4i9kqXI1GAq75FoXKWswuKxEo
TCpeyJuyZR5zSyscCtYVyFeOT5MrqvqN6qzvnFrWiPuxJ2wZzO0XYM7O75w0jiPYzXSt7GL0
KBdoOu1XkJMgxcQF6pw2sGg2Vq87beoSTbiTlCC+IDW8O05Lq8N7uTCXE/5XvuFtaqBuQ0ZA
i72OprJpNCHix2G7Ndgd6RbHeJt9bxrTm9FK7k3PDibMBcSHShDkmHEZN657C2eKmFdcjbM7
Mzz4rL3KJ9Ypr/59qaP569QFufqB5bdZzry86BXZeBHflfxJE41rqd1H+wJS8eUBCeGVM+V6
55Rd4s+Zl6J+9DhtpmqiR8gm3xRDImnidKeUtPw72HfoQKPM732X12ANunZ/QXscI3WGiip/
QF9tuidwxuNP1wccHZsaIuwPk0qWaxI7baDKaPj+S9qnNvQvuv/XdQG6RyzL77pW7eaYgah9
TrGjRWBqOccRvMTlDlzaNTySnaR37v6kDpth1/Dta3olLVDdtjSxj3LjgrQ/hQXfXWCblltP
gwdHZxW17apVn20Zr1i6RnbgBEwyCIpZlYdSCGlZoXV1jWkO4HX6I//wurZ5Y8SlOYPIvCsd
McZai4EBnxfL+AxXzJ5mdWITgAPUY0TsQgbrtPXWfC/FKw0mDUdhHMxTy5fnnh7bX9Sbav/h
8EBvggC96Gm8W475017lh43wrS4S4WKEmcgr/VZpYUf23q1QUaIyOqaQrxNqOxLUFr4bPnfz
ePiKxiSnIFqSKT1WnsthOw2nFrSnzbKjS3cGzrXsQqGWjn1xk4XDmRyYc6y51s1Yku+RT81t
eavmIfq187tKf0IOMJhhkk/xFrzIsJ1VleG1nJScFJF70amZbbD0ouSwR84+3JfuYBbgud/b
ksBnq1k0XmdHPsfXhJo/paHCjpml+hRvRdtgv2kMOZgSQ5Rl3tm0JcM82LalD7/vaVDGA5c5
KZ1o0m7/beqM7MGjC9rLE4/BtJHcS4LTAhw9Y2smxk1/rZb+tcybQGS8dWRVqGm/M7ysxtDH
I+N4rEpZi7OIS/F56oThjzjNA0UOR+g5OkGq/QZ+VOnn+rp7fvom+7Jvwdvkr72vvWHsC6ar
IP3q7aLa/bf6TUSvwBUV6juGFkJPqN7OVJ92E5VUPbZMLD18saBpN9qts6xNf6J7QuTHgZHv
0WYVxpGJKF6uA5pj0mxkRQ1odF+ZpI0HrTi/m1+V2ToU/gX+6H5UekKoVnJLa4mnaWuJVOgV
FyI/AkecsJ0eQJ82MuDjMrIbwNI2saHYazEpOTotSAvJ1i8DxkTfmkRQ2nyCcb1pV4NWbvXX
pSsVxodk0hi1BAc0y8g0SX6Caqxm+mOYDVLfCn3im7LfWdn/zOzltaTS91Vurul0Q5XFoOzU
+Gxm9/wkP54s6YcMqV6DyYzGjt7OJ9GVUJgac/iRanPV00amrn2av2f3d/z/0wmbJG3RYMNA
xJ5wm1ZePSz6zidBvYRytCkfImRnU+u712CiL9IWI3LjxMeNebsssaVeu15tlPsZeDf7Yv62
V9OYOuZm6aayBwtXHQZGHHpetjSU38XeRRegHjOzFLOGdxm65oOXUUZGRsA9vBCtnp5/wsQp
INu1MpouxCUWe4TFTl518ngcND3nl586pX8re+jp4RWwC2hY/yzHJpCwWbvYsiY+hKVvQODY
llu02ULRCY3XB1tN4uJsoVrwAmtwNoZqGsevc+6bjJ+7kfFUC6NuHsB6mOrkwWJLVAtEpNMG
q+vNGOXsgQPRmTOD8rpfGeO3Bzk+1dIumS+S9po6WfLTNSs9MBeFddUB07MF92n6VpNIPTaB
NKWqqir79sQ/Len/EuKW4gWZvlbBIF6xsuFdf078heKiAfZFq4xC/bh7Zr7yzILE3QeJ6s3m
6gbqLeFVS/jNDjo0la+lvd8HJk8emla9KVUlFwsWlqCd0LZOLXwlhOqL2/hT9NKdy/TRmFQi
iFputpNGL76dmsJRa741d/0/4O0LzEDHX8LeouGYOc1b2JKiKx7SjiEXu/3Qe16X7kl6wlqt
6nB6vrDsbUvGZtemORByEubBEpwfLv17JKVNm4lKYbqsxFtdujq9nQv0NNf5M6kER6ppll83
COAW0E3JlNe9D96p5Kdiv1lM+eIgyzPRRH22pIjZ2KsTwXJikiI8xniJW7o7biSbYuJjQXBr
+aFGfkYrtUfhxXSW7kGRWBAsoZkjjasKFPTV06vkPFytFktwqEhsZO4gKmLhzYLTwSz5UMNM
5xax4czapKLTIdb0/qTcXO+olOYw3dWWGOTe4yaMLIKnowvRscl4Ii27RtPTXN/KJccpVl5X
eQH4lC9lYbDL6fb9EvWDeFF/9F5vqbO559v8Q+0+9xbfyQTLnsrsyu1dppXNUK75BR0JVHFx
lb9sCeueXx3crViZgy53M3nDlNqsbHyxKm4r5aaEUjP3YDPRNLjEBvhrfDM7NYEWmJojdKEW
BgsPMblLGKcnacQ/dEkNSXiY6nN40MHBkrAw3qHQAkIQiCORpoVi3V+7vJH5TsnxiBl1+VGL
cuqei3sWzBJvlBakEBaBdYwV6BB/jANR88VUkXau/D0xWQ+SpDTcBy2JQMfjLhSagykyAxVj
NXMx+vqmNfgDXVD0J39uHbrVhU6+ni++0/L+CR16XKIgx3VRnXlcYEwqhg/zQHDsGVT1nrT8
LMIxxWW2AwhYnEmVHjjVeDfzwjGuYV9NK9yVkdlaVcBOK+d4fk+OR18D49zhAo1qJH7rfkJe
Dm5nmL+ZuKq66bWEtk1P+j4p/f8Xt2PPVWcxTVEykyhcnUDCxepWrkXAckF8f/9IuOjW1Zis
ygG9s0WuuaNC5ksYA+Utrii0XReIaRyys0NVxU3jtjsvQHBTZadVAbHUgtK2Rcz34fPtPdOF
vqoROHudC5RYwtKqlNjipvse6Bibv7ysQdeMNNgyC9qMlgjxOqJSQi9XpMfjqGKLEdEaUZHp
t2YLayfiJDNb+y/gkx87LhLiUZaEwlOH0gZbbMVDnOKQ4VJ+73Zc/98sV+GWPBd6RHEkxoj2
xHvOazYPh5qZVTL3odEVKMYWNPFdp1eoMJrywXni0BospmOKvYcno+o0MoRUR919puoskQB2
1sEr0Y5tMn/FeYnc6DguO2EUt4B8VrFafMkSfzdb53RpskWoullAu2kNbPBo5b4xP9uYdm2w
jAyaBdX5Doc0ClVNRdGFXSb049OfcKoWZ5eSyNWB4X5Gxhe5ez9Mz7hhrVxKDDQduyt3PO/H
fLZ87oWHvJ/dLq+l0wwtWp1B14v6HByRF5zD6ZrymViVZKdugRZciEolcZhEMNNtbrurDprp
DiIoUMRBOA3LIBIVcw999Ap4SYffzuEwUfJObu0aTC51fDqXgorJfa6HNOI6EQqNmrlDkv0V
lfunKfJ8WtnyCGmeof9IMiEVi7PAhKMLVBY31VqOet8w7uHua76CciO/bis7mFPU08yi0IUd
JoriuqtGiaNvenBTIWirvJTUEoPxPVoLKzMgdCtKb/zODlK/sJLNF30aal39mtvVjDdzLIJ2
q3p04bqIYOp0Ft2CImAfqi+uwCZq/zfrz5+8/SmBPyXwpwT+lMCfEvhTAn9K4E8J/CmBPyXw
pwT+lMCfEvhTAn9K4E8J/CmBPyXwpwT+lMD/mAQwa10bZV0n//yLgH7XPv0TrIFUCOY6Gdp0
+DEbgoX+NoHPxzToF8ABOtfJa+t46yC/+/riZ5x/y/gGulrHg3AREE3o8+u0X67XM/7gyxQG
yhU2h/nBrsJcYGjw7Q6lQB9pC5gPzB+kyMLOg6urMF/wQcMc11OMQY47wHL5OdUX5glgZGHn
YCawixD2lqMwdZgGTBV8q36kKPZ7OlcANahsR/ANUQCYawmfW8CCYV4g9fi/W/anODoA6jTg
xANgoAE/LoAS9CsLOwAzAt9B4IP6+fcs7OA6VVXA1UaOCuzY7649AC2IqjHs8rpUIFpegGog
KAGqpS+ovRf4dwd8Qjyqwo6C7wvrOOd/Bef4Myf+gJ7XurQgziAMFfBBrcOb/8z1hvwswJ0j
7BqA8gTUPWHOP5fw78sb4vHkz5y4ALzL/1bGYZAD8Xd5vb2gEv8GaF4BFKFyfNdL/mNMn3U4
j3VOHdep+AKcj6kQbfd1Pv2AHCDNkAUcXwZp7jAoD6rjVZgSKB+SFqQZ6PVUJ5gTkCakPxtQ
UD56HQ7i89+D2ZCf0zqdX3TvIx+ysCOALtTqkA5B2usM7j/mQmVcA2VD2uX+STokqQ2+fw19
BdTGD8j7tzQgOMd16F+k+1sIX1BTSKp+oK6/lcQG7lWQD/G3IQeIZ6hlHcB/8Lokft8yUIov
wNmQ6a/LhbQbqhHUopAkXQCtjZpDuvBHeBD0qfXyIRyI6lWgC7JAn10A37/gn4WdAe3hC/iC
Sr8KZAthagIuj4FfQ9hZWMi65hisU4BsFpIfGlBwBPm+4BuifRnUbIMvSJoQBUtAa0PnjMEV
pN9Qe29oLNQ2f4xpAuhvWKInaB00KHGDW0jOUO2dwa/fehkQh+KykGVBVxv2a/qz5D0Arsd6
6n9O5TBM69/wT4MyIDlANf3YfhDnzuv1h2qmCnwcZPtPfraoj3mQFTiB9Ms/W8FHS/k9zveA
PmSl19Z1wQdcXwFlQXKEYDvBRwX4UKhGkD9TAa2huX73FHgySDK/xYd0BuIBshaI53+Wjte6
xv/i8f8xXv6jHgOyhY16fqSl/W+10oCp/aZOFuuaCWn2RvtCGgK1xC+tbwEzAJ7vFNBIiNov
+vWfYULQkO/d0JSjoO2g1nMHfQQkSwtQIuRPPi0PwoLgIC4cwe9HbO2fdQ3SSQj/r6CGkIVC
ML/mHrK3APCBdN1pXY9/0ajf8r/Rf/4eyne9npANewAKG94G8nCnYKaAB+jqPNAgyNt5AguG
rBzyxpCPgOxzw06hFMgjQ9D/DKcQntGv2uSXWkE5Z0H/B7UIpPmQH/Va/4ZyNjzPhj+DeFEC
fHxs2Y/W/Fs+Py3p1xRlga4ErdfhJKDiA+h/1FWoV4a0bIMbyOJd1m1pw6f/mgYE8fuxyKcQ
p0FrQr0B5LEhb/VRFz9tQYga5CkCASeeAA6qI5R2AbTNqfUrC5ALjQAg6UPe/GOv+esSIf1B
AWw/0I6ywIP6A03aaD9orAFJDLLr32oLNHb4xSog+AAAd3kdygBoszlIgfpfJwAVCNI/Suev
gB40soO0BdKZDd/z1/Uyf8sHhOGxDgNZxW9bCeLlo3/+23qtofptwEAjgD/S8b8B2Sv9LIlf
agWlHgNWBpUPjbsgvwv1TR892HnAM2RdkA9wXIc6CTiDepoNXye7jvF7KX+0Xchm1dat+Alo
FagUSC+hnhhqDQgqEMhho3f9NBdqze+Bdhutw2kDKiq/4hQNKDgB3qD6brSsD0xhvfVQINVn
vaaQTmz0hZAvDwY8QzkbfeJ5GBLQg8qAfJrJehkQp0eBp9cCPENl/W4sDY2URU4B+NMw+9/k
K8Ncgb44Q/nikI57Ahvwh7mB8lX+GPLjCP3T388hmUMy9f00RzhgvQZQrwhpKijt/6vP9o+e
5co6R1dgykArIJ7/gCchCP7fnnL+COq/nL5pHUMU9tnPT1qbPvn9gwew9eR12M0w2O5PgJbB
090/8jf9D8L9I7T+OZjDAO3r/wIqtEv5JPjcAZ/P1/FOnPj7+u/GkzN4eiX7gfs/aMM/TF8n
8fMXhPuf/UH7cf/9P7F/P3n7HxYNivvsKFA+yHDBtdDG9acV2KA6IgSCHoDL/wMe/xhz
    SensorDataFile = <blob elided: 365386 chars, md5=6bdf4b68>
    Type Image = RLX_056353.jpg
    URL = http://relux.com
    VarID = var1
    Voltage = 0 V
    Weight = 0.00 kg
    Width = 100 mm  [stored 0.328084 ft]

note: [stored X ft] marks values corroborated as IEEE doubles in the binary element streams (Revit-internal decimal feet)

## geometry (parser evidence)
native form markers: Blend x2, Sweep x21
no freeform markers — native parametric forms only
